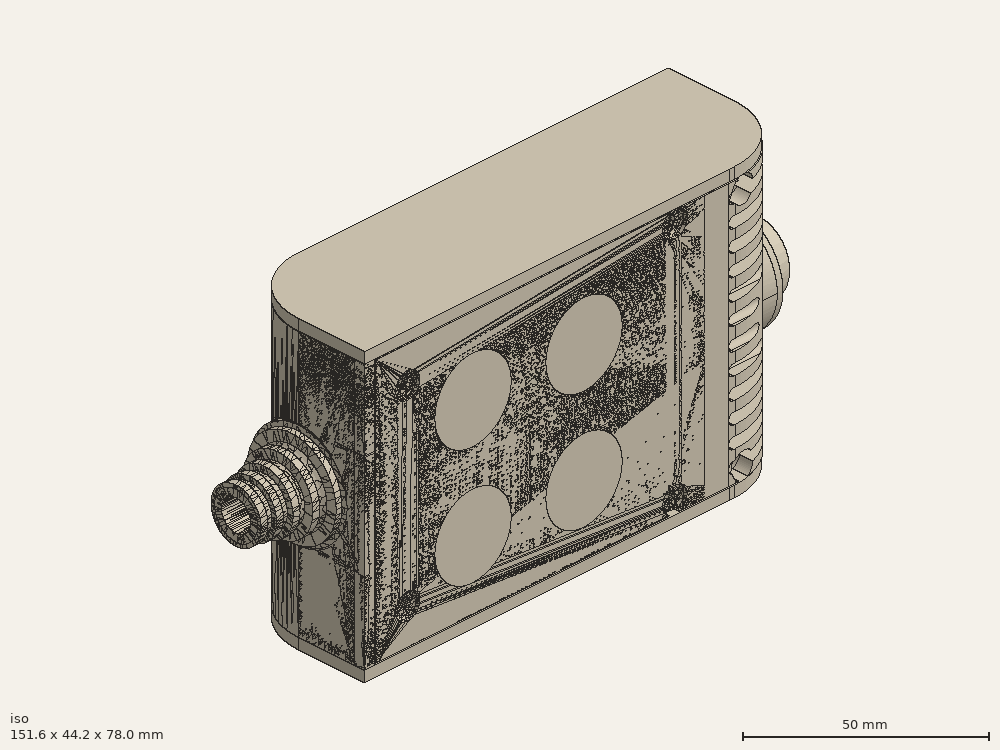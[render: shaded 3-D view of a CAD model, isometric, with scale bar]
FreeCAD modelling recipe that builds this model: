
FCSTD DOCUMENT  (FreeCAD 0.19R0.19.2)
Label: enclosure_177FCStd
License: All rights reserved
LicenseURL: http://en.wikipedia.org/wiki/All_rights_reserved
objects: Part::Revolution×152, Part::MultiFuse×146, Part::Feature×146, Sketcher::SketchObject×84, Part::Cut×70, Part::Cylinder×70, Part::Extrusion×67, Part::Fillet×58, Part::Box×36, App::MeasureDistance×4, PartDesign::Body×2, Image::ImagePlane×1
note: 831 computed .brp shape members not serialized (recipe doc carries the construction recipe); baked Part::Feature solids carry a one-line shape summary decoded from their .brp

FEATURE [Sketcher::SketchObject] Sketch  label="topSketch"
  FullyConstrained = true
  sketch-geometry (20):
    g0: LineSegment StartX=5.21097e-06 StartY=3 StartZ=0 EndX=5.21097e-06 EndY=19 EndZ=0
    g1: ArcOfCircle CenterX=19 CenterY=19 CenterZ=0 NormalX=0 NormalY=0 NormalZ=1 AngleXU=0 Radius=19 StartAngle=1.5708 EndAngle=3.14159
    g2: ArcOfCircle CenterX=19 CenterY=19 CenterZ=0 NormalX=0 NormalY=0 NormalZ=1 AngleXU=0 Radius=16 StartAngle=1.5708 EndAngle=3.14159
    g3: LineSegment StartX=114 StartY=35 StartZ=0 EndX=19 EndY=35 EndZ=0
    g4: LineSegment StartX=5.21097e-06 StartY=3 StartZ=0 EndX=5.21097e-06 EndY=0 EndZ=0
    g5: LineSegment StartX=3 StartY=0 StartZ=0 EndX=5.21097e-06 EndY=0 EndZ=0
    g6: LineSegment StartX=3 StartY=19 StartZ=0 EndX=3 EndY=0 EndZ=0
    g7: LineSegment StartX=19 StartY=38 StartZ=0 EndX=124 EndY=38 EndZ=0
    g8: Circle CenterX=119 CenterY=35 CenterZ=0 NormalX=0 NormalY=0 NormalZ=1 AngleXU=0 Radius=1
    g9: Circle CenterX=121 CenterY=35 CenterZ=0 NormalX=0 NormalY=0 NormalZ=1 AngleXU=0 Radius=1
    g10: Circle CenterX=121 CenterY=33 CenterZ=0 NormalX=0 NormalY=0 NormalZ=1 AngleXU=0 Radius=1
    g11: BSplineCurve PolesCount=3 KnotsCount=2 Degree=2 IsPeriodic=0
    g12: GeomPoint X=119 Y=35 Z=0
    g13: GeomPoint X=121 Y=33 Z=0
    g14: LineSegment StartX=119 StartY=35 StartZ=0 EndX=114 EndY=35 EndZ=0
    g15: ArcOfCircle CenterX=105 CenterY=19 CenterZ=0 NormalX=0 NormalY=0 NormalZ=1 AngleXU=0 Radius=19 StartAngle=5.7297 EndAngle=6.28319
    g16: ArcOfCircle CenterX=105 CenterY=19 CenterZ=0 NormalX=0 NormalY=0 NormalZ=1 AngleXU=0 Radius=16 StartAngle=5.60905 EndAngle=6.28319
    g17: LineSegment StartX=121 StartY=33 StartZ=0 EndX=121 EndY=19 EndZ=0
    g18: LineSegment StartX=124 StartY=38 StartZ=0 EndX=124 EndY=19 EndZ=0
    g19: LineSegment StartX=117.5 StartY=9.01251 StartZ=0 EndX=121.163 EndY=9.0125 EndZ=0
  constraints (46):
    c: Vertical(g0)
    c: Block(g0)
    c: Coincident(g1,g0)
    c: Block(g1)
    c: Coincident(g2,g1)
    c: Block(g2)
    c: Coincident(g3,g2)
    c: Horizontal(g3)
    c: Tangent(g3,g2)
    c: Coincident(g4,g0)
    c: Distance(g4) = 3
    c: Vertical(g4)
    c: Coincident(g5,g4)
    c: Horizontal(g5)
    c: Coincident(g6,g2)
    c: Coincident(g6,g5)
    c: Vertical(g6)
    c: Horizontal(g7)
    c: Distance(g7) = 105
    c: Coincident(g7,g1)
    c: Block(g3)
    c: Weight(g8) = 1
    c: Equal(g8,g9)
    c: Equal(g8,g10)
    c: InternalAlignment(g8,g11)
    c: InternalAlignment(g9,g11)
    c: InternalAlignment(g10,g11)
    c: InternalAlignment(g12,g11)
    c: InternalAlignment(g13,g11)
    c: Block(g11)
    c: Coincident(g14,g11)
    c: Coincident(g14,g3)
    c: Horizontal(g14)
    c: Block(g15)
    c: Coincident(g16,g15)
    c: Block(g16)
    c: Coincident(g17,g11)
    c: Coincident(g17,g16)
    c: Vertical(g17)
    c: Distance(g17) = 14
    c: Coincident(g18,g7)
    c: Coincident(g18,g15)
    c: Vertical(g18)
    c: Distance(g18) = 19
    c: Coincident(g19,g16)
    c: Coincident(g19,g15)
FEATURE [Sketcher::SketchObject] Sketch001  label="bottomSketch"
  FullyConstrained = true
  sketch-geometry (32):
    g0: LineSegment StartX=3.3 StartY=-6.03275e-07 StartZ=0 EndX=98 EndY=-6.03275e-07 EndZ=0
    g1: ArcOfCircle CenterX=98 CenterY=19 CenterZ=0 NormalX=0 NormalY=0 NormalZ=1 AngleXU=0 Radius=19 StartAngle=4.71239 EndAngle=5.71103
    g2: LineSegment StartX=6.3 StartY=8 StartZ=0 EndX=3.3 EndY=8 EndZ=0
    g3: LineSegment StartX=3.3 StartY=8 StartZ=0 EndX=3.3 EndY=-6.03275e-07 EndZ=0
    g4: ArcOfCircle CenterX=8.3 CenterY=5 CenterZ=0 NormalX=0 NormalY=0 NormalZ=1 AngleXU=0 Radius=2 StartAngle=3.14159 EndAngle=4.71239
    g5: LineSegment StartX=6.3 StartY=8 StartZ=0 EndX=6.3 EndY=5 EndZ=0
    g6: ArcOfCircle CenterX=98 CenterY=19 CenterZ=0 NormalX=0 NormalY=0 NormalZ=1 AngleXU=0 Radius=12.7 StartAngle=4.71239 EndAngle=6.28319
    g7: LineSegment StartX=94.7 StartY=3 StartZ=0 EndX=8.3 EndY=3 EndZ=0
    g8-g12: Circle x5 (B-spline internal-alignment scaffolding for g13; pole/knot coordinates omitted)
    g13: BSplineCurve PolesCount=5 KnotsCount=3 Degree=3 IsPeriodic=0
    g14: GeomPoint X=98 Y=6.3 Z=0
    g15: GeomPoint X=96.3938 Y=4.71946 Z=0
    g16: GeomPoint X=94.7 Y=3 Z=0
    g17-g23: Circle x7 (B-spline internal-alignment scaffolding for g24; pole/knot coordinates omitted)
    g24: BSplineCurve PolesCount=7 KnotsCount=5 Degree=3 IsPeriodic=0
    g25-g29: GeomPoint x5 (B-spline internal-alignment scaffolding for g24; pole/knot coordinates omitted)
    g30: ArcOfCircle CenterX=98 CenterY=19 CenterZ=0 NormalX=0 NormalY=0 NormalZ=1 AngleXU=0 Radius=15.7 StartAngle=5.81226 EndAngle=6.28319
    g31: LineSegment StartX=110.7 StartY=19 StartZ=0 EndX=113.7 EndY=19 EndZ=0
  constraints (41):
    c: Horizontal(g0)
    c: Coincident(g1,g0)
    c: Block(g1)
    c: Horizontal(g2)
    c: Distance(g2) = 3
    c: Coincident(g3,g2)
    c: Vertical(g3)
    c: Coincident(g3,g0)
    c: Block(g4)
    c: Block(g2)
    c: Coincident(g5,g2)
    c: Coincident(g5,g4)
    c: Vertical(g5)
    c: Coincident(g6,g1)
    c: Block(g6)
    c: Coincident(g7,g4)
    c: Horizontal(g7)
    c: Block(g0)
    c: Block(g7)
    c: Block(g3)
    c: Coincident(g13,g6)
    c: Weight(g8) = 1
    c: Equal(g8, g9-g12) x4
    c: Coincident(g13,g7)
    c: InternalAlignment(g8-g12 -> g13) x5
    c: InternalAlignment(g14,g13)
    c: InternalAlignment(g15,g13)
    c: InternalAlignment(g16,g13)
    c: Block(g13)
    c: Weight(g17) = 1
    c: Equal(g17, g18-g23) x6
    c: Coincident(g24,g1)
    c: InternalAlignment(g17-g23 -> g24) x7
    c: InternalAlignment(g25-g29 -> g24) x5
    c: Block(g24)
    c: Coincident(g30,g24)
    c: Coincident(g31,g6)
    c: Coincident(g31,g30)
    c: Horizontal(g31)
    c: Block(g31)
    c: Block(g30)
FEATURE [Part::Extrusion] Extrude  label="top"
  Base = -> Sketch
  Dir = (0,0,1)
  DirMode = 2
  FaceMakerClass = Part::FaceMakerBullseye
  LengthFwd = 72
  LengthRev = 0
  Solid = true
  Symmetric = false
FEATURE [Part::Extrusion] Extrude001  label="bottom"
  Base = -> Sketch001
  Dir = (0,0,1)
  DirMode = 2
  FaceMakerClass = Part::FaceMakerBullseye
  LengthFwd = 71.4
  LengthRev = 0
  Placement = pos=(0,0,0.3) rot=(0,0,1;0rad)
  Solid = true
  Symmetric = false
FEATURE [Sketcher::SketchObject] Sketch002  label="topSketch001"
  FullyConstrained = true
  sketch-geometry (8):
    g0: ArcOfCircle CenterX=19 CenterY=19.0975 CenterZ=0 NormalX=0 NormalY=0 NormalZ=1 AngleXU=0 Radius=18.9025 StartAngle=1.5708 EndAngle=3.14674
    g1: LineSegment StartX=0.0977805 StartY=19.0003 StartZ=0 EndX=0.0977805 EndY=0.000251602 EndZ=0
    g2: LineSegment StartX=19 StartY=38 StartZ=0 EndX=124 EndY=38 EndZ=0
    g3: LineSegment StartX=0.0977805 StartY=0.000251602 StartZ=0 EndX=105.098 EndY=0.000251602 EndZ=0
    g4: LineSegment StartX=124 StartY=38 StartZ=0 EndX=125.616 EndY=38 EndZ=0
    g5: LineSegment StartX=105.098 StartY=0.000251602 StartZ=0 EndX=106.713 EndY=0.000251602 EndZ=0
    g6: ArcOfCircle CenterX=106.616 CenterY=19 CenterZ=0 NormalX=0 NormalY=0 NormalZ=1 AngleXU=0 Radius=19 StartAngle=4.71754 EndAngle=6.28319
    g7: LineSegment StartX=125.616 StartY=38 StartZ=0 EndX=125.616 EndY=19 EndZ=0
  constraints (21):
    c: Block(g0)
    c: Coincident(g1,g0)
    c: Vertical(g1)
    c: Horizontal(g2)
    c: Distance(g2) = 105
    c: Coincident(g2,g0)
    c: Distance(g1) = 19
    c: Coincident(g3,g1)
    c: Horizontal(g3)
    c: Distance(g3) = 105
    c: Coincident(g4,g2)
    c: Horizontal(g4)
    c: Distance(g4) = 1.61553
    c: Horizontal(g5)
    c: Equal(g4,g5) = 1.61553
    c: Coincident(g5,g3)
    c: Block(g6)
    c: Coincident(g6,g5)
    c: Coincident(g7,g4)
    c: Coincident(g7,g6)
    c: Vertical(g7)
FEATURE [Part::Extrusion] Extrude002  label="sideA"
  Base = -> Sketch002
  Dir = (0,0,1)
  DirMode = 2
  FaceMakerClass = Part::FaceMakerBullseye
  LengthFwd = 3
  LengthRev = 0
  Placement = pos=(0,0,-3) rot=(0,0,1;0rad)
  Solid = true
  Symmetric = false
FEATURE [Sketcher::SketchObject] Sketch003  label="topSketch002"
  FullyConstrained = true
  sketch-geometry (6):
    g0: LineSegment StartX=19 StartY=38 StartZ=0 EndX=117 EndY=38 EndZ=0
    g1: ArcOfCircle CenterX=19 CenterY=19 CenterZ=0 NormalX=0 NormalY=0 NormalZ=1 AngleXU=0 Radius=19 StartAngle=1.5708 EndAngle=3.14159
    g2: LineSegment StartX=117 StartY=38 StartZ=0 EndX=117 EndY=19 EndZ=0
    g3: LineSegment StartX=98 StartY=1.0161e-12 StartZ=0 EndX=5.22862e-06 EndY=1.0161e-12 EndZ=0
    g4: LineSegment StartX=5.22862e-06 StartY=19 StartZ=0 EndX=5.22862e-06 EndY=1.0161e-12 EndZ=0
    g5: ArcOfCircle CenterX=98 CenterY=19 CenterZ=0 NormalX=0 NormalY=0 NormalZ=1 AngleXU=0 Radius=19 StartAngle=4.71239 EndAngle=6.28319
  constraints (16):
    c: Horizontal(g0)
    c: Distance(g0) = 98
    c: Coincident(g1,g0)
    c: Block(g1)
    c: Coincident(g2,g0)
    c: Vertical(g2)
    c: Distance(g2) = 19
    c: Horizontal(g3)
    c: Coincident(g4,g1)
    c: Vertical(g4)
    c: Coincident(g3,g4)
    c: Block(g3)
    c: Coincident(g5,g2)
    c: Coincident(g5,g3)
    c: Block(g0)
    c: Block(g5)
FEATURE [Sketcher::SketchObject] Sketch004
  FullyConstrained = true
  MapMode = 3
  Placement = pos=(0,0,0) rot=(1,0,0;1.5708rad)
  Support = -> [Extrude]
  sketch-geometry (8):
    g0: Circle CenterX=80.351 CenterY=-67.6202 CenterZ=0 NormalX=0 NormalY=0 NormalZ=1 AngleXU=0 Radius=2
    g1: Circle CenterX=80.351 CenterY=-67.6202 CenterZ=0 NormalX=0 NormalY=0 NormalZ=1 AngleXU=0 Radius=3
    g2: Circle CenterX=80.351 CenterY=-4.92017 CenterZ=0 NormalX=0 NormalY=0 NormalZ=1 AngleXU=0 Radius=2
    g3: Circle CenterX=80.351 CenterY=-4.92017 CenterZ=0 NormalX=0 NormalY=0 NormalZ=1 AngleXU=0 Radius=3
    g4: Circle CenterX=23.851 CenterY=-4.92017 CenterZ=0 NormalX=0 NormalY=0 NormalZ=1 AngleXU=0 Radius=2
    g5: Circle CenterX=23.851 CenterY=-4.92017 CenterZ=0 NormalX=0 NormalY=0 NormalZ=1 AngleXU=0 Radius=3
    g6: Circle CenterX=23.851 CenterY=-67.6202 CenterZ=0 NormalX=0 NormalY=0 NormalZ=1 AngleXU=0 Radius=2
    g7: Circle CenterX=23.851 CenterY=-67.6202 CenterZ=0 NormalX=0 NormalY=0 NormalZ=1 AngleXU=0 Radius=3
  constraints (8):
    c: Block(g3)
    c: Block(g2)
    c: Block(g1)
    c: Block(g0)
    c: Block(g6)
    c: Block(g7)
    c: Block(g4)
    c: Block(g5)
FEATURE [Part::Extrusion] Extrude004
  Base = -> Sketch004
  Dir = (0,-1,2e-16)
  DirMode = 2
  FaceMakerClass = Part::FaceMakerBullseye
  LengthFwd = 6
  LengthRev = 0
  Placement = pos=(0,9,0) rot=(0,0,1;0rad)
  Solid = true
  Symmetric = false
FEATURE [Sketcher::SketchObject] Sketch005
  FullyConstrained = true
  MapMode = 3
  Placement = pos=(0,0,0) rot=(1,0,0;1.5708rad)
  Support = -> [Extrude]
  sketch-geometry (8):
    g0: Circle CenterX=80.351 CenterY=-67.6202 CenterZ=0 NormalX=0 NormalY=0 NormalZ=1 AngleXU=0 Radius=3
    g1: Circle CenterX=80.351 CenterY=-4.92017 CenterZ=0 NormalX=0 NormalY=0 NormalZ=1 AngleXU=0 Radius=3
    g2: Circle CenterX=23.851 CenterY=-4.92017 CenterZ=0 NormalX=0 NormalY=0 NormalZ=1 AngleXU=0 Radius=3
    g3: Circle CenterX=23.851 CenterY=-67.6202 CenterZ=0 NormalX=0 NormalY=0 NormalZ=1 AngleXU=0 Radius=3
    g4: Circle CenterX=23.851 CenterY=-67.6202 CenterZ=0 NormalX=0 NormalY=0 NormalZ=1 AngleXU=0 Radius=5
    g5: Circle CenterX=80.351 CenterY=-67.6202 CenterZ=0 NormalX=0 NormalY=0 NormalZ=1 AngleXU=0 Radius=5
    g6: Circle CenterX=23.851 CenterY=-4.92017 CenterZ=0 NormalX=0 NormalY=0 NormalZ=1 AngleXU=0 Radius=5
    g7: Circle CenterX=80.351 CenterY=-4.92017 CenterZ=0 NormalX=0 NormalY=0 NormalZ=1 AngleXU=0 Radius=5
  constraints (8):
    c: Block(g1)
    c: Block(g0)
    c: Block(g3)
    c: Block(g2)
    c: Block(g5)
    c: Block(g4)
    c: Block(g6)
    c: Block(g7)
FEATURE [Part::Extrusion] Extrude005
  Base = -> Sketch005
  Dir = (0,-1,2e-16)
  DirMode = 2
  FaceMakerClass = Part::FaceMakerBullseye
  LengthFwd = 2
  LengthRev = 0
  Solid = true
  Symmetric = false
FEATURE [Sketcher::SketchObject] Sketch006
  FullyConstrained = true
  MapMode = 3
  Placement = pos=(0,0,0) rot=(1,0,0;1.5708rad)
  sketch-geometry (8):
    g0: Circle CenterX=80.351 CenterY=-67.6202 CenterZ=0 NormalX=0 NormalY=0 NormalZ=1 AngleXU=0 Radius=3
    g1: Circle CenterX=80.351 CenterY=-4.92017 CenterZ=0 NormalX=0 NormalY=0 NormalZ=1 AngleXU=0 Radius=3
    g2: Circle CenterX=23.851 CenterY=-4.92017 CenterZ=0 NormalX=0 NormalY=0 NormalZ=1 AngleXU=0 Radius=3
    g3: Circle CenterX=23.851 CenterY=-67.6202 CenterZ=0 NormalX=0 NormalY=0 NormalZ=1 AngleXU=0 Radius=3
    g4: Circle CenterX=23.851 CenterY=-67.6202 CenterZ=0 NormalX=0 NormalY=0 NormalZ=1 AngleXU=0 Radius=5
    g5: Circle CenterX=80.351 CenterY=-67.6202 CenterZ=0 NormalX=0 NormalY=0 NormalZ=1 AngleXU=0 Radius=5
    g6: Circle CenterX=23.851 CenterY=-4.92017 CenterZ=0 NormalX=0 NormalY=0 NormalZ=1 AngleXU=0 Radius=5
    g7: Circle CenterX=80.351 CenterY=-4.92017 CenterZ=0 NormalX=0 NormalY=0 NormalZ=1 AngleXU=0 Radius=5
  constraints (8):
    c: Block(g1)
    c: Block(g0)
    c: Block(g3)
    c: Block(g2)
    c: Block(g5)
    c: Block(g4)
    c: Block(g6)
    c: Block(g7)
FEATURE [Part::Extrusion] Extrude007
  Base = -> Sketch006
  Dir = (0,-1,2e-16)
  DirMode = 2
  FaceMakerClass = Part::FaceMakerBullseye
  LengthFwd = 2
  LengthRev = 0
  Solid = true
  Symmetric = false
FEATURE [Part::Fillet] Fillet
  Base = -> Extrude007
  Edges = 4 edges r=1.99: [Edge6,Edge12,Edge18,Edge24]
FEATURE [Part::Cut] Cut
  Base = -> Extrude005
  Placement = pos=(0,5,0) rot=(0,0,1;0rad)
  Tool = -> Fillet
FEATURE [Part::MultiFuse] Fusion  label="pCBScrews"
  Placement = pos=(-2.5,0,72.3) rot=(0,0,1;0rad)
  Shapes = -> [Extrude004,Cut]
FEATURE [App::MeasureDistance] Distance  label="Distance: 0.69 mm"
  Distance = 0.685967
  P1 = (24.0138,2.9647,0.3)
  P2 = (23.8901,3,-0.373787)
FEATURE [App::MeasureDistance] Distance001  label="Distance: 0.53 mm"
  Distance = 0.533607
  P1 = (80.2939,3,72.2334)
  P2 = (80.281,2.99661,71.7)
FEATURE [Part::Fillet] Fillet001
  Base = -> Extrude001
  Edges = 1 edges r=2.4: [Edge17]
FEATURE [Part::Fillet] Fillet002  label="bottom001"
  Base = -> Fillet001
  Edges = 1 edges r=2.4: [Edge36]
FEATURE [Part::Fillet] Fillet003  label="top001"
  Base = -> Extrude
  Edges = 1 edges r=2: [Edge1]
FEATURE [Sketcher::SketchObject] Sketch007
  FullyConstrained = true
  sketch-geometry (16):
    g0: LineSegment StartX=4 StartY=0 StartZ=0 EndX=4 EndY=2.4 EndZ=0
    g1: LineSegment StartX=4 StartY=2.4 StartZ=0 EndX=7 EndY=2.4 EndZ=0
    g2: LineSegment StartX=4 StartY=0 StartZ=0 EndX=5.7 EndY=0 EndZ=0
    g3: LineSegment StartX=5.7 StartY=0 StartZ=0 EndX=5.7 EndY=-5.6 EndZ=0
    g4-g8: Circle x5 (B-spline internal-alignment scaffolding for g9; pole/knot coordinates omitted)
    g9: BSplineCurve PolesCount=5 KnotsCount=3 Degree=3 IsPeriodic=0
    g10: GeomPoint X=7 Y=2.4 Z=0
    g11: GeomPoint X=10.4582 Y=-1.55472 Z=0
    g12: GeomPoint X=14 Y=-5.6 Z=0
    g13: LineSegment StartX=14 StartY=-5.6 StartZ=0 EndX=14 EndY=-14.1 EndZ=0
    g14: LineSegment StartX=14 StartY=-14.1 StartZ=0 EndX=6.5 EndY=-14.1 EndZ=0
    g15: LineSegment StartX=5.7 StartY=-5.6 StartZ=0 EndX=6.5 EndY=-14.1 EndZ=0
  constraints (28):
    c: Distance(g0) = 2.4
    c: Vertical(g0)
    c: Block(g0)
    c: Coincident(g1,g0)
    c: Horizontal(g1)
    c: Distance(g1) = 3
    c: Coincident(g2,g0)
    c: Horizontal(g2)
    c: Distance(g2) = 1.7
    c: Coincident(g3,g2)
    c: Vertical(g3)
    c: Distance(g3) = 5.6
    c: Coincident(g9,g1)
    c: Weight(g4) = 1
    c: Equal(g4, g5-g8) x4
    c: InternalAlignment(g4-g8 -> g9) x5
    c: InternalAlignment(g10,g9)
    c: InternalAlignment(g11,g9)
    c: InternalAlignment(g12,g9)
    c: Block(g9)
    c: Coincident(g13,g9)
    c: Vertical(g13)
    c: Distance(g13) = 8.5
    c: Coincident(g14,g13)
    c: Horizontal(g14)
    c: Distance(g14) = 7.5
    c: Coincident(g15,g3)
    c: Coincident(g15,g14)
FEATURE [Part::Feature] Face
  shape: bbox 10 x 16.5 x 2e-07 mm, 1 faces, 0 solids (baked)
FEATURE [Part::Revolution] Revolve  label="plugHousing"
  Angle = 360
  Axis = (0,1,0)
  Base = (0,0,0)
  FaceMakerClass = Part::FaceMakerBullseye
  Placement = pos=(0,0,36.15) rot=(0,0,1;0rad)
  Solid = false
  Source = -> Face
  Symmetric = false
FEATURE [Part::Feature] Face001
  shape: bbox 10 x 16.5 x 2e-07 mm, 1 faces, 0 solids (baked)
FEATURE [Part::Revolution] Revolve001  label="plugHousing001"
  Angle = 360
  Axis = (0,1,0)
  Base = (0,0,0)
  FaceMakerClass = Part::FaceMakerBullseye
  Placement = pos=(0,0,36.15) rot=(0,0,1;0rad)
  Solid = false
  Source = -> Face001
  Symmetric = false
FEATURE [Part::MultiFuse] Fusion001  label="plugHousing002"
  Placement = pos=(0,0,0) rot=(0,0,1;1.5708rad)
  Shapes = -> [Revolve001,Revolve]
FEATURE [Part::Feature] Face002
  shape: bbox 10 x 16.5 x 2e-07 mm, 1 faces, 0 solids (baked)
FEATURE [Part::Revolution] Revolve003  label="plugHousing005"
  Angle = 360
  Axis = (0,1,0)
  Base = (0,0,0)
  FaceMakerClass = Part::FaceMakerBullseye
  Placement = pos=(0,0,36.15) rot=(0,0,1;0rad)
  Solid = false
  Source = -> Face002
  Symmetric = false
FEATURE [Part::Feature] Face003
  shape: bbox 10 x 16.5 x 2e-07 mm, 1 faces, 0 solids (baked)
FEATURE [Part::Revolution] Revolve002  label="plugHousing003"
  Angle = 360
  Axis = (0,1,0)
  Base = (0,0,0)
  FaceMakerClass = Part::FaceMakerBullseye
  Placement = pos=(0,0,36.15) rot=(0,0,1;0rad)
  Solid = false
  Source = -> Face003
  Symmetric = false
FEATURE [Part::MultiFuse] Fusion002  label="plugHousing004"
  Placement = pos=(0,0,0) rot=(0,0,1;1.5708rad)
  Shapes = -> [Revolve002,Revolve003]
FEATURE [Part::MultiFuse] Fusion003  label="plugHousing006"
  Placement = pos=(0,19,0) rot=(0,0,1;3.14159rad)
  Shapes = -> [Fusion002,Fusion001]
FEATURE [Part::Feature] Face004
  shape: bbox 10 x 16.5 x 2e-07 mm, 1 faces, 0 solids (baked)
FEATURE [Part::Revolution] Revolve006  label="plugHousing010"
  Angle = 360
  Axis = (0,1,0)
  Base = (0,0,0)
  FaceMakerClass = Part::FaceMakerBullseye
  Placement = pos=(0,0,36.15) rot=(0,0,1;0rad)
  Solid = false
  Source = -> Face004
  Symmetric = false
FEATURE [Part::Feature] Face005
  shape: bbox 10 x 16.5 x 2e-07 mm, 1 faces, 0 solids (baked)
FEATURE [Part::Revolution] Revolve007  label="plugHousing011"
  Angle = 360
  Axis = (0,1,0)
  Base = (0,0,0)
  FaceMakerClass = Part::FaceMakerBullseye
  Placement = pos=(0,0,36.15) rot=(0,0,1;0rad)
  Solid = false
  Source = -> Face005
  Symmetric = false
FEATURE [Part::Feature] Face006
  shape: bbox 10 x 16.5 x 2e-07 mm, 1 faces, 0 solids (baked)
FEATURE [Part::Revolution] Revolve004  label="plugHousing007"
  Angle = 360
  Axis = (0,1,0)
  Base = (0,0,0)
  FaceMakerClass = Part::FaceMakerBullseye
  Placement = pos=(0,0,36.15) rot=(0,0,1;0rad)
  Solid = false
  Source = -> Face006
  Symmetric = false
FEATURE [Part::MultiFuse] Fusion004  label="plugHousing009"
  Placement = pos=(0,0,0) rot=(0,0,1;1.5708rad)
  Shapes = -> [Revolve004,Revolve007]
FEATURE [Part::Feature] Face007
  shape: bbox 10 x 16.5 x 2e-07 mm, 1 faces, 0 solids (baked)
FEATURE [Part::Revolution] Revolve005  label="plugHousing008"
  Angle = 360
  Axis = (0,1,0)
  Base = (0,0,0)
  FaceMakerClass = Part::FaceMakerBullseye
  Placement = pos=(0,0,36.15) rot=(0,0,1;0rad)
  Solid = false
  Source = -> Face007
  Symmetric = false
FEATURE [Part::MultiFuse] Fusion005  label="plugHousing012"
  Placement = pos=(0,0,0) rot=(0,0,1;1.5708rad)
  Shapes = -> [Revolve006,Revolve005]
FEATURE [Part::MultiFuse] Fusion006  label="plugHousing013"
  Placement = pos=(0,19,0) rot=(0,0,1;3.14159rad)
  Shapes = -> [Fusion005,Fusion004]
FEATURE [Part::MultiFuse] Fusion007  label="plugHousing014"
  Placement = pos=(122.621,0,-0.15) rot=(0,0,1;0rad)
  Shapes = -> [Fusion003,Fusion006]
FEATURE [Part::Cylinder] Cylinder002
  Angle = 360
  AttacherType = Attacher::AttachEngine3D
  Height = 20
  Placement = pos=(0,0,36.15) rot=(0,0,1;0rad)
  Radius = 4
FEATURE [Part::Cylinder] Cylinder003
  Angle = 360
  AttacherType = Attacher::AttachEngine3D
  Height = 10
  Placement = pos=(0,0,36.15) rot=(0,0,1;0rad)
  Radius = 4
FEATURE [Part::MultiFuse] Fusion009  label="removeToCreateHoleForPlugHousing"
  Placement = pos=(70,19,36.15) rot=(0,1,0;1.5708rad)
  Shapes = -> [Cylinder002,Cylinder003]
FEATURE [Part::Cylinder] Cylinder004
  Angle = 360
  AttacherType = Attacher::AttachEngine3D
  Height = 20
  Placement = pos=(0,0,36.15) rot=(0,0,1;0rad)
  Radius = 4
FEATURE [Part::Cylinder] Cylinder005
  Angle = 360
  AttacherType = Attacher::AttachEngine3D
  Height = 10
  Placement = pos=(0,0,36.15) rot=(0,0,1;0rad)
  Radius = 4
FEATURE [Part::MultiFuse] Fusion010  label="removeToCreateHoleForPlugHousing001"
  Placement = pos=(70,19,36.15) rot=(0,1,0;1.5708rad)
  Shapes = -> [Cylinder004,Cylinder005]
FEATURE [Part::Cut] Cut001
  Base = -> Fillet003
  Tool = -> Fusion010
FEATURE [Part::Cut] Cut002  label="Bottom"
  Base = -> Fillet002
  Tool = -> Fusion009
FEATURE [Part::Feature] Face008
  shape: bbox 10 x 16.5 x 2e-07 mm, 1 faces, 0 solids (baked)
FEATURE [Part::Revolution] Revolve011  label="plugHousing021"
  Angle = 360
  Axis = (0,1,0)
  Base = (0,0,0)
  FaceMakerClass = Part::FaceMakerBullseye
  Placement = pos=(0,0,36.15) rot=(0,0,1;0rad)
  Solid = false
  Source = -> Face008
  Symmetric = false
FEATURE [Part::Feature] Face009
  shape: bbox 10 x 16.5 x 2e-07 mm, 1 faces, 0 solids (baked)
FEATURE [Part::Revolution] Revolve012  label="plugHousing022"
  Angle = 360
  Axis = (0,1,0)
  Base = (0,0,0)
  FaceMakerClass = Part::FaceMakerBullseye
  Placement = pos=(0,0,36.15) rot=(0,0,1;0rad)
  Solid = false
  Source = -> Face009
  Symmetric = false
FEATURE [Part::Feature] Face010 .. Face013  x4 (patterned run collapsed; names and placements below)
  shape: bbox 10 x 16.5 x 2e-07 mm, 1 faces, 0 solids (baked)
FEATURE [Part::Revolution] Revolve015  label="plugHousing027"
  Angle = 360
  Axis = (0,1,0)
  Base = (0,0,0)
  FaceMakerClass = Part::FaceMakerBullseye
  Placement = pos=(0,0,36.15) rot=(0,0,1;0rad)
  Solid = false
  Source = -> Face013
  Symmetric = false
FEATURE [Part::Feature] Face014
  shape: bbox 10 x 16.5 x 2e-07 mm, 1 faces, 0 solids (baked)
FEATURE [Part::Feature] Face015
  shape: bbox 10 x 16.5 x 2e-07 mm, 1 faces, 0 solids (baked)
FEATURE [Part::Feature] Face016
  shape: bbox 10 x 16.5 x 2e-07 mm, 1 faces, 0 solids (baked)
FEATURE [Part::Revolution] Revolve019  label="plugHousing033"
  Angle = 360
  Axis = (0,1,0)
  Base = (0,0,0)
  FaceMakerClass = Part::FaceMakerBullseye
  Placement = pos=(0,0,36.15) rot=(0,0,1;0rad)
  Solid = false
  Source = -> Face016
  Symmetric = false
FEATURE [Part::Feature] Face017
  shape: bbox 10 x 16.5 x 2e-07 mm, 1 faces, 0 solids (baked)
FEATURE [Part::Revolution] Revolve020  label="plugHousing034"
  Angle = 360
  Axis = (0,1,0)
  Base = (0,0,0)
  FaceMakerClass = Part::FaceMakerBullseye
  Placement = pos=(0,0,36.15) rot=(0,0,1;0rad)
  Solid = false
  Source = -> Face017
  Symmetric = false
FEATURE [Part::Feature] Face018
  shape: bbox 10 x 16.5 x 2e-07 mm, 1 faces, 0 solids (baked)
FEATURE [Part::Revolution] Revolve016  label="plugHousing030"
  Angle = 360
  Axis = (0,1,0)
  Base = (0,0,0)
  FaceMakerClass = Part::FaceMakerBullseye
  Placement = pos=(0,0,36.15) rot=(0,0,1;0rad)
  Solid = false
  Source = -> Face018
  Symmetric = false
FEATURE [Part::MultiFuse] Fusion020  label="plugHousing038"
  Placement = pos=(0,0,0) rot=(0,0,1;1.5708rad)
  Shapes = -> [Revolve016,Revolve020]
FEATURE [Part::Feature] Face019
  shape: bbox 10 x 16.5 x 2e-07 mm, 1 faces, 0 solids (baked)
FEATURE [Part::Feature] Face020
  shape: bbox 10 x 16.5 x 2e-07 mm, 1 faces, 0 solids (baked)
FEATURE [Part::Revolution] Revolve017  label="plugHousing031"
  Angle = 360
  Axis = (0,1,0)
  Base = (0,0,0)
  FaceMakerClass = Part::FaceMakerBullseye
  Placement = pos=(0,0,36.15) rot=(0,0,1;0rad)
  Solid = false
  Source = -> Face020
  Symmetric = false
FEATURE [Part::MultiFuse] Fusion021  label="plugHousing039"
  Placement = pos=(0,0,0) rot=(0,0,1;1.5708rad)
  Shapes = -> [Revolve019,Revolve017]
FEATURE [Part::MultiFuse] Fusion023  label="plugHousing041"
  Placement = pos=(0,19,0) rot=(0,0,1;3.14159rad)
  Shapes = -> [Fusion021,Fusion020]
FEATURE [Part::Revolution] Revolve022  label="plugHousing043"
  Angle = 360
  Axis = (0,1,0)
  Base = (0,0,0)
  FaceMakerClass = Part::FaceMakerBullseye
  Placement = pos=(0,0,36.15) rot=(0,0,1;0rad)
  Solid = false
  Source = -> Face019
  Symmetric = false
FEATURE [Part::Feature] Face021
  shape: bbox 10 x 16.5 x 2e-07 mm, 1 faces, 0 solids (baked)
FEATURE [Part::Revolution] Revolve023  label="plugHousing044"
  Angle = 360
  Axis = (0,1,0)
  Base = (0,0,0)
  FaceMakerClass = Part::FaceMakerBullseye
  Placement = pos=(0,0,36.15) rot=(0,0,1;0rad)
  Solid = false
  Source = -> Face021
  Symmetric = false
FEATURE [Part::Feature] Face022
  shape: bbox 10 x 16.5 x 2e-07 mm, 1 faces, 0 solids (baked)
FEATURE [Part::Revolution] Revolve018  label="plugHousing032"
  Angle = 360
  Axis = (0,1,0)
  Base = (0,0,0)
  FaceMakerClass = Part::FaceMakerBullseye
  Placement = pos=(0,0,36.15) rot=(0,0,1;0rad)
  Solid = false
  Source = -> Face022
  Symmetric = false
FEATURE [Part::MultiFuse] Fusion022  label="plugHousing040"
  Placement = pos=(0,0,0) rot=(0,0,1;1.5708rad)
  Shapes = -> [Revolve018,Revolve023]
FEATURE [Part::Feature] Face023
  shape: bbox 10 x 16.5 x 2e-07 mm, 1 faces, 0 solids (baked)
FEATURE [Part::Revolution] Revolve021  label="plugHousing035"
  Angle = 360
  Axis = (0,1,0)
  Base = (0,0,0)
  FaceMakerClass = Part::FaceMakerBullseye
  Placement = pos=(0,0,36.15) rot=(0,0,1;0rad)
  Solid = false
  Source = -> Face023
  Symmetric = false
FEATURE [Part::MultiFuse] Fusion018  label="plugHousing036"
  Placement = pos=(0,0,0) rot=(0,0,1;1.5708rad)
  Shapes = -> [Revolve022,Revolve021]
FEATURE [Part::MultiFuse] Fusion019  label="plugHousing037"
  Placement = pos=(0,19,0) rot=(0,0,1;3.14159rad)
  Shapes = -> [Fusion018,Fusion022]
FEATURE [Part::MultiFuse] Fusion024  label="plugHousing042"
  Placement = pos=(122.621,0,-0.15) rot=(0,0,1;0rad)
  Shapes = -> [Fusion023,Fusion019]
FEATURE [Part::Cylinder] Cylinder006
  Angle = 360
  AttacherType = Attacher::AttachEngine3D
  Height = 20
  Placement = pos=(0,0,36.15) rot=(0,0,1;0rad)
  Radius = 14.3
FEATURE [Part::Cylinder] Cylinder007
  Angle = 360
  AttacherType = Attacher::AttachEngine3D
  Height = 10
  Placement = pos=(0,0,36.15) rot=(0,0,1;0rad)
  Radius = 4
FEATURE [Part::MultiFuse] Fusion026  label="removeToCreteHoleForPlugHousing"
  Placement = pos=(70,19,36) rot=(0,1,0;1.5708rad)
  Shapes = -> [Cylinder006,Cylinder007]
FEATURE [Part::Box] Box001  label="Cube001"
  AttacherType = Attacher::AttachEngine3D
  Height = 28
  Length = 3
  Placement = pos=(110.7,19,22) rot=(0,0,1;0rad)
  Width = 15.7
FEATURE [Part::Cut] Cut003  label="top002"
  Base = -> Cut001
  Tool = -> Fusion007
FEATURE [Part::Revolution] Revolve008  label="plugHousing015"
  Angle = 360
  Axis = (0,1,0)
  Base = (0,0,0)
  FaceMakerClass = Part::FaceMakerBullseye
  Placement = pos=(0,0,36.15) rot=(0,0,1;0rad)
  Solid = false
  Source = -> Face010
  Symmetric = false
FEATURE [Part::MultiFuse] Fusion013  label="plugHousing020"
  Placement = pos=(0,0,0) rot=(0,0,1;1.5708rad)
  Shapes = -> [Revolve008,Revolve012]
FEATURE [Part::Cut] Cut004  label="top003"
  Base = -> Cut003
  Placement = pos=(1,0,0) rot=(0,0,1;0rad)
  Tool = -> Fusion026
FEATURE [Part::Cylinder] Cylinder008
  Angle = 360
  AttacherType = Attacher::AttachEngine3D
  Height = 20
  Placement = pos=(0,0,36.15) rot=(0,0,1;0rad)
  Radius = 10.3
FEATURE [Part::Cylinder] Cylinder009
  Angle = 360
  AttacherType = Attacher::AttachEngine3D
  Height = 10
  Placement = pos=(0,0,36.15) rot=(0,0,1;0rad)
  Radius = 4
FEATURE [Part::MultiFuse] Fusion027  label="removeToCreteHoleForPlugHousing001"
  Placement = pos=(70,19,36) rot=(0,1,0;1.5708rad)
  Shapes = -> [Cylinder008,Cylinder009]
FEATURE [Part::Cut] Cut005  label="plugHousingTab"
  Base = -> Box001
  Tool = -> Fusion027
FEATURE [Part::MultiFuse] Fusion028  label="plugHousing045"
  Shapes = -> [Fusion024,Cut005]
FEATURE [Part::Box] Box002  label="Cube002"
  AttacherType = Attacher::AttachEngine3D
  Height = 28.8
  Length = 3
  Placement = pos=(107.3,28,21.6) rot=(0,0,1;0rad)
  Width = 7
FEATURE [Part::Box] Box003  label="Cube003"
  AttacherType = Attacher::AttachEngine3D
  Height = 3
  Length = 6.4
  Placement = pos=(107.3,28,18.6) rot=(0,0,1;0rad)
  Width = 7
FEATURE [Part::Box] Box004  label="Cube004"
  AttacherType = Attacher::AttachEngine3D
  Height = 3
  Length = 6.4
  Placement = pos=(107.3,28,50.4) rot=(0,0,1;0rad)
  Width = 7
FEATURE [Part::MultiFuse] Fusion029  label="plugHousingBracketHolder"
  Shapes = -> [Box004,Box002,Box003]
FEATURE [Part::Cylinder] Cylinder010
  Angle = 360
  AttacherType = Attacher::AttachEngine3D
  Height = 20
  Placement = pos=(0,0,36.15) rot=(0,0,1;0rad)
  Radius = 14.3
FEATURE [Part::Cylinder] Cylinder011
  Angle = 360
  AttacherType = Attacher::AttachEngine3D
  Height = 10
  Placement = pos=(0,0,36.15) rot=(0,0,1;0rad)
  Radius = 4
FEATURE [Part::MultiFuse] Fusion030  label="removeToCreteHoleForPlugHousing002"
  Placement = pos=(70,19,36) rot=(0,1,0;1.5708rad)
  Shapes = -> [Cylinder010,Cylinder011]
FEATURE [Part::Cut] Cut006  label="plugHousingBracketHolder001"
  Base = -> Fusion029
  Tool = -> Fusion030
FEATURE [Part::Cylinder] Cylinder012
  Angle = 360
  AttacherType = Attacher::AttachEngine3D
  Height = 20
  Placement = pos=(0,0,36.15) rot=(0,0,1;0rad)
  Radius = 7
FEATURE [Part::Cylinder] Cylinder013
  Angle = 360
  AttacherType = Attacher::AttachEngine3D
  Height = 10
  Placement = pos=(0,0,36.15) rot=(0,0,1;0rad)
  Radius = 4
FEATURE [Part::MultiFuse] Fusion032  label="removeToCreteHoleForPlugHousing003"
  Placement = pos=(70,19,36) rot=(0,1,0;1.5708rad)
  Shapes = -> [Cylinder012,Cylinder013]
FEATURE [Part::Cut] Cut007  label="bottom002"
  Base = -> Cut002
  Tool = -> Fusion032
FEATURE [Sketcher::SketchObject] Sketch008
  FullyConstrained = true
  sketch-geometry (54):
    g0: LineSegment StartX=-4.2 StartY=0 StartZ=0 EndX=-6.2 EndY=0 EndZ=0
    g1: LineSegment StartX=-14 StartY=-18 StartZ=0 EndX=-14 EndY=-26.5 EndZ=0
    g2: LineSegment StartX=-4.2 StartY=0 StartZ=0 EndX=-4.2 EndY=-13.4877 EndZ=0
    g3: Circle CenterX=-4.2 CenterY=-13.4877 CenterZ=0 NormalX=0 NormalY=0 NormalZ=1 AngleXU=0 Radius=1
    g4: Circle CenterX=-4.2 CenterY=-26.5 CenterZ=0 NormalX=0 NormalY=0 NormalZ=1 AngleXU=0 Radius=1
    g5: Circle CenterX=-8.2 CenterY=-26.5 CenterZ=0 NormalX=0 NormalY=0 NormalZ=1 AngleXU=0 Radius=1
    g6: BSplineCurve PolesCount=3 KnotsCount=2 Degree=2 IsPeriodic=0
    g7: GeomPoint X=-4.2 Y=-13.4877 Z=0
    g8: GeomPoint X=-8.2 Y=-26.5 Z=0
    g9: LineSegment StartX=-14 StartY=-26.5 StartZ=0 EndX=-8.2 EndY=-26.5 EndZ=0
    g10: LineSegment StartX=-10.15 StartY=-12 StartZ=0 EndX=-10.15 EndY=-14 EndZ=0
    g11: LineSegment StartX=-12.8401 StartY=-16 StartZ=0 EndX=-10.1571 EndY=-16 EndZ=0
    g12: LineSegment StartX=-10.15 StartY=-14 StartZ=0 EndX=-8.70761 EndY=-14 EndZ=0
    g13: LineSegment StartX=-12.8401 StartY=-16 StartZ=0 EndX=-12.8401 EndY=-17.6958 EndZ=0
    g14: LineSegment StartX=-10.15 StartY=-12 StartZ=0 EndX=-7.79258 EndY=-12 EndZ=0
    g15: Circle CenterX=-6.2215 CenterY=-2 CenterZ=0 NormalX=0 NormalY=0 NormalZ=1 AngleXU=0 Radius=1
    g16: Circle CenterX=-6.22762 CenterY=-2.58724 CenterZ=0 NormalX=0 NormalY=0 NormalZ=1 AngleXU=0 Radius=1
    g17: Circle CenterX=-6.32538 CenterY=-4 CenterZ=0 NormalX=0 NormalY=0 NormalZ=1 AngleXU=0 Radius=1
    g18: BSplineCurve PolesCount=3 KnotsCount=2 Degree=2 IsPeriodic=0
    g19: GeomPoint X=-6.2215 Y=-2 Z=0
    g20: GeomPoint X=-6.32538 Y=-4 Z=0
    g21: Circle CenterX=-6.48644 CenterY=-5.99526 CenterZ=0 NormalX=0 NormalY=0 NormalZ=1 AngleXU=0 Radius=1
    g22: Circle CenterX=-6.58486 CenterY=-6.99526 CenterZ=0 NormalX=0 NormalY=0 NormalZ=1 AngleXU=0 Radius=1
    g23: Circle CenterX=-6.77343 CenterY=-8 CenterZ=0 NormalX=0 NormalY=0 NormalZ=1 AngleXU=0 Radius=1
    g24: BSplineCurve PolesCount=3 KnotsCount=2 Degree=2 IsPeriodic=0
    g25: GeomPoint X=-6.48644 Y=-5.99526 Z=0
    g26: GeomPoint X=-6.77343 Y=-8 Z=0
    g27: Circle CenterX=-7.19003 CenterY=-10 CenterZ=0 NormalX=0 NormalY=0 NormalZ=1 AngleXU=0 Radius=1
    g28: Circle CenterX=-7.44407 CenterY=-11.0915 CenterZ=0 NormalX=0 NormalY=0 NormalZ=1 AngleXU=0 Radius=1
    g29: Circle CenterX=-7.79258 CenterY=-12 CenterZ=0 NormalX=0 NormalY=0 NormalZ=1 AngleXU=0 Radius=1
    g30: BSplineCurve PolesCount=3 KnotsCount=2 Degree=2 IsPeriodic=0
    g31: GeomPoint X=-7.19003 Y=-10 Z=0
    g32: GeomPoint X=-7.79258 Y=-12 Z=0
    g33: Circle CenterX=-8.70761 CenterY=-14 CenterZ=0 NormalX=0 NormalY=0 NormalZ=1 AngleXU=0 Radius=1
    g34: Circle CenterX=-9.33087 CenterY=-15.1837 CenterZ=0 NormalX=0 NormalY=0 NormalZ=1 AngleXU=0 Radius=1
    g35: Circle CenterX=-10.1571 CenterY=-16 CenterZ=0 NormalX=0 NormalY=0 NormalZ=1 AngleXU=0 Radius=1
    g36: BSplineCurve PolesCount=3 KnotsCount=2 Degree=2 IsPeriodic=0
    g37: GeomPoint X=-8.70761 Y=-14 Z=0
    g38: GeomPoint X=-10.1571 Y=-16 Z=0
    g39: Circle CenterX=-12.8401 CenterY=-17.6958 CenterZ=0 NormalX=0 NormalY=0 NormalZ=1 AngleXU=0 Radius=1
    g40: Circle CenterX=-13.3521 CenterY=-17.9027 CenterZ=0 NormalX=0 NormalY=0 NormalZ=1 AngleXU=0 Radius=1
    g41: Circle CenterX=-14 CenterY=-18 CenterZ=0 NormalX=0 NormalY=0 NormalZ=1 AngleXU=0 Radius=1
    g42: BSplineCurve PolesCount=3 KnotsCount=2 Degree=2 IsPeriodic=0
    g43: GeomPoint X=-12.8401 Y=-17.6958 Z=0
    g44: GeomPoint X=-14 Y=-18 Z=0
    g45: LineSegment StartX=-6.2 StartY=0 StartZ=0 EndX=-7.2 EndY=0 EndZ=0
    g46: LineSegment StartX=-7.2 StartY=0 StartZ=0 EndX=-7.2 EndY=-2 EndZ=0
    g47: LineSegment StartX=-7.2 StartY=-2 StartZ=0 EndX=-6.2215 EndY=-2 EndZ=0
    g48: LineSegment StartX=-6.32538 StartY=-4 StartZ=0 EndX=-7.65538 EndY=-4 EndZ=0
    g49: LineSegment StartX=-7.65538 StartY=-4 StartZ=0 EndX=-7.65538 EndY=-5.99526 EndZ=0
    g50: LineSegment StartX=-7.65538 StartY=-5.99526 StartZ=0 EndX=-6.48644 EndY=-5.99526 EndZ=0
    g51: LineSegment StartX=-6.77343 StartY=-8 StartZ=0 EndX=-8.43343 EndY=-8 EndZ=0
    g52: LineSegment StartX=-8.43343 StartY=-8 StartZ=0 EndX=-8.43343 EndY=-10 EndZ=0
    g53: LineSegment StartX=-8.43343 StartY=-10 StartZ=0 EndX=-7.19003 EndY=-10 EndZ=0
  constraints (112):
    c: Horizontal(g0)
    c: Distance(g0) = 2
    c: Block(g0)
    c: Vertical(g1)
    c: Coincident(g2,g0)
    c: Vertical(g2)
    c: Block(g2)
    c: Coincident(g6,g2)
    c: Weight(g3) = 1
    c: Equal(g3,g4)
    c: Equal(g3,g5)
    c: InternalAlignment(g3,g6)
    c: InternalAlignment(g4,g6)
    c: InternalAlignment(g5,g6)
    c: InternalAlignment(g7,g6)
    c: InternalAlignment(g8,g6)
    c: Block(g6)
    c: Coincident(g9,g1)
    c: Coincident(g9,g6)
    c: Horizontal(g9)
    c: Vertical(g10)
    c: Block(g10)
    c: Horizontal(g11)
    c: Block(g11)
    c: Coincident(g12,g10)
    c: Horizontal(g12)
    c: Block(g12)
    c: Coincident(g13,g11)
    c: Vertical(g13)
    c: Block(g13)
    c: Coincident(g14,g10)
    c: Horizontal(g14)
    c: Block(g14)
    c: Block(g9)
    c: Block(g1)
    c: Weight(g15) = 1
    c: Equal(g15,g16)
    c: Equal(g15,g17)
    c: InternalAlignment(g15,g18)
    c: InternalAlignment(g16,g18)
    c: InternalAlignment(g17,g18)
    c: InternalAlignment(g19,g18)
    c: InternalAlignment(g20,g18)
    c: Weight(g21) = 1
    c: Equal(g21,g22)
    c: Equal(g21,g23)
    c: InternalAlignment(g21,g24)
    c: InternalAlignment(g22,g24)
    c: InternalAlignment(g23,g24)
    c: InternalAlignment(g25,g24)
    c: InternalAlignment(g26,g24)
    c: Weight(g27) = 1
    c: Equal(g27,g28)
    c: Equal(g27,g29)
    c: Coincident(g30,g14)
    c: InternalAlignment(g27,g30)
    c: InternalAlignment(g28,g30)
    c: InternalAlignment(g29,g30)
    c: InternalAlignment(g31,g30)
    c: InternalAlignment(g32,g30)
    c: Coincident(g36,g12)
    c: Weight(g33) = 1
    c: Equal(g33,g34)
    c: Equal(g33,g35)
    c: Coincident(g36,g11)
    c: InternalAlignment(g33,g36)
    c: InternalAlignment(g34,g36)
    c: InternalAlignment(g35,g36)
    c: InternalAlignment(g37,g36)
    c: InternalAlignment(g38,g36)
    c: Coincident(g42,g13)
    c: Weight(g39) = 1
    c: Equal(g39,g40)
    c: Equal(g39,g41)
    c: Coincident(g42,g1)
    c: InternalAlignment(g39,g42)
    c: InternalAlignment(g40,g42)
    c: InternalAlignment(g41,g42)
    c: InternalAlignment(g43,g42)
    c: InternalAlignment(g44,g42)
    c: Block(g18)
    c: Block(g24)
    c: Block(g30)
    c: Block(g36)
    c: Block(g42)
    c: Horizontal(g45)
    c: Coincident(g45,g0)
    c: Vertical(g46)
    c: Coincident(g46,g45)
    c: Coincident(g47,g46)
    c: Coincident(g47,g18)
    c: Horizontal(g47)
    c: Block(g46)
    c: Coincident(g48,g18)
    c: Horizontal(g48)
    c: Distance(g48) = 1.33
    c: Vertical(g49)
    c: Coincident(g49,g48)
    c: Coincident(g50,g49)
    c: Coincident(g50,g24)
    c: Horizontal(g50)
    c: Tangent(g50,g22)
    c: Horizontal(g51)
    c: Coincident(g51,g24)
    c: Block(g51)
    c: Vertical(g52)
    c: Block(g52)
    c: Coincident(g52,g51)
    c: Coincident(g53,g52)
    c: Coincident(g53,g30)
    c: Horizontal(g53)
    c: Distance(g1) = 8.5
FEATURE [Part::Feature] Face024
  shape: bbox 9.8 x 26.5 x 2e-07 mm, 1 faces, 0 solids (baked)
FEATURE [Part::Revolution] Revolve024
  Angle = 360
  Axis = (0,1,0)
  Base = (0,0,0)
  FaceMakerClass = Part::FaceMakerBullseye
  Placement = pos=(0,0,0) rot=(0,0,1;1.5708rad)
  Solid = false
  Source = -> Face024
  Symmetric = false
FEATURE [Part::Feature] Face025
  shape: bbox 9.8 x 26.5 x 2e-07 mm, 1 faces, 0 solids (baked)
FEATURE [Part::Revolution] Revolve025
  Angle = 360
  Axis = (0,1,0)
  Base = (0,0,0)
  FaceMakerClass = Part::FaceMakerBullseye
  Placement = pos=(0,0,0) rot=(0,0,1;1.5708rad)
  Solid = false
  Source = -> Face025
  Symmetric = false
FEATURE [Part::MultiFuse] Fusion033
  Placement = pos=(-18,19,36) rot=(0,0,1;0rad)
  Shapes = -> [Revolve025,Revolve024]
FEATURE [Part::Cylinder] Cylinder014
  Angle = 360
  AttacherType = Attacher::AttachEngine3D
  Height = 20
  Placement = pos=(0,0,36.15) rot=(0,0,1;0rad)
  Radius = 14.3
FEATURE [Part::Cylinder] Cylinder015
  Angle = 360
  AttacherType = Attacher::AttachEngine3D
  Height = 10
  Placement = pos=(0,0,36.15) rot=(0,0,1;0rad)
  Radius = 4
FEATURE [Part::MultiFuse] Fusion034  label="removeToCreteHoleForPlugHousing004"
  Placement = pos=(-42,19,36) rot=(0,1,0;1.5708rad)
  Shapes = -> [Cylinder014,Cylinder015]
FEATURE [Part::Cut] Cut008  label="top004"
  Base = -> Cut004
  Placement = pos=(-1,0,0) rot=(0,0,1;0rad)
  Tool = -> Fusion034
FEATURE [Part::Box] Box005  label="Cube005"
  AttacherType = Attacher::AttachEngine3D
  Height = 28
  Length = 3
  Placement = pos=(110.7,19,22) rot=(0,0,1;0rad)
  Width = 15.7
FEATURE [Part::Cylinder] Cylinder016
  Angle = 360
  AttacherType = Attacher::AttachEngine3D
  Height = 10
  Placement = pos=(0,0,36.15) rot=(0,0,1;0rad)
  Radius = 4
FEATURE [Part::Cylinder] Cylinder017
  Angle = 360
  AttacherType = Attacher::AttachEngine3D
  Height = 20
  Placement = pos=(0,0,36.15) rot=(0,0,1;0rad)
  Radius = 10.3
FEATURE [Part::MultiFuse] Fusion035  label="removeToCreteHoleForPlugHousing005"
  Placement = pos=(70,19,36) rot=(0,1,0;1.5708rad)
  Shapes = -> [Cylinder017,Cylinder016]
FEATURE [Part::Cut] Cut009  label="plugHousingTab001"
  Base = -> Box005
  Placement = pos=(-107.4,-14,0) rot=(0,0,1;0rad)
  Tool = -> Fusion035
FEATURE [Part::Box] Box006  label="Cube006"
  AttacherType = Attacher::AttachEngine3D
  Height = 28
  Length = 3
  Placement = pos=(110.7,19,22) rot=(0,0,1;0rad)
  Width = 15.7
FEATURE [Part::Cylinder] Cylinder018
  Angle = 360
  AttacherType = Attacher::AttachEngine3D
  Height = 10
  Placement = pos=(0,0,36.15) rot=(0,0,1;0rad)
  Radius = 4
FEATURE [Part::Cylinder] Cylinder019
  Angle = 360
  AttacherType = Attacher::AttachEngine3D
  Height = 20
  Placement = pos=(0,0,36.15) rot=(0,0,1;0rad)
  Radius = 10.3
FEATURE [Part::MultiFuse] Fusion036  label="removeToCreteHoleForPlugHousing006"
  Placement = pos=(70,19,36) rot=(0,1,0;1.5708rad)
  Shapes = -> [Cylinder019,Cylinder018]
FEATURE [Part::Cut] Cut010  label="plugHousingTab002"
  Base = -> Box006
  Placement = pos=(-107.4,-14,0) rot=(0,0,1;0rad)
  Tool = -> Fusion036
FEATURE [Part::MultiFuse] Fusion037
  Placement = pos=(9.6,23,0) rot=(0,0,1;3.14159rad)
  Shapes = -> [Cut009,Cut010]
FEATURE [Part::Box] Box  label="Cube"
  AttacherType = Attacher::AttachEngine3D
  Height = 10
  Length = 3
  Placement = pos=(3.3,4,12) rot=(0,0,1;0rad)
  Width = 10
FEATURE [Part::Fillet] Fillet004
  Base = -> Fusion028
  Edges = 1 edges r=2: [Edge25]
FEATURE [Part::Fillet] Fillet005  label="plugHousing046"
  Base = -> Fillet004
  Edges = 1 edges r=2: [Edge8]
FEATURE [Part::Fillet] Fillet006
  Base = -> Box
  Edges = 1 edges r=2: [Edge11]
FEATURE [Part::Box] Box007  label="Cube007"
  AttacherType = Attacher::AttachEngine3D
  Height = 10
  Length = 3
  Placement = pos=(3.3,4,50) rot=(0,0,1;0rad)
  Width = 10
FEATURE [Part::Fillet] Fillet007
  Base = -> Box007
  Edges = 1 edges r=2: [Edge12]
FEATURE [Part::Box] Box008  label="Cube008"
  AttacherType = Attacher::AttachEngine3D
  Height = 28
  Length = 4
  Placement = pos=(5,0,22) rot=(0,0,1;0rad)
  Width = 10
FEATURE [Part::Fillet] Fillet008
  Base = -> Box008
  Edges = 1 edges r=1: [Edge7]
FEATURE [Part::Fillet] Fillet009
  Base = -> Fillet008
  Edges = 1 edges r=2: [Edge5]
FEATURE [Part::Fillet] Fillet010
  Base = -> Fillet009
  Edges = 1 edges r=2: [Edge2]
FEATURE [Sketcher::SketchObject] Sketch009  label="topSketch003"
  FullyConstrained = true
  sketch-geometry (4):
    g0: LineSegment StartX=16.8446 StartY=31.512 StartZ=0 EndX=16.3251 EndY=34.4666 EndZ=0
    g1: ArcOfCircle CenterX=19 CenterY=19.2524 CenterZ=0 NormalX=0 NormalY=0 NormalZ=1 AngleXU=0 Radius=15.4476 StartAngle=1.74483 EndAngle=2.72717
    g2: ArcOfCircle CenterX=19 CenterY=19.2524 CenterZ=0 NormalX=0 NormalY=0 NormalZ=1 AngleXU=0 Radius=12.4476 StartAngle=1.74483 EndAngle=2.73189
    g3: LineSegment StartX=4.86004 StartY=25.4725 StartZ=0 EndX=7.58253 EndY=24.2107 EndZ=0
  constraints (7):
    c: Block(g0)
    c: Coincident(g1,g0)
    c: Coincident(g2,g0)
    c: Coincident(g3,g1)
    c: Coincident(g3,g2)
    c: Block(g1)
    c: Block(g2)
FEATURE [Part::Extrusion] Extrude008
  Base = -> Sketch009
  Dir = (0,0,1)
  DirMode = 2
  FaceMakerClass = Part::FaceMakerBullseye
  LengthFwd = 10
  LengthRev = 0
  Placement = pos=(0,0,31) rot=(0,0,1;0rad)
  Solid = true
  Symmetric = false
FEATURE [Part::Cylinder] Cylinder020
  Angle = 360
  AttacherType = Attacher::AttachEngine3D
  Height = 20
  Placement = pos=(0,0,36.15) rot=(0,0,1;0rad)
  Radius = 8.2
FEATURE [Part::Cylinder] Cylinder021
  Angle = 360
  AttacherType = Attacher::AttachEngine3D
  Height = 10
  Placement = pos=(0,0,36.15) rot=(0,0,1;0rad)
  Radius = 4
FEATURE [Part::MultiFuse] Fusion038  label="removeToCreteHoleForPlugHousing007"
  Placement = pos=(-42,19,36) rot=(0,1,0;1.5708rad)
  Shapes = -> [Cylinder020,Cylinder021]
FEATURE [Part::Cut] Cut011
  Base = -> Extrude008
  Tool = -> Fusion038
FEATURE [Part::Fillet] Fillet011
  Base = -> Cut011
  Edges = 1 edges r=2: [Edge1]
FEATURE [Part::Fillet] Fillet012
  Base = -> Fillet011
  Edges = 1 edges r=2.5: [Edge1]
FEATURE [Part::Fillet] Fillet013
  Base = -> Fillet012
  Edges = 1 edges r=2.5: [Edge2]
FEATURE [Part::Box] Box010  label="Cube010"
  AttacherType = Attacher::AttachEngine3D
  Height = 16
  Length = 8
  Placement = pos=(12.7,31.52,28) rot=(0,0,1;0rad)
  Width = 4
FEATURE [Sketcher::SketchObject] Sketch010  label="topSketch004"
  FullyConstrained = true
  sketch-geometry (4):
    g0: LineSegment StartX=16.8446 StartY=31.512 StartZ=0 EndX=16.3251 EndY=34.4666 EndZ=0
    g1: ArcOfCircle CenterX=19 CenterY=19.2524 CenterZ=0 NormalX=0 NormalY=0 NormalZ=1 AngleXU=0 Radius=15.4476 StartAngle=1.74483 EndAngle=2.72717
    g2: ArcOfCircle CenterX=19 CenterY=19.2524 CenterZ=0 NormalX=0 NormalY=0 NormalZ=1 AngleXU=0 Radius=12.4476 StartAngle=1.74483 EndAngle=2.73189
    g3: LineSegment StartX=4.86004 StartY=25.4725 StartZ=0 EndX=7.58253 EndY=24.2107 EndZ=0
  constraints (7):
    c: Block(g0)
    c: Coincident(g1,g0)
    c: Coincident(g2,g0)
    c: Coincident(g3,g1)
    c: Coincident(g3,g2)
    c: Block(g1)
    c: Block(g2)
FEATURE [Part::Cylinder] Cylinder022
  Angle = 360
  AttacherType = Attacher::AttachEngine3D
  Height = 10
  Placement = pos=(0,0,36.15) rot=(0,0,1;0rad)
  Radius = 4
FEATURE [Sketcher::SketchObject] Sketch011  label="topSketch005"
  FullyConstrained = true
  sketch-geometry (4):
    g0: LineSegment StartX=16.8446 StartY=31.512 StartZ=0 EndX=16.3251 EndY=34.4666 EndZ=0
    g1: ArcOfCircle CenterX=19 CenterY=19.2524 CenterZ=0 NormalX=0 NormalY=0 NormalZ=1 AngleXU=0 Radius=15.4476 StartAngle=1.74483 EndAngle=2.72717
    g2: ArcOfCircle CenterX=19 CenterY=19.2524 CenterZ=0 NormalX=0 NormalY=0 NormalZ=1 AngleXU=0 Radius=12.4476 StartAngle=1.74483 EndAngle=2.73189
    g3: LineSegment StartX=4.86004 StartY=25.4725 StartZ=0 EndX=7.58253 EndY=24.2107 EndZ=0
  constraints (7):
    c: Block(g0)
    c: Coincident(g1,g0)
    c: Coincident(g2,g0)
    c: Coincident(g3,g1)
    c: Coincident(g3,g2)
    c: Block(g1)
    c: Block(g2)
FEATURE [Part::Extrusion] Extrude010
  Base = -> Sketch011
  Dir = (0,0,1)
  DirMode = 2
  FaceMakerClass = Part::FaceMakerBullseye
  LengthFwd = 10.6
  LengthRev = 0
  Placement = pos=(0,0,31) rot=(0,0,1;0rad)
  Solid = true
  Symmetric = false
FEATURE [Part::Cylinder] Cylinder023
  Angle = 360
  AttacherType = Attacher::AttachEngine3D
  Height = 20
  Placement = pos=(0,0,36.15) rot=(0,0,1;0rad)
  Radius = 8.2
FEATURE [Part::MultiFuse] Fusion039  label="removeToCreteHoleForPlugHousing008"
  Placement = pos=(-42,19,36) rot=(0,1,0;1.5708rad)
  Shapes = -> [Cylinder023,Cylinder022]
FEATURE [Part::Cut] Cut012
  Base = -> Extrude010
  Placement = pos=(0,0,-0.3) rot=(0,0,1;0rad)
  Tool = -> Fusion039
FEATURE [Part::Cut] Cut013
  Base = -> Box010
  Tool = -> Cut012
FEATURE [Part::Fillet] Fillet014
  Base = -> Cut013
  Edges = 1 edges r=0.7: [Edge13]
FEATURE [Part::Fillet] Fillet015
  Base = -> Fillet014
  Edges = 1 edges r=0.7: [Edge13]
FEATURE [Part::Fillet] Fillet016
  Base = -> Fillet015
  Edges = 1 edges r=0.7: [Edge16]
FEATURE [Part::Fillet] Fillet017
  Base = -> Fillet016
  Edges = 1 edges r=0.7: [Edge11]
FEATURE [Part::Fillet] Fillet018
  Base = -> Fillet017
  Edges = 1 edges r=0.7: [Edge10]
FEATURE [Part::Fillet] Fillet019
  Base = -> Fillet018
  Edges = 1 edges r=1.2: [Edge5]
FEATURE [Part::Fillet] Fillet020
  Base = -> Fillet019
  Edges = 1 edges r=1.2: [Edge12]
FEATURE [Part::Fillet] Fillet021
  Base = -> Fillet020
  Edges = 1 edges r=2: [Edge1]
  Placement = pos=(0.3,0,0) rot=(0,0,1;0rad)
FEATURE [Part::MultiFuse] Fusion040  label="top005"
  Shapes = -> [Cut008,Fillet021]
FEATURE [Part::MultiFuse] Fusion041  label="wireHolder"
  Shapes = -> [Fusion033,Fillet013]
FEATURE [Part::MultiFuse] Fusion042
  Shapes = -> [Fillet007,Fusion041]
FEATURE [Part::MultiFuse] Fusion043  label="wireHolder001"
  Shapes = -> [Fusion042,Fillet010]
FEATURE [Part::MultiFuse] Fusion044  label="wireHolder002"
  Shapes = -> [Fillet006,Fusion037,Fusion043]
FEATURE [Part::Feature] Face026
  shape: bbox 11 x 6 x 2e-07 mm, 1 faces, 0 solids (baked)
FEATURE [Part::Revolution] Revolve026
  Angle = 360
  Axis = (0,1,0)
  Base = (0,0,0)
  FaceMakerClass = Part::FaceMakerBullseye
  Placement = pos=(30.3,-1,19.7) rot=(0,0,1;0rad)
  Solid = false
  Source = -> Face026
  Symmetric = false
FEATURE [Sketcher::SketchObject] Sketch013  label="topSketch006"
  FullyConstrained = true
  sketch-geometry (13):
    g0: LineSegment StartX=117 StartY=19 StartZ=0 EndX=117 EndY=38 EndZ=0
    g1: ArcOfCircle CenterX=98 CenterY=19 CenterZ=0 NormalX=0 NormalY=0 NormalZ=1 AngleXU=0 Radius=19 StartAngle=5.7297 EndAngle=6.28319
    g2: LineSegment StartX=0 StartY=3 StartZ=0 EndX=0 EndY=19 EndZ=0
    g3: LineSegment StartX=19 StartY=38 StartZ=0 EndX=117 EndY=38 EndZ=0
    g4: ArcOfCircle CenterX=19 CenterY=19 CenterZ=0 NormalX=0 NormalY=0 NormalZ=1 AngleXU=0 Radius=19 StartAngle=1.5708 EndAngle=3.14159
    g5: ArcOfCircle CenterX=19 CenterY=19 CenterZ=0 NormalX=0 NormalY=0 NormalZ=1 AngleXU=0 Radius=16 StartAngle=1.5708 EndAngle=3.14159
    g6: ArcOfCircle CenterX=98 CenterY=19 CenterZ=0 NormalX=0 NormalY=0 NormalZ=1 AngleXU=0 Radius=16 StartAngle=5.60905 EndAngle=6.28319
    g7: LineSegment StartX=114 StartY=19 StartZ=0 EndX=114 EndY=35 EndZ=0
    g8: LineSegment StartX=110.5 StartY=9.01251 StartZ=0 EndX=114.163 EndY=9.01251 EndZ=0
    g9: LineSegment StartX=114 StartY=35 StartZ=0 EndX=19 EndY=35 EndZ=0
    g10: LineSegment StartX=0 StartY=3 StartZ=0 EndX=0 EndY=0 EndZ=0
    g11: LineSegment StartX=3 StartY=0 StartZ=0 EndX=0 EndY=0 EndZ=0
    g12: LineSegment StartX=3 StartY=19 StartZ=0 EndX=3 EndY=0 EndZ=0
  constraints (33):
    c: Vertical(g0)
    c: Distance(g0) = 19
    c: Block(g0)
    c: Coincident(g1,g0)
    c: Block(g1)
    c: Vertical(g2)
    c: Block(g2)
    c: Coincident(g3,g0)
    c: Horizontal(g3)
    c: Distance(g3) = 98
    c: Coincident(g4,g3)
    c: Coincident(g4,g2)
    c: Block(g4)
    c: Coincident(g5,g4)
    c: Coincident(g6,g1)
    c: Block(g6)
    c: Block(g5)
    c: Coincident(g7,g6)
    c: Vertical(g7)
    c: Coincident(g8,g6)
    c: Coincident(g8,g1)
    c: Coincident(g9,g7)
    c: Coincident(g9,g5)
    c: Horizontal(g9)
    c: Tangent(g9,g5)
    c: Coincident(g10,g2)
    c: Distance(g10) = 3
    c: Vertical(g10)
    c: Coincident(g11,g10)
    c: Horizontal(g11)
    c: Coincident(g12,g5)
    c: Coincident(g12,g11)
    c: Vertical(g12)
FEATURE [Part::Extrusion] Extrude011  label="top006"
  Base = -> Sketch013
  Dir = (0,0,1)
  DirMode = 2
  FaceMakerClass = Part::FaceMakerBullseye
  LengthFwd = 72
  LengthRev = 0
  Solid = true
  Symmetric = false
FEATURE [Sketcher::SketchObject] Sketch014
  FullyConstrained = true
  MapMode = 3
  Placement = pos=(0,0,0) rot=(1,0,0;1.5708rad)
  Support = -> [Extrude011]
  sketch-geometry (8):
    g0: Circle CenterX=80.351 CenterY=-67.6202 CenterZ=0 NormalX=0 NormalY=0 NormalZ=1 AngleXU=0 Radius=2
    g1: Circle CenterX=80.351 CenterY=-67.6202 CenterZ=0 NormalX=0 NormalY=0 NormalZ=1 AngleXU=0 Radius=3
    g2: Circle CenterX=80.351 CenterY=-4.92017 CenterZ=0 NormalX=0 NormalY=0 NormalZ=1 AngleXU=0 Radius=2
    g3: Circle CenterX=80.351 CenterY=-4.92017 CenterZ=0 NormalX=0 NormalY=0 NormalZ=1 AngleXU=0 Radius=3
    g4: Circle CenterX=23.851 CenterY=-4.92017 CenterZ=0 NormalX=0 NormalY=0 NormalZ=1 AngleXU=0 Radius=2
    g5: Circle CenterX=23.851 CenterY=-4.92017 CenterZ=0 NormalX=0 NormalY=0 NormalZ=1 AngleXU=0 Radius=3
    g6: Circle CenterX=23.851 CenterY=-67.6202 CenterZ=0 NormalX=0 NormalY=0 NormalZ=1 AngleXU=0 Radius=2
    g7: Circle CenterX=23.851 CenterY=-67.6202 CenterZ=0 NormalX=0 NormalY=0 NormalZ=1 AngleXU=0 Radius=3
  constraints (8):
    c: Block(g3)
    c: Block(g2)
    c: Block(g1)
    c: Block(g0)
    c: Block(g6)
    c: Block(g7)
    c: Block(g4)
    c: Block(g5)
FEATURE [Part::Feature] Face027
  shape: bbox 11 x 6 x 2e-07 mm, 1 faces, 0 solids (baked)
FEATURE [Part::Revolution] Revolve027
  Angle = 360
  Axis = (0,1,0)
  Base = (0,0,0)
  FaceMakerClass = Part::FaceMakerBullseye
  Placement = pos=(30.3,-1,51.7) rot=(0,0,1;0rad)
  Solid = false
  Source = -> Face027
  Symmetric = false
FEATURE [Part::Feature] Face028
  shape: bbox 11 x 6 x 2e-07 mm, 1 faces, 0 solids (baked)
FEATURE [Part::Revolution] Revolve028
  Angle = 360
  Axis = (0,1,0)
  Base = (0,0,0)
  FaceMakerClass = Part::FaceMakerBullseye
  Placement = pos=(62.3,-1,19.7) rot=(0,0,1;0rad)
  Solid = false
  Source = -> Face028
  Symmetric = false
FEATURE [Part::Feature] Face029
  shape: bbox 11 x 6 x 2e-07 mm, 1 faces, 0 solids (baked)
FEATURE [Part::Revolution] Revolve029
  Angle = 360
  Axis = (0,1,0)
  Base = (0,0,0)
  FaceMakerClass = Part::FaceMakerBullseye
  Placement = pos=(62.3,-1,51.7) rot=(0,0,1;0rad)
  Solid = false
  Source = -> Face029
  Symmetric = false
FEATURE [Part::Feature] Wire
  shape: bbox 11 x 5.2 x 2e-07 mm, 0 faces, 0 solids (baked)
FEATURE [Part::Revolution] Revolve030
  Angle = 360
  Axis = (0,1,0)
  Base = (0,0,0)
  FaceMakerClass = Part::FaceMakerBullseye
  Placement = pos=(30.3,38,19.7) rot=(0,0,1;0rad)
  Solid = true
  Source = -> Wire
  Symmetric = false
FEATURE [Part::Feature] Wire001
  shape: bbox 11 x 5.2 x 2e-07 mm, 0 faces, 0 solids (baked)
FEATURE [Part::Revolution] Revolve031
  Angle = 360
  Axis = (0,1,0)
  Base = (0,0,0)
  FaceMakerClass = Part::FaceMakerBullseye
  Placement = pos=(30.3,38,51.7) rot=(0,0,1;0rad)
  Solid = true
  Source = -> Wire001
  Symmetric = false
FEATURE [Part::Feature] Wire002
  shape: bbox 11 x 5.2 x 2e-07 mm, 0 faces, 0 solids (baked)
FEATURE [Part::Revolution] Revolve032
  Angle = 360
  Axis = (0,1,0)
  Base = (0,0,0)
  FaceMakerClass = Part::FaceMakerBullseye
  Placement = pos=(62.3,38,51.7) rot=(0,0,1;0rad)
  Solid = true
  Source = -> Wire002
  Symmetric = false
FEATURE [Part::Feature] Wire003
  shape: bbox 11 x 5.2 x 2e-07 mm, 0 faces, 0 solids (baked)
FEATURE [Part::Revolution] Revolve033
  Angle = 360
  Axis = (0,1,0)
  Base = (0,0,0)
  FaceMakerClass = Part::FaceMakerBullseye
  Placement = pos=(62.3,38,19.7) rot=(0,0,1;0rad)
  Solid = true
  Source = -> Wire003
  Symmetric = false
FEATURE [Part::MultiFuse] Fusion045  label="altRandScrewHousing"
  Shapes = -> [Revolve029,Revolve027,Revolve028,Revolve026]
FEATURE [Part::MultiFuse] Fusion046  label="fanScrewHousing"
  Shapes = -> [Revolve033,Revolve032,Revolve031,Revolve030]
FEATURE [Sketcher::SketchObject] Sketch015
  FullyConstrained = true
  sketch-geometry (17):
    g0: Circle CenterX=-3.5 CenterY=23.5 CenterZ=0 NormalX=0 NormalY=0 NormalZ=1 AngleXU=0 Radius=1
    g1: Circle CenterX=-1 CenterY=15.25 CenterZ=0 NormalX=0 NormalY=0 NormalZ=1 AngleXU=0 Radius=1
    g2: Circle CenterX=-3.5 CenterY=7 CenterZ=0 NormalX=0 NormalY=0 NormalZ=1 AngleXU=0 Radius=1
    g3: BSplineCurve PolesCount=3 KnotsCount=2 Degree=2 IsPeriodic=0
    g4: GeomPoint X=-3.5 Y=23.5 Z=0
    g5: GeomPoint X=-3.5 Y=7 Z=0
    g6: Circle CenterX=-4.8 CenterY=30.5 CenterZ=0 NormalX=0 NormalY=0 NormalZ=1 AngleXU=0 Radius=1
    g7: Circle CenterX=-3.5 CenterY=30.5 CenterZ=0 NormalX=0 NormalY=0 NormalZ=1 AngleXU=0 Radius=1
    g8: Circle CenterX=-3.5 CenterY=29.2 CenterZ=0 NormalX=0 NormalY=0 NormalZ=1 AngleXU=0 Radius=1
    g9: BSplineCurve PolesCount=3 KnotsCount=2 Degree=2 IsPeriodic=0
    g10: GeomPoint X=-4.8 Y=30.5 Z=0
    g11: GeomPoint X=-3.5 Y=29.2 Z=0
    g12: LineSegment StartX=-3.5 StartY=29.2 StartZ=0 EndX=-3.5 EndY=23.5 EndZ=0
    g13: LineSegment StartX=-4.8 StartY=30.5 StartZ=0 EndX=0 EndY=30.5 EndZ=0
    g14: LineSegment StartX=-3.5 StartY=0.3 StartZ=0 EndX=0 EndY=0.3 EndZ=0
    g15: LineSegment StartX=-3.5 StartY=0.3 StartZ=0 EndX=-3.5 EndY=7 EndZ=0
    g16: LineSegment StartX=0 StartY=0.3 StartZ=0 EndX=0 EndY=30.5 EndZ=0
  constraints (33):
    c: Weight(g0) = 1
    c: Equal(g0,g1)
    c: Equal(g0,g2)
    c: InternalAlignment(g0,g3)
    c: InternalAlignment(g1,g3)
    c: InternalAlignment(g2,g3)
    c: InternalAlignment(g4,g3)
    c: InternalAlignment(g5,g3)
    c: Block(g3)
    c: Weight(g6) = 1
    c: Equal(g6,g7)
    c: Equal(g6,g8)
    c: InternalAlignment(g6,g9)
    c: InternalAlignment(g7,g9)
    c: InternalAlignment(g8,g9)
    c: InternalAlignment(g10,g9)
    c: InternalAlignment(g11,g9)
    c: Block(g9)
    c: Coincident(g12,g9)
    c: Coincident(g12,g3)
    c: Vertical(g12)
    c: Coincident(g13,g9)
    c: Horizontal(g13)
    c: Distance(g13) = 4.8
    c: Horizontal(g14)
    c: Block(g14)
    c: Coincident(g15,g14)
    c: Coincident(g15,g3)
    c: Vertical(g15)
    c: Coincident(g16,g14)
    c: Coincident(g16,g13)
    c: Vertical(g16)
    c: Tangent(g16,g1)
FEATURE [Sketcher::SketchObject] Sketch016
  FullyConstrained = true
  sketch-geometry (16):
    g0: Circle CenterX=-3.5 CenterY=23.5 CenterZ=0 NormalX=0 NormalY=0 NormalZ=1 AngleXU=0 Radius=1
    g1: Circle CenterX=-1 CenterY=15.25 CenterZ=0 NormalX=0 NormalY=0 NormalZ=1 AngleXU=0 Radius=1
    g2: Circle CenterX=-3.5 CenterY=7 CenterZ=0 NormalX=0 NormalY=0 NormalZ=1 AngleXU=0 Radius=1
    g3: BSplineCurve PolesCount=3 KnotsCount=2 Degree=2 IsPeriodic=0
    g4: GeomPoint X=-3.5 Y=23.5 Z=0
    g5: GeomPoint X=-3.5 Y=7 Z=0
    g6: LineSegment StartX=-3.5 StartY=28.2 StartZ=0 EndX=-3.5 EndY=23.5 EndZ=0
    g7: LineSegment StartX=0 StartY=29.5 StartZ=0 EndX=0 EndY=30 EndZ=0
    g8: LineSegment StartX=-3.5 StartY=28.2 StartZ=0 EndX=-3.5 EndY=30 EndZ=0
    g9: LineSegment StartX=0 StartY=30 StartZ=0 EndX=0 EndY=30.5 EndZ=0
    g10: LineSegment StartX=0 StartY=30.5 StartZ=0 EndX=-3.5 EndY=30.5 EndZ=0
    g11: LineSegment StartX=-3.5 StartY=30.5 StartZ=0 EndX=-3.5 EndY=30 EndZ=0
    g12: LineSegment StartX=0 StartY=29.5 StartZ=0 EndX=0 EndY=5 EndZ=0
    g13: LineSegment StartX=-3.5 StartY=0.3 StartZ=0 EndX=-3.5 EndY=7 EndZ=0
    g14: LineSegment StartX=-3.5 StartY=0.3 StartZ=0 EndX=0 EndY=0.3 EndZ=0
    g15: LineSegment StartX=0 StartY=5 StartZ=0 EndX=0 EndY=0.3 EndZ=0
  constraints (39):
    c: Weight(g0) = 1
    c: Equal(g0,g1)
    c: Equal(g0,g2)
    c: InternalAlignment(g0,g3)
    c: InternalAlignment(g1,g3)
    c: InternalAlignment(g2,g3)
    c: InternalAlignment(g4,g3)
    c: InternalAlignment(g5,g3)
    c: Block(g3)
    c: Coincident(g6,g3)
    c: Vertical(g6)
    c: Vertical(g7)
    c: Distance(g7) = 0.5
    c: Coincident(g8,g6)
    c: Vertical(g8)
    c: Block(g6)
    c: Block(g7)
    c: Vertical(g9)
    c: Equal(g7,g9) = 0.5
    c: Block(g9)
    c: Coincident(g9,g7)
    c: Horizontal(g10)
    c: Coincident(g10,g9)
    c: Coincident(g11,g10)
    c: Coincident(g11,g8)
    c: Vertical(g11)
    c: Block(g11)
    c: Coincident(g12,g7)
    c: Vertical(g12)
    c: Coincident(g13,g3)
    c: Vertical(g13)
    c: Distance(g13) = 6.7
    c: Coincident(g14,g13)
    c: Horizontal(g14)
    c: Block(g14)
    c: Coincident(g15,g12)
    c: Coincident(g15,g14)
    c: Vertical(g15)
    c: Block(g15)
FEATURE [Sketcher::SketchObject] Sketch017
  FullyConstrained = true
  sketch-geometry (11):
    g0: LineSegment StartX=-3.5 StartY=1e-16 StartZ=0 EndX=-1.6 EndY=1e-16 EndZ=0
    g1: LineSegment StartX=-1.6 StartY=1e-16 StartZ=0 EndX=-1.6 EndY=1.5 EndZ=0
    g2: LineSegment StartX=-3.5 StartY=1.5 StartZ=0 EndX=-1.6 EndY=1.5 EndZ=0
    g3: LineSegment StartX=-3.5 StartY=1e-16 StartZ=0 EndX=-4.8 EndY=1e-16 EndZ=0
    g4: Circle CenterX=-3.5 CenterY=1.3 CenterZ=0 NormalX=0 NormalY=0 NormalZ=1 AngleXU=0 Radius=1
    g5: Circle CenterX=-3.5 CenterY=1e-16 CenterZ=0 NormalX=0 NormalY=0 NormalZ=1 AngleXU=0 Radius=1
    g6: Circle CenterX=-4.8 CenterY=1e-16 CenterZ=0 NormalX=0 NormalY=0 NormalZ=1 AngleXU=0 Radius=1
    g7: BSplineCurve PolesCount=3 KnotsCount=2 Degree=2 IsPeriodic=0
    g8: GeomPoint X=-3.5 Y=1.3 Z=0
    g9: GeomPoint X=-4.8 Y=1e-16 Z=0
    g10: LineSegment StartX=-3.5 StartY=1.3 StartZ=0 EndX=-3.5 EndY=1.5 EndZ=0
  constraints (24):
    c: Horizontal(g0)
    c: Distance(g0) = 1.9
    c: Block(g0)
    c: Coincident(g1,g0)
    c: Vertical(g1)
    c: Coincident(g2,g1)
    c: Horizontal(g2)
    c: Coincident(g3,g0)
    c: Horizontal(g3)
    c: Distance(g3) = 1.3
    c: Weight(g4) = 1
    c: Equal(g4,g5)
    c: Coincident(g5,g0)
    c: Equal(g4,g6)
    c: Coincident(g7,g3)
    c: InternalAlignment(g4,g7)
    c: InternalAlignment(g5,g7)
    c: InternalAlignment(g6,g7)
    c: InternalAlignment(g8,g7)
    c: InternalAlignment(g9,g7)
    c: Coincident(g10,g7)
    c: Coincident(g10,g2)
    c: Vertical(g10)
    c: Block(g10)
FEATURE [Part::Feature] Face035
  shape: bbox 3.2 x 1.5 x 2e-07 mm, 1 faces, 0 solids (baked)
FEATURE [Part::Revolution] Revolve039  label="backCaseScrewRetainer"
  Angle = 360
  Axis = (0,1,0)
  Base = (0,0,0)
  FaceMakerClass = Part::FaceMakerBullseye
  Placement = pos=(12.5,3,62) rot=(0,0,1;0rad)
  Solid = false
  Source = -> Face035
  Symmetric = false
FEATURE [Part::Feature] Face036
  shape: bbox 3.2 x 1.5 x 2e-07 mm, 1 faces, 0 solids (baked)
FEATURE [Part::Feature] Face039
  shape: bbox 4.8 x 30.2 x 2e-07 mm, 1 faces, 0 solids (baked)
FEATURE [Part::Revolution] Revolve043  label="frontCaseScrewPost002"
  Angle = 360
  Axis = (0,1,0)
  Base = (0,0,0)
  FaceMakerClass = Part::FaceMakerBullseye
  Placement = pos=(89.5,4.5,3.5) rot=(0,0,1;0rad)
  Solid = false
  Source = -> Face039
  Symmetric = false
FEATURE [Part::Feature] Face042
  shape: bbox 4.8 x 30.2 x 2e-07 mm, 1 faces, 0 solids (baked)
FEATURE [Part::Revolution] Revolve046  label="frontCaseScrewPost003"
  Angle = 360
  Axis = (0,1,0)
  Base = (0,0,0)
  FaceMakerClass = Part::FaceMakerBullseye
  Placement = pos=(89.5,4.5,68.5) rot=(0,0,1;0rad)
  Solid = false
  Source = -> Face042
  Symmetric = false
FEATURE [Part::Feature] Face043
  shape: bbox 3.2 x 1.5 x 2e-07 mm, 1 faces, 0 solids (baked)
FEATURE [Part::Revolution] Revolve047  label="frontCaseScrewRetainer002"
  Angle = 360
  Axis = (0,1,0)
  Base = (0,0,0)
  FaceMakerClass = Part::FaceMakerBullseye
  Placement = pos=(89.5,3,68.5) rot=(0,0,1;0rad)
  Solid = false
  Source = -> Face043
  Symmetric = false
FEATURE [Part::Feature] Face044
  shape: bbox 3.2 x 1.5 x 2e-07 mm, 1 faces, 0 solids (baked)
FEATURE [Part::Revolution] Revolve048  label="frontCaseScrewRetainer003"
  Angle = 360
  Axis = (0,1,0)
  Base = (0,0,0)
  FaceMakerClass = Part::FaceMakerBullseye
  Placement = pos=(89.5,3,3.5) rot=(0,0,1;0rad)
  Solid = false
  Source = -> Face044
  Symmetric = false
FEATURE [App::MeasureDistance] Distance002  label="Distance: 1.67 mm"
  Distance = 1.66921
  P1 = (99.2361,4.7524,71.7)
  P2 = (99.2347,6.42161,71.7)
FEATURE [Sketcher::SketchObject] Sketch018
  FullyConstrained = true
  sketch-geometry (7):
    g0: LineSegment StartX=0 StartY=0 StartZ=0 EndX=0 EndY=6 EndZ=0
    g1: Circle CenterX=0 CenterY=0 CenterZ=0 NormalX=0 NormalY=0 NormalZ=1 AngleXU=0 Radius=1
    g2: Circle CenterX=8 CenterY=6 CenterZ=0 NormalX=0 NormalY=0 NormalZ=1 AngleXU=0 Radius=1
    g3: BSplineCurve PolesCount=3 KnotsCount=2 Degree=2 IsPeriodic=0
    g4: GeomPoint X=0 Y=0 Z=0
    g5: GeomPoint X=8 Y=6 Z=0
    g6: LineSegment StartX=0 StartY=6 StartZ=0 EndX=8 EndY=6 EndZ=0
  constraints (14):
    c: Coincident(g0,g-1)
    c: Distance(g0) = 6
    c: Vertical(g0)
    c: Coincident(g3,g0)
    c: Weight(g1) = 1
    c: Equal(g1,g2)
    c: InternalAlignment(g1,g3)
    c: InternalAlignment(g2,g3)
    c: InternalAlignment(g4,g3)
    c: InternalAlignment(g5,g3)
    c: Block(g3)
    c: Coincident(g6,g0)
    c: Coincident(g6,g3)
    c: Horizontal(g6)
FEATURE [Part::Extrusion] Extrude012  label="caseScrewPillarBracket"
  Base = -> Sketch018
  Dir = (0,0,1)
  DirMode = 2
  FaceMakerClass = Part::FaceMakerBullseye
  LengthFwd = 2.4
  LengthRev = 0
  Placement = pos=(15.76,29,8.8) rot=(0,1,0;0rad)
  Solid = true
  Symmetric = false
FEATURE [Sketcher::SketchObject] Sketch019
  FullyConstrained = true
  sketch-geometry (7):
    g0: LineSegment StartX=0 StartY=0 StartZ=0 EndX=0 EndY=6 EndZ=0
    g1: Circle CenterX=0 CenterY=0 CenterZ=0 NormalX=0 NormalY=0 NormalZ=1 AngleXU=0 Radius=1
    g2: Circle CenterX=8 CenterY=6 CenterZ=0 NormalX=0 NormalY=0 NormalZ=1 AngleXU=0 Radius=1
    g3: BSplineCurve PolesCount=3 KnotsCount=2 Degree=2 IsPeriodic=0
    g4: GeomPoint X=0 Y=0 Z=0
    g5: GeomPoint X=8 Y=6 Z=0
    g6: LineSegment StartX=0 StartY=6 StartZ=0 EndX=8 EndY=6 EndZ=0
  constraints (14):
    c: Coincident(g0,g-1)
    c: Distance(g0) = 6
    c: Vertical(g0)
    c: Coincident(g3,g0)
    c: Weight(g1) = 1
    c: Equal(g1,g2)
    c: InternalAlignment(g1,g3)
    c: InternalAlignment(g2,g3)
    c: InternalAlignment(g4,g3)
    c: InternalAlignment(g5,g3)
    c: Block(g3)
    c: Coincident(g6,g0)
    c: Coincident(g6,g3)
    c: Horizontal(g6)
FEATURE [Part::Extrusion] Extrude013  label="caseScrewPillarBracket001"
  Base = -> Sketch019
  Dir = (0,0,1)
  DirMode = 2
  FaceMakerClass = Part::FaceMakerBullseye
  LengthFwd = 2.4
  LengthRev = 0
  Placement = pos=(15.76,29,60.8) rot=(0,0,1;0rad)
  Solid = true
  Symmetric = false
FEATURE [Sketcher::SketchObject] Sketch020
  FullyConstrained = true
  sketch-geometry (7):
    g0: LineSegment StartX=0 StartY=0 StartZ=0 EndX=0 EndY=6 EndZ=0
    g1: Circle CenterX=0 CenterY=0 CenterZ=0 NormalX=0 NormalY=0 NormalZ=1 AngleXU=0 Radius=1
    g2: Circle CenterX=8 CenterY=6 CenterZ=0 NormalX=0 NormalY=0 NormalZ=1 AngleXU=0 Radius=1
    g3: BSplineCurve PolesCount=3 KnotsCount=2 Degree=2 IsPeriodic=0
    g4: GeomPoint X=0 Y=0 Z=0
    g5: GeomPoint X=8 Y=6 Z=0
    g6: LineSegment StartX=0 StartY=6 StartZ=0 EndX=8 EndY=6 EndZ=0
  constraints (14):
    c: Coincident(g0,g-1)
    c: Distance(g0) = 6
    c: Vertical(g0)
    c: Coincident(g3,g0)
    c: Weight(g1) = 1
    c: Equal(g1,g2)
    c: InternalAlignment(g1,g3)
    c: InternalAlignment(g2,g3)
    c: InternalAlignment(g4,g3)
    c: InternalAlignment(g5,g3)
    c: Block(g3)
    c: Coincident(g6,g0)
    c: Coincident(g6,g3)
    c: Horizontal(g6)
FEATURE [Part::Extrusion] Extrude014  label="caseScrewPillarBracket002"
  Base = -> Sketch020
  Dir = (0,0,1)
  DirMode = 2
  FaceMakerClass = Part::FaceMakerBullseye
  LengthFwd = 2.4
  LengthRev = 0
  Placement = pos=(13.7,29,13.26) rot=(0,-1,0;1.5708rad)
  Solid = true
  Symmetric = false
FEATURE [Sketcher::SketchObject] Sketch021
  FullyConstrained = true
  sketch-geometry (7):
    g0: LineSegment StartX=0 StartY=0 StartZ=0 EndX=0 EndY=6 EndZ=0
    g1: Circle CenterX=0 CenterY=0 CenterZ=0 NormalX=0 NormalY=0 NormalZ=1 AngleXU=0 Radius=1
    g2: Circle CenterX=8 CenterY=6 CenterZ=0 NormalX=0 NormalY=0 NormalZ=1 AngleXU=0 Radius=1
    g3: BSplineCurve PolesCount=3 KnotsCount=2 Degree=2 IsPeriodic=0
    g4: GeomPoint X=0 Y=0 Z=0
    g5: GeomPoint X=8 Y=6 Z=0
    g6: LineSegment StartX=0 StartY=6 StartZ=0 EndX=8 EndY=6 EndZ=0
  constraints (14):
    c: Coincident(g0,g-1)
    c: Distance(g0) = 6
    c: Vertical(g0)
    c: Coincident(g3,g0)
    c: Weight(g1) = 1
    c: Equal(g1,g2)
    c: InternalAlignment(g1,g3)
    c: InternalAlignment(g2,g3)
    c: InternalAlignment(g4,g3)
    c: InternalAlignment(g5,g3)
    c: Block(g3)
    c: Coincident(g6,g0)
    c: Coincident(g6,g3)
    c: Horizontal(g6)
FEATURE [Part::Extrusion] Extrude015  label="caseScrewPillarBracket003"
  Base = -> Sketch021
  Dir = (0,0,1)
  DirMode = 2
  FaceMakerClass = Part::FaceMakerBullseye
  LengthFwd = 2.4
  LengthRev = 0
  Placement = pos=(11.3,29,58.74) rot=(0,1,0;1.5708rad)
  Solid = true
  Symmetric = false
FEATURE [Sketcher::SketchObject] Sketch022
  FullyConstrained = true
  sketch-geometry (7):
    g0: LineSegment StartX=0 StartY=0 StartZ=0 EndX=0 EndY=6 EndZ=0
    g1: Circle CenterX=0 CenterY=0 CenterZ=0 NormalX=0 NormalY=0 NormalZ=1 AngleXU=0 Radius=1
    g2: Circle CenterX=8 CenterY=6 CenterZ=0 NormalX=0 NormalY=0 NormalZ=1 AngleXU=0 Radius=1
    g3: BSplineCurve PolesCount=3 KnotsCount=2 Degree=2 IsPeriodic=0
    g4: GeomPoint X=0 Y=0 Z=0
    g5: GeomPoint X=8 Y=6 Z=0
    g6: LineSegment StartX=0 StartY=6 StartZ=0 EndX=8 EndY=6 EndZ=0
  constraints (14):
    c: Coincident(g0,g-1)
    c: Distance(g0) = 6
    c: Vertical(g0)
    c: Coincident(g3,g0)
    c: Weight(g1) = 1
    c: Equal(g1,g2)
    c: InternalAlignment(g1,g3)
    c: InternalAlignment(g2,g3)
    c: InternalAlignment(g4,g3)
    c: InternalAlignment(g5,g3)
    c: Block(g3)
    c: Coincident(g6,g0)
    c: Coincident(g6,g3)
    c: Horizontal(g6)
FEATURE [Part::Extrusion] Extrude016  label="caseScrewPillarBracket004"
  Base = -> Sketch022
  Dir = (0,0,1)
  DirMode = 2
  FaceMakerClass = Part::FaceMakerBullseye
  LengthFwd = 2.4
  LengthRev = 0
  Placement = pos=(88.3,29,65.23) rot=(0,1,0;1.5708rad)
  Solid = true
  Symmetric = false
FEATURE [Sketcher::SketchObject] Sketch023
  FullyConstrained = true
  sketch-geometry (7):
    g0: LineSegment StartX=0 StartY=0 StartZ=0 EndX=0 EndY=6 EndZ=0
    g1: Circle CenterX=0 CenterY=0 CenterZ=0 NormalX=0 NormalY=0 NormalZ=1 AngleXU=0 Radius=1
    g2: Circle CenterX=8 CenterY=6 CenterZ=0 NormalX=0 NormalY=0 NormalZ=1 AngleXU=0 Radius=1
    g3: BSplineCurve PolesCount=3 KnotsCount=2 Degree=2 IsPeriodic=0
    g4: GeomPoint X=0 Y=0 Z=0
    g5: GeomPoint X=8 Y=6 Z=0
    g6: LineSegment StartX=0 StartY=6 StartZ=0 EndX=8 EndY=6 EndZ=0
  constraints (14):
    c: Coincident(g0,g-1)
    c: Distance(g0) = 6
    c: Vertical(g0)
    c: Coincident(g3,g0)
    c: Weight(g1) = 1
    c: Equal(g1,g2)
    c: InternalAlignment(g1,g3)
    c: InternalAlignment(g2,g3)
    c: InternalAlignment(g4,g3)
    c: InternalAlignment(g5,g3)
    c: Block(g3)
    c: Coincident(g6,g0)
    c: Coincident(g6,g3)
    c: Horizontal(g6)
FEATURE [Part::Extrusion] Extrude017  label="caseScrewPillarBracket005"
  Base = -> Sketch023
  Dir = (0,0,1)
  DirMode = 2
  FaceMakerClass = Part::FaceMakerBullseye
  LengthFwd = 2.4
  LengthRev = 0
  Placement = pos=(90.7,29,6.77) rot=(0,-1,0;1.5708rad)
  Solid = true
  Symmetric = false
FEATURE [Sketcher::SketchObject] Sketch024
  FullyConstrained = true
  sketch-geometry (7):
    g0: LineSegment StartX=0 StartY=0 StartZ=0 EndX=0 EndY=6 EndZ=0
    g1: Circle CenterX=0 CenterY=0 CenterZ=0 NormalX=0 NormalY=0 NormalZ=1 AngleXU=0 Radius=1
    g2: Circle CenterX=8 CenterY=6 CenterZ=0 NormalX=0 NormalY=0 NormalZ=1 AngleXU=0 Radius=1
    g3: BSplineCurve PolesCount=3 KnotsCount=2 Degree=2 IsPeriodic=0
    g4: GeomPoint X=0 Y=0 Z=0
    g5: GeomPoint X=8 Y=6 Z=0
    g6: LineSegment StartX=0 StartY=6 StartZ=0 EndX=8 EndY=6 EndZ=0
  constraints (14):
    c: Coincident(g0,g-1)
    c: Distance(g0) = 6
    c: Vertical(g0)
    c: Coincident(g3,g0)
    c: Weight(g1) = 1
    c: Equal(g1,g2)
    c: InternalAlignment(g1,g3)
    c: InternalAlignment(g2,g3)
    c: InternalAlignment(g4,g3)
    c: InternalAlignment(g5,g3)
    c: Block(g3)
    c: Coincident(g6,g0)
    c: Coincident(g6,g3)
    c: Horizontal(g6)
FEATURE [Part::Extrusion] Extrude018  label="caseScrewPillarBracket006"
  Base = -> Sketch024
  Dir = (0,0,1)
  DirMode = 2
  FaceMakerClass = Part::FaceMakerBullseye
  LengthFwd = 2.4
  LengthRev = 0
  Placement = pos=(103.7,29,6.77) rot=(0,-1,0;1.5708rad)
  Solid = true
  Symmetric = false
FEATURE [Sketcher::SketchObject] Sketch025
  FullyConstrained = true
  sketch-geometry (7):
    g0: LineSegment StartX=0 StartY=0 StartZ=0 EndX=0 EndY=6 EndZ=0
    g1: Circle CenterX=0 CenterY=0 CenterZ=0 NormalX=0 NormalY=0 NormalZ=1 AngleXU=0 Radius=1
    g2: Circle CenterX=8 CenterY=6 CenterZ=0 NormalX=0 NormalY=0 NormalZ=1 AngleXU=0 Radius=1
    g3: BSplineCurve PolesCount=3 KnotsCount=2 Degree=2 IsPeriodic=0
    g4: GeomPoint X=0 Y=0 Z=0
    g5: GeomPoint X=8 Y=6 Z=0
    g6: LineSegment StartX=0 StartY=6 StartZ=0 EndX=8 EndY=6 EndZ=0
  constraints (14):
    c: Coincident(g0,g-1)
    c: Distance(g0) = 6
    c: Vertical(g0)
    c: Coincident(g3,g0)
    c: Weight(g1) = 1
    c: Equal(g1,g2)
    c: InternalAlignment(g1,g3)
    c: InternalAlignment(g2,g3)
    c: InternalAlignment(g4,g3)
    c: InternalAlignment(g5,g3)
    c: Block(g3)
    c: Coincident(g6,g0)
    c: Coincident(g6,g3)
    c: Horizontal(g6)
FEATURE [Part::Extrusion] Extrude019  label="caseScrewPillarBracket007"
  Base = -> Sketch025
  Dir = (0,0,1)
  DirMode = 2
  FaceMakerClass = Part::FaceMakerBullseye
  LengthFwd = 2.4
  LengthRev = 0
  Placement = pos=(101.3,29,65.23) rot=(0,1,0;1.5708rad)
  Solid = true
  Symmetric = false
FEATURE [Part::Box] Box011  label="frontCaseScrewPillarBracket"
  AttacherType = Attacher::AttachEngine3D
  Height = 2.4
  Length = 16
  Placement = pos=(87,28,2.3) rot=(0,0,1;0rad)
  Width = 7
FEATURE [Part::Box] Box012  label="frontCaseScrewPillarBracket001"
  AttacherType = Attacher::AttachEngine3D
  Height = 2.4
  Length = 16
  Placement = pos=(87,28,67.3) rot=(0,0,1;0rad)
  Width = 7
FEATURE [Sketcher::SketchObject] Sketch026
  FullyConstrained = true
  sketch-geometry (17):
    g0: Circle CenterX=-3.5 CenterY=23.5 CenterZ=0 NormalX=0 NormalY=0 NormalZ=1 AngleXU=0 Radius=1
    g1: Circle CenterX=-1 CenterY=15.25 CenterZ=0 NormalX=0 NormalY=0 NormalZ=1 AngleXU=0 Radius=1
    g2: Circle CenterX=-3.5 CenterY=7 CenterZ=0 NormalX=0 NormalY=0 NormalZ=1 AngleXU=0 Radius=1
    g3: BSplineCurve PolesCount=3 KnotsCount=2 Degree=2 IsPeriodic=0
    g4: GeomPoint X=-3.5 Y=23.5 Z=0
    g5: GeomPoint X=-3.5 Y=7 Z=0
    g6: Circle CenterX=-4.8 CenterY=30.5 CenterZ=0 NormalX=0 NormalY=0 NormalZ=1 AngleXU=0 Radius=1
    g7: Circle CenterX=-3.5 CenterY=30.5 CenterZ=0 NormalX=0 NormalY=0 NormalZ=1 AngleXU=0 Radius=1
    g8: Circle CenterX=-3.5 CenterY=29.2 CenterZ=0 NormalX=0 NormalY=0 NormalZ=1 AngleXU=0 Radius=1
    g9: BSplineCurve PolesCount=3 KnotsCount=2 Degree=2 IsPeriodic=0
    g10: GeomPoint X=-4.8 Y=30.5 Z=0
    g11: GeomPoint X=-3.5 Y=29.2 Z=0
    g12: LineSegment StartX=-3.5 StartY=29.2 StartZ=0 EndX=-3.5 EndY=23.5 EndZ=0
    g13: LineSegment StartX=-4.8 StartY=30.5 StartZ=0 EndX=0 EndY=30.5 EndZ=0
    g14: LineSegment StartX=-3.5 StartY=5 StartZ=0 EndX=-3.5 EndY=7 EndZ=0
    g15: LineSegment StartX=0 StartY=5 StartZ=0 EndX=0 EndY=30.5 EndZ=0
    g16: LineSegment StartX=-3.5 StartY=5 StartZ=0 EndX=0 EndY=5 EndZ=0
  constraints (33):
    c: Weight(g0) = 1
    c: Equal(g0,g1)
    c: Equal(g0,g2)
    c: InternalAlignment(g0,g3)
    c: InternalAlignment(g1,g3)
    c: InternalAlignment(g2,g3)
    c: InternalAlignment(g4,g3)
    c: InternalAlignment(g5,g3)
    c: Block(g3)
    c: Weight(g6) = 1
    c: Equal(g6,g7)
    c: Equal(g6,g8)
    c: InternalAlignment(g6,g9)
    c: InternalAlignment(g7,g9)
    c: InternalAlignment(g8,g9)
    c: InternalAlignment(g10,g9)
    c: InternalAlignment(g11,g9)
    c: Block(g9)
    c: Coincident(g12,g9)
    c: Coincident(g12,g3)
    c: Vertical(g12)
    c: Coincident(g13,g9)
    c: Horizontal(g13)
    c: Distance(g13) = 4.8
    c: Coincident(g14,g3)
    c: Vertical(g14)
    c: Coincident(g15,g13)
    c: Vertical(g15)
    c: Tangent(g15,g1)
    c: Distance(g14) = 2
    c: Coincident(g16,g14)
    c: Horizontal(g16)
    c: Coincident(g15,g16)
FEATURE [Part::Feature] Face050
  shape: bbox 4.8 x 25.5 x 2e-07 mm, 1 faces, 0 solids (baked)
FEATURE [Part::Revolution] Revolve054  label="moreFrontCaseScrewPost001"
  Angle = 360
  Axis = (0,1,0)
  Base = (0,0,0)
  FaceMakerClass = Part::FaceMakerBullseye
  Placement = pos=(102.5,4.5,3.5) rot=(0,0,1;0rad)
  Solid = false
  Source = -> Face050
  Symmetric = false
FEATURE [Part::Feature] Face051
  shape: bbox 4.8 x 25.5 x 2e-07 mm, 1 faces, 0 solids (baked)
FEATURE [Part::Revolution] Revolve055  label="moreFrontCaseScrewPost002"
  Angle = 360
  Axis = (0,1,0)
  Base = (0,0,0)
  FaceMakerClass = Part::FaceMakerBullseye
  Placement = pos=(102.5,4.5,68.5) rot=(0,0,1;0rad)
  Solid = false
  Source = -> Face051
  Symmetric = false
FEATURE [Sketcher::SketchObject] Sketch027
  FullyConstrained = true
  sketch-geometry (10):
    g0: LineSegment StartX=-1.6 StartY=4.7 StartZ=0 EndX=-1.6 EndY=1.7 EndZ=0
    g1: LineSegment StartX=-3.5 StartY=4.7 StartZ=0 EndX=-1.6 EndY=4.7 EndZ=0
    g2: LineSegment StartX=-1.6 StartY=1.7 StartZ=0 EndX=-1.6 EndY=1.5 EndZ=0
    g3: LineSegment StartX=-1.6 StartY=1.5 StartZ=0 EndX=-5.2 EndY=1.5 EndZ=0
    g4: Circle CenterX=-3.5 CenterY=4.7 CenterZ=0 NormalX=0 NormalY=0 NormalZ=1 AngleXU=0 Radius=1
    g5: Circle CenterX=-3.59627 CenterY=2.99743 CenterZ=0 NormalX=0 NormalY=0 NormalZ=1 AngleXU=0 Radius=1
    g6: Circle CenterX=-5.2 CenterY=1.5 CenterZ=0 NormalX=0 NormalY=0 NormalZ=1 AngleXU=0 Radius=1
    g7: BSplineCurve PolesCount=3 KnotsCount=2 Degree=2 IsPeriodic=0
    g8: GeomPoint X=-3.5 Y=4.7 Z=0
    g9: GeomPoint X=-5.2 Y=1.5 Z=0
  constraints (23):
    c: Vertical(g0)
    c: Distance(g0) = 3
    c: Coincident(g1,g0)
    c: Horizontal(g1)
    c: Block(g0)
    c: Block(g1)
    c: Coincident(g2,g0)
    c: Vertical(g2)
    c: Distance(g2) = 0.2
    c: Coincident(g3,g2)
    c: Horizontal(g3)
    c: Block(g3)
    c: Coincident(g7,g1)
    c: Weight(g4) = 1
    c: Equal(g4,g5)
    c: Equal(g4,g6)
    c: Coincident(g7,g3)
    c: InternalAlignment(g4,g7)
    c: InternalAlignment(g5,g7)
    c: InternalAlignment(g6,g7)
    c: InternalAlignment(g8,g7)
    c: InternalAlignment(g9,g7)
    c: Block(g7)
FEATURE [Sketcher::SketchObject] Sketch028
  FullyConstrained = true
  sketch-geometry (18):
    g0: LineSegment StartX=0 StartY=3e-16 StartZ=0 EndX=0 EndY=1.7 EndZ=0
    g1: LineSegment StartX=-3.5 StartY=0 StartZ=0 EndX=-3.5 EndY=0.9 EndZ=0
    g2: Circle CenterX=-2.7 CenterY=1.7 CenterZ=0 NormalX=0 NormalY=0 NormalZ=1 AngleXU=0 Radius=1
    g3: Circle CenterX=-3.5 CenterY=1.7 CenterZ=0 NormalX=0 NormalY=0 NormalZ=1 AngleXU=0 Radius=1
    g4: Circle CenterX=-3.5 CenterY=0.9 CenterZ=0 NormalX=0 NormalY=0 NormalZ=1 AngleXU=0 Radius=1
    g5: BSplineCurve PolesCount=3 KnotsCount=2 Degree=2 IsPeriodic=0
    g6: GeomPoint X=-2.7 Y=1.7 Z=0
    g7: GeomPoint X=-3.5 Y=0.9 Z=0
    g8: LineSegment StartX=-3.5 StartY=0 StartZ=0 EndX=-3.5 EndY=-7 EndZ=0
    g9: LineSegment StartX=0 StartY=3e-16 StartZ=0 EndX=0 EndY=-7 EndZ=0
    g10: LineSegment StartX=-3.5 StartY=-7 StartZ=0 EndX=0 EndY=-7 EndZ=0
    g11: LineSegment StartX=-2.7 StartY=1.7 StartZ=0 EndX=-1.6 EndY=1.7 EndZ=0
    g12: LineSegment StartX=0 StartY=1.7 StartZ=0 EndX=0 EndY=4.5 EndZ=0
    g13: LineSegment StartX=0 StartY=4.5 StartZ=0 EndX=0 EndY=10.8 EndZ=0
    g14: LineSegment StartX=0 StartY=10.8 StartZ=0 EndX=-2 EndY=10.8 EndZ=0
    g15: LineSegment StartX=-1.6 StartY=4.7 StartZ=0 EndX=-1.6 EndY=1.7 EndZ=0
    g16: LineSegment StartX=-1.6 StartY=4.7 StartZ=0 EndX=-2 EndY=4.7 EndZ=0
    g17: LineSegment StartX=-2 StartY=4.7 StartZ=0 EndX=-2 EndY=10.8 EndZ=0
  constraints (44):
    c: Vertical(g0)
    c: Vertical(g1)
    c: Distance(g1) = 0.9
    c: Block(g0)
    c: Distance(g0) = 1.7
    c: Weight(g2) = 1
    c: Equal(g2,g3)
    c: Equal(g2,g4)
    c: Coincident(g5,g1)
    c: InternalAlignment(g2,g5)
    c: InternalAlignment(g3,g5)
    c: InternalAlignment(g4,g5)
    c: InternalAlignment(g6,g5)
    c: InternalAlignment(g7,g5)
    c: Block(g5)
    c: Coincident(g8,g1)
    c: Vertical(g8)
    c: Distance(g8) = 7
    c: Vertical(g9)
    c: Equal(g8,g9) = 7
    c: Coincident(g9,g0)
    c: Coincident(g10,g8)
    c: Coincident(g10,g9)
    c: Horizontal(g10)
    c: Coincident(g11,g5)
    c: Horizontal(g11)
    c: Coincident(g12,g0)
    c: Vertical(g12)
    c: Distance(g12) = 2.8
    c: Coincident(g13,g12)
    c: Vertical(g13)
    c: Distance(g13) = 6.3
    c: Coincident(g14,g13)
    c: Horizontal(g14)
    c: Distance(g14) = 2
    c: Vertical(g15)
    c: Distance(g15) = 3
    c: Block(g11)
    c: Coincident(g15,g11)
    c: Coincident(g16,g15)
    c: Horizontal(g16)
    c: Coincident(g17,g16)
    c: Coincident(g17,g14)
    c: Vertical(g17)
FEATURE [Part::Revolution] Revolve040  label="backCaseScrewRetainer001"
  Angle = 360
  Axis = (0,1,0)
  Base = (0,0,0)
  FaceMakerClass = Part::FaceMakerBullseye
  Placement = pos=(12.5,3,10) rot=(0,0,1;0rad)
  Solid = false
  Source = -> Face036
  Symmetric = false
FEATURE [Part::Feature] Face055
  shape: bbox 3.5 x 30.2 x 2e-07 mm, 1 faces, 0 solids (baked)
FEATURE [Part::Revolution] Revolve059  label="backCaseScrewPost"
  Angle = 360
  Axis = (0,1,0)
  Base = (0,0,0)
  FaceMakerClass = Part::FaceMakerBullseye
  Placement = pos=(12.5,4.5,10) rot=(0,0,1;0rad)
  Solid = false
  Source = -> Face055
  Symmetric = false
FEATURE [Part::Feature] Face056
  shape: bbox 3.5 x 30.2 x 2e-07 mm, 1 faces, 0 solids (baked)
FEATURE [Part::Revolution] Revolve060  label="backCaseScrewPost001"
  Angle = 360
  Axis = (0,1,0)
  Base = (0,0,0)
  FaceMakerClass = Part::FaceMakerBullseye
  Placement = pos=(12.5,4.5,62) rot=(0,0,1;0rad)
  Solid = false
  Source = -> Face056
  Symmetric = false
FEATURE [Part::Feature] Face057
  shape: bbox 3.5 x 17.8 x 2e-07 mm, 1 faces, 0 solids (baked)
FEATURE [Part::Revolution] Revolve061  label="removeToCreateScrewAndThreadedInsertHole"
  Angle = 360
  Axis = (0,1,0)
  Base = (0,0,0)
  FaceMakerClass = Part::FaceMakerBullseye
  Placement = pos=(12.5,0,10) rot=(0,0,1;0rad)
  Solid = false
  Source = -> Face057
  Symmetric = false
FEATURE [Part::Feature] Face058
  shape: bbox 3.5 x 17.8 x 2e-07 mm, 1 faces, 0 solids (baked)
FEATURE [Part::Revolution] Revolve062  label="removeToCreateScrewAndThreadedInsertHole001"
  Angle = 360
  Axis = (0,1,0)
  Base = (0,0,0)
  FaceMakerClass = Part::FaceMakerBullseye
  Placement = pos=(12.5,0,62) rot=(0,0,1;0rad)
  Solid = false
  Source = -> Face058
  Symmetric = false
FEATURE [Part::Feature] Face059
  shape: bbox 3.5 x 17.8 x 2e-07 mm, 1 faces, 0 solids (baked)
FEATURE [Part::Revolution] Revolve063  label="removeToCreateScrewAndThreadedInsertHole002"
  Angle = 360
  Axis = (0,1,0)
  Base = (0,0,0)
  FaceMakerClass = Part::FaceMakerBullseye
  Placement = pos=(89.5,0,68.5) rot=(0,0,1;0rad)
  Solid = false
  Source = -> Face059
  Symmetric = false
FEATURE [Part::Feature] Face060
  shape: bbox 3.5 x 17.8 x 2e-07 mm, 1 faces, 0 solids (baked)
FEATURE [Part::Revolution] Revolve064  label="removeToCreateScrewAndThreadedInsertHole003"
  Angle = 360
  Axis = (0,1,0)
  Base = (0,0,0)
  FaceMakerClass = Part::FaceMakerBullseye
  Placement = pos=(89.5,0,3.5) rot=(0,0,1;0rad)
  Solid = false
  Source = -> Face060
  Symmetric = false
FEATURE [Part::Feature] Face061
  shape: bbox 3.5 x 17.8 x 2e-07 mm, 1 faces, 0 solids (baked)
FEATURE [Part::Revolution] Revolve065  label="removeToCreateScrewAndThreadedInsertHole004"
  Angle = 360
  Axis = (0,1,0)
  Base = (0,0,0)
  FaceMakerClass = Part::FaceMakerBullseye
  Placement = pos=(102.5,4.7,3.5) rot=(0,0,1;0rad)
  Solid = false
  Source = -> Face061
  Symmetric = false
FEATURE [Part::Feature] Face062
  shape: bbox 3.5 x 17.8 x 2e-07 mm, 1 faces, 0 solids (baked)
FEATURE [Part::Revolution] Revolve066  label="removeToCreateScrewAndThreadedInsertHole005"
  Angle = 360
  Axis = (0,1,0)
  Base = (0,0,0)
  FaceMakerClass = Part::FaceMakerBullseye
  Placement = pos=(102.5,4.7,68.5) rot=(0,0,1;0rad)
  Solid = false
  Source = -> Face062
  Symmetric = false
FEATURE [Part::MultiFuse] Fusion047  label="makeHoles"
  Shapes = -> [Revolve066,Revolve065,Revolve064,Revolve063,Revolve062,Revolve061]
FEATURE [Part::Feature] Face063
  shape: bbox 3.6 x 3.2 x 2e-07 mm, 1 faces, 0 solids (baked)
FEATURE [Part::Revolution] Revolve067  label="moreFrontCaseScrewRetainer002"
  Angle = 360
  Axis = (0,1,0)
  Base = (0,0,0)
  FaceMakerClass = Part::FaceMakerBullseye
  Placement = pos=(102.5,4.5,68.5) rot=(0,0,1;0rad)
  Solid = false
  Source = -> Face063
  Symmetric = false
FEATURE [Part::Feature] Face064
  shape: bbox 3.6 x 3.2 x 2e-07 mm, 1 faces, 0 solids (baked)
FEATURE [Part::Revolution] Revolve068  label="moreFrontCaseScrewRetainer003"
  Angle = 360
  Axis = (0,1,0)
  Base = (0,0,0)
  FaceMakerClass = Part::FaceMakerBullseye
  Placement = pos=(102.5,4.5,3.5) rot=(0,0,1;0rad)
  Solid = false
  Source = -> Face064
  Symmetric = false
FEATURE [Part::Feature] Face065
  shape: bbox 3.5 x 17.8 x 2e-07 mm, 1 faces, 0 solids (baked)
FEATURE [Part::Revolution] Revolve069  label="removeToCreateScrewAndThreadedInsertHole006"
  Angle = 360
  Axis = (0,1,0)
  Base = (0,0,0)
  FaceMakerClass = Part::FaceMakerBullseye
  Placement = pos=(12.5,0,10) rot=(0,0,1;0rad)
  Solid = false
  Source = -> Face065
  Symmetric = false
FEATURE [Part::Feature] Face066
  shape: bbox 3.5 x 17.8 x 2e-07 mm, 1 faces, 0 solids (baked)
FEATURE [Part::Revolution] Revolve070  label="removeToCreateScrewAndThreadedInsertHole007"
  Angle = 360
  Axis = (0,1,0)
  Base = (0,0,0)
  FaceMakerClass = Part::FaceMakerBullseye
  Placement = pos=(12.5,0,62) rot=(0,0,1;0rad)
  Solid = false
  Source = -> Face066
  Symmetric = false
FEATURE [Part::Feature] Face067
  shape: bbox 3.5 x 17.8 x 2e-07 mm, 1 faces, 0 solids (baked)
FEATURE [Part::Revolution] Revolve071  label="removeToCreateScrewAndThreadedInsertHole008"
  Angle = 360
  Axis = (0,1,0)
  Base = (0,0,0)
  FaceMakerClass = Part::FaceMakerBullseye
  Placement = pos=(89.5,0,68.5) rot=(0,0,1;0rad)
  Solid = false
  Source = -> Face067
  Symmetric = false
FEATURE [Part::Feature] Face068
  shape: bbox 3.5 x 17.8 x 2e-07 mm, 1 faces, 0 solids (baked)
FEATURE [Part::Revolution] Revolve072  label="removeToCreateScrewAndThreadedInsertHole009"
  Angle = 360
  Axis = (0,1,0)
  Base = (0,0,0)
  FaceMakerClass = Part::FaceMakerBullseye
  Placement = pos=(89.5,0,3.5) rot=(0,0,1;0rad)
  Solid = false
  Source = -> Face068
  Symmetric = false
FEATURE [Part::Feature] Face069
  shape: bbox 3.5 x 17.8 x 2e-07 mm, 1 faces, 0 solids (baked)
FEATURE [Part::Feature] Face070
  shape: bbox 3.5 x 17.8 x 2e-07 mm, 1 faces, 0 solids (baked)
FEATURE [Part::Revolution] Revolve073  label="removeToCreateScrewAndThreadedInsertHole010"
  Angle = 360
  Axis = (0,1,0)
  Base = (0,0,0)
  FaceMakerClass = Part::FaceMakerBullseye
  Placement = pos=(102.5,4.7,3.5) rot=(0,0,1;0rad)
  Solid = false
  Source = -> Face069
  Symmetric = false
FEATURE [Part::Revolution] Revolve074  label="removeToCreateScrewAndThreadedInsertHole011"
  Angle = 360
  Axis = (0,1,0)
  Base = (0,0,0)
  FaceMakerClass = Part::FaceMakerBullseye
  Placement = pos=(102.5,4.7,68.5) rot=(0,0,1;0rad)
  Solid = false
  Source = -> Face070
  Symmetric = false
FEATURE [Part::MultiFuse] Fusion048  label="makeHoles001"
  Shapes = -> [Revolve074,Revolve073,Revolve072,Revolve071,Revolve070,Revolve069]
FEATURE [Part::MultiFuse] Fusion049  label="caseScrewRetainers"
  Shapes = -> [Revolve067,Revolve068,Revolve048,Revolve047,Revolve039,Revolve040]
FEATURE [Part::Cut] Cut015  label="caseScrewRetainers001"
  Base = -> Fusion049
  Tool = -> Fusion048
FEATURE [Part::MultiFuse] Fusion050  label="casePillars"
  Shapes = -> [Revolve055,Revolve054,Revolve043,Revolve046,Revolve059,Revolve060]
FEATURE [Part::Feature] Face071 .. Face076  x6 (patterned run collapsed; names and placements below)
  shape: bbox 3.5 x 17.8 x 2e-07 mm, 1 faces, 0 solids (baked)
FEATURE [Part::Revolution] Revolve075  label="removeToCreateScrewAndThreadedInsertHole012"
  Angle = 360
  Axis = (0,1,0)
  Base = (0,0,0)
  FaceMakerClass = Part::FaceMakerBullseye
  Placement = pos=(12.5,0,10) rot=(0,0,1;0rad)
  Solid = false
  Source = -> Face071
  Symmetric = false
FEATURE [Part::Revolution] Revolve076  label="removeToCreateScrewAndThreadedInsertHole013"
  Angle = 360
  Axis = (0,1,0)
  Base = (0,0,0)
  FaceMakerClass = Part::FaceMakerBullseye
  Placement = pos=(12.5,0,62) rot=(0,0,1;0rad)
  Solid = false
  Source = -> Face072
  Symmetric = false
FEATURE [Part::Revolution] Revolve077  label="removeToCreateScrewAndThreadedInsertHole014"
  Angle = 360
  Axis = (0,1,0)
  Base = (0,0,0)
  FaceMakerClass = Part::FaceMakerBullseye
  Placement = pos=(89.5,0,68.5) rot=(0,0,1;0rad)
  Solid = false
  Source = -> Face073
  Symmetric = false
FEATURE [Part::Revolution] Revolve078  label="removeToCreateScrewAndThreadedInsertHole015"
  Angle = 360
  Axis = (0,1,0)
  Base = (0,0,0)
  FaceMakerClass = Part::FaceMakerBullseye
  Placement = pos=(89.5,0,3.5) rot=(0,0,1;0rad)
  Solid = false
  Source = -> Face074
  Symmetric = false
FEATURE [Part::Revolution] Revolve079  label="removeToCreateScrewAndThreadedInsertHole016"
  Angle = 360
  Axis = (0,1,0)
  Base = (0,0,0)
  FaceMakerClass = Part::FaceMakerBullseye
  Placement = pos=(102.5,4.7,3.5) rot=(0,0,1;0rad)
  Solid = false
  Source = -> Face075
  Symmetric = false
FEATURE [Part::Revolution] Revolve080  label="removeToCreateScrewAndThreadedInsertHole017"
  Angle = 360
  Axis = (0,1,0)
  Base = (0,0,0)
  FaceMakerClass = Part::FaceMakerBullseye
  Placement = pos=(102.5,4.7,68.5) rot=(0,0,1;0rad)
  Solid = false
  Source = -> Face076
  Symmetric = false
FEATURE [Part::MultiFuse] Fusion051  label="makeHoles002"
  Shapes = -> [Revolve080,Revolve079,Revolve078,Revolve077,Revolve076,Revolve075]
FEATURE [Part::Cut] Cut016  label="caesPillars"
  Base = -> Fusion050
  Tool = -> Fusion051
FEATURE [Part::Revolution] Revolve009  label="plugHousing016"
  Angle = 360
  Axis = (0,1,0)
  Base = (0,0,0)
  FaceMakerClass = Part::FaceMakerBullseye
  Placement = pos=(0,0,36.15) rot=(0,0,1;0rad)
  Solid = false
  Source = -> Face012
  Symmetric = false
FEATURE [Part::MultiFuse] Fusion014  label="plugHousing023"
  Placement = pos=(0,0,0) rot=(0,0,1;1.5708rad)
  Shapes = -> [Revolve011,Revolve009]
FEATURE [Part::Revolution] Revolve010  label="plugHousing017"
  Angle = 360
  Axis = (0,1,0)
  Base = (0,0,0)
  FaceMakerClass = Part::FaceMakerBullseye
  Placement = pos=(0,0,36.15) rot=(0,0,1;0rad)
  Solid = false
  Source = -> Face014
  Symmetric = false
FEATURE [Part::MultiFuse] Fusion015  label="plugHousing024"
  Placement = pos=(0,0,0) rot=(0,0,1;1.5708rad)
  Shapes = -> [Revolve010,Revolve015]
FEATURE [Part::Revolution] Revolve014  label="plugHousing026"
  Angle = 360
  Axis = (0,1,0)
  Base = (0,0,0)
  FaceMakerClass = Part::FaceMakerBullseye
  Placement = pos=(0,0,36.15) rot=(0,0,1;0rad)
  Solid = false
  Source = -> Face011
  Symmetric = false
FEATURE [Part::Revolution] Revolve013  label="plugHousing025"
  Angle = 360
  Axis = (0,1,0)
  Base = (0,0,0)
  FaceMakerClass = Part::FaceMakerBullseye
  Placement = pos=(0,0,36.15) rot=(0,0,1;0rad)
  Solid = false
  Source = -> Face015
  Symmetric = false
FEATURE [Part::MultiFuse] Fusion016  label="plugHousing028"
  Placement = pos=(0,19,0) rot=(0,0,1;3.14159rad)
  Shapes = -> [Fusion014,Fusion013]
FEATURE [Part::MultiFuse] Fusion011  label="plugHousing018"
  Placement = pos=(0,0,0) rot=(0,0,1;1.5708rad)
  Shapes = -> [Revolve014,Revolve013]
FEATURE [Part::MultiFuse] Fusion012  label="plugHousing019"
  Placement = pos=(0,19,0) rot=(0,0,1;3.14159rad)
  Shapes = -> [Fusion011,Fusion015]
FEATURE [Part::MultiFuse] Fusion017  label="plugHousing029"
  Placement = pos=(122.621,0,-0.15) rot=(0,0,1;0rad)
  Shapes = -> [Fusion016,Fusion012]
FEATURE [Part::MultiFuse] Fusion052  label="casePillarRetainers"
  Shapes = -> [Extrude012,Extrude013,Extrude014,Extrude015,Extrude016,Extrude017,Extrude018,Extrude019,Box011,Box012]
FEATURE [Part::Feature] Face077
  shape: bbox 3.5 x 17.8 x 2e-07 mm, 1 faces, 0 solids (baked)
FEATURE [Part::Revolution] Revolve081  label="removeToCreateScrewAndThreadedInsertHole018"
  Angle = 360
  Axis = (0,1,0)
  Base = (0,0,0)
  FaceMakerClass = Part::FaceMakerBullseye
  Placement = pos=(62.3,30.3,19.7) rot=(0,0,1;0rad)
  Solid = false
  Source = -> Face077
  Symmetric = false
FEATURE [Part::Feature] Face078
  shape: bbox 3.5 x 17.8 x 2e-07 mm, 1 faces, 0 solids (baked)
FEATURE [Part::Revolution] Revolve082  label="removeToCreateScrewAndThreadedInsertHole019"
  Angle = 360
  Axis = (0,1,0)
  Base = (0,0,0)
  FaceMakerClass = Part::FaceMakerBullseye
  Placement = pos=(62.3,30.3,51.7) rot=(0,0,1;0rad)
  Solid = false
  Source = -> Face078
  Symmetric = false
FEATURE [Part::Feature] Face079
  shape: bbox 3.5 x 17.8 x 2e-07 mm, 1 faces, 0 solids (baked)
FEATURE [Part::Revolution] Revolve083  label="removeToCreateScrewAndThreadedInsertHole020"
  Angle = 360
  Axis = (0,1,0)
  Base = (0,0,0)
  FaceMakerClass = Part::FaceMakerBullseye
  Placement = pos=(30.3,30.3,19.7) rot=(0,0,1;0rad)
  Solid = false
  Source = -> Face079
  Symmetric = false
FEATURE [Part::Feature] Face080
  shape: bbox 3.5 x 17.8 x 2e-07 mm, 1 faces, 0 solids (baked)
FEATURE [Part::Revolution] Revolve084  label="removeToCreateScrewAndThreadedInsertHole021"
  Angle = 360
  Axis = (0,1,0)
  Base = (0,0,0)
  FaceMakerClass = Part::FaceMakerBullseye
  Placement = pos=(30.3,30.3,51.7) rot=(0,0,1;0rad)
  Solid = false
  Source = -> Face080
  Symmetric = false
FEATURE [Part::MultiFuse] Fusion053  label="createThreadedInsertHolesForFan"
  Shapes = -> [Revolve081,Revolve082,Revolve083,Revolve084]
FEATURE [Part::Cut] Cut017  label="fanScrewHousing001"
  Base = -> Fusion046
  Tool = -> Fusion053
FEATURE [Part::Feature] Face081
  shape: bbox 3.5 x 17.8 x 2e-07 mm, 1 faces, 0 solids (baked)
FEATURE [Part::Revolution] Revolve085  label="removeToCreateScrewAndThreadedInsertHole022"
  Angle = 360
  Axis = (0,1,0)
  Base = (0,0,0)
  FaceMakerClass = Part::FaceMakerBullseye
  Placement = pos=(62.3,30.3,19.7) rot=(0,0,1;0rad)
  Solid = false
  Source = -> Face081
  Symmetric = false
FEATURE [Part::Feature] Face082
  shape: bbox 3.5 x 17.8 x 2e-07 mm, 1 faces, 0 solids (baked)
FEATURE [Part::Revolution] Revolve086  label="removeToCreateScrewAndThreadedInsertHole023"
  Angle = 360
  Axis = (0,1,0)
  Base = (0,0,0)
  FaceMakerClass = Part::FaceMakerBullseye
  Placement = pos=(62.3,30.3,51.7) rot=(0,0,1;0rad)
  Solid = false
  Source = -> Face082
  Symmetric = false
FEATURE [Part::Feature] Face083
  shape: bbox 3.5 x 17.8 x 2e-07 mm, 1 faces, 0 solids (baked)
FEATURE [Part::Revolution] Revolve087  label="removeToCreateScrewAndThreadedInsertHole024"
  Angle = 360
  Axis = (0,1,0)
  Base = (0,0,0)
  FaceMakerClass = Part::FaceMakerBullseye
  Placement = pos=(30.3,30.3,19.7) rot=(0,0,1;0rad)
  Solid = false
  Source = -> Face083
  Symmetric = false
FEATURE [Part::Feature] Face084
  shape: bbox 3.5 x 17.8 x 2e-07 mm, 1 faces, 0 solids (baked)
FEATURE [Part::Revolution] Revolve088  label="removeToCreateScrewAndThreadedInsertHole025"
  Angle = 360
  Axis = (0,1,0)
  Base = (0,0,0)
  FaceMakerClass = Part::FaceMakerBullseye
  Placement = pos=(30.3,30.3,51.7) rot=(0,0,1;0rad)
  Solid = false
  Source = -> Face084
  Symmetric = false
FEATURE [Part::MultiFuse] Fusion054  label="createThreadedInsertHolesForFan001"
  Shapes = -> [Revolve085,Revolve086,Revolve087,Revolve088]
FEATURE [Part::Cut] Cut018  label="top007"
  Base = -> Fusion040
  Tool = -> Fusion054
FEATURE [Sketcher::SketchObject] Sketch029
  FullyConstrained = false
  Placement = pos=(0,0,0) rot=(1,0,0;1.5708rad)
  sketch-geometry (24):
    g0: ArcOfCircle CenterX=-4 CenterY=-10.5 CenterZ=0 NormalX=0 NormalY=0 NormalZ=1 AngleXU=0 Radius=1.5 StartAngle=6e-16 EndAngle=3.14159
    g1: ArcOfCircle CenterX=-34.2 CenterY=-10.5 CenterZ=0 NormalX=0 NormalY=0 NormalZ=1 AngleXU=0 Radius=1.5 StartAngle=0 EndAngle=3.14159
    g2: ArcOfCircle CenterX=-34.2 CenterY=-27.7 CenterZ=0 NormalX=0 NormalY=0 NormalZ=1 AngleXU=0 Radius=1.5 StartAngle=3.14159 EndAngle=6.28319
    g3: ArcOfCircle CenterX=-4 CenterY=-27.7 CenterZ=0 NormalX=0 NormalY=0 NormalZ=1 AngleXU=0 Radius=1.5 StartAngle=3.1416 EndAngle=6.28319
    g4: ArcOfCircle CenterX=-10 CenterY=-4.3 CenterZ=0 NormalX=0 NormalY=0 NormalZ=1 AngleXU=0 Radius=1.5 StartAngle=2e-16 EndAngle=3.14159
    g5: ArcOfCircle CenterX=-16.1 CenterY=-1.8 CenterZ=0 NormalX=0 NormalY=0 NormalZ=1 AngleXU=0 Radius=1.5 StartAngle=5e-16 EndAngle=3.14159
    g6: ArcOfCircle CenterX=-22.1 CenterY=-1.8 CenterZ=0 NormalX=0 NormalY=0 NormalZ=1 AngleXU=0 Radius=1.5 StartAngle=5e-16 EndAngle=3.14159
    g7: ArcOfCircle CenterX=-28.2 CenterY=-4.3 CenterZ=0 NormalX=0 NormalY=0 NormalZ=1 AngleXU=0 Radius=1.5 StartAngle=2e-16 EndAngle=3.14159
    g8: ArcOfCircle CenterX=-10 CenterY=-33.9 CenterZ=0 NormalX=0 NormalY=0 NormalZ=1 AngleXU=0 Radius=1.5 StartAngle=3.14159 EndAngle=6.28319
    g9: ArcOfCircle CenterX=-16.1 CenterY=-36.4 CenterZ=0 NormalX=0 NormalY=0 NormalZ=1 AngleXU=0 Radius=1.5 StartAngle=3.14159 EndAngle=6.28319
    g10: ArcOfCircle CenterX=-22.1 CenterY=-36.4 CenterZ=0 NormalX=0 NormalY=0 NormalZ=1 AngleXU=0 Radius=1.5 StartAngle=3.14159 EndAngle=6.28319
    g11: ArcOfCircle CenterX=-28.2 CenterY=-33.9 CenterZ=0 NormalX=0 NormalY=0 NormalZ=1 AngleXU=0 Radius=1.5 StartAngle=3.14159 EndAngle=6.28319
    g12: LineSegment StartX=-35.7 StartY=-10.5 StartZ=0 EndX=-35.7 EndY=-27.7 EndZ=0
    g13: LineSegment StartX=-32.7 StartY=-10.5 StartZ=0 EndX=-32.7 EndY=-27.7 EndZ=0
    g14: LineSegment StartX=-29.7 StartY=-33.9 StartZ=0 EndX=-29.7 EndY=-4.3 EndZ=0
    g15: LineSegment StartX=-26.7 StartY=-33.9 StartZ=0 EndX=-26.7 EndY=-4.3 EndZ=0
    g16: LineSegment StartX=-2.5 StartY=-10.5 StartZ=0 EndX=-2.5 EndY=-27.7 EndZ=0
    g17: LineSegment StartX=-8.5 StartY=-4.3 StartZ=0 EndX=-8.5 EndY=-33.9 EndZ=0
    g18: LineSegment StartX=-5.5 StartY=-10.5 StartZ=0 EndX=-5.5 EndY=-27.7 EndZ=0
    g19: LineSegment StartX=-11.5 StartY=-4.3 StartZ=0 EndX=-11.5 EndY=-33.9 EndZ=0
    g20: LineSegment StartX=-14.6 StartY=-1.8 StartZ=0 EndX=-14.6 EndY=-36.4 EndZ=0
    g21: LineSegment StartX=-17.6 StartY=-1.8 StartZ=0 EndX=-17.6 EndY=-36.4 EndZ=0
    g22: LineSegment StartX=-20.6 StartY=-36.4 StartZ=0 EndX=-20.6 EndY=-1.8 EndZ=0
    g23: LineSegment StartX=-23.6 StartY=-1.8 StartZ=0 EndX=-23.6 EndY=-36.4 EndZ=0
  constraints (48):
    c: Block(g0)
    c: Block(g1)
    c: Block(g2)
    c: Block(g3)
    c: Block(g4)
    c: Block(g5)
    c: Block(g6)
    c: Block(g7)
    c: Block(g8)
    c: Block(g9)
    c: Block(g10)
    c: Block(g11)
    c: Coincident(g12,g1)
    c: Coincident(g12,g2)
    c: Vertical(g12)
    c: Coincident(g13,g1)
    c: Coincident(g13,g2)
    c: Vertical(g13)
    c: Coincident(g14,g11)
    c: Coincident(g14,g7)
    c: Vertical(g14)
    c: Coincident(g15,g11)
    c: Coincident(g15,g7)
    c: Vertical(g15)
    c: Coincident(g16,g0)
    c: Coincident(g16,g3)
    c: Vertical(g16)
    c: Coincident(g17,g4)
    c: Coincident(g17,g8)
    c: Vertical(g17)
    c: Coincident(g18,g0)
    c: Coincident(g18,g3)
    c: Vertical(g18)
    c: Coincident(g19,g4)
    c: Coincident(g19,g8)
    c: Vertical(g19)
    c: Coincident(g20,g5)
    c: Coincident(g20,g9)
    c: Vertical(g20)
    c: Coincident(g21,g5)
    c: Coincident(g21,g9)
    c: Vertical(g21)
    c: Coincident(g22,g10)
    c: Coincident(g22,g6)
    c: Vertical(g22)
    c: Coincident(g23,g6)
    c: Coincident(g23,g10)
    c: Vertical(g23)
FEATURE [Part::Extrusion] Extrude020  label="removeToCreateFanGrillHoles"
  Base = -> Sketch029
  Dir = (0,-1,6e-16)
  DirMode = 2
  FaceMakerClass = Part::FaceMakerBullseye
  LengthFwd = 10
  LengthRev = 0
  Placement = pos=(65.4,44,54.82) rot=(0,0,1;0rad)
  Solid = true
  Symmetric = false
FEATURE [Part::MultiFuse] Fusion055  label="top008"
  Shapes = -> [Cut017,Cut018]
FEATURE [Part::Cut] Cut019  label="top009"
  Base = -> Fusion055
  Tool = -> Extrude020
FEATURE [App::MeasureDistance] Distance003  label="Distance: 71.95 mm"
  Distance = 71.9513
  P1 = (117,38,72)
  P2 = (117,38,0.0487319)
FEATURE [Sketcher::SketchObject] Sketch030
  FullyConstrained = true
  Placement = pos=(117,19,0) rot=(0.57735,0.57735,0.57735;2.0944rad)
  sketch-geometry (48):
    g0: LineSegment StartX=-49.19 StartY=69.25 StartZ=0 EndX=-49.19 EndY=66.25 EndZ=0
    g1: LineSegment StartX=-49.19 StartY=63.5 StartZ=0 EndX=-49.19 EndY=60.5 EndZ=0
    g2: LineSegment StartX=-49.19 StartY=57.75 StartZ=0 EndX=-49.19 EndY=54.75 EndZ=0
    g3: LineSegment StartX=-49.19 StartY=52 StartZ=0 EndX=-49.19 EndY=49 EndZ=0
    g4: LineSegment StartX=-49.19 StartY=46.25 StartZ=0 EndX=-49.19 EndY=43.25 EndZ=0
    g5: LineSegment StartX=-49.19 StartY=40.5 StartZ=0 EndX=-49.19 EndY=37.5 EndZ=0
    g6: LineSegment StartX=-49.19 StartY=34.5 StartZ=0 EndX=-49.19 EndY=31.5 EndZ=0
    g7: LineSegment StartX=-49.19 StartY=28.75 StartZ=0 EndX=-49.19 EndY=25.75 EndZ=0
    g8: LineSegment StartX=-49.19 StartY=23 StartZ=0 EndX=-49.19 EndY=20 EndZ=0
    g9: LineSegment StartX=-49.19 StartY=17.25 StartZ=0 EndX=-49.19 EndY=14.25 EndZ=0
    g10: LineSegment StartX=-49.19 StartY=11.5 StartZ=0 EndX=-49.19 EndY=8.5 EndZ=0
    g11: LineSegment StartX=-49.19 StartY=5.75 StartZ=0 EndX=-49.19 EndY=2.75 EndZ=0
    g12: ArcOfCircle CenterX=-1.5 CenterY=67.75 CenterZ=0 NormalX=0 NormalY=0 NormalZ=1 AngleXU=0 Radius=1.5 StartAngle=4.71239 EndAngle=7.85398
    g13: ArcOfCircle CenterX=-1.5 CenterY=62 CenterZ=0 NormalX=0 NormalY=0 NormalZ=1 AngleXU=0 Radius=1.5 StartAngle=4.71239 EndAngle=7.85398
    g14: ArcOfCircle CenterX=-1.5 CenterY=56.25 CenterZ=0 NormalX=0 NormalY=0 NormalZ=1 AngleXU=0 Radius=1.5 StartAngle=4.71239 EndAngle=7.85398
    g15: ArcOfCircle CenterX=-11.49 CenterY=50.5 CenterZ=0 NormalX=0 NormalY=0 NormalZ=1 AngleXU=0 Radius=1.5 StartAngle=4.71239 EndAngle=7.85398
    g16: ArcOfCircle CenterX=-16.28 CenterY=44.75 CenterZ=0 NormalX=0 NormalY=0 NormalZ=1 AngleXU=0 Radius=1.5 StartAngle=4.71239 EndAngle=7.85398
    g17: ArcOfCircle CenterX=-18.2337 CenterY=39 CenterZ=0 NormalX=0 NormalY=0 NormalZ=1 AngleXU=0 Radius=1.5 StartAngle=4.71485 EndAngle=7.85398
    g18: ArcOfCircle CenterX=-16.2837 CenterY=27.25 CenterZ=0 NormalX=0 NormalY=0 NormalZ=1 AngleXU=0 Radius=1.5 StartAngle=4.71485 EndAngle=7.85398
    g19: ArcOfCircle CenterX=-18.2337 CenterY=33 CenterZ=0 NormalX=0 NormalY=0 NormalZ=1 AngleXU=0 Radius=1.5 StartAngle=4.71485 EndAngle=7.85398
    g20: ArcOfCircle CenterX=-11.49 CenterY=21.5 CenterZ=0 NormalX=0 NormalY=0 NormalZ=1 AngleXU=0 Radius=1.5 StartAngle=4.71239 EndAngle=7.85398
    g21: ArcOfCircle CenterX=-1.5 CenterY=4.25 CenterZ=0 NormalX=0 NormalY=0 NormalZ=1 AngleXU=0 Radius=1.5 StartAngle=4.71239 EndAngle=7.85398
    g22: ArcOfCircle CenterX=-1.5 CenterY=10 CenterZ=0 NormalX=0 NormalY=0 NormalZ=1 AngleXU=0 Radius=1.5 StartAngle=4.71239 EndAngle=7.85398
    g23: ArcOfCircle CenterX=-1.5 CenterY=15.75 CenterZ=0 NormalX=0 NormalY=0 NormalZ=1 AngleXU=0 Radius=1.5 StartAngle=4.71239 EndAngle=7.85398
    g24: LineSegment StartX=-49.19 StartY=69.25 StartZ=0 EndX=-1.5 EndY=69.25 EndZ=0
    g25: LineSegment StartX=-49.19 StartY=66.25 StartZ=0 EndX=-1.5 EndY=66.25 EndZ=0
    g26: LineSegment StartX=-49.19 StartY=63.5 StartZ=0 EndX=-1.5 EndY=63.5 EndZ=0
    g27: LineSegment StartX=-49.19 StartY=60.5 StartZ=0 EndX=-1.5 EndY=60.5 EndZ=0
    g28: LineSegment StartX=-49.19 StartY=57.75 StartZ=0 EndX=-1.5 EndY=57.75 EndZ=0
    g29: LineSegment StartX=-49.19 StartY=54.75 StartZ=0 EndX=-1.5 EndY=54.75 EndZ=0
    g30: LineSegment StartX=-49.19 StartY=52 StartZ=0 EndX=-11.49 EndY=52 EndZ=0
    g31: LineSegment StartX=-49.19 StartY=49 StartZ=0 EndX=-11.49 EndY=49 EndZ=0
    g32: LineSegment StartX=-49.19 StartY=46.25 StartZ=0 EndX=-16.28 EndY=46.25 EndZ=0
    g33: LineSegment StartX=-49.19 StartY=43.25 StartZ=0 EndX=-16.28 EndY=43.25 EndZ=0
    g34: LineSegment StartX=-49.19 StartY=40.5 StartZ=0 EndX=-18.2337 EndY=40.5 EndZ=0
    g35: LineSegment StartX=-49.19 StartY=37.5 StartZ=0 EndX=-18.23 EndY=37.5 EndZ=0
    g36: LineSegment StartX=-49.19 StartY=34.5 StartZ=0 EndX=-18.2337 EndY=34.5 EndZ=0
    g37: LineSegment StartX=-49.19 StartY=31.5 StartZ=0 EndX=-18.23 EndY=31.5 EndZ=0
    g38: LineSegment StartX=-49.19 StartY=28.75 StartZ=0 EndX=-16.2837 EndY=28.75 EndZ=0
    g39: LineSegment StartX=-49.19 StartY=25.75 StartZ=0 EndX=-16.28 EndY=25.75 EndZ=0
    g40: LineSegment StartX=-49.19 StartY=23 StartZ=0 EndX=-11.49 EndY=23 EndZ=0
    g41: LineSegment StartX=-49.19 StartY=20 StartZ=0 EndX=-11.49 EndY=20 EndZ=0
    g42: LineSegment StartX=-49.19 StartY=17.25 StartZ=0 EndX=-1.5 EndY=17.25 EndZ=0
    g43: LineSegment StartX=-49.19 StartY=14.25 StartZ=0 EndX=-1.5 EndY=14.25 EndZ=0
    g44: LineSegment StartX=-49.19 StartY=11.5 StartZ=0 EndX=-1.5 EndY=11.5 EndZ=0
    g45: LineSegment StartX=-49.19 StartY=8.5 StartZ=0 EndX=-1.5 EndY=8.5 EndZ=0
    g46: LineSegment StartX=-49.19 StartY=5.75 StartZ=0 EndX=-1.5 EndY=5.75 EndZ=0
    g47: LineSegment StartX=-49.19 StartY=2.75 StartZ=0 EndX=-1.5 EndY=2.75 EndZ=0
  constraints (120):
    c: Vertical(g0)
    c: Distance(g0) = 3
    c: Block(g0)
    c: Vertical(g1)
    c: Distance(g1) = 3
    c: Vertical(g2)
    c: Equal(g0,g2) = 3
    c: Block(g2)
    c: Vertical(g3)
    c: Equal(g1,g3) = 3
    c: Vertical(g4)
    c: Equal(g0,g4) = 3
    c: Block(g4)
    c: Vertical(g5)
    c: Equal(g1,g5) = 3
    c: Vertical(g6)
    c: Equal(g0,g6) = 3
    c: Block(g6)
    c: Vertical(g7)
    c: Equal(g1,g7) = 3
    c: Vertical(g8)
    c: Equal(g0,g8) = 3
    c: Block(g8)
    c: Vertical(g9)
    c: Equal(g1,g9) = 3
    c: Vertical(g10)
    c: Equal(g0,g10) = 3
    c: Block(g10)
    c: Vertical(g11)
    c: Equal(g1,g11) = 3
    c: Block(g12)
    c: Block(g13)
    c: Block(g14)
    c: Block(g15)
    c: Block(g16)
    c: Block(g17)
    c: Block(g18)
    c: Block(g19)
    c: Block(g20)
    c: Block(g21)
    c: Block(g22)
    c: Block(g23)
    c: Block(g11)
    c: Block(g9)
    c: Block(g7)
    c: Block(g5)
    c: Block(g3)
    c: Block(g1)
    c: Coincident(g24,g0)
    c: Coincident(g24,g12)
    c: Horizontal(g24)
    c: Coincident(g25,g0)
    c: Coincident(g25,g12)
    c: Horizontal(g25)
    c: Coincident(g26,g1)
    c: Coincident(g26,g13)
    c: Horizontal(g26)
    c: Coincident(g27,g1)
    c: Coincident(g27,g13)
    c: Horizontal(g27)
    c: Coincident(g28,g2)
    c: Coincident(g28,g14)
    c: Horizontal(g28)
    c: Coincident(g29,g2)
    c: Coincident(g29,g14)
    c: Horizontal(g29)
    c: Coincident(g30,g3)
    c: Coincident(g30,g15)
    c: Horizontal(g30)
    c: Coincident(g31,g3)
    c: Coincident(g31,g15)
    c: Horizontal(g31)
    c: Coincident(g32,g4)
    c: Coincident(g32,g16)
    c: Horizontal(g32)
    c: Coincident(g33,g4)
    c: Coincident(g33,g16)
    c: Horizontal(g33)
    c: Coincident(g34,g5)
    c: Coincident(g34,g17)
    c: Horizontal(g34)
    c: Coincident(g35,g5)
    c: Coincident(g35,g17)
    c: Horizontal(g35)
    c: Coincident(g36,g6)
    c: Coincident(g36,g19)
    c: Horizontal(g36)
    c: Coincident(g37,g6)
    c: Coincident(g37,g19)
    c: Horizontal(g37)
    c: Coincident(g38,g7)
    c: Coincident(g38,g18)
    c: Horizontal(g38)
    c: Coincident(g39,g7)
    c: Coincident(g39,g18)
    c: Horizontal(g39)
    c: Coincident(g40,g8)
    c: Coincident(g40,g20)
    c: Horizontal(g40)
    c: Coincident(g41,g8)
    c: Coincident(g41,g20)
    c: Horizontal(g41)
    c: Coincident(g42,g9)
    c: Coincident(g42,g23)
    c: Horizontal(g42)
    c: Coincident(g43,g9)
    c: Coincident(g43,g23)
    c: Horizontal(g43)
    c: Coincident(g44,g10)
    c: Coincident(g44,g22)
    c: Horizontal(g44)
    c: Coincident(g45,g10)
    c: Coincident(g45,g22)
    c: Horizontal(g45)
    c: Coincident(g46,g11)
    c: Coincident(g46,g21)
    c: Horizontal(g46)
    c: Coincident(g47,g11)
    c: Coincident(g47,g21)
    c: Horizontal(g47)
FEATURE [Sketcher::SketchObject] Sketch031
  FullyConstrained = true
  Placement = pos=(117,19,0) rot=(0.57735,0.57735,0.57735;2.0944rad)
  sketch-geometry (24):
    g0: ArcOfCircle CenterX=-49.19 CenterY=67.75 CenterZ=0 NormalX=0 NormalY=0 NormalZ=1 AngleXU=0 Radius=1.5 StartAngle=1.5708 EndAngle=4.71239
    g1: ArcOfCircle CenterX=-49.19 CenterY=62 CenterZ=0 NormalX=0 NormalY=0 NormalZ=1 AngleXU=0 Radius=1.5 StartAngle=1.5708 EndAngle=4.71239
    g2: ArcOfCircle CenterX=-49.19 CenterY=56.25 CenterZ=0 NormalX=0 NormalY=0 NormalZ=1 AngleXU=0 Radius=1.5 StartAngle=1.5708 EndAngle=4.71239
    g3: ArcOfCircle CenterX=-49.19 CenterY=50.5 CenterZ=0 NormalX=0 NormalY=0 NormalZ=1 AngleXU=0 Radius=1.5 StartAngle=1.5708 EndAngle=4.71239
    g4: ArcOfCircle CenterX=-49.19 CenterY=44.75 CenterZ=0 NormalX=0 NormalY=0 NormalZ=1 AngleXU=0 Radius=1.5 StartAngle=1.5708 EndAngle=4.71239
    g5: ArcOfCircle CenterX=-49.19 CenterY=39 CenterZ=0 NormalX=0 NormalY=0 NormalZ=1 AngleXU=0 Radius=1.5 StartAngle=1.5708 EndAngle=4.71239
    g6: ArcOfCircle CenterX=-49.19 CenterY=33 CenterZ=0 NormalX=0 NormalY=0 NormalZ=1 AngleXU=0 Radius=1.5 StartAngle=1.5708 EndAngle=4.71239
    g7: ArcOfCircle CenterX=-49.19 CenterY=27.25 CenterZ=0 NormalX=0 NormalY=0 NormalZ=1 AngleXU=0 Radius=1.5 StartAngle=1.5708 EndAngle=4.71239
    g8: ArcOfCircle CenterX=-49.19 CenterY=21.5 CenterZ=0 NormalX=0 NormalY=0 NormalZ=1 AngleXU=0 Radius=1.5 StartAngle=1.5708 EndAngle=4.71239
    g9: ArcOfCircle CenterX=-49.19 CenterY=15.75 CenterZ=0 NormalX=0 NormalY=0 NormalZ=1 AngleXU=0 Radius=1.5 StartAngle=1.5708 EndAngle=4.71239
    g10: ArcOfCircle CenterX=-49.19 CenterY=10 CenterZ=0 NormalX=0 NormalY=0 NormalZ=1 AngleXU=0 Radius=1.5 StartAngle=1.5708 EndAngle=4.71239
    g11: ArcOfCircle CenterX=-49.19 CenterY=4.25 CenterZ=0 NormalX=0 NormalY=0 NormalZ=1 AngleXU=0 Radius=1.5 StartAngle=1.5708 EndAngle=4.71239
    g12: LineSegment StartX=-49.19 StartY=69.25 StartZ=0 EndX=-49.19 EndY=66.25 EndZ=0
    g13: LineSegment StartX=-49.19 StartY=63.5 StartZ=0 EndX=-49.19 EndY=60.5 EndZ=0
    g14: LineSegment StartX=-49.19 StartY=57.75 StartZ=0 EndX=-49.19 EndY=54.75 EndZ=0
    g15: LineSegment StartX=-49.19 StartY=52 StartZ=0 EndX=-49.19 EndY=49 EndZ=0
    g16: LineSegment StartX=-49.19 StartY=46.25 StartZ=0 EndX=-49.19 EndY=43.25 EndZ=0
    g17: LineSegment StartX=-49.19 StartY=40.5 StartZ=0 EndX=-49.19 EndY=37.5 EndZ=0
    g18: LineSegment StartX=-49.19 StartY=34.5 StartZ=0 EndX=-49.19 EndY=31.5 EndZ=0
    g19: LineSegment StartX=-49.19 StartY=28.75 StartZ=0 EndX=-49.19 EndY=25.75 EndZ=0
    g20: LineSegment StartX=-49.19 StartY=23 StartZ=0 EndX=-49.19 EndY=20 EndZ=0
    g21: LineSegment StartX=-49.19 StartY=17.25 StartZ=0 EndX=-49.19 EndY=14.25 EndZ=0
    g22: LineSegment StartX=-49.19 StartY=11.5 StartZ=0 EndX=-49.19 EndY=8.5 EndZ=0
    g23: LineSegment StartX=-49.19 StartY=5.75 StartZ=0 EndX=-49.19 EndY=2.75 EndZ=0
  constraints (48):
    c: Block(g0)
    c: Block(g1)
    c: Block(g2)
    c: Block(g3)
    c: Block(g4)
    c: Block(g5)
    c: Block(g6)
    c: Block(g7)
    c: Block(g8)
    c: Block(g9)
    c: Block(g10)
    c: Block(g11)
    c: Coincident(g12,g0)
    c: Coincident(g12,g0)
    c: Vertical(g12)
    c: Vertical(g13)
    c: Coincident(g13,g1)
    c: Vertical(g14)
    c: Coincident(g14,g2)
    c: Vertical(g15)
    c: Coincident(g15,g3)
    c: Vertical(g16)
    c: Coincident(g16,g4)
    c: Vertical(g17)
    c: Coincident(g17,g5)
    c: Vertical(g18)
    c: Coincident(g18,g6)
    c: Vertical(g19)
    c: Coincident(g19,g7)
    c: Vertical(g20)
    c: Coincident(g20,g8)
    c: Vertical(g21)
    c: Coincident(g21,g9)
    c: Vertical(g22)
    c: Coincident(g22,g10)
    c: Vertical(g23)
    c: Coincident(g23,g11)
    c: Block(g23)
    c: Block(g22)
    c: Block(g21)
    c: Block(g20)
    c: Block(g13)
    c: Block(g14)
    c: Block(g15)
    c: Block(g16)
    c: Block(g17)
    c: Block(g18)
    c: Block(g19)
FEATURE [Part::Extrusion] Extrude022
  Base = -> Sketch030
  Dir = (1,-2e-16,2e-16)
  DirMode = 2
  FaceMakerClass = Part::FaceMakerBullseye
  LengthFwd = 19
  LengthRev = 0
  Placement = pos=(-19,0,0) rot=(0,0,1;0rad)
  Solid = true
  Symmetric = false
FEATURE [Part::Fillet] Fillet022
  Base = -> Extrude022
  Edges = 24 edges r=1.49: [Edge6,Edge11,Edge18,Edge23,Edge30,Edge35,Edge42,Edge47,Edge54,Edge59,Edge66,Edge71,Edge78,Edge83,Edge90,Edge95,Edge102,Edge107,Edge114,Edge119,Edge126,Edge131,Edge138,Edge143]
FEATURE [Part::Cut] Cut020  label="top010"
  Base = -> Cut019
  Tool = -> Fillet022
FEATURE [Sketcher::SketchObject] Sketch032
  FullyConstrained = true
  Placement = pos=(117,19,0) rot=(0.57735,0.57735,0.57735;2.0944rad)
  sketch-geometry (48):
    g0: LineSegment StartX=-49.19 StartY=69.25 StartZ=0 EndX=-49.19 EndY=66.25 EndZ=0
    g1: LineSegment StartX=-49.19 StartY=63.5 StartZ=0 EndX=-49.19 EndY=60.5 EndZ=0
    g2: LineSegment StartX=-49.19 StartY=57.75 StartZ=0 EndX=-49.19 EndY=54.75 EndZ=0
    g3: LineSegment StartX=-49.19 StartY=52 StartZ=0 EndX=-49.19 EndY=49 EndZ=0
    g4: LineSegment StartX=-49.19 StartY=46.25 StartZ=0 EndX=-49.19 EndY=43.25 EndZ=0
    g5: LineSegment StartX=-49.19 StartY=40.5 StartZ=0 EndX=-49.19 EndY=37.5 EndZ=0
    g6: LineSegment StartX=-49.19 StartY=34.5 StartZ=0 EndX=-49.19 EndY=31.5 EndZ=0
    g7: LineSegment StartX=-49.19 StartY=28.75 StartZ=0 EndX=-49.19 EndY=25.75 EndZ=0
    g8: LineSegment StartX=-49.19 StartY=23 StartZ=0 EndX=-49.19 EndY=20 EndZ=0
    g9: LineSegment StartX=-49.19 StartY=17.25 StartZ=0 EndX=-49.19 EndY=14.25 EndZ=0
    g10: LineSegment StartX=-49.19 StartY=11.5 StartZ=0 EndX=-49.19 EndY=8.5 EndZ=0
    g11: LineSegment StartX=-49.19 StartY=5.75 StartZ=0 EndX=-49.19 EndY=2.75 EndZ=0
    g12: ArcOfCircle CenterX=-1.5 CenterY=67.75 CenterZ=0 NormalX=0 NormalY=0 NormalZ=1 AngleXU=0 Radius=1.5 StartAngle=4.71239 EndAngle=7.85398
    g13: ArcOfCircle CenterX=-1.5 CenterY=62 CenterZ=0 NormalX=0 NormalY=0 NormalZ=1 AngleXU=0 Radius=1.5 StartAngle=4.71239 EndAngle=7.85398
    g14: ArcOfCircle CenterX=-1.5 CenterY=56.25 CenterZ=0 NormalX=0 NormalY=0 NormalZ=1 AngleXU=0 Radius=1.5 StartAngle=4.71239 EndAngle=7.85398
    g15: ArcOfCircle CenterX=-11.49 CenterY=50.5 CenterZ=0 NormalX=0 NormalY=0 NormalZ=1 AngleXU=0 Radius=1.5 StartAngle=4.71239 EndAngle=7.85398
    g16: ArcOfCircle CenterX=-16.28 CenterY=44.75 CenterZ=0 NormalX=0 NormalY=0 NormalZ=1 AngleXU=0 Radius=1.5 StartAngle=4.71239 EndAngle=7.85398
    g17: ArcOfCircle CenterX=-18.2337 CenterY=39 CenterZ=0 NormalX=0 NormalY=0 NormalZ=1 AngleXU=0 Radius=1.5 StartAngle=4.71485 EndAngle=7.85398
    g18: ArcOfCircle CenterX=-16.2837 CenterY=27.25 CenterZ=0 NormalX=0 NormalY=0 NormalZ=1 AngleXU=0 Radius=1.5 StartAngle=4.71485 EndAngle=7.85398
    g19: ArcOfCircle CenterX=-18.2337 CenterY=33 CenterZ=0 NormalX=0 NormalY=0 NormalZ=1 AngleXU=0 Radius=1.5 StartAngle=4.71485 EndAngle=7.85398
    g20: ArcOfCircle CenterX=-11.49 CenterY=21.5 CenterZ=0 NormalX=0 NormalY=0 NormalZ=1 AngleXU=0 Radius=1.5 StartAngle=4.71239 EndAngle=7.85398
    g21: ArcOfCircle CenterX=-1.5 CenterY=4.25 CenterZ=0 NormalX=0 NormalY=0 NormalZ=1 AngleXU=0 Radius=1.5 StartAngle=4.71239 EndAngle=7.85398
    g22: ArcOfCircle CenterX=-1.5 CenterY=10 CenterZ=0 NormalX=0 NormalY=0 NormalZ=1 AngleXU=0 Radius=1.5 StartAngle=4.71239 EndAngle=7.85398
    g23: ArcOfCircle CenterX=-1.5 CenterY=15.75 CenterZ=0 NormalX=0 NormalY=0 NormalZ=1 AngleXU=0 Radius=1.5 StartAngle=4.71239 EndAngle=7.85398
    g24: LineSegment StartX=-49.19 StartY=69.25 StartZ=0 EndX=-1.5 EndY=69.25 EndZ=0
    g25: LineSegment StartX=-49.19 StartY=66.25 StartZ=0 EndX=-1.5 EndY=66.25 EndZ=0
    g26: LineSegment StartX=-49.19 StartY=63.5 StartZ=0 EndX=-1.5 EndY=63.5 EndZ=0
    g27: LineSegment StartX=-49.19 StartY=60.5 StartZ=0 EndX=-1.5 EndY=60.5 EndZ=0
    g28: LineSegment StartX=-49.19 StartY=57.75 StartZ=0 EndX=-1.5 EndY=57.75 EndZ=0
    g29: LineSegment StartX=-49.19 StartY=54.75 StartZ=0 EndX=-1.5 EndY=54.75 EndZ=0
    g30: LineSegment StartX=-49.19 StartY=52 StartZ=0 EndX=-11.49 EndY=52 EndZ=0
    g31: LineSegment StartX=-49.19 StartY=49 StartZ=0 EndX=-11.49 EndY=49 EndZ=0
    g32: LineSegment StartX=-49.19 StartY=46.25 StartZ=0 EndX=-16.28 EndY=46.25 EndZ=0
    g33: LineSegment StartX=-49.19 StartY=43.25 StartZ=0 EndX=-16.28 EndY=43.25 EndZ=0
    g34: LineSegment StartX=-49.19 StartY=40.5 StartZ=0 EndX=-18.2337 EndY=40.5 EndZ=0
    g35: LineSegment StartX=-49.19 StartY=37.5 StartZ=0 EndX=-18.23 EndY=37.5 EndZ=0
    g36: LineSegment StartX=-49.19 StartY=34.5 StartZ=0 EndX=-18.2337 EndY=34.5 EndZ=0
    g37: LineSegment StartX=-49.19 StartY=31.5 StartZ=0 EndX=-18.23 EndY=31.5 EndZ=0
    g38: LineSegment StartX=-49.19 StartY=28.75 StartZ=0 EndX=-16.2837 EndY=28.75 EndZ=0
    g39: LineSegment StartX=-49.19 StartY=25.75 StartZ=0 EndX=-16.28 EndY=25.75 EndZ=0
    g40: LineSegment StartX=-49.19 StartY=23 StartZ=0 EndX=-11.49 EndY=23 EndZ=0
    g41: LineSegment StartX=-49.19 StartY=20 StartZ=0 EndX=-11.49 EndY=20 EndZ=0
    g42: LineSegment StartX=-49.19 StartY=17.25 StartZ=0 EndX=-1.5 EndY=17.25 EndZ=0
    g43: LineSegment StartX=-49.19 StartY=14.25 StartZ=0 EndX=-1.5 EndY=14.25 EndZ=0
    g44: LineSegment StartX=-49.19 StartY=11.5 StartZ=0 EndX=-1.5 EndY=11.5 EndZ=0
    g45: LineSegment StartX=-49.19 StartY=8.5 StartZ=0 EndX=-1.5 EndY=8.5 EndZ=0
    g46: LineSegment StartX=-49.19 StartY=5.75 StartZ=0 EndX=-1.5 EndY=5.75 EndZ=0
    g47: LineSegment StartX=-49.19 StartY=2.75 StartZ=0 EndX=-1.5 EndY=2.75 EndZ=0
  constraints (120):
    c: Vertical(g0)
    c: Distance(g0) = 3
    c: Block(g0)
    c: Vertical(g1)
    c: Distance(g1) = 3
    c: Vertical(g2)
    c: Equal(g0,g2) = 3
    c: Block(g2)
    c: Vertical(g3)
    c: Equal(g1,g3) = 3
    c: Vertical(g4)
    c: Equal(g0,g4) = 3
    c: Block(g4)
    c: Vertical(g5)
    c: Equal(g1,g5) = 3
    c: Vertical(g6)
    c: Equal(g0,g6) = 3
    c: Block(g6)
    c: Vertical(g7)
    c: Equal(g1,g7) = 3
    c: Vertical(g8)
    c: Equal(g0,g8) = 3
    c: Block(g8)
    c: Vertical(g9)
    c: Equal(g1,g9) = 3
    c: Vertical(g10)
    c: Equal(g0,g10) = 3
    c: Block(g10)
    c: Vertical(g11)
    c: Equal(g1,g11) = 3
    c: Block(g12)
    c: Block(g13)
    c: Block(g14)
    c: Block(g15)
    c: Block(g16)
    c: Block(g17)
    c: Block(g18)
    c: Block(g19)
    c: Block(g20)
    c: Block(g21)
    c: Block(g22)
    c: Block(g23)
    c: Block(g11)
    c: Block(g9)
    c: Block(g7)
    c: Block(g5)
    c: Block(g3)
    c: Block(g1)
    c: Coincident(g24,g0)
    c: Coincident(g24,g12)
    c: Horizontal(g24)
    c: Coincident(g25,g0)
    c: Coincident(g25,g12)
    c: Horizontal(g25)
    c: Coincident(g26,g1)
    c: Coincident(g26,g13)
    c: Horizontal(g26)
    c: Coincident(g27,g1)
    c: Coincident(g27,g13)
    c: Horizontal(g27)
    c: Coincident(g28,g2)
    c: Coincident(g28,g14)
    c: Horizontal(g28)
    c: Coincident(g29,g2)
    c: Coincident(g29,g14)
    c: Horizontal(g29)
    c: Coincident(g30,g3)
    c: Coincident(g30,g15)
    c: Horizontal(g30)
    c: Coincident(g31,g3)
    c: Coincident(g31,g15)
    c: Horizontal(g31)
    c: Coincident(g32,g4)
    c: Coincident(g32,g16)
    c: Horizontal(g32)
    c: Coincident(g33,g4)
    c: Coincident(g33,g16)
    c: Horizontal(g33)
    c: Coincident(g34,g5)
    c: Coincident(g34,g17)
    c: Horizontal(g34)
    c: Coincident(g35,g5)
    c: Coincident(g35,g17)
    c: Horizontal(g35)
    c: Coincident(g36,g6)
    c: Coincident(g36,g19)
    c: Horizontal(g36)
    c: Coincident(g37,g6)
    c: Coincident(g37,g19)
    c: Horizontal(g37)
    c: Coincident(g38,g7)
    c: Coincident(g38,g18)
    c: Horizontal(g38)
    c: Coincident(g39,g7)
    c: Coincident(g39,g18)
    c: Horizontal(g39)
    c: Coincident(g40,g8)
    c: Coincident(g40,g20)
    c: Horizontal(g40)
    c: Coincident(g41,g8)
    c: Coincident(g41,g20)
    c: Horizontal(g41)
    c: Coincident(g42,g9)
    c: Coincident(g42,g23)
    c: Horizontal(g42)
    c: Coincident(g43,g9)
    c: Coincident(g43,g23)
    c: Horizontal(g43)
    c: Coincident(g44,g10)
    c: Coincident(g44,g22)
    c: Horizontal(g44)
    c: Coincident(g45,g10)
    c: Coincident(g45,g22)
    c: Horizontal(g45)
    c: Coincident(g46,g11)
    c: Coincident(g46,g21)
    c: Horizontal(g46)
    c: Coincident(g47,g11)
    c: Coincident(g47,g21)
    c: Horizontal(g47)
FEATURE [Part::Extrusion] Extrude023
  Base = -> Sketch032
  Dir = (1,-2e-16,2e-16)
  DirMode = 2
  FaceMakerClass = Part::FaceMakerBullseye
  LengthFwd = 19
  LengthRev = 0
  Placement = pos=(-19,0,0) rot=(0,0,1;0rad)
  Solid = true
  Symmetric = false
FEATURE [Part::Fillet] Fillet023
  Base = -> Extrude023
  Edges = <same value as first occurrence — deduplicated (x6 in doc)>
  Placement = pos=(0,0.05,0) rot=(0,0,1;0rad)
FEATURE [Part::Cut] Cut014  label="bottom003"
  Base = -> Cut007
  Tool = -> Fusion047
FEATURE [Part::Cut] Cut021  label="bottom004"
  Base = -> Cut014
  Tool = -> Fillet023
FEATURE [Sketcher::SketchObject] Sketch033
  FullyConstrained = true
  Placement = pos=(117,19,0) rot=(0.57735,0.57735,0.57735;2.0944rad)
  sketch-geometry (8):
    g0: LineSegment StartX=-49.19 StartY=69.25 StartZ=0 EndX=-49.19 EndY=66.25 EndZ=0
    g1: LineSegment StartX=-49.19 StartY=5.75 StartZ=0 EndX=-49.19 EndY=2.75 EndZ=0
    g2: ArcOfCircle CenterX=-1.5 CenterY=67.75 CenterZ=0 NormalX=0 NormalY=0 NormalZ=1 AngleXU=0 Radius=1.5 StartAngle=4.71239 EndAngle=7.85398
    g3: ArcOfCircle CenterX=-1.5 CenterY=4.25 CenterZ=0 NormalX=0 NormalY=0 NormalZ=1 AngleXU=0 Radius=1.5 StartAngle=4.71239 EndAngle=7.85398
    g4: LineSegment StartX=-49.19 StartY=69.25 StartZ=0 EndX=-1.5 EndY=69.25 EndZ=0
    g5: LineSegment StartX=-49.19 StartY=66.25 StartZ=0 EndX=-1.5 EndY=66.25 EndZ=0
    g6: LineSegment StartX=-49.19 StartY=5.75 StartZ=0 EndX=-1.5 EndY=5.75 EndZ=0
    g7: LineSegment StartX=-49.19 StartY=2.75 StartZ=0 EndX=-1.5 EndY=2.75 EndZ=0
  constraints (19):
    c: Vertical(g0)
    c: Distance(g0) = 3
    c: Block(g0)
    c: Vertical(g1)
    c: Block(g2)
    c: Block(g3)
    c: Block(g1)
    c: Coincident(g4,g0)
    c: Coincident(g4,g2)
    c: Horizontal(g4)
    c: Coincident(g5,g0)
    c: Coincident(g5,g2)
    c: Horizontal(g5)
    c: Coincident(g6,g1)
    c: Coincident(g6,g3)
    c: Horizontal(g6)
    c: Coincident(g7,g1)
    c: Coincident(g7,g3)
    c: Horizontal(g7)
FEATURE [Sketcher::SketchObject] Sketch034
  FullyConstrained = true
  Placement = pos=(117,19,0) rot=(0.57735,0.57735,0.57735;2.0944rad)
  sketch-geometry (8):
    g0: LineSegment StartX=-49.19 StartY=63.5 StartZ=0 EndX=-49.19 EndY=60.5 EndZ=0
    g1: LineSegment StartX=-49.19 StartY=11.5 StartZ=0 EndX=-49.19 EndY=8.5 EndZ=0
    g2: ArcOfCircle CenterX=-1.5 CenterY=62 CenterZ=0 NormalX=0 NormalY=0 NormalZ=1 AngleXU=0 Radius=1.5 StartAngle=4.71239 EndAngle=7.85398
    g3: ArcOfCircle CenterX=-1.5 CenterY=10 CenterZ=0 NormalX=0 NormalY=0 NormalZ=1 AngleXU=0 Radius=1.5 StartAngle=4.71239 EndAngle=7.85398
    g4: LineSegment StartX=-49.19 StartY=63.5 StartZ=0 EndX=-1.5 EndY=63.5 EndZ=0
    g5: LineSegment StartX=-49.19 StartY=60.5 StartZ=0 EndX=-1.5 EndY=60.5 EndZ=0
    g6: LineSegment StartX=-49.19 StartY=11.5 StartZ=0 EndX=-1.5 EndY=11.5 EndZ=0
    g7: LineSegment StartX=-49.19 StartY=8.5 StartZ=0 EndX=-1.5 EndY=8.5 EndZ=0
  constraints (19):
    c: Vertical(g0)
    c: Distance(g0) = 3
    c: Vertical(g1)
    c: Block(g1)
    c: Block(g2)
    c: Block(g3)
    c: Block(g0)
    c: Coincident(g4,g0)
    c: Coincident(g4,g2)
    c: Horizontal(g4)
    c: Coincident(g5,g0)
    c: Coincident(g5,g2)
    c: Horizontal(g5)
    c: Coincident(g6,g1)
    c: Coincident(g6,g3)
    c: Horizontal(g6)
    c: Coincident(g7,g1)
    c: Coincident(g7,g3)
    c: Horizontal(g7)
FEATURE [Part::Extrusion] Extrude024
  Base = -> Sketch033
  Dir = (1,0,0)
  DirMode = 2
  FaceMakerClass = Part::FaceMakerBullseye
  LengthFwd = 10
  LengthRev = 0
  Solid = true
  Symmetric = false
FEATURE [Part::Extrusion] Extrude025
  Base = -> Sketch034
  Dir = (1,0,0)
  DirMode = 2
  FaceMakerClass = Part::FaceMakerBullseye
  LengthFwd = 10
  LengthRev = 0
  Solid = true
  Symmetric = false
FEATURE [Part::Fillet] Fillet024  label="removeFromtMoreFrontCaseScrewRetainers"
  Base = -> Extrude024
  Edges = 4 edges r=1.49: [Edge6,Edge11,Edge18,Edge23]
  Placement = pos=(-11,0,0) rot=(0,0,1;0rad)
FEATURE [Part::Fillet] Fillet025  label="removeFromtMoreFrontCaseScrewRetainers001"
  Base = -> Extrude025
  Edges = 4 edges r=1.49: [Edge6,Edge11,Edge18,Edge23]
  Placement = pos=(-19,0,0) rot=(0,0,1;0rad)
FEATURE [Part::Cut] Cut022
  Base = -> Cut015
  Tool = -> Fillet025
FEATURE [Part::Cut] Cut023  label="screwRetainers"
  Base = -> Cut022
  Tool = -> Fillet024
FEATURE [Part::MultiFuse] Fusion056  label="bottom005"
  Shapes = -> [Fusion044,Cut021]
FEATURE [Part::MultiFuse] Fusion057  label="casePillars001"
  Shapes = -> [Cut016,Fusion052]
FEATURE [Part::MultiFuse] Fusion058  label="bottom006"
  Shapes = -> [Fusion056,Cut023]
FEATURE [Part::MultiFuse] Fusion059  label="bottom007"
  Shapes = -> [Fusion058,Fillet005]
FEATURE [Part::MultiFuse] Fusion060  label="bottom008"
  Shapes = -> [Fusion059,Fusion]
FEATURE [Part::MultiFuse] Fusion061  label="top011"
  Shapes = -> [Cut006,Cut020]
FEATURE [Part::MultiFuse] Fusion062  label="top012"
  Shapes = -> [Fusion057,Fusion061]
FEATURE [Sketcher::SketchObject] Sketch035  label="topSketch007"
  FullyConstrained = true
  sketch-geometry (6):
    g0: LineSegment StartX=19 StartY=38 StartZ=0 EndX=117 EndY=38 EndZ=0
    g1: ArcOfCircle CenterX=19 CenterY=19 CenterZ=0 NormalX=0 NormalY=0 NormalZ=1 AngleXU=0 Radius=19 StartAngle=1.5708 EndAngle=3.14159
    g2: LineSegment StartX=117 StartY=38 StartZ=0 EndX=117 EndY=19 EndZ=0
    g3: LineSegment StartX=98 StartY=1.0161e-12 StartZ=0 EndX=5.22862e-06 EndY=1.0161e-12 EndZ=0
    g4: LineSegment StartX=5.22862e-06 StartY=19 StartZ=0 EndX=5.22862e-06 EndY=1.0161e-12 EndZ=0
    g5: ArcOfCircle CenterX=98 CenterY=19 CenterZ=0 NormalX=0 NormalY=0 NormalZ=1 AngleXU=0 Radius=19 StartAngle=4.71239 EndAngle=6.28319
  constraints (16):
    c: Horizontal(g0)
    c: Distance(g0) = 98
    c: Coincident(g1,g0)
    c: Block(g1)
    c: Coincident(g2,g0)
    c: Vertical(g2)
    c: Distance(g2) = 19
    c: Horizontal(g3)
    c: Coincident(g4,g1)
    c: Vertical(g4)
    c: Coincident(g3,g4)
    c: Block(g3)
    c: Coincident(g5,g2)
    c: Coincident(g5,g3)
    c: Block(g0)
    c: Block(g5)
FEATURE [Part::Extrusion] Extrude026  label="sideA001"
  Base = -> Sketch035
  Dir = (0,0,1)
  DirMode = 2
  FaceMakerClass = Part::FaceMakerBullseye
  LengthFwd = 3
  LengthRev = 0
  Placement = pos=(0,0,-2.7) rot=(0,0,1;0rad)
  Solid = true
  Symmetric = false
FEATURE [Sketcher::SketchObject] Sketch036  label="topSketch008"
  FullyConstrained = true
  sketch-geometry (6):
    g0: LineSegment StartX=19 StartY=38 StartZ=0 EndX=117 EndY=38 EndZ=0
    g1: ArcOfCircle CenterX=19 CenterY=19 CenterZ=0 NormalX=0 NormalY=0 NormalZ=1 AngleXU=0 Radius=19 StartAngle=1.5708 EndAngle=3.14159
    g2: LineSegment StartX=117 StartY=38 StartZ=0 EndX=117 EndY=19 EndZ=0
    g3: LineSegment StartX=98 StartY=1.0161e-12 StartZ=0 EndX=5.22862e-06 EndY=1.0161e-12 EndZ=0
    g4: LineSegment StartX=5.22862e-06 StartY=19 StartZ=0 EndX=5.22862e-06 EndY=1.0161e-12 EndZ=0
    g5: ArcOfCircle CenterX=98 CenterY=19 CenterZ=0 NormalX=0 NormalY=0 NormalZ=1 AngleXU=0 Radius=19 StartAngle=4.71239 EndAngle=6.28319
  constraints (16):
    c: Horizontal(g0)
    c: Distance(g0) = 98
    c: Coincident(g1,g0)
    c: Block(g1)
    c: Coincident(g2,g0)
    c: Vertical(g2)
    c: Distance(g2) = 19
    c: Horizontal(g3)
    c: Coincident(g4,g1)
    c: Vertical(g4)
    c: Coincident(g3,g4)
    c: Block(g3)
    c: Coincident(g5,g2)
    c: Coincident(g5,g3)
    c: Block(g0)
    c: Block(g5)
FEATURE [Part::Extrusion] Extrude027  label="sideB001"
  Base = -> Sketch036
  Dir = (0,0,1)
  DirMode = 2
  FaceMakerClass = Part::FaceMakerBullseye
  LengthFwd = 3
  LengthRev = 0
  Placement = pos=(0,0,71.7) rot=(0,0,1;0rad)
  Solid = true
  Symmetric = false
FEATURE [Part::MultiFuse] Fusion064  label="removeFromBottom"
  Shapes = -> [Extrude026,Extrude027]
FEATURE [Part::Cut] Cut024  label="bottom009"
  Base = -> Fusion060
  Tool = -> Fusion064
FEATURE [Sketcher::SketchObject] Sketch037  label="topSketch009"
  FullyConstrained = true
  sketch-geometry (8):
    g0: ArcOfCircle CenterX=19 CenterY=19.1201 CenterZ=0 NormalX=0 NormalY=0 NormalZ=1 AngleXU=0 Radius=18.8799 StartAngle=1.5708 EndAngle=3.14793
    g1: LineSegment StartX=0.120501 StartY=19.0004 StartZ=0 EndX=0.120501 EndY=0.000382114 EndZ=0
    g2: LineSegment StartX=19 StartY=38 StartZ=0 EndX=124 EndY=38 EndZ=0
    g3: LineSegment StartX=0.120501 StartY=0.000382114 StartZ=0 EndX=105.121 EndY=0.000382114 EndZ=0
    g4: LineSegment StartX=124 StartY=38 StartZ=0 EndX=125.616 EndY=38 EndZ=0
    g5: LineSegment StartX=105.121 StartY=0.000382114 StartZ=0 EndX=106.736 EndY=0.000382114 EndZ=0
    g6: ArcOfCircle CenterX=106.616 CenterY=19 CenterZ=0 NormalX=0 NormalY=0 NormalZ=1 AngleXU=0 Radius=19 StartAngle=4.71873 EndAngle=6.28319
    g7: LineSegment StartX=125.616 StartY=38 StartZ=0 EndX=125.616 EndY=19 EndZ=0
  constraints (21):
    c: Block(g0)
    c: Coincident(g1,g0)
    c: Vertical(g1)
    c: Horizontal(g2)
    c: Distance(g2) = 105
    c: Coincident(g2,g0)
    c: Distance(g1) = 19
    c: Coincident(g3,g1)
    c: Horizontal(g3)
    c: Distance(g3) = 105
    c: Coincident(g4,g2)
    c: Horizontal(g4)
    c: Distance(g4) = 1.61553
    c: Horizontal(g5)
    c: Equal(g4,g5) = 1.61553
    c: Coincident(g5,g3)
    c: Block(g6)
    c: Coincident(g6,g5)
    c: Coincident(g7,g4)
    c: Coincident(g7,g6)
    c: Vertical(g7)
FEATURE [Part::Extrusion] Extrude028  label="sideB"
  Base = -> Sketch037
  Dir = (0,0,1)
  DirMode = 2
  FaceMakerClass = Part::FaceMakerBullseye
  LengthFwd = 3
  LengthRev = 0
  Placement = pos=(0,0,72) rot=(0,0,1;0rad)
  Solid = true
  Symmetric = false
FEATURE [Sketcher::SketchObject] Sketch038  label="topSketch010"
  FullyConstrained = true
  sketch-geometry (22):
    g0: LineSegment StartX=5.21097e-06 StartY=3 StartZ=0 EndX=5.21097e-06 EndY=19 EndZ=0
    g1: ArcOfCircle CenterX=19 CenterY=19 CenterZ=0 NormalX=0 NormalY=0 NormalZ=1 AngleXU=0 Radius=19 StartAngle=1.5708 EndAngle=3.14159
    g2: ArcOfCircle CenterX=19 CenterY=19 CenterZ=0 NormalX=0 NormalY=0 NormalZ=1 AngleXU=0 Radius=16 StartAngle=1.5708 EndAngle=3.14159
    g3: LineSegment StartX=114 StartY=35 StartZ=0 EndX=19 EndY=35 EndZ=0
    g4: LineSegment StartX=5.21097e-06 StartY=3 StartZ=0 EndX=5.21097e-06 EndY=0 EndZ=0
    g5: LineSegment StartX=3 StartY=0 StartZ=0 EndX=5.21097e-06 EndY=0 EndZ=0
    g6: LineSegment StartX=3 StartY=19 StartZ=0 EndX=3 EndY=0 EndZ=0
    g7: LineSegment StartX=19 StartY=38 StartZ=0 EndX=124 EndY=38 EndZ=0
    g8: Circle CenterX=119 CenterY=35 CenterZ=0 NormalX=0 NormalY=0 NormalZ=1 AngleXU=0 Radius=1
    g9: Circle CenterX=121 CenterY=35 CenterZ=0 NormalX=0 NormalY=0 NormalZ=1 AngleXU=0 Radius=1
    g10: Circle CenterX=121 CenterY=33 CenterZ=0 NormalX=0 NormalY=0 NormalZ=1 AngleXU=0 Radius=1
    g11: BSplineCurve PolesCount=3 KnotsCount=2 Degree=2 IsPeriodic=0
    g12: GeomPoint X=119 Y=35 Z=0
    g13: GeomPoint X=121 Y=33 Z=0
    g14: LineSegment StartX=119 StartY=35 StartZ=0 EndX=114 EndY=35 EndZ=0
    g15: ArcOfCircle CenterX=105 CenterY=19 CenterZ=0 NormalX=0 NormalY=0 NormalZ=1 AngleXU=0 Radius=16 StartAngle=5.60905 EndAngle=6.28319
    g16: LineSegment StartX=121 StartY=33 StartZ=0 EndX=121 EndY=19 EndZ=0
    g17: LineSegment StartX=117.5 StartY=9.01251 StartZ=0 EndX=121.163 EndY=9.0125 EndZ=0
    g18: ArcOfCircle CenterX=105 CenterY=19 CenterZ=0 NormalX=0 NormalY=0 NormalZ=1 AngleXU=0 Radius=20.6155 StartAngle=5.7297 EndAngle=6.28319
    g19: LineSegment StartX=121.163 StartY=9.0125 StartZ=0 EndX=122.538 EndY=8.16329 EndZ=0
    g20: LineSegment StartX=124 StartY=38 StartZ=0 EndX=125.616 EndY=38 EndZ=0
    g21: LineSegment StartX=125.616 StartY=19 StartZ=0 EndX=125.616 EndY=38 EndZ=0
  constraints (49):
    c: Vertical(g0)
    c: Block(g0)
    c: Coincident(g1,g0)
    c: Block(g1)
    c: Coincident(g2,g1)
    c: Block(g2)
    c: Coincident(g3,g2)
    c: Horizontal(g3)
    c: Tangent(g3,g2)
    c: Coincident(g4,g0)
    c: Distance(g4) = 3
    c: Vertical(g4)
    c: Coincident(g5,g4)
    c: Horizontal(g5)
    c: Coincident(g6,g2)
    c: Coincident(g6,g5)
    c: Vertical(g6)
    c: Horizontal(g7)
    c: Distance(g7) = 105
    c: Coincident(g7,g1)
    c: Block(g3)
    c: Weight(g8) = 1
    c: Equal(g8,g9)
    c: Equal(g8,g10)
    c: InternalAlignment(g8,g11)
    c: InternalAlignment(g9,g11)
    c: InternalAlignment(g10,g11)
    c: InternalAlignment(g12,g11)
    c: InternalAlignment(g13,g11)
    c: Block(g11)
    c: Coincident(g14,g11)
    c: Coincident(g14,g3)
    c: Horizontal(g14)
    c: Block(g15)
    c: Coincident(g16,g11)
    c: Coincident(g16,g15)
    c: Vertical(g16)
    c: Distance(g16) = 14
    c: Coincident(g17,g15)
    c: Block(g18)
    c: Coincident(g19,g18)
    c: Coincident(g20,g7)
    c: Horizontal(g20)
    c: Vertical(g21)
    c: Coincident(g20,g21)
    c: Block(g20)
    c: Block(g21)
    c: Block(g19)
    c: Block(g17)
FEATURE [Part::Extrusion] Extrude029
  Base = -> Sketch038
  Dir = (0,0,1)
  DirMode = 2
  FaceMakerClass = Part::FaceMakerBullseye
  LengthFwd = 72
  LengthRev = 0
  Solid = true
  Symmetric = false
FEATURE [Part::Feature] Face085
  shape: bbox 4.8 x 25.5 x 2e-07 mm, 1 faces, 0 solids (baked)
FEATURE [Part::Revolution] Revolve089  label="moreFrontCaseScrewPost003"
  Angle = 360
  Axis = (0,1,0)
  Base = (0,0,0)
  FaceMakerClass = Part::FaceMakerBullseye
  Placement = pos=(109.5,4.5,3.5) rot=(0,0,1;0rad)
  Solid = false
  Source = -> Face085
  Symmetric = false
FEATURE [Part::Feature] Face086
  shape: bbox 4.8 x 25.5 x 2e-07 mm, 1 faces, 0 solids (baked)
FEATURE [Part::Revolution] Revolve090  label="moreFrontCaseScrewPost004"
  Angle = 360
  Axis = (0,1,0)
  Base = (0,0,0)
  FaceMakerClass = Part::FaceMakerBullseye
  Placement = pos=(109.5,4.5,68.5) rot=(0,0,1;0rad)
  Solid = false
  Source = -> Face086
  Symmetric = false
FEATURE [Part::Fillet] Fillet026  label="top013"
  Base = -> Extrude029
  Edges = 1 edges r=2: [Edge35]
FEATURE [Sketcher::SketchObject] Sketch039
  FullyConstrained = true
  sketch-geometry (7):
    g0: LineSegment StartX=0 StartY=0 StartZ=0 EndX=0 EndY=6 EndZ=0
    g1: Circle CenterX=0 CenterY=0 CenterZ=0 NormalX=0 NormalY=0 NormalZ=1 AngleXU=0 Radius=1
    g2: Circle CenterX=8 CenterY=6 CenterZ=0 NormalX=0 NormalY=0 NormalZ=1 AngleXU=0 Radius=1
    g3: BSplineCurve PolesCount=3 KnotsCount=2 Degree=2 IsPeriodic=0
    g4: GeomPoint X=0 Y=0 Z=0
    g5: GeomPoint X=8 Y=6 Z=0
    g6: LineSegment StartX=0 StartY=6 StartZ=0 EndX=8 EndY=6 EndZ=0
  constraints (14):
    c: Coincident(g0,g-1)
    c: Distance(g0) = 6
    c: Vertical(g0)
    c: Coincident(g3,g0)
    c: Weight(g1) = 1
    c: Equal(g1,g2)
    c: InternalAlignment(g1,g3)
    c: InternalAlignment(g2,g3)
    c: InternalAlignment(g4,g3)
    c: InternalAlignment(g5,g3)
    c: Block(g3)
    c: Coincident(g6,g0)
    c: Coincident(g6,g3)
    c: Horizontal(g6)
FEATURE [Sketcher::SketchObject] Sketch040
  FullyConstrained = true
  sketch-geometry (7):
    g0: LineSegment StartX=0 StartY=0 StartZ=0 EndX=0 EndY=6 EndZ=0
    g1: Circle CenterX=0 CenterY=0 CenterZ=0 NormalX=0 NormalY=0 NormalZ=1 AngleXU=0 Radius=1
    g2: Circle CenterX=8 CenterY=6 CenterZ=0 NormalX=0 NormalY=0 NormalZ=1 AngleXU=0 Radius=1
    g3: BSplineCurve PolesCount=3 KnotsCount=2 Degree=2 IsPeriodic=0
    g4: GeomPoint X=0 Y=0 Z=0
    g5: GeomPoint X=8 Y=6 Z=0
    g6: LineSegment StartX=0 StartY=6 StartZ=0 EndX=8 EndY=6 EndZ=0
  constraints (14):
    c: Coincident(g0,g-1)
    c: Distance(g0) = 6
    c: Vertical(g0)
    c: Coincident(g3,g0)
    c: Weight(g1) = 1
    c: Equal(g1,g2)
    c: InternalAlignment(g1,g3)
    c: InternalAlignment(g2,g3)
    c: InternalAlignment(g4,g3)
    c: InternalAlignment(g5,g3)
    c: Block(g3)
    c: Coincident(g6,g0)
    c: Coincident(g6,g3)
    c: Horizontal(g6)
FEATURE [Sketcher::SketchObject] Sketch041
  FullyConstrained = true
  sketch-geometry (7):
    g0: LineSegment StartX=0 StartY=0 StartZ=0 EndX=0 EndY=6 EndZ=0
    g1: Circle CenterX=0 CenterY=0 CenterZ=0 NormalX=0 NormalY=0 NormalZ=1 AngleXU=0 Radius=1
    g2: Circle CenterX=8 CenterY=6 CenterZ=0 NormalX=0 NormalY=0 NormalZ=1 AngleXU=0 Radius=1
    g3: BSplineCurve PolesCount=3 KnotsCount=2 Degree=2 IsPeriodic=0
    g4: GeomPoint X=0 Y=0 Z=0
    g5: GeomPoint X=8 Y=6 Z=0
    g6: LineSegment StartX=0 StartY=6 StartZ=0 EndX=8 EndY=6 EndZ=0
  constraints (14):
    c: Coincident(g0,g-1)
    c: Distance(g0) = 6
    c: Vertical(g0)
    c: Coincident(g3,g0)
    c: Weight(g1) = 1
    c: Equal(g1,g2)
    c: InternalAlignment(g1,g3)
    c: InternalAlignment(g2,g3)
    c: InternalAlignment(g4,g3)
    c: InternalAlignment(g5,g3)
    c: Block(g3)
    c: Coincident(g6,g0)
    c: Coincident(g6,g3)
    c: Horizontal(g6)
FEATURE [Sketcher::SketchObject] Sketch042
  FullyConstrained = true
  sketch-geometry (7):
    g0: LineSegment StartX=0 StartY=0 StartZ=0 EndX=0 EndY=6 EndZ=0
    g1: Circle CenterX=0 CenterY=0 CenterZ=0 NormalX=0 NormalY=0 NormalZ=1 AngleXU=0 Radius=1
    g2: Circle CenterX=8 CenterY=6 CenterZ=0 NormalX=0 NormalY=0 NormalZ=1 AngleXU=0 Radius=1
    g3: BSplineCurve PolesCount=3 KnotsCount=2 Degree=2 IsPeriodic=0
    g4: GeomPoint X=0 Y=0 Z=0
    g5: GeomPoint X=8 Y=6 Z=0
    g6: LineSegment StartX=0 StartY=6 StartZ=0 EndX=8 EndY=6 EndZ=0
  constraints (14):
    c: Coincident(g0,g-1)
    c: Distance(g0) = 6
    c: Vertical(g0)
    c: Coincident(g3,g0)
    c: Weight(g1) = 1
    c: Equal(g1,g2)
    c: InternalAlignment(g1,g3)
    c: InternalAlignment(g2,g3)
    c: InternalAlignment(g4,g3)
    c: InternalAlignment(g5,g3)
    c: Block(g3)
    c: Coincident(g6,g0)
    c: Coincident(g6,g3)
    c: Horizontal(g6)
FEATURE [Part::Extrusion] Extrude030  label="caseScrewPillarBracket008"
  Base = -> Sketch039
  Dir = (0,0,1)
  DirMode = 2
  FaceMakerClass = Part::FaceMakerBullseye
  LengthFwd = 2.4
  LengthRev = 0
  Placement = pos=(15.76,29,8.8) rot=(0,1,0;0rad)
  Solid = true
  Symmetric = false
FEATURE [Part::Extrusion] Extrude031  label="caseScrewPillarBracket009"
  Base = -> Sketch040
  Dir = (0,0,1)
  DirMode = 2
  FaceMakerClass = Part::FaceMakerBullseye
  LengthFwd = 2.4
  LengthRev = 0
  Placement = pos=(15.76,29,60.8) rot=(0,0,1;0rad)
  Solid = true
  Symmetric = false
FEATURE [Part::Extrusion] Extrude032  label="caseScrewPillarBracket010"
  Base = -> Sketch041
  Dir = (0,0,1)
  DirMode = 2
  FaceMakerClass = Part::FaceMakerBullseye
  LengthFwd = 2.4
  LengthRev = 0
  Placement = pos=(13.7,29,13.26) rot=(0,-1,0;1.5708rad)
  Solid = true
  Symmetric = false
FEATURE [Part::Extrusion] Extrude033  label="caseScrewPillarBracket011"
  Base = -> Sketch042
  Dir = (0,0,1)
  DirMode = 2
  FaceMakerClass = Part::FaceMakerBullseye
  LengthFwd = 2.4
  LengthRev = 0
  Placement = pos=(11.3,29,58.74) rot=(0,1,0;1.5708rad)
  Solid = true
  Symmetric = false
FEATURE [Sketcher::SketchObject] Sketch043
  FullyConstrained = true
  sketch-geometry (7):
    g0: LineSegment StartX=0 StartY=0 StartZ=0 EndX=0 EndY=6 EndZ=0
    g1: Circle CenterX=0 CenterY=0 CenterZ=0 NormalX=0 NormalY=0 NormalZ=1 AngleXU=0 Radius=1
    g2: Circle CenterX=8 CenterY=6 CenterZ=0 NormalX=0 NormalY=0 NormalZ=1 AngleXU=0 Radius=1
    g3: BSplineCurve PolesCount=3 KnotsCount=2 Degree=2 IsPeriodic=0
    g4: GeomPoint X=0 Y=0 Z=0
    g5: GeomPoint X=8 Y=6 Z=0
    g6: LineSegment StartX=0 StartY=6 StartZ=0 EndX=8 EndY=6 EndZ=0
  constraints (14):
    c: Coincident(g0,g-1)
    c: Distance(g0) = 6
    c: Vertical(g0)
    c: Coincident(g3,g0)
    c: Weight(g1) = 1
    c: Equal(g1,g2)
    c: InternalAlignment(g1,g3)
    c: InternalAlignment(g2,g3)
    c: InternalAlignment(g4,g3)
    c: InternalAlignment(g5,g3)
    c: Block(g3)
    c: Coincident(g6,g0)
    c: Coincident(g6,g3)
    c: Horizontal(g6)
FEATURE [Part::Extrusion] Extrude034  label="caseScrewPillarBracket012"
  Base = -> Sketch043
  Dir = (0,0,1)
  DirMode = 2
  FaceMakerClass = Part::FaceMakerBullseye
  LengthFwd = 2.4
  LengthRev = 0
  Placement = pos=(88.3,29,65.23) rot=(0,1,0;1.5708rad)
  Solid = true
  Symmetric = false
FEATURE [Sketcher::SketchObject] Sketch044
  FullyConstrained = true
  sketch-geometry (7):
    g0: LineSegment StartX=0 StartY=0 StartZ=0 EndX=0 EndY=6 EndZ=0
    g1: Circle CenterX=0 CenterY=0 CenterZ=0 NormalX=0 NormalY=0 NormalZ=1 AngleXU=0 Radius=1
    g2: Circle CenterX=8 CenterY=6 CenterZ=0 NormalX=0 NormalY=0 NormalZ=1 AngleXU=0 Radius=1
    g3: BSplineCurve PolesCount=3 KnotsCount=2 Degree=2 IsPeriodic=0
    g4: GeomPoint X=0 Y=0 Z=0
    g5: GeomPoint X=8 Y=6 Z=0
    g6: LineSegment StartX=0 StartY=6 StartZ=0 EndX=8 EndY=6 EndZ=0
  constraints (14):
    c: Coincident(g0,g-1)
    c: Distance(g0) = 6
    c: Vertical(g0)
    c: Coincident(g3,g0)
    c: Weight(g1) = 1
    c: Equal(g1,g2)
    c: InternalAlignment(g1,g3)
    c: InternalAlignment(g2,g3)
    c: InternalAlignment(g4,g3)
    c: InternalAlignment(g5,g3)
    c: Block(g3)
    c: Coincident(g6,g0)
    c: Coincident(g6,g3)
    c: Horizontal(g6)
FEATURE [Part::Extrusion] Extrude035  label="caseScrewPillarBracket013"
  Base = -> Sketch044
  Dir = (0,0,1)
  DirMode = 2
  FaceMakerClass = Part::FaceMakerBullseye
  LengthFwd = 2.4
  LengthRev = 0
  Placement = pos=(90.7,29,6.77) rot=(0,-1,0;1.5708rad)
  Solid = true
  Symmetric = false
FEATURE [Sketcher::SketchObject] Sketch045
  FullyConstrained = true
  sketch-geometry (7):
    g0: LineSegment StartX=0 StartY=0 StartZ=0 EndX=0 EndY=6 EndZ=0
    g1: Circle CenterX=0 CenterY=0 CenterZ=0 NormalX=0 NormalY=0 NormalZ=1 AngleXU=0 Radius=1
    g2: Circle CenterX=8 CenterY=6 CenterZ=0 NormalX=0 NormalY=0 NormalZ=1 AngleXU=0 Radius=1
    g3: BSplineCurve PolesCount=3 KnotsCount=2 Degree=2 IsPeriodic=0
    g4: GeomPoint X=0 Y=0 Z=0
    g5: GeomPoint X=8 Y=6 Z=0
    g6: LineSegment StartX=0 StartY=6 StartZ=0 EndX=8 EndY=6 EndZ=0
  constraints (14):
    c: Coincident(g0,g-1)
    c: Distance(g0) = 6
    c: Vertical(g0)
    c: Coincident(g3,g0)
    c: Weight(g1) = 1
    c: Equal(g1,g2)
    c: InternalAlignment(g1,g3)
    c: InternalAlignment(g2,g3)
    c: InternalAlignment(g4,g3)
    c: InternalAlignment(g5,g3)
    c: Block(g3)
    c: Coincident(g6,g0)
    c: Coincident(g6,g3)
    c: Horizontal(g6)
FEATURE [Sketcher::SketchObject] Sketch046
  FullyConstrained = true
  sketch-geometry (7):
    g0: LineSegment StartX=0 StartY=0 StartZ=0 EndX=0 EndY=6 EndZ=0
    g1: Circle CenterX=0 CenterY=0 CenterZ=0 NormalX=0 NormalY=0 NormalZ=1 AngleXU=0 Radius=1
    g2: Circle CenterX=8 CenterY=6 CenterZ=0 NormalX=0 NormalY=0 NormalZ=1 AngleXU=0 Radius=1
    g3: BSplineCurve PolesCount=3 KnotsCount=2 Degree=2 IsPeriodic=0
    g4: GeomPoint X=0 Y=0 Z=0
    g5: GeomPoint X=8 Y=6 Z=0
    g6: LineSegment StartX=0 StartY=6 StartZ=0 EndX=8 EndY=6 EndZ=0
  constraints (14):
    c: Coincident(g0,g-1)
    c: Distance(g0) = 6
    c: Vertical(g0)
    c: Coincident(g3,g0)
    c: Weight(g1) = 1
    c: Equal(g1,g2)
    c: InternalAlignment(g1,g3)
    c: InternalAlignment(g2,g3)
    c: InternalAlignment(g4,g3)
    c: InternalAlignment(g5,g3)
    c: Block(g3)
    c: Coincident(g6,g0)
    c: Coincident(g6,g3)
    c: Horizontal(g6)
FEATURE [Part::Extrusion] Extrude036  label="caseScrewPillarBracket014"
  Base = -> Sketch045
  Dir = (0,0,1)
  DirMode = 2
  FaceMakerClass = Part::FaceMakerBullseye
  LengthFwd = 2.4
  LengthRev = 0
  Placement = pos=(110.7,29,6.77) rot=(0,-1,0;1.5708rad)
  Solid = true
  Symmetric = false
FEATURE [Part::Extrusion] Extrude037  label="caseScrewPillarBracket015"
  Base = -> Sketch046
  Dir = (0,0,1)
  DirMode = 2
  FaceMakerClass = Part::FaceMakerBullseye
  LengthFwd = 2.4
  LengthRev = 0
  Placement = pos=(108.3,29,65.23) rot=(0,1,0;1.5708rad)
  Solid = true
  Symmetric = false
FEATURE [Part::Box] Box013  label="frontCaseScrewPillarBracket002"
  AttacherType = Attacher::AttachEngine3D
  Height = 2.4
  Length = 22
  Placement = pos=(87,28,2.3) rot=(0,0,1;0rad)
  Width = 7
FEATURE [Part::Box] Box014  label="frontCaseScrewPillarBracket003"
  AttacherType = Attacher::AttachEngine3D
  Height = 2.4
  Length = 22
  Placement = pos=(87,28,67.3) rot=(0,0,1;0rad)
  Width = 7
FEATURE [Part::Feature] Face087
  shape: bbox 4.8 x 30.2 x 2e-07 mm, 1 faces, 0 solids (baked)
FEATURE [Part::Revolution] Revolve091  label="frontCaseScrewPost004"
  Angle = 360
  Axis = (0,1,0)
  Base = (0,0,0)
  FaceMakerClass = Part::FaceMakerBullseye
  Placement = pos=(89.5,4.5,3.5) rot=(0,0,1;0rad)
  Solid = false
  Source = -> Face087
  Symmetric = false
FEATURE [Part::Feature] Face088
  shape: bbox 4.8 x 30.2 x 2e-07 mm, 1 faces, 0 solids (baked)
FEATURE [Part::Revolution] Revolve092  label="frontCaseScrewPost005"
  Angle = 360
  Axis = (0,1,0)
  Base = (0,0,0)
  FaceMakerClass = Part::FaceMakerBullseye
  Placement = pos=(89.5,4.5,68.5) rot=(0,0,1;0rad)
  Solid = false
  Source = -> Face088
  Symmetric = false
FEATURE [Part::Feature] Face089
  shape: bbox 3.5 x 30.2 x 2e-07 mm, 1 faces, 0 solids (baked)
FEATURE [Part::Revolution] Revolve093  label="backCaseScrewPost002"
  Angle = 360
  Axis = (0,1,0)
  Base = (0,0,0)
  FaceMakerClass = Part::FaceMakerBullseye
  Placement = pos=(12.5,4.5,10) rot=(0,0,1;0rad)
  Solid = false
  Source = -> Face089
  Symmetric = false
FEATURE [Part::Feature] Face090
  shape: bbox 3.5 x 30.2 x 2e-07 mm, 1 faces, 0 solids (baked)
FEATURE [Part::Revolution] Revolve094  label="backCaseScrewPost003"
  Angle = 360
  Axis = (0,1,0)
  Base = (0,0,0)
  FaceMakerClass = Part::FaceMakerBullseye
  Placement = pos=(12.5,4.5,62) rot=(0,0,1;0rad)
  Solid = false
  Source = -> Face090
  Symmetric = false
FEATURE [Part::Box] Box015  label="Cube011"
  AttacherType = Attacher::AttachEngine3D
  Height = 28.8
  Length = 3
  Placement = pos=(107.3,28,21.6) rot=(0,0,1;0rad)
  Width = 7
FEATURE [Part::Box] Box016  label="Cube012"
  AttacherType = Attacher::AttachEngine3D
  Height = 3
  Length = 7.4
  Placement = pos=(107.3,28,18.6) rot=(0,0,1;0rad)
  Width = 7
FEATURE [Part::Box] Box017  label="Cube013"
  AttacherType = Attacher::AttachEngine3D
  Height = 3
  Length = 7.4
  Placement = pos=(107.3,28,50.4) rot=(0,0,1;0rad)
  Width = 7
FEATURE [Part::Cylinder] Cylinder024
  Angle = 360
  AttacherType = Attacher::AttachEngine3D
  Height = 20
  Placement = pos=(0,0,36.15) rot=(0,0,1;0rad)
  Radius = 14.3
FEATURE [Part::Cylinder] Cylinder025
  Angle = 360
  AttacherType = Attacher::AttachEngine3D
  Height = 10
  Placement = pos=(0,0,36.15) rot=(0,0,1;0rad)
  Radius = 4
FEATURE [Part::MultiFuse] Fusion066  label="removeToCreteHoleForPlugHousing009"
  Placement = pos=(70,19,36) rot=(0,1,0;1.5708rad)
  Shapes = -> [Cylinder024,Cylinder025]
FEATURE [Part::MultiFuse] Fusion065  label="plugHousingBracketHolder002"
  Shapes = -> [Box017,Box015,Box016]
FEATURE [Part::Cut] Cut025  label="plugHousingBracketHolder003"
  Base = -> Fusion065
  Placement = pos=(7,0,0) rot=(0,0,1;0rad)
  Tool = -> Fusion066
FEATURE [Sketcher::SketchObject] Sketch047
  FullyConstrained = false
  Placement = pos=(0,0,0) rot=(1,0,0;1.5708rad)
  sketch-geometry (24):
    g0: ArcOfCircle CenterX=-4 CenterY=-10.5 CenterZ=0 NormalX=0 NormalY=0 NormalZ=1 AngleXU=0 Radius=1.5 StartAngle=6e-16 EndAngle=3.14159
    g1: ArcOfCircle CenterX=-34.2 CenterY=-10.5 CenterZ=0 NormalX=0 NormalY=0 NormalZ=1 AngleXU=0 Radius=1.5 StartAngle=0 EndAngle=3.14159
    g2: ArcOfCircle CenterX=-34.2 CenterY=-27.7 CenterZ=0 NormalX=0 NormalY=0 NormalZ=1 AngleXU=0 Radius=1.5 StartAngle=3.14159 EndAngle=6.28319
    g3: ArcOfCircle CenterX=-4 CenterY=-27.7 CenterZ=0 NormalX=0 NormalY=0 NormalZ=1 AngleXU=0 Radius=1.5 StartAngle=3.1416 EndAngle=6.28319
    g4: ArcOfCircle CenterX=-10 CenterY=-4.3 CenterZ=0 NormalX=0 NormalY=0 NormalZ=1 AngleXU=0 Radius=1.5 StartAngle=2e-16 EndAngle=3.14159
    g5: ArcOfCircle CenterX=-16.1 CenterY=-1.8 CenterZ=0 NormalX=0 NormalY=0 NormalZ=1 AngleXU=0 Radius=1.5 StartAngle=5e-16 EndAngle=3.14159
    g6: ArcOfCircle CenterX=-22.1 CenterY=-1.8 CenterZ=0 NormalX=0 NormalY=0 NormalZ=1 AngleXU=0 Radius=1.5 StartAngle=5e-16 EndAngle=3.14159
    g7: ArcOfCircle CenterX=-28.2 CenterY=-4.3 CenterZ=0 NormalX=0 NormalY=0 NormalZ=1 AngleXU=0 Radius=1.5 StartAngle=2e-16 EndAngle=3.14159
    g8: ArcOfCircle CenterX=-10 CenterY=-33.9 CenterZ=0 NormalX=0 NormalY=0 NormalZ=1 AngleXU=0 Radius=1.5 StartAngle=3.14159 EndAngle=6.28319
    g9: ArcOfCircle CenterX=-16.1 CenterY=-36.4 CenterZ=0 NormalX=0 NormalY=0 NormalZ=1 AngleXU=0 Radius=1.5 StartAngle=3.14159 EndAngle=6.28319
    g10: ArcOfCircle CenterX=-22.1 CenterY=-36.4 CenterZ=0 NormalX=0 NormalY=0 NormalZ=1 AngleXU=0 Radius=1.5 StartAngle=3.14159 EndAngle=6.28319
    g11: ArcOfCircle CenterX=-28.2 CenterY=-33.9 CenterZ=0 NormalX=0 NormalY=0 NormalZ=1 AngleXU=0 Radius=1.5 StartAngle=3.14159 EndAngle=6.28319
    g12: LineSegment StartX=-35.7 StartY=-10.5 StartZ=0 EndX=-35.7 EndY=-27.7 EndZ=0
    g13: LineSegment StartX=-32.7 StartY=-10.5 StartZ=0 EndX=-32.7 EndY=-27.7 EndZ=0
    g14: LineSegment StartX=-29.7 StartY=-33.9 StartZ=0 EndX=-29.7 EndY=-4.3 EndZ=0
    g15: LineSegment StartX=-26.7 StartY=-33.9 StartZ=0 EndX=-26.7 EndY=-4.3 EndZ=0
    g16: LineSegment StartX=-2.5 StartY=-10.5 StartZ=0 EndX=-2.5 EndY=-27.7 EndZ=0
    g17: LineSegment StartX=-8.5 StartY=-4.3 StartZ=0 EndX=-8.5 EndY=-33.9 EndZ=0
    g18: LineSegment StartX=-5.5 StartY=-10.5 StartZ=0 EndX=-5.5 EndY=-27.7 EndZ=0
    g19: LineSegment StartX=-11.5 StartY=-4.3 StartZ=0 EndX=-11.5 EndY=-33.9 EndZ=0
    g20: LineSegment StartX=-14.6 StartY=-1.8 StartZ=0 EndX=-14.6 EndY=-36.4 EndZ=0
    g21: LineSegment StartX=-17.6 StartY=-1.8 StartZ=0 EndX=-17.6 EndY=-36.4 EndZ=0
    g22: LineSegment StartX=-20.6 StartY=-36.4 StartZ=0 EndX=-20.6 EndY=-1.8 EndZ=0
    g23: LineSegment StartX=-23.6 StartY=-1.8 StartZ=0 EndX=-23.6 EndY=-36.4 EndZ=0
  constraints (48):
    c: Block(g0)
    c: Block(g1)
    c: Block(g2)
    c: Block(g3)
    c: Block(g4)
    c: Block(g5)
    c: Block(g6)
    c: Block(g7)
    c: Block(g8)
    c: Block(g9)
    c: Block(g10)
    c: Block(g11)
    c: Coincident(g12,g1)
    c: Coincident(g12,g2)
    c: Vertical(g12)
    c: Coincident(g13,g1)
    c: Coincident(g13,g2)
    c: Vertical(g13)
    c: Coincident(g14,g11)
    c: Coincident(g14,g7)
    c: Vertical(g14)
    c: Coincident(g15,g11)
    c: Coincident(g15,g7)
    c: Vertical(g15)
    c: Coincident(g16,g0)
    c: Coincident(g16,g3)
    c: Vertical(g16)
    c: Coincident(g17,g4)
    c: Coincident(g17,g8)
    c: Vertical(g17)
    c: Coincident(g18,g0)
    c: Coincident(g18,g3)
    c: Vertical(g18)
    c: Coincident(g19,g4)
    c: Coincident(g19,g8)
    c: Vertical(g19)
    c: Coincident(g20,g5)
    c: Coincident(g20,g9)
    c: Vertical(g20)
    c: Coincident(g21,g5)
    c: Coincident(g21,g9)
    c: Vertical(g21)
    c: Coincident(g22,g10)
    c: Coincident(g22,g6)
    c: Vertical(g22)
    c: Coincident(g23,g6)
    c: Coincident(g23,g10)
    c: Vertical(g23)
FEATURE [Part::Extrusion] Extrude038  label="removeToCreateFanGrillHoles001"
  Base = -> Sketch047
  Dir = (0,-1,6e-16)
  DirMode = 2
  FaceMakerClass = Part::FaceMakerBullseye
  LengthFwd = 10
  LengthRev = 0
  Placement = pos=(65.4,44,54.82) rot=(0,0,1;0rad)
  Solid = true
  Symmetric = false
FEATURE [Part::Feature] Wire004
  shape: bbox 11 x 5.2 x 2e-07 mm, 0 faces, 0 solids (baked)
FEATURE [Part::Revolution] Revolve095
  Angle = 360
  Axis = (0,1,0)
  Base = (0,0,0)
  FaceMakerClass = Part::FaceMakerBullseye
  Placement = pos=(30.3,38,19.7) rot=(0,0,1;0rad)
  Solid = true
  Source = -> Wire004
  Symmetric = false
FEATURE [Part::Feature] Wire005
  shape: bbox 11 x 5.2 x 2e-07 mm, 0 faces, 0 solids (baked)
FEATURE [Part::Revolution] Revolve096
  Angle = 360
  Axis = (0,1,0)
  Base = (0,0,0)
  FaceMakerClass = Part::FaceMakerBullseye
  Placement = pos=(30.3,38,51.7) rot=(0,0,1;0rad)
  Solid = true
  Source = -> Wire005
  Symmetric = false
FEATURE [Part::Feature] Wire006
  shape: bbox 11 x 5.2 x 2e-07 mm, 0 faces, 0 solids (baked)
FEATURE [Part::Revolution] Revolve097
  Angle = 360
  Axis = (0,1,0)
  Base = (0,0,0)
  FaceMakerClass = Part::FaceMakerBullseye
  Placement = pos=(62.3,38,51.7) rot=(0,0,1;0rad)
  Solid = true
  Source = -> Wire006
  Symmetric = false
FEATURE [Part::Feature] Wire007
  shape: bbox 11 x 5.2 x 2e-07 mm, 0 faces, 0 solids (baked)
FEATURE [Part::Revolution] Revolve098
  Angle = 360
  Axis = (0,1,0)
  Base = (0,0,0)
  FaceMakerClass = Part::FaceMakerBullseye
  Placement = pos=(62.3,38,19.7) rot=(0,0,1;0rad)
  Solid = true
  Source = -> Wire007
  Symmetric = false
FEATURE [Part::MultiFuse] Fusion067  label="fanScrewHousing002"
  Shapes = -> [Revolve098,Revolve097,Revolve096,Revolve095]
FEATURE [Part::Feature] Face091 .. Face094  x4 (patterned run collapsed; names and placements below)
  shape: bbox 3.5 x 17.8 x 2e-07 mm, 1 faces, 0 solids (baked)
FEATURE [Part::Revolution] Revolve099  label="removeToCreateScrewAndThreadedInsertHole026"
  Angle = 360
  Axis = (0,1,0)
  Base = (0,0,0)
  FaceMakerClass = Part::FaceMakerBullseye
  Placement = pos=(62.3,30.3,19.7) rot=(0,0,1;0rad)
  Solid = false
  Source = -> Face091
  Symmetric = false
FEATURE [Part::Revolution] Revolve100  label="removeToCreateScrewAndThreadedInsertHole027"
  Angle = 360
  Axis = (0,1,0)
  Base = (0,0,0)
  FaceMakerClass = Part::FaceMakerBullseye
  Placement = pos=(62.3,30.3,51.7) rot=(0,0,1;0rad)
  Solid = false
  Source = -> Face092
  Symmetric = false
FEATURE [Part::Revolution] Revolve101  label="removeToCreateScrewAndThreadedInsertHole028"
  Angle = 360
  Axis = (0,1,0)
  Base = (0,0,0)
  FaceMakerClass = Part::FaceMakerBullseye
  Placement = pos=(30.3,30.3,19.7) rot=(0,0,1;0rad)
  Solid = false
  Source = -> Face093
  Symmetric = false
FEATURE [Part::Revolution] Revolve102  label="removeToCreateScrewAndThreadedInsertHole029"
  Angle = 360
  Axis = (0,1,0)
  Base = (0,0,0)
  FaceMakerClass = Part::FaceMakerBullseye
  Placement = pos=(30.3,30.3,51.7) rot=(0,0,1;0rad)
  Solid = false
  Source = -> Face094
  Symmetric = false
FEATURE [Part::MultiFuse] Fusion068  label="createThreadedInsertHolesForFan002"
  Shapes = -> [Revolve099,Revolve100,Revolve101,Revolve102]
FEATURE [Part::Cut] Cut026  label="fanScrewHousing003"
  Base = -> Fusion067
  Tool = -> Fusion068
FEATURE [Sketcher::SketchObject] Sketch048
  FullyConstrained = false
  Placement = pos=(0,0,0) rot=(1,0,0;1.5708rad)
  sketch-geometry (24):
    g0: ArcOfCircle CenterX=-4 CenterY=-10.5 CenterZ=0 NormalX=0 NormalY=0 NormalZ=1 AngleXU=0 Radius=1.5 StartAngle=6e-16 EndAngle=3.14159
    g1: ArcOfCircle CenterX=-34.2 CenterY=-10.5 CenterZ=0 NormalX=0 NormalY=0 NormalZ=1 AngleXU=0 Radius=1.5 StartAngle=0 EndAngle=3.14159
    g2: ArcOfCircle CenterX=-34.2 CenterY=-27.7 CenterZ=0 NormalX=0 NormalY=0 NormalZ=1 AngleXU=0 Radius=1.5 StartAngle=3.14159 EndAngle=6.28319
    g3: ArcOfCircle CenterX=-4 CenterY=-27.7 CenterZ=0 NormalX=0 NormalY=0 NormalZ=1 AngleXU=0 Radius=1.5 StartAngle=3.1416 EndAngle=6.28319
    g4: ArcOfCircle CenterX=-10 CenterY=-4.3 CenterZ=0 NormalX=0 NormalY=0 NormalZ=1 AngleXU=0 Radius=1.5 StartAngle=2e-16 EndAngle=3.14159
    g5: ArcOfCircle CenterX=-16.1 CenterY=-1.8 CenterZ=0 NormalX=0 NormalY=0 NormalZ=1 AngleXU=0 Radius=1.5 StartAngle=5e-16 EndAngle=3.14159
    g6: ArcOfCircle CenterX=-22.1 CenterY=-1.8 CenterZ=0 NormalX=0 NormalY=0 NormalZ=1 AngleXU=0 Radius=1.5 StartAngle=5e-16 EndAngle=3.14159
    g7: ArcOfCircle CenterX=-28.2 CenterY=-4.3 CenterZ=0 NormalX=0 NormalY=0 NormalZ=1 AngleXU=0 Radius=1.5 StartAngle=2e-16 EndAngle=3.14159
    g8: ArcOfCircle CenterX=-10 CenterY=-33.9 CenterZ=0 NormalX=0 NormalY=0 NormalZ=1 AngleXU=0 Radius=1.5 StartAngle=3.14159 EndAngle=6.28319
    g9: ArcOfCircle CenterX=-16.1 CenterY=-36.4 CenterZ=0 NormalX=0 NormalY=0 NormalZ=1 AngleXU=0 Radius=1.5 StartAngle=3.14159 EndAngle=6.28319
    g10: ArcOfCircle CenterX=-22.1 CenterY=-36.4 CenterZ=0 NormalX=0 NormalY=0 NormalZ=1 AngleXU=0 Radius=1.5 StartAngle=3.14159 EndAngle=6.28319
    g11: ArcOfCircle CenterX=-28.2 CenterY=-33.9 CenterZ=0 NormalX=0 NormalY=0 NormalZ=1 AngleXU=0 Radius=1.5 StartAngle=3.14159 EndAngle=6.28319
    g12: LineSegment StartX=-35.7 StartY=-10.5 StartZ=0 EndX=-35.7 EndY=-27.7 EndZ=0
    g13: LineSegment StartX=-32.7 StartY=-10.5 StartZ=0 EndX=-32.7 EndY=-27.7 EndZ=0
    g14: LineSegment StartX=-29.7 StartY=-33.9 StartZ=0 EndX=-29.7 EndY=-4.3 EndZ=0
    g15: LineSegment StartX=-26.7 StartY=-33.9 StartZ=0 EndX=-26.7 EndY=-4.3 EndZ=0
    g16: LineSegment StartX=-2.5 StartY=-10.5 StartZ=0 EndX=-2.5 EndY=-27.7 EndZ=0
    g17: LineSegment StartX=-8.5 StartY=-4.3 StartZ=0 EndX=-8.5 EndY=-33.9 EndZ=0
    g18: LineSegment StartX=-5.5 StartY=-10.5 StartZ=0 EndX=-5.5 EndY=-27.7 EndZ=0
    g19: LineSegment StartX=-11.5 StartY=-4.3 StartZ=0 EndX=-11.5 EndY=-33.9 EndZ=0
    g20: LineSegment StartX=-14.6 StartY=-1.8 StartZ=0 EndX=-14.6 EndY=-36.4 EndZ=0
    g21: LineSegment StartX=-17.6 StartY=-1.8 StartZ=0 EndX=-17.6 EndY=-36.4 EndZ=0
    g22: LineSegment StartX=-20.6 StartY=-36.4 StartZ=0 EndX=-20.6 EndY=-1.8 EndZ=0
    g23: LineSegment StartX=-23.6 StartY=-1.8 StartZ=0 EndX=-23.6 EndY=-36.4 EndZ=0
  constraints (48):
    c: Block(g0)
    c: Block(g1)
    c: Block(g2)
    c: Block(g3)
    c: Block(g4)
    c: Block(g5)
    c: Block(g6)
    c: Block(g7)
    c: Block(g8)
    c: Block(g9)
    c: Block(g10)
    c: Block(g11)
    c: Coincident(g12,g1)
    c: Coincident(g12,g2)
    c: Vertical(g12)
    c: Coincident(g13,g1)
    c: Coincident(g13,g2)
    c: Vertical(g13)
    c: Coincident(g14,g11)
    c: Coincident(g14,g7)
    c: Vertical(g14)
    c: Coincident(g15,g11)
    c: Coincident(g15,g7)
    c: Vertical(g15)
    c: Coincident(g16,g0)
    c: Coincident(g16,g3)
    c: Vertical(g16)
    c: Coincident(g17,g4)
    c: Coincident(g17,g8)
    c: Vertical(g17)
    c: Coincident(g18,g0)
    c: Coincident(g18,g3)
    c: Vertical(g18)
    c: Coincident(g19,g4)
    c: Coincident(g19,g8)
    c: Vertical(g19)
    c: Coincident(g20,g5)
    c: Coincident(g20,g9)
    c: Vertical(g20)
    c: Coincident(g21,g5)
    c: Coincident(g21,g9)
    c: Vertical(g21)
    c: Coincident(g22,g10)
    c: Coincident(g22,g6)
    c: Vertical(g22)
    c: Coincident(g23,g6)
    c: Coincident(g23,g10)
    c: Vertical(g23)
FEATURE [Part::Extrusion] Extrude039  label="removeToCreateFanGrillHoles002"
  Base = -> Sketch048
  Dir = (0,-1,6e-16)
  DirMode = 2
  FaceMakerClass = Part::FaceMakerBullseye
  LengthFwd = 10
  LengthRev = 0
  Placement = pos=(65.4,44,54.82) rot=(0,0,1;0rad)
  Solid = true
  Symmetric = false
FEATURE [Part::Cut] Cut027  label="fanScrewHousing004"
  Base = -> Cut026
  Tool = -> Extrude038
FEATURE [Part::Cut] Cut028  label="top014"
  Base = -> Fillet026
  Tool = -> Extrude039
FEATURE [Part::Feature] Face095 .. Face098  x4 (patterned run collapsed; names and placements below)
  shape: bbox 3.5 x 17.8 x 2e-07 mm, 1 faces, 0 solids (baked)
FEATURE [Part::Revolution] Revolve103  label="removeToCreateScrewAndThreadedInsertHole030"
  Angle = 360
  Axis = (0,1,0)
  Base = (0,0,0)
  FaceMakerClass = Part::FaceMakerBullseye
  Placement = pos=(62.3,30.3,19.7) rot=(0,0,1;0rad)
  Solid = false
  Source = -> Face095
  Symmetric = false
FEATURE [Part::Revolution] Revolve104  label="removeToCreateScrewAndThreadedInsertHole031"
  Angle = 360
  Axis = (0,1,0)
  Base = (0,0,0)
  FaceMakerClass = Part::FaceMakerBullseye
  Placement = pos=(62.3,30.3,51.7) rot=(0,0,1;0rad)
  Solid = false
  Source = -> Face096
  Symmetric = false
FEATURE [Part::Revolution] Revolve105  label="removeToCreateScrewAndThreadedInsertHole032"
  Angle = 360
  Axis = (0,1,0)
  Base = (0,0,0)
  FaceMakerClass = Part::FaceMakerBullseye
  Placement = pos=(30.3,30.3,19.7) rot=(0,0,1;0rad)
  Solid = false
  Source = -> Face097
  Symmetric = false
FEATURE [Part::Revolution] Revolve106  label="removeToCreateScrewAndThreadedInsertHole033"
  Angle = 360
  Axis = (0,1,0)
  Base = (0,0,0)
  FaceMakerClass = Part::FaceMakerBullseye
  Placement = pos=(30.3,30.3,51.7) rot=(0,0,1;0rad)
  Solid = false
  Source = -> Face098
  Symmetric = false
FEATURE [Part::MultiFuse] Fusion069  label="createThreadedInsertHolesForFan003"
  Shapes = -> [Revolve103,Revolve104,Revolve105,Revolve106]
FEATURE [Part::Cut] Cut029  label="top015"
  Base = -> Cut028
  Tool = -> Fusion054
FEATURE [Part::Cut] Cut030  label="fanScrewHousing005"
  Base = -> Cut027
  Tool = -> Fusion069
FEATURE [Part::Cylinder] Cylinder026  label="removeToCreteHoleForPlugHousing010"
  Angle = 360
  AttacherType = Attacher::AttachEngine3D
  Height = 20
  Placement = pos=(-2,19,36) rot=(0,1,0;1.5708rad)
  Radius = 14.3
FEATURE [Part::Box] Box018  label="removeToCreteHoleForPlugHousing011"
  AttacherType = Attacher::AttachEngine3D
  Height = 28.6
  Length = 10
  Placement = pos=(-2,0,21.7) rot=(0,0,1;0rad)
  Width = 19
FEATURE [Part::Box] Box019  label="wireHolderBottomCaseBit"
  AttacherType = Attacher::AttachEngine3D
  Height = 28
  Length = 3
  Placement = pos=(0,0,22) rot=(0,0,1;0rad)
  Width = 21
FEATURE [Part::Cylinder] Cylinder027  label="removeToCreteHoleForPlugHousing012"
  Angle = 360
  AttacherType = Attacher::AttachEngine3D
  Height = 20
  Placement = pos=(-2,19,36) rot=(0,1,0;1.5708rad)
  Radius = 14.3
FEATURE [Part::Cut] Cut031  label="wireHolderBottomCaseBit001"
  Base = -> Box019
  Tool = -> Cylinder027
FEATURE [Part::MultiFuse] Fusion070  label="removeToCreteHoleForPlugHousing013"
  Shapes = -> [Box018,Cylinder026]
FEATURE [Part::Cut] Cut032  label="top016"
  Base = -> Cut029
  Tool = -> Fusion070
FEATURE [Part::Cylinder] Cylinder028
  Angle = 360
  AttacherType = Attacher::AttachEngine3D
  Height = 20
  Placement = pos=(0,0,36.15) rot=(0,0,1;0rad)
  Radius = 14.3
FEATURE [Part::Cylinder] Cylinder029
  Angle = 360
  AttacherType = Attacher::AttachEngine3D
  Height = 10
  Placement = pos=(0,0,36.15) rot=(0,0,1;0rad)
  Radius = 4
FEATURE [Part::MultiFuse] Fusion071  label="removeToCreteHoleForPlugHousing014"
  Placement = pos=(70,19,36) rot=(0,1,0;1.5708rad)
  Shapes = -> [Cylinder028,Cylinder029]
FEATURE [Sketcher::SketchObject] Sketch049  label="topSketch011"
  FullyConstrained = true
  sketch-geometry (4):
    g0: ArcOfCircle CenterX=105 CenterY=19 CenterZ=0 NormalX=0 NormalY=0 NormalZ=1 AngleXU=0 Radius=20.6155 StartAngle=5.54125 EndAngle=6.28319
    g1: ArcOfCircle CenterX=105 CenterY=19 CenterZ=0 NormalX=0 NormalY=0 NormalZ=1 AngleXU=0 Radius=13 StartAngle=5.54125 EndAngle=6.28319
    g2: LineSegment StartX=118 StartY=19 StartZ=0 EndX=125.616 EndY=19 EndZ=0
    g3: LineSegment StartX=114.583 StartY=10.2157 StartZ=0 EndX=120.197 EndY=5.06982 EndZ=0
  constraints (7):
    c: Block(g0)
    c: Block(g1)
    c: Coincident(g2,g1)
    c: Coincident(g2,g0)
    c: Horizontal(g2)
    c: Coincident(g3,g1)
    c: Coincident(g3,g0)
FEATURE [Part::Box] Box020  label="removeToCreteHoleForPlugHousing015"
  AttacherType = Attacher::AttachEngine3D
  Height = 28.6
  Length = 20
  Placement = pos=(106.15,0,21.7) rot=(0,0,1;0rad)
  Width = 19
FEATURE [Part::MultiFuse] Fusion072  label="removeToCreteHoleForPlugHousing016"
  Shapes = -> [Box020,Fusion071]
FEATURE [Part::Cut] Cut033  label="removeToCreteHoleForPlugHousing017"
  Base = -> Cut032
  Tool = -> Fusion072
FEATURE [Part::Cylinder] Cylinder030
  Angle = 360
  AttacherType = Attacher::AttachEngine3D
  Height = 20
  Placement = pos=(0,0,36.15) rot=(0,0,1;0rad)
  Radius = 14.3
FEATURE [Part::Cylinder] Cylinder031
  Angle = 360
  AttacherType = Attacher::AttachEngine3D
  Height = 10
  Placement = pos=(0,0,36.15) rot=(0,0,1;0rad)
  Radius = 4
FEATURE [Part::Box] Box021  label="removeToCreteHoleForPlugHousing019"
  AttacherType = Attacher::AttachEngine3D
  Height = 28.6
  Length = 20
  Placement = pos=(106.15,0,21.7) rot=(0,0,1;0rad)
  Width = 19
FEATURE [Part::MultiFuse] Fusion074  label="removeToCreteHoleForPlugHousing020"
  Placement = pos=(70,19,36) rot=(0,1,0;1.5708rad)
  Shapes = -> [Cylinder030,Cylinder031]
FEATURE [Part::MultiFuse] Fusion073  label="removeToCreteHoleForPlugHousing018"
  Placement = pos=(0,0,28.3) rot=(0,0,1;0rad)
  Shapes = -> [Box021,Fusion074]
FEATURE [Part::Cylinder] Cylinder032
  Angle = 360
  AttacherType = Attacher::AttachEngine3D
  Height = 20
  Placement = pos=(0,0,36.15) rot=(0,0,1;0rad)
  Radius = 14.3
FEATURE [Part::Cylinder] Cylinder033
  Angle = 360
  AttacherType = Attacher::AttachEngine3D
  Height = 10
  Placement = pos=(0,0,36.15) rot=(0,0,1;0rad)
  Radius = 4
FEATURE [Part::Box] Box022  label="removeToCreteHoleForPlugHousing021"
  AttacherType = Attacher::AttachEngine3D
  Height = 28.6
  Length = 20
  Placement = pos=(106.15,0,21.7) rot=(0,0,1;0rad)
  Width = 19
FEATURE [Part::MultiFuse] Fusion076  label="removeToCreteHoleForPlugHousing023"
  Placement = pos=(70,19,36) rot=(0,1,0;1.5708rad)
  Shapes = -> [Cylinder032,Cylinder033]
FEATURE [Part::MultiFuse] Fusion075  label="removeToCreteHoleForPlugHousing022"
  Placement = pos=(0,0,-28.3) rot=(0,0,1;0rad)
  Shapes = -> [Box022,Fusion076]
FEATURE [Part::MultiFuse] Fusion077  label="removeToCreatePlugHousingBottomBit"
  Shapes = -> [Fusion075,Fusion073]
FEATURE [Part::Cylinder] Cylinder034
  Angle = 360
  AttacherType = Attacher::AttachEngine3D
  Height = 20
  Placement = pos=(0,0,36.15) rot=(0,0,1;0rad)
  Radius = 14
FEATURE [Part::Cylinder] Cylinder035
  Angle = 360
  AttacherType = Attacher::AttachEngine3D
  Height = 10
  Placement = pos=(0,0,36.15) rot=(0,0,1;0rad)
  Radius = 4
FEATURE [Part::MultiFuse] Fusion078  label="removeToCreteHoleForPlugHousing024"
  Placement = pos=(70,19,36) rot=(0,1,0;1.5708rad)
  Shapes = -> [Cylinder034,Cylinder035]
FEATURE [Part::MultiFuse] Fusion079  label="removeToCreatePlugHousingBottomBit001"
  Shapes = -> [Fusion078,Fusion077]
FEATURE [Part::Extrusion] Extrude040  label="bottomPlugHousingBit"
  Base = -> Sketch049
  Dir = (0,0,1)
  DirMode = 2
  FaceMakerClass = Part::FaceMakerBullseye
  LengthFwd = 72
  LengthRev = 0
  Solid = true
  Symmetric = false
FEATURE [Part::Cut] Cut034  label="bottomPlugHousingBit001"
  Base = -> Extrude040
  Placement = pos=(-0.09,0,0) rot=(0,0,1;0rad)
  Tool = -> Fusion079
FEATURE [Part::Box] Box023  label="Cube014"
  AttacherType = Attacher::AttachEngine3D
  Height = 16
  Length = 8
  Placement = pos=(12.7,31.52,28) rot=(0,0,1;0rad)
  Width = 4
FEATURE [Part::Cylinder] Cylinder036
  Angle = 360
  AttacherType = Attacher::AttachEngine3D
  Height = 10
  Placement = pos=(0,0,36.15) rot=(0,0,1;0rad)
  Radius = 4
FEATURE [Part::Cylinder] Cylinder037
  Angle = 360
  AttacherType = Attacher::AttachEngine3D
  Height = 20
  Placement = pos=(0,0,36.15) rot=(0,0,1;0rad)
  Radius = 8.2
FEATURE [Part::MultiFuse] Fusion080  label="removeToCreteHoleForPlugHousing025"
  Placement = pos=(-42,19,36) rot=(0,1,0;1.5708rad)
  Shapes = -> [Cylinder037,Cylinder036]
FEATURE [Sketcher::SketchObject] Sketch050  label="topSketch012"
  FullyConstrained = true
  sketch-geometry (4):
    g0: LineSegment StartX=16.8446 StartY=31.512 StartZ=0 EndX=16.3251 EndY=34.4666 EndZ=0
    g1: ArcOfCircle CenterX=19 CenterY=19.2524 CenterZ=0 NormalX=0 NormalY=0 NormalZ=1 AngleXU=0 Radius=15.4476 StartAngle=1.74483 EndAngle=2.72717
    g2: ArcOfCircle CenterX=19 CenterY=19.2524 CenterZ=0 NormalX=0 NormalY=0 NormalZ=1 AngleXU=0 Radius=12.4476 StartAngle=1.74483 EndAngle=2.73189
    g3: LineSegment StartX=4.86004 StartY=25.4725 StartZ=0 EndX=7.58253 EndY=24.2107 EndZ=0
  constraints (7):
    c: Block(g0)
    c: Coincident(g1,g0)
    c: Coincident(g2,g0)
    c: Coincident(g3,g1)
    c: Coincident(g3,g2)
    c: Block(g1)
    c: Block(g2)
FEATURE [Part::Extrusion] Extrude041
  Base = -> Sketch050
  Dir = (0,0,1)
  DirMode = 2
  FaceMakerClass = Part::FaceMakerBullseye
  LengthFwd = 10.6
  LengthRev = 0
  Placement = pos=(0,0,31) rot=(0,0,1;0rad)
  Solid = true
  Symmetric = false
FEATURE [Part::Cut] Cut035
  Base = -> Extrude041
  Placement = pos=(0,0,-0.3) rot=(0,0,1;0rad)
  Tool = -> Fusion080
FEATURE [Part::Cut] Cut036
  Base = -> Box023
  Tool = -> Cut035
FEATURE [Part::Fillet] Fillet027
  Base = -> Cut036
  Edges = 1 edges r=0.7: [Edge13]
FEATURE [Part::Fillet] Fillet028
  Base = -> Fillet027
  Edges = 1 edges r=0.7: [Edge13]
FEATURE [Part::Fillet] Fillet029
  Base = -> Fillet028
  Edges = 1 edges r=0.7: [Edge16]
FEATURE [Part::Fillet] Fillet030
  Base = -> Fillet029
  Edges = 1 edges r=0.7: [Edge11]
FEATURE [Part::Fillet] Fillet031
  Base = -> Fillet030
  Edges = 1 edges r=0.7: [Edge10]
FEATURE [Part::Fillet] Fillet032
  Base = -> Fillet031
  Edges = 1 edges r=1.2: [Edge5]
FEATURE [Part::Fillet] Fillet033
  Base = -> Fillet032
  Edges = 1 edges r=1.2: [Edge12]
FEATURE [Part::Fillet] Fillet034  label="wireHousingRetainer"
  Base = -> Fillet033
  Edges = 1 edges r=2: [Edge1]
  Placement = pos=(0.3,0,0) rot=(0,0,1;0rad)
FEATURE [Part::Feature] Face099
  shape: bbox 3.5 x 17.8 x 2e-07 mm, 1 faces, 0 solids (baked)
FEATURE [Part::Revolution] Revolve107  label="removeToCreateScrewAndThreadedInsertHole034"
  Angle = 360
  Axis = (0,1,0)
  Base = (0,0,0)
  FaceMakerClass = Part::FaceMakerBullseye
  Placement = pos=(12.5,0,10) rot=(0,0,1;0rad)
  Solid = false
  Source = -> Face099
  Symmetric = false
FEATURE [Part::Feature] Face100
  shape: bbox 3.5 x 17.8 x 2e-07 mm, 1 faces, 0 solids (baked)
FEATURE [Part::Revolution] Revolve108  label="removeToCreateScrewAndThreadedInsertHole035"
  Angle = 360
  Axis = (0,1,0)
  Base = (0,0,0)
  FaceMakerClass = Part::FaceMakerBullseye
  Placement = pos=(12.5,0,62) rot=(0,0,1;0rad)
  Solid = false
  Source = -> Face100
  Symmetric = false
FEATURE [Part::Feature] Face101
  shape: bbox 3.5 x 17.8 x 2e-07 mm, 1 faces, 0 solids (baked)
FEATURE [Part::Revolution] Revolve109  label="removeToCreateScrewAndThreadedInsertHole036"
  Angle = 360
  Axis = (0,1,0)
  Base = (0,0,0)
  FaceMakerClass = Part::FaceMakerBullseye
  Placement = pos=(89.5,0,68.5) rot=(0,0,1;0rad)
  Solid = false
  Source = -> Face101
  Symmetric = false
FEATURE [Part::Feature] Face102
  shape: bbox 3.5 x 17.8 x 2e-07 mm, 1 faces, 0 solids (baked)
FEATURE [Part::Revolution] Revolve110  label="removeToCreateScrewAndThreadedInsertHole037"
  Angle = 360
  Axis = (0,1,0)
  Base = (0,0,0)
  FaceMakerClass = Part::FaceMakerBullseye
  Placement = pos=(89.5,0,3.5) rot=(0,0,1;0rad)
  Solid = false
  Source = -> Face102
  Symmetric = false
FEATURE [Part::Feature] Face103
  shape: bbox 3.5 x 17.8 x 2e-07 mm, 1 faces, 0 solids (baked)
FEATURE [Part::Revolution] Revolve111  label="removeToCreateScrewAndThreadedInsertHole038"
  Angle = 360
  Axis = (0,1,0)
  Base = (0,0,0)
  FaceMakerClass = Part::FaceMakerBullseye
  Placement = pos=(109.5,4.7,3.5) rot=(0,0,1;0rad)
  Solid = false
  Source = -> Face103
  Symmetric = false
FEATURE [Part::Feature] Face104
  shape: bbox 3.5 x 17.8 x 2e-07 mm, 1 faces, 0 solids (baked)
FEATURE [Part::Revolution] Revolve112  label="removeToCreateScrewAndThreadedInsertHole039"
  Angle = 360
  Axis = (0,1,0)
  Base = (0,0,0)
  FaceMakerClass = Part::FaceMakerBullseye
  Placement = pos=(109.5,4.7,68.5) rot=(0,0,1;0rad)
  Solid = false
  Source = -> Face104
  Symmetric = false
FEATURE [Part::MultiFuse] Fusion081  label="removeToCreateScrewAndThreadedInsertHole040"
  Shapes = -> [Revolve107,Revolve108,Revolve109,Revolve110,Revolve111,Revolve112]
FEATURE [Part::MultiFuse] Fusion082  label="casePillars002"
  Shapes = -> [Revolve094,Revolve092,Revolve090,Revolve089,Revolve091,Revolve093]
FEATURE [Part::Cut] Cut037  label="casePillars003"
  Base = -> Fusion082
  Tool = -> Fusion081
FEATURE [Sketcher::SketchObject] Sketch051
  FullyConstrained = true
  Placement = pos=(117,19,0) rot=(0.57735,0.57735,0.57735;2.0944rad)
  sketch-geometry (48):
    g0: LineSegment StartX=-49.19 StartY=69.25 StartZ=0 EndX=-49.19 EndY=66.25 EndZ=0
    g1: LineSegment StartX=-49.19 StartY=63.5 StartZ=0 EndX=-49.19 EndY=60.5 EndZ=0
    g2: LineSegment StartX=-49.19 StartY=57.75 StartZ=0 EndX=-49.19 EndY=54.75 EndZ=0
    g3: LineSegment StartX=-49.19 StartY=52 StartZ=0 EndX=-49.19 EndY=49 EndZ=0
    g4: LineSegment StartX=-49.19 StartY=46.25 StartZ=0 EndX=-49.19 EndY=43.25 EndZ=0
    g5: LineSegment StartX=-49.19 StartY=40.5 StartZ=0 EndX=-49.19 EndY=37.5 EndZ=0
    g6: LineSegment StartX=-49.19 StartY=34.5 StartZ=0 EndX=-49.19 EndY=31.5 EndZ=0
    g7: LineSegment StartX=-49.19 StartY=28.75 StartZ=0 EndX=-49.19 EndY=25.75 EndZ=0
    g8: LineSegment StartX=-49.19 StartY=23 StartZ=0 EndX=-49.19 EndY=20 EndZ=0
    g9: LineSegment StartX=-49.19 StartY=17.25 StartZ=0 EndX=-49.19 EndY=14.25 EndZ=0
    g10: LineSegment StartX=-49.19 StartY=11.5 StartZ=0 EndX=-49.19 EndY=8.5 EndZ=0
    g11: LineSegment StartX=-49.19 StartY=5.75 StartZ=0 EndX=-49.19 EndY=2.75 EndZ=0
    g12: ArcOfCircle CenterX=-1.5 CenterY=67.75 CenterZ=0 NormalX=0 NormalY=0 NormalZ=1 AngleXU=0 Radius=1.5 StartAngle=4.71239 EndAngle=7.85398
    g13: ArcOfCircle CenterX=-1.5 CenterY=62 CenterZ=0 NormalX=0 NormalY=0 NormalZ=1 AngleXU=0 Radius=1.5 StartAngle=4.71239 EndAngle=7.85398
    g14: ArcOfCircle CenterX=-1.5 CenterY=56.25 CenterZ=0 NormalX=0 NormalY=0 NormalZ=1 AngleXU=0 Radius=1.5 StartAngle=4.71239 EndAngle=7.85398
    g15: ArcOfCircle CenterX=-11.49 CenterY=50.5 CenterZ=0 NormalX=0 NormalY=0 NormalZ=1 AngleXU=0 Radius=1.5 StartAngle=4.71239 EndAngle=7.85398
    g16: ArcOfCircle CenterX=-16.28 CenterY=44.75 CenterZ=0 NormalX=0 NormalY=0 NormalZ=1 AngleXU=0 Radius=1.5 StartAngle=4.71239 EndAngle=7.85398
    g17: ArcOfCircle CenterX=-18.2337 CenterY=39 CenterZ=0 NormalX=0 NormalY=0 NormalZ=1 AngleXU=0 Radius=1.5 StartAngle=4.71485 EndAngle=7.85398
    g18: ArcOfCircle CenterX=-16.2837 CenterY=27.25 CenterZ=0 NormalX=0 NormalY=0 NormalZ=1 AngleXU=0 Radius=1.5 StartAngle=4.71485 EndAngle=7.85398
    g19: ArcOfCircle CenterX=-18.2337 CenterY=33 CenterZ=0 NormalX=0 NormalY=0 NormalZ=1 AngleXU=0 Radius=1.5 StartAngle=4.71485 EndAngle=7.85398
    g20: ArcOfCircle CenterX=-11.49 CenterY=21.5 CenterZ=0 NormalX=0 NormalY=0 NormalZ=1 AngleXU=0 Radius=1.5 StartAngle=4.71239 EndAngle=7.85398
    g21: ArcOfCircle CenterX=-1.5 CenterY=4.25 CenterZ=0 NormalX=0 NormalY=0 NormalZ=1 AngleXU=0 Radius=1.5 StartAngle=4.71239 EndAngle=7.85398
    g22: ArcOfCircle CenterX=-1.5 CenterY=10 CenterZ=0 NormalX=0 NormalY=0 NormalZ=1 AngleXU=0 Radius=1.5 StartAngle=4.71239 EndAngle=7.85398
    g23: ArcOfCircle CenterX=-1.5 CenterY=15.75 CenterZ=0 NormalX=0 NormalY=0 NormalZ=1 AngleXU=0 Radius=1.5 StartAngle=4.71239 EndAngle=7.85398
    g24: LineSegment StartX=-49.19 StartY=69.25 StartZ=0 EndX=-1.5 EndY=69.25 EndZ=0
    g25: LineSegment StartX=-49.19 StartY=66.25 StartZ=0 EndX=-1.5 EndY=66.25 EndZ=0
    g26: LineSegment StartX=-49.19 StartY=63.5 StartZ=0 EndX=-1.5 EndY=63.5 EndZ=0
    g27: LineSegment StartX=-49.19 StartY=60.5 StartZ=0 EndX=-1.5 EndY=60.5 EndZ=0
    g28: LineSegment StartX=-49.19 StartY=57.75 StartZ=0 EndX=-1.5 EndY=57.75 EndZ=0
    g29: LineSegment StartX=-49.19 StartY=54.75 StartZ=0 EndX=-1.5 EndY=54.75 EndZ=0
    g30: LineSegment StartX=-49.19 StartY=52 StartZ=0 EndX=-11.49 EndY=52 EndZ=0
    g31: LineSegment StartX=-49.19 StartY=49 StartZ=0 EndX=-11.49 EndY=49 EndZ=0
    g32: LineSegment StartX=-49.19 StartY=46.25 StartZ=0 EndX=-16.28 EndY=46.25 EndZ=0
    g33: LineSegment StartX=-49.19 StartY=43.25 StartZ=0 EndX=-16.28 EndY=43.25 EndZ=0
    g34: LineSegment StartX=-49.19 StartY=40.5 StartZ=0 EndX=-18.2337 EndY=40.5 EndZ=0
    g35: LineSegment StartX=-49.19 StartY=37.5 StartZ=0 EndX=-18.23 EndY=37.5 EndZ=0
    g36: LineSegment StartX=-49.19 StartY=34.5 StartZ=0 EndX=-18.2337 EndY=34.5 EndZ=0
    g37: LineSegment StartX=-49.19 StartY=31.5 StartZ=0 EndX=-18.23 EndY=31.5 EndZ=0
    g38: LineSegment StartX=-49.19 StartY=28.75 StartZ=0 EndX=-16.2837 EndY=28.75 EndZ=0
    g39: LineSegment StartX=-49.19 StartY=25.75 StartZ=0 EndX=-16.28 EndY=25.75 EndZ=0
    g40: LineSegment StartX=-49.19 StartY=23 StartZ=0 EndX=-11.49 EndY=23 EndZ=0
    g41: LineSegment StartX=-49.19 StartY=20 StartZ=0 EndX=-11.49 EndY=20 EndZ=0
    g42: LineSegment StartX=-49.19 StartY=17.25 StartZ=0 EndX=-1.5 EndY=17.25 EndZ=0
    g43: LineSegment StartX=-49.19 StartY=14.25 StartZ=0 EndX=-1.5 EndY=14.25 EndZ=0
    g44: LineSegment StartX=-49.19 StartY=11.5 StartZ=0 EndX=-1.5 EndY=11.5 EndZ=0
    g45: LineSegment StartX=-49.19 StartY=8.5 StartZ=0 EndX=-1.5 EndY=8.5 EndZ=0
    g46: LineSegment StartX=-49.19 StartY=5.75 StartZ=0 EndX=-1.5 EndY=5.75 EndZ=0
    g47: LineSegment StartX=-49.19 StartY=2.75 StartZ=0 EndX=-1.5 EndY=2.75 EndZ=0
  constraints (120):
    c: Vertical(g0)
    c: Distance(g0) = 3
    c: Block(g0)
    c: Vertical(g1)
    c: Distance(g1) = 3
    c: Vertical(g2)
    c: Equal(g0,g2) = 3
    c: Block(g2)
    c: Vertical(g3)
    c: Equal(g1,g3) = 3
    c: Vertical(g4)
    c: Equal(g0,g4) = 3
    c: Block(g4)
    c: Vertical(g5)
    c: Equal(g1,g5) = 3
    c: Vertical(g6)
    c: Equal(g0,g6) = 3
    c: Block(g6)
    c: Vertical(g7)
    c: Equal(g1,g7) = 3
    c: Vertical(g8)
    c: Equal(g0,g8) = 3
    c: Block(g8)
    c: Vertical(g9)
    c: Equal(g1,g9) = 3
    c: Vertical(g10)
    c: Equal(g0,g10) = 3
    c: Block(g10)
    c: Vertical(g11)
    c: Equal(g1,g11) = 3
    c: Block(g12)
    c: Block(g13)
    c: Block(g14)
    c: Block(g15)
    c: Block(g16)
    c: Block(g17)
    c: Block(g18)
    c: Block(g19)
    c: Block(g20)
    c: Block(g21)
    c: Block(g22)
    c: Block(g23)
    c: Block(g11)
    c: Block(g9)
    c: Block(g7)
    c: Block(g5)
    c: Block(g3)
    c: Block(g1)
    c: Coincident(g24,g0)
    c: Coincident(g24,g12)
    c: Horizontal(g24)
    c: Coincident(g25,g0)
    c: Coincident(g25,g12)
    c: Horizontal(g25)
    c: Coincident(g26,g1)
    c: Coincident(g26,g13)
    c: Horizontal(g26)
    c: Coincident(g27,g1)
    c: Coincident(g27,g13)
    c: Horizontal(g27)
    c: Coincident(g28,g2)
    c: Coincident(g28,g14)
    c: Horizontal(g28)
    c: Coincident(g29,g2)
    c: Coincident(g29,g14)
    c: Horizontal(g29)
    c: Coincident(g30,g3)
    c: Coincident(g30,g15)
    c: Horizontal(g30)
    c: Coincident(g31,g3)
    c: Coincident(g31,g15)
    c: Horizontal(g31)
    c: Coincident(g32,g4)
    c: Coincident(g32,g16)
    c: Horizontal(g32)
    c: Coincident(g33,g4)
    c: Coincident(g33,g16)
    c: Horizontal(g33)
    c: Coincident(g34,g5)
    c: Coincident(g34,g17)
    c: Horizontal(g34)
    c: Coincident(g35,g5)
    c: Coincident(g35,g17)
    c: Horizontal(g35)
    c: Coincident(g36,g6)
    c: Coincident(g36,g19)
    c: Horizontal(g36)
    c: Coincident(g37,g6)
    c: Coincident(g37,g19)
    c: Horizontal(g37)
    c: Coincident(g38,g7)
    c: Coincident(g38,g18)
    c: Horizontal(g38)
    c: Coincident(g39,g7)
    c: Coincident(g39,g18)
    c: Horizontal(g39)
    c: Coincident(g40,g8)
    c: Coincident(g40,g20)
    c: Horizontal(g40)
    c: Coincident(g41,g8)
    c: Coincident(g41,g20)
    c: Horizontal(g41)
    c: Coincident(g42,g9)
    c: Coincident(g42,g23)
    c: Horizontal(g42)
    c: Coincident(g43,g9)
    c: Coincident(g43,g23)
    c: Horizontal(g43)
    c: Coincident(g44,g10)
    c: Coincident(g44,g22)
    c: Horizontal(g44)
    c: Coincident(g45,g10)
    c: Coincident(g45,g22)
    c: Horizontal(g45)
    c: Coincident(g46,g11)
    c: Coincident(g46,g21)
    c: Horizontal(g46)
    c: Coincident(g47,g11)
    c: Coincident(g47,g21)
    c: Horizontal(g47)
FEATURE [Part::Extrusion] Extrude042
  Base = -> Sketch051
  Dir = (1,-2e-16,2e-16)
  DirMode = 2
  FaceMakerClass = Part::FaceMakerBullseye
  LengthFwd = 19
  LengthRev = 0
  Placement = pos=(-19,0,0) rot=(0,0,1;0rad)
  Solid = true
  Symmetric = false
FEATURE [Part::Fillet] Fillet035  label="removeToCreateVentalationHoles"
  Base = -> Extrude042
  Edges = <same value as first occurrence — deduplicated (x6 in doc)>
  Placement = pos=(7,0,0) rot=(0,0,1;0rad)
FEATURE [Part::Cut] Cut038  label="top017"
  Base = -> Cut033
  Tool = -> Fillet035
FEATURE [Sketcher::SketchObject] Sketch052  label="bottomSketch001"
  FullyConstrained = true
  sketch-geometry (45):
    g0: LineSegment StartX=6.29999 StartY=8 StartZ=0 EndX=3.29999 EndY=8 EndZ=0
    g1: LineSegment StartX=3.29999 StartY=8 StartZ=0 EndX=3.29999 EndY=-6.03275e-07 EndZ=0
    g2: ArcOfCircle CenterX=8.29999 CenterY=5 CenterZ=0 NormalX=0 NormalY=0 NormalZ=1 AngleXU=0 Radius=2 StartAngle=3.14159 EndAngle=4.71239
    g3: LineSegment StartX=6.29999 StartY=8 StartZ=0 EndX=6.29999 EndY=5 EndZ=0
    g4: ArcOfCircle CenterX=105 CenterY=19 CenterZ=0 NormalX=0 NormalY=0 NormalZ=1 AngleXU=0 Radius=12.7 StartAngle=4.71239 EndAngle=5.94289
    g5-g11: Circle x7 (B-spline internal-alignment scaffolding for g12; pole/knot coordinates omitted)
    g12: BSplineCurve PolesCount=7 KnotsCount=5 Degree=3 IsPeriodic=0
    g13-g17: GeomPoint x5 (B-spline internal-alignment scaffolding for g12; pole/knot coordinates omitted)
    g18: ArcOfCircle CenterX=105 CenterY=19 CenterZ=0 NormalX=0 NormalY=0 NormalZ=1 AngleXU=0 Radius=15.7 StartAngle=5.81226 EndAngle=6.28319
    g19: BSplineCurve PolesCount=5 KnotsCount=3 Degree=3 IsPeriodic=0
    g20: LineSegment StartX=8.29999 StartY=3 StartZ=0 EndX=101.7 EndY=3 EndZ=0
    g21: LineSegment StartX=3.29999 StartY=-6.03275e-07 StartZ=0 EndX=105 EndY=-6.03275e-07 EndZ=0
    g22: LineSegment StartX=120.974 StartY=8.71251 StartZ=0 EndX=122.332 EndY=7.83778 EndZ=0
    g23: LineSegment StartX=105 StartY=-6.03274e-07 StartZ=0 EndX=113 EndY=-6.03274e-07 EndZ=0
    g24: ArcOfCircle CenterX=105 CenterY=19 CenterZ=0 NormalX=0 NormalY=0 NormalZ=1 AngleXU=0 Radius=20.6155 StartAngle=5.11091 EndAngle=5.71103
    g25: ArcOfCircle CenterX=117.7 CenterY=19 CenterZ=0 NormalX=0 NormalY=0 NormalZ=1 AngleXU=0 Radius=3 StartAngle=1.2e-15 EndAngle=2.10468
    g26: Circle CenterX=116.345 CenterY=16.3232 CenterZ=0 NormalX=0 NormalY=0 NormalZ=1 AngleXU=0 Radius=1
    g27: Circle CenterX=117.24 CenterY=15.7584 CenterZ=0 NormalX=0 NormalY=0 NormalZ=1 AngleXU=0 Radius=1
    g28: Circle CenterX=116.972 CenterY=14.7612 CenterZ=0 NormalX=0 NormalY=0 NormalZ=1 AngleXU=0 Radius=1
    g29: BSplineCurve PolesCount=3 KnotsCount=2 Degree=2 IsPeriodic=0
    g30: GeomPoint X=116.345 Y=16.3232 Z=0
    g31: GeomPoint X=116.972 Y=14.7612 Z=0
    g32: Circle CenterX=115.828 CenterY=17.157 CenterZ=0 NormalX=0 NormalY=0 NormalZ=1 AngleXU=0 Radius=1
    g33: Circle CenterX=115.841 CenterY=16.639 CenterZ=0 NormalX=0 NormalY=0 NormalZ=1 AngleXU=0 Radius=1
    g34: Circle CenterX=116.345 CenterY=16.3232 CenterZ=0 NormalX=0 NormalY=0 NormalZ=1 AngleXU=0 Radius=1
    g35: BSplineCurve PolesCount=3 KnotsCount=2 Degree=2 IsPeriodic=0
    g36: GeomPoint X=115.828 Y=17.157 Z=0
    g37: GeomPoint X=116.345 Y=16.3232 Z=0
    g38: LineSegment StartX=115.828 StartY=17.157 StartZ=0 EndX=115.828 EndY=20.8307 EndZ=0
    g39: Circle CenterX=115.828 CenterY=20.8307 CenterZ=0 NormalX=0 NormalY=0 NormalZ=1 AngleXU=0 Radius=1
    g40: Circle CenterX=115.831 CenterY=21.3396 CenterZ=0 NormalX=0 NormalY=0 NormalZ=1 AngleXU=0 Radius=1
    g41: Circle CenterX=116.173 CenterY=21.5825 CenterZ=0 NormalX=0 NormalY=0 NormalZ=1 AngleXU=0 Radius=1
    g42: BSplineCurve PolesCount=3 KnotsCount=2 Degree=2 IsPeriodic=0
    g43: GeomPoint X=115.828 Y=20.8307 Z=0
    g44: GeomPoint X=116.173 Y=21.5825 Z=0
  constraints (70):
    c: Horizontal(g0)
    c: Distance(g0) = 3
    c: Coincident(g1,g0)
    c: Vertical(g1)
    c: Block(g2)
    c: Block(g0)
    c: Coincident(g3,g0)
    c: Coincident(g3,g2)
    c: Vertical(g3)
    c: Block(g1)
    c: Block(g4)
    c: Coincident(g19,g4)
    c: Block(g19)
    c: Equal(g5, g6-g11) x6
    c: InternalAlignment(g5-g11 -> g12) x7
    c: InternalAlignment(g13-g17 -> g12) x5
    c: Block(g12)
    c: Coincident(g18,g12)
    c: Block(g18)
    c: Coincident(g20,g2)
    c: Coincident(g20,g19)
    c: Horizontal(g20)
    c: Distance(g20) = 93.4
    c: Coincident(g21,g1)
    c: Horizontal(g21)
    c: Distance(g21) = 101.7
    c: Horizontal(g23)
    c: Distance(g23) = 8
    c: Coincident(g24,g23)
    c: Block(g23)
    c: Coincident(g22,g24)
    c: Block(g24)
    c: Block(g22)
    c: Distance(g22) = 1.61553
    c: Coincident(g25,g18)
    c: Block(g25)
    c: Weight(g26) = 1
    c: Equal(g26,g27)
    c: Equal(g26,g28)
    c: Coincident(g29,g4)
    c: InternalAlignment(g26,g29)
    c: InternalAlignment(g27,g29)
    c: InternalAlignment(g28,g29)
    c: InternalAlignment(g30,g29)
    c: InternalAlignment(g31,g29)
    c: Block(g29)
    c: Weight(g32) = 1
    c: Equal(g32,g33)
    c: Equal(g32,g34)
    c: Coincident(g35,g29)
    c: InternalAlignment(g32,g35)
    c: InternalAlignment(g33,g35)
    c: InternalAlignment(g34,g35)
    c: InternalAlignment(g36,g35)
    c: InternalAlignment(g37,g35)
    c: Block(g35)
    c: Coincident(g38,g35)
    c: Vertical(g38)
    c: Block(g38)
    c: Coincident(g42,g38)
    c: Weight(g39) = 1
    c: Equal(g39,g40)
    c: Equal(g39,g41)
    c: Coincident(g42,g25)
    c: InternalAlignment(g39,g42)
    c: InternalAlignment(g40,g42)
    c: InternalAlignment(g41,g42)
    c: InternalAlignment(g43,g42)
    c: InternalAlignment(g44,g42)
    c: Block(g42)
FEATURE [Part::Extrusion] Extrude043  label="bottom010"
  Base = -> Sketch052
  Dir = (0,0,1)
  DirMode = 2
  FaceMakerClass = Part::FaceMakerBullseye
  LengthFwd = 71.4
  LengthRev = 0
  Placement = pos=(0,0,0.3) rot=(0,0,1;0rad)
  Solid = true
  Symmetric = false
FEATURE [Sketcher::SketchObject] Sketch053  label="topSketch013"
  FullyConstrained = true
  sketch-geometry (22):
    g0: LineSegment StartX=5.21097e-06 StartY=3 StartZ=0 EndX=5.21097e-06 EndY=19 EndZ=0
    g1: ArcOfCircle CenterX=19 CenterY=19 CenterZ=0 NormalX=0 NormalY=0 NormalZ=1 AngleXU=0 Radius=19 StartAngle=1.5708 EndAngle=3.14159
    g2: ArcOfCircle CenterX=19 CenterY=19 CenterZ=0 NormalX=0 NormalY=0 NormalZ=1 AngleXU=0 Radius=16 StartAngle=1.5708 EndAngle=3.14159
    g3: LineSegment StartX=114 StartY=35 StartZ=0 EndX=19 EndY=35 EndZ=0
    g4: LineSegment StartX=5.21097e-06 StartY=3 StartZ=0 EndX=5.21097e-06 EndY=0 EndZ=0
    g5: LineSegment StartX=3 StartY=0 StartZ=0 EndX=5.21097e-06 EndY=0 EndZ=0
    g6: LineSegment StartX=3 StartY=19 StartZ=0 EndX=3 EndY=0 EndZ=0
    g7: LineSegment StartX=19 StartY=38 StartZ=0 EndX=124 EndY=38 EndZ=0
    g8: Circle CenterX=119 CenterY=35 CenterZ=0 NormalX=0 NormalY=0 NormalZ=1 AngleXU=0 Radius=1
    g9: Circle CenterX=121 CenterY=35 CenterZ=0 NormalX=0 NormalY=0 NormalZ=1 AngleXU=0 Radius=1
    g10: Circle CenterX=121 CenterY=33 CenterZ=0 NormalX=0 NormalY=0 NormalZ=1 AngleXU=0 Radius=1
    g11: BSplineCurve PolesCount=3 KnotsCount=2 Degree=2 IsPeriodic=0
    g12: GeomPoint X=119 Y=35 Z=0
    g13: GeomPoint X=121 Y=33 Z=0
    g14: LineSegment StartX=119 StartY=35 StartZ=0 EndX=114 EndY=35 EndZ=0
    g15: ArcOfCircle CenterX=105 CenterY=19 CenterZ=0 NormalX=0 NormalY=0 NormalZ=1 AngleXU=0 Radius=16 StartAngle=5.60905 EndAngle=6.28319
    g16: LineSegment StartX=121 StartY=33 StartZ=0 EndX=121 EndY=19 EndZ=0
    g17: LineSegment StartX=117.5 StartY=9.01251 StartZ=0 EndX=121.163 EndY=9.0125 EndZ=0
    g18: ArcOfCircle CenterX=105 CenterY=19 CenterZ=0 NormalX=0 NormalY=0 NormalZ=1 AngleXU=0 Radius=20.6155 StartAngle=5.7297 EndAngle=6.28319
    g19: LineSegment StartX=121.163 StartY=9.0125 StartZ=0 EndX=122.538 EndY=8.16329 EndZ=0
    g20: LineSegment StartX=124 StartY=38 StartZ=0 EndX=125.616 EndY=38 EndZ=0
    g21: LineSegment StartX=125.616 StartY=19 StartZ=0 EndX=125.616 EndY=38 EndZ=0
  constraints (50):
    c: Vertical(g0)
    c: Block(g0)
    c: Coincident(g1,g0)
    c: Block(g1)
    c: Coincident(g2,g1)
    c: Block(g2)
    c: Coincident(g3,g2)
    c: Horizontal(g3)
    c: Tangent(g3,g2)
    c: Coincident(g4,g0)
    c: Distance(g4) = 3
    c: Vertical(g4)
    c: Coincident(g5,g4)
    c: Horizontal(g5)
    c: Coincident(g6,g2)
    c: Coincident(g6,g5)
    c: Vertical(g6)
    c: Horizontal(g7)
    c: Distance(g7) = 105
    c: Coincident(g7,g1)
    c: Block(g3)
    c: Weight(g8) = 1
    c: Equal(g8,g9)
    c: Equal(g8,g10)
    c: InternalAlignment(g8,g11)
    c: InternalAlignment(g9,g11)
    c: InternalAlignment(g10,g11)
    c: InternalAlignment(g12,g11)
    c: InternalAlignment(g13,g11)
    c: Block(g11)
    c: Coincident(g14,g11)
    c: Coincident(g14,g3)
    c: Horizontal(g14)
    c: Block(g15)
    c: Coincident(g16,g11)
    c: Coincident(g16,g15)
    c: Vertical(g16)
    c: Distance(g16) = 14
    c: Coincident(g17,g15)
    c: Block(g18)
    c: Coincident(g19,g18)
    c: Coincident(g20,g7)
    c: Horizontal(g20)
    c: Vertical(g21)
    c: Coincident(g20,g21)
    c: Block(g20)
    c: Block(g21)
    c: Block(g19)
    c: Block(g17)
    c: Distance(g20) = 1.61553
FEATURE [Part::Extrusion] Extrude044
  Base = -> Sketch053
  Dir = (0,0,1)
  DirMode = 2
  FaceMakerClass = Part::FaceMakerBullseye
  LengthFwd = 72
  LengthRev = 0
  Solid = true
  Symmetric = false
FEATURE [Part::Fillet] Fillet036  label="top018"
  Base = -> Extrude044
  Edges = 1 edges r=2: [Edge41]
FEATURE [Sketcher::SketchObject] Sketch054
  FullyConstrained = false
  Placement = pos=(0,0,0) rot=(1,0,0;1.5708rad)
  sketch-geometry (24):
    g0: ArcOfCircle CenterX=-4 CenterY=-10.5 CenterZ=0 NormalX=0 NormalY=0 NormalZ=1 AngleXU=0 Radius=1.5 StartAngle=6e-16 EndAngle=3.14159
    g1: ArcOfCircle CenterX=-34.2 CenterY=-10.5 CenterZ=0 NormalX=0 NormalY=0 NormalZ=1 AngleXU=0 Radius=1.5 StartAngle=0 EndAngle=3.14159
    g2: ArcOfCircle CenterX=-34.2 CenterY=-27.7 CenterZ=0 NormalX=0 NormalY=0 NormalZ=1 AngleXU=0 Radius=1.5 StartAngle=3.14159 EndAngle=6.28319
    g3: ArcOfCircle CenterX=-4 CenterY=-27.7 CenterZ=0 NormalX=0 NormalY=0 NormalZ=1 AngleXU=0 Radius=1.5 StartAngle=3.1416 EndAngle=6.28319
    g4: ArcOfCircle CenterX=-10 CenterY=-4.3 CenterZ=0 NormalX=0 NormalY=0 NormalZ=1 AngleXU=0 Radius=1.5 StartAngle=2e-16 EndAngle=3.14159
    g5: ArcOfCircle CenterX=-16.1 CenterY=-1.8 CenterZ=0 NormalX=0 NormalY=0 NormalZ=1 AngleXU=0 Radius=1.5 StartAngle=5e-16 EndAngle=3.14159
    g6: ArcOfCircle CenterX=-22.1 CenterY=-1.8 CenterZ=0 NormalX=0 NormalY=0 NormalZ=1 AngleXU=0 Radius=1.5 StartAngle=5e-16 EndAngle=3.14159
    g7: ArcOfCircle CenterX=-28.2 CenterY=-4.3 CenterZ=0 NormalX=0 NormalY=0 NormalZ=1 AngleXU=0 Radius=1.5 StartAngle=2e-16 EndAngle=3.14159
    g8: ArcOfCircle CenterX=-10 CenterY=-33.9 CenterZ=0 NormalX=0 NormalY=0 NormalZ=1 AngleXU=0 Radius=1.5 StartAngle=3.14159 EndAngle=6.28319
    g9: ArcOfCircle CenterX=-16.1 CenterY=-36.4 CenterZ=0 NormalX=0 NormalY=0 NormalZ=1 AngleXU=0 Radius=1.5 StartAngle=3.14159 EndAngle=6.28319
    g10: ArcOfCircle CenterX=-22.1 CenterY=-36.4 CenterZ=0 NormalX=0 NormalY=0 NormalZ=1 AngleXU=0 Radius=1.5 StartAngle=3.14159 EndAngle=6.28319
    g11: ArcOfCircle CenterX=-28.2 CenterY=-33.9 CenterZ=0 NormalX=0 NormalY=0 NormalZ=1 AngleXU=0 Radius=1.5 StartAngle=3.14159 EndAngle=6.28319
    g12: LineSegment StartX=-35.7 StartY=-10.5 StartZ=0 EndX=-35.7 EndY=-27.7 EndZ=0
    g13: LineSegment StartX=-32.7 StartY=-10.5 StartZ=0 EndX=-32.7 EndY=-27.7 EndZ=0
    g14: LineSegment StartX=-29.7 StartY=-33.9 StartZ=0 EndX=-29.7 EndY=-4.3 EndZ=0
    g15: LineSegment StartX=-26.7 StartY=-33.9 StartZ=0 EndX=-26.7 EndY=-4.3 EndZ=0
    g16: LineSegment StartX=-2.5 StartY=-10.5 StartZ=0 EndX=-2.5 EndY=-27.7 EndZ=0
    g17: LineSegment StartX=-8.5 StartY=-4.3 StartZ=0 EndX=-8.5 EndY=-33.9 EndZ=0
    g18: LineSegment StartX=-5.5 StartY=-10.5 StartZ=0 EndX=-5.5 EndY=-27.7 EndZ=0
    g19: LineSegment StartX=-11.5 StartY=-4.3 StartZ=0 EndX=-11.5 EndY=-33.9 EndZ=0
    g20: LineSegment StartX=-14.6 StartY=-1.8 StartZ=0 EndX=-14.6 EndY=-36.4 EndZ=0
    g21: LineSegment StartX=-17.6 StartY=-1.8 StartZ=0 EndX=-17.6 EndY=-36.4 EndZ=0
    g22: LineSegment StartX=-20.6 StartY=-36.4 StartZ=0 EndX=-20.6 EndY=-1.8 EndZ=0
    g23: LineSegment StartX=-23.6 StartY=-1.8 StartZ=0 EndX=-23.6 EndY=-36.4 EndZ=0
  constraints (48):
    c: Block(g0)
    c: Block(g1)
    c: Block(g2)
    c: Block(g3)
    c: Block(g4)
    c: Block(g5)
    c: Block(g6)
    c: Block(g7)
    c: Block(g8)
    c: Block(g9)
    c: Block(g10)
    c: Block(g11)
    c: Coincident(g12,g1)
    c: Coincident(g12,g2)
    c: Vertical(g12)
    c: Coincident(g13,g1)
    c: Coincident(g13,g2)
    c: Vertical(g13)
    c: Coincident(g14,g11)
    c: Coincident(g14,g7)
    c: Vertical(g14)
    c: Coincident(g15,g11)
    c: Coincident(g15,g7)
    c: Vertical(g15)
    c: Coincident(g16,g0)
    c: Coincident(g16,g3)
    c: Vertical(g16)
    c: Coincident(g17,g4)
    c: Coincident(g17,g8)
    c: Vertical(g17)
    c: Coincident(g18,g0)
    c: Coincident(g18,g3)
    c: Vertical(g18)
    c: Coincident(g19,g4)
    c: Coincident(g19,g8)
    c: Vertical(g19)
    c: Coincident(g20,g5)
    c: Coincident(g20,g9)
    c: Vertical(g20)
    c: Coincident(g21,g5)
    c: Coincident(g21,g9)
    c: Vertical(g21)
    c: Coincident(g22,g10)
    c: Coincident(g22,g6)
    c: Vertical(g22)
    c: Coincident(g23,g6)
    c: Coincident(g23,g10)
    c: Vertical(g23)
FEATURE [Part::Extrusion] Extrude045  label="removeToCreateFanGrillHoles003"
  Base = -> Sketch054
  Dir = (0,-1,6e-16)
  DirMode = 2
  FaceMakerClass = Part::FaceMakerBullseye
  LengthFwd = 10
  LengthRev = 0
  Placement = pos=(65.4,44,54.82) rot=(0,0,1;0rad)
  Solid = true
  Symmetric = false
FEATURE [Part::Feature] Face105 .. Face108  x4 (patterned run collapsed; names and placements below)
  shape: bbox 3.5 x 17.8 x 2e-07 mm, 1 faces, 0 solids (baked)
FEATURE [Part::Revolution] Revolve113  label="removeToCreateScrewAndThreadedInsertHole041"
  Angle = 360
  Axis = (0,1,0)
  Base = (0,0,0)
  FaceMakerClass = Part::FaceMakerBullseye
  Placement = pos=(62.3,30.3,19.7) rot=(0,0,1;0rad)
  Solid = false
  Source = -> Face105
  Symmetric = false
FEATURE [Part::Revolution] Revolve114  label="removeToCreateScrewAndThreadedInsertHole042"
  Angle = 360
  Axis = (0,1,0)
  Base = (0,0,0)
  FaceMakerClass = Part::FaceMakerBullseye
  Placement = pos=(62.3,30.3,51.7) rot=(0,0,1;0rad)
  Solid = false
  Source = -> Face106
  Symmetric = false
FEATURE [Part::Revolution] Revolve115  label="removeToCreateScrewAndThreadedInsertHole043"
  Angle = 360
  Axis = (0,1,0)
  Base = (0,0,0)
  FaceMakerClass = Part::FaceMakerBullseye
  Placement = pos=(30.3,30.3,19.7) rot=(0,0,1;0rad)
  Solid = false
  Source = -> Face107
  Symmetric = false
FEATURE [Part::Revolution] Revolve116  label="removeToCreateScrewAndThreadedInsertHole044"
  Angle = 360
  Axis = (0,1,0)
  Base = (0,0,0)
  FaceMakerClass = Part::FaceMakerBullseye
  Placement = pos=(30.3,30.3,51.7) rot=(0,0,1;0rad)
  Solid = false
  Source = -> Face108
  Symmetric = false
FEATURE [Part::MultiFuse] Fusion083  label="createThreadedInsertHolesForFan004"
  Shapes = -> [Revolve113,Revolve114,Revolve115,Revolve116]
FEATURE [Part::Box] Box024  label="removeToCreteHoleForPlugHousing026"
  AttacherType = Attacher::AttachEngine3D
  Height = 28.6
  Length = 10
  Placement = pos=(-2,0,21.7) rot=(0,0,1;0rad)
  Width = 19
FEATURE [Part::Cylinder] Cylinder038  label="removeToCreteHoleForPlugHousing027"
  Angle = 360
  AttacherType = Attacher::AttachEngine3D
  Height = 20
  Placement = pos=(-2,19,36) rot=(0,1,0;1.5708rad)
  Radius = 14.3
FEATURE [Part::MultiFuse] Fusion084  label="removeToCreteHoleForPlugHousing028"
  Shapes = -> [Box024,Cylinder038]
FEATURE [Part::Cylinder] Cylinder039
  Angle = 360
  AttacherType = Attacher::AttachEngine3D
  Height = 20
  Placement = pos=(0,0,36.15) rot=(0,0,1;0rad)
  Radius = 14.3
FEATURE [Part::Cylinder] Cylinder040
  Angle = 360
  AttacherType = Attacher::AttachEngine3D
  Height = 10
  Placement = pos=(0,0,36.15) rot=(0,0,1;0rad)
  Radius = 4
FEATURE [Part::Box] Box025  label="removeToCreteHoleForPlugHousing030"
  AttacherType = Attacher::AttachEngine3D
  Height = 28.6
  Length = 20
  Placement = pos=(106.15,0,21.7) rot=(0,0,1;0rad)
  Width = 19
FEATURE [Part::MultiFuse] Fusion086  label="removeToCreteHoleForPlugHousing031"
  Placement = pos=(70,19,36) rot=(0,1,0;1.5708rad)
  Shapes = -> [Cylinder039,Cylinder040]
FEATURE [Part::MultiFuse] Fusion085  label="removeToCreteHoleForPlugHousing029"
  Shapes = -> [Box025,Fusion086]
FEATURE [Sketcher::SketchObject] Sketch055
  FullyConstrained = true
  Placement = pos=(117,19,0) rot=(0.57735,0.57735,0.57735;2.0944rad)
  sketch-geometry (48):
    g0: LineSegment StartX=-49.19 StartY=69.25 StartZ=0 EndX=-49.19 EndY=66.25 EndZ=0
    g1: LineSegment StartX=-49.19 StartY=63.5 StartZ=0 EndX=-49.19 EndY=60.5 EndZ=0
    g2: LineSegment StartX=-49.19 StartY=57.75 StartZ=0 EndX=-49.19 EndY=54.75 EndZ=0
    g3: LineSegment StartX=-49.19 StartY=52 StartZ=0 EndX=-49.19 EndY=49 EndZ=0
    g4: LineSegment StartX=-49.19 StartY=46.25 StartZ=0 EndX=-49.19 EndY=43.25 EndZ=0
    g5: LineSegment StartX=-49.19 StartY=40.5 StartZ=0 EndX=-49.19 EndY=37.5 EndZ=0
    g6: LineSegment StartX=-49.19 StartY=34.5 StartZ=0 EndX=-49.19 EndY=31.5 EndZ=0
    g7: LineSegment StartX=-49.19 StartY=28.75 StartZ=0 EndX=-49.19 EndY=25.75 EndZ=0
    g8: LineSegment StartX=-49.19 StartY=23 StartZ=0 EndX=-49.19 EndY=20 EndZ=0
    g9: LineSegment StartX=-49.19 StartY=17.25 StartZ=0 EndX=-49.19 EndY=14.25 EndZ=0
    g10: LineSegment StartX=-49.19 StartY=11.5 StartZ=0 EndX=-49.19 EndY=8.5 EndZ=0
    g11: LineSegment StartX=-49.19 StartY=5.75 StartZ=0 EndX=-49.19 EndY=2.75 EndZ=0
    g12: ArcOfCircle CenterX=-1.5 CenterY=67.75 CenterZ=0 NormalX=0 NormalY=0 NormalZ=1 AngleXU=0 Radius=1.5 StartAngle=4.71239 EndAngle=7.85398
    g13: ArcOfCircle CenterX=-1.5 CenterY=62 CenterZ=0 NormalX=0 NormalY=0 NormalZ=1 AngleXU=0 Radius=1.5 StartAngle=4.71239 EndAngle=7.85398
    g14: ArcOfCircle CenterX=-1.5 CenterY=56.25 CenterZ=0 NormalX=0 NormalY=0 NormalZ=1 AngleXU=0 Radius=1.5 StartAngle=4.71239 EndAngle=7.85398
    g15: ArcOfCircle CenterX=-11.49 CenterY=50.5 CenterZ=0 NormalX=0 NormalY=0 NormalZ=1 AngleXU=0 Radius=1.5 StartAngle=4.71239 EndAngle=7.85398
    g16: ArcOfCircle CenterX=-16.28 CenterY=44.75 CenterZ=0 NormalX=0 NormalY=0 NormalZ=1 AngleXU=0 Radius=1.5 StartAngle=4.71239 EndAngle=7.85398
    g17: ArcOfCircle CenterX=-18.2337 CenterY=39 CenterZ=0 NormalX=0 NormalY=0 NormalZ=1 AngleXU=0 Radius=1.5 StartAngle=4.71485 EndAngle=7.85398
    g18: ArcOfCircle CenterX=-16.2837 CenterY=27.25 CenterZ=0 NormalX=0 NormalY=0 NormalZ=1 AngleXU=0 Radius=1.5 StartAngle=4.71485 EndAngle=7.85398
    g19: ArcOfCircle CenterX=-18.2337 CenterY=33 CenterZ=0 NormalX=0 NormalY=0 NormalZ=1 AngleXU=0 Radius=1.5 StartAngle=4.71485 EndAngle=7.85398
    g20: ArcOfCircle CenterX=-11.49 CenterY=21.5 CenterZ=0 NormalX=0 NormalY=0 NormalZ=1 AngleXU=0 Radius=1.5 StartAngle=4.71239 EndAngle=7.85398
    g21: ArcOfCircle CenterX=-1.5 CenterY=4.25 CenterZ=0 NormalX=0 NormalY=0 NormalZ=1 AngleXU=0 Radius=1.5 StartAngle=4.71239 EndAngle=7.85398
    g22: ArcOfCircle CenterX=-1.5 CenterY=10 CenterZ=0 NormalX=0 NormalY=0 NormalZ=1 AngleXU=0 Radius=1.5 StartAngle=4.71239 EndAngle=7.85398
    g23: ArcOfCircle CenterX=-1.5 CenterY=15.75 CenterZ=0 NormalX=0 NormalY=0 NormalZ=1 AngleXU=0 Radius=1.5 StartAngle=4.71239 EndAngle=7.85398
    g24: LineSegment StartX=-49.19 StartY=69.25 StartZ=0 EndX=-1.5 EndY=69.25 EndZ=0
    g25: LineSegment StartX=-49.19 StartY=66.25 StartZ=0 EndX=-1.5 EndY=66.25 EndZ=0
    g26: LineSegment StartX=-49.19 StartY=63.5 StartZ=0 EndX=-1.5 EndY=63.5 EndZ=0
    g27: LineSegment StartX=-49.19 StartY=60.5 StartZ=0 EndX=-1.5 EndY=60.5 EndZ=0
    g28: LineSegment StartX=-49.19 StartY=57.75 StartZ=0 EndX=-1.5 EndY=57.75 EndZ=0
    g29: LineSegment StartX=-49.19 StartY=54.75 StartZ=0 EndX=-1.5 EndY=54.75 EndZ=0
    g30: LineSegment StartX=-49.19 StartY=52 StartZ=0 EndX=-11.49 EndY=52 EndZ=0
    g31: LineSegment StartX=-49.19 StartY=49 StartZ=0 EndX=-11.49 EndY=49 EndZ=0
    g32: LineSegment StartX=-49.19 StartY=46.25 StartZ=0 EndX=-16.28 EndY=46.25 EndZ=0
    g33: LineSegment StartX=-49.19 StartY=43.25 StartZ=0 EndX=-16.28 EndY=43.25 EndZ=0
    g34: LineSegment StartX=-49.19 StartY=40.5 StartZ=0 EndX=-18.2337 EndY=40.5 EndZ=0
    g35: LineSegment StartX=-49.19 StartY=37.5 StartZ=0 EndX=-18.23 EndY=37.5 EndZ=0
    g36: LineSegment StartX=-49.19 StartY=34.5 StartZ=0 EndX=-18.2337 EndY=34.5 EndZ=0
    g37: LineSegment StartX=-49.19 StartY=31.5 StartZ=0 EndX=-18.23 EndY=31.5 EndZ=0
    g38: LineSegment StartX=-49.19 StartY=28.75 StartZ=0 EndX=-16.2837 EndY=28.75 EndZ=0
    g39: LineSegment StartX=-49.19 StartY=25.75 StartZ=0 EndX=-16.28 EndY=25.75 EndZ=0
    g40: LineSegment StartX=-49.19 StartY=23 StartZ=0 EndX=-11.49 EndY=23 EndZ=0
    g41: LineSegment StartX=-49.19 StartY=20 StartZ=0 EndX=-11.49 EndY=20 EndZ=0
    g42: LineSegment StartX=-49.19 StartY=17.25 StartZ=0 EndX=-1.5 EndY=17.25 EndZ=0
    g43: LineSegment StartX=-49.19 StartY=14.25 StartZ=0 EndX=-1.5 EndY=14.25 EndZ=0
    g44: LineSegment StartX=-49.19 StartY=11.5 StartZ=0 EndX=-1.5 EndY=11.5 EndZ=0
    g45: LineSegment StartX=-49.19 StartY=8.5 StartZ=0 EndX=-1.5 EndY=8.5 EndZ=0
    g46: LineSegment StartX=-49.19 StartY=5.75 StartZ=0 EndX=-1.5 EndY=5.75 EndZ=0
    g47: LineSegment StartX=-49.19 StartY=2.75 StartZ=0 EndX=-1.5 EndY=2.75 EndZ=0
  constraints (120):
    c: Vertical(g0)
    c: Distance(g0) = 3
    c: Block(g0)
    c: Vertical(g1)
    c: Distance(g1) = 3
    c: Vertical(g2)
    c: Equal(g0,g2) = 3
    c: Block(g2)
    c: Vertical(g3)
    c: Equal(g1,g3) = 3
    c: Vertical(g4)
    c: Equal(g0,g4) = 3
    c: Block(g4)
    c: Vertical(g5)
    c: Equal(g1,g5) = 3
    c: Vertical(g6)
    c: Equal(g0,g6) = 3
    c: Block(g6)
    c: Vertical(g7)
    c: Equal(g1,g7) = 3
    c: Vertical(g8)
    c: Equal(g0,g8) = 3
    c: Block(g8)
    c: Vertical(g9)
    c: Equal(g1,g9) = 3
    c: Vertical(g10)
    c: Equal(g0,g10) = 3
    c: Block(g10)
    c: Vertical(g11)
    c: Equal(g1,g11) = 3
    c: Block(g12)
    c: Block(g13)
    c: Block(g14)
    c: Block(g15)
    c: Block(g16)
    c: Block(g17)
    c: Block(g18)
    c: Block(g19)
    c: Block(g20)
    c: Block(g21)
    c: Block(g22)
    c: Block(g23)
    c: Block(g11)
    c: Block(g9)
    c: Block(g7)
    c: Block(g5)
    c: Block(g3)
    c: Block(g1)
    c: Coincident(g24,g0)
    c: Coincident(g24,g12)
    c: Horizontal(g24)
    c: Coincident(g25,g0)
    c: Coincident(g25,g12)
    c: Horizontal(g25)
    c: Coincident(g26,g1)
    c: Coincident(g26,g13)
    c: Horizontal(g26)
    c: Coincident(g27,g1)
    c: Coincident(g27,g13)
    c: Horizontal(g27)
    c: Coincident(g28,g2)
    c: Coincident(g28,g14)
    c: Horizontal(g28)
    c: Coincident(g29,g2)
    c: Coincident(g29,g14)
    c: Horizontal(g29)
    c: Coincident(g30,g3)
    c: Coincident(g30,g15)
    c: Horizontal(g30)
    c: Coincident(g31,g3)
    c: Coincident(g31,g15)
    c: Horizontal(g31)
    c: Coincident(g32,g4)
    c: Coincident(g32,g16)
    c: Horizontal(g32)
    c: Coincident(g33,g4)
    c: Coincident(g33,g16)
    c: Horizontal(g33)
    c: Coincident(g34,g5)
    c: Coincident(g34,g17)
    c: Horizontal(g34)
    c: Coincident(g35,g5)
    c: Coincident(g35,g17)
    c: Horizontal(g35)
    c: Coincident(g36,g6)
    c: Coincident(g36,g19)
    c: Horizontal(g36)
    c: Coincident(g37,g6)
    c: Coincident(g37,g19)
    c: Horizontal(g37)
    c: Coincident(g38,g7)
    c: Coincident(g38,g18)
    c: Horizontal(g38)
    c: Coincident(g39,g7)
    c: Coincident(g39,g18)
    c: Horizontal(g39)
    c: Coincident(g40,g8)
    c: Coincident(g40,g20)
    c: Horizontal(g40)
    c: Coincident(g41,g8)
    c: Coincident(g41,g20)
    c: Horizontal(g41)
    c: Coincident(g42,g9)
    c: Coincident(g42,g23)
    c: Horizontal(g42)
    c: Coincident(g43,g9)
    c: Coincident(g43,g23)
    c: Horizontal(g43)
    c: Coincident(g44,g10)
    c: Coincident(g44,g22)
    c: Horizontal(g44)
    c: Coincident(g45,g10)
    c: Coincident(g45,g22)
    c: Horizontal(g45)
    c: Coincident(g46,g11)
    c: Coincident(g46,g21)
    c: Horizontal(g46)
    c: Coincident(g47,g11)
    c: Coincident(g47,g21)
    c: Horizontal(g47)
FEATURE [Part::Extrusion] Extrude046
  Base = -> Sketch055
  Dir = (1,0,0)
  DirMode = 2
  FaceMakerClass = Part::FaceMakerBullseye
  LengthFwd = 23
  LengthRev = 0
  Placement = pos=(-19,0,0) rot=(0,0,1;0rad)
  Solid = true
  Symmetric = false
FEATURE [Part::Fillet] Fillet038  label="removeToCreateVentalationHoles001"
  Base = -> Extrude046
  Edges = <same value as first occurrence — deduplicated (x6 in doc)>
  Placement = pos=(7,0,0) rot=(0,0,1;0rad)
FEATURE [Sketcher::SketchObject] Sketch056  label="topSketch014"
  FullyConstrained = true
  sketch-geometry (22):
    g0: LineSegment StartX=5.21097e-06 StartY=3 StartZ=0 EndX=5.21097e-06 EndY=19 EndZ=0
    g1: ArcOfCircle CenterX=19 CenterY=19 CenterZ=0 NormalX=0 NormalY=0 NormalZ=1 AngleXU=0 Radius=19 StartAngle=1.5708 EndAngle=3.14159
    g2: ArcOfCircle CenterX=19 CenterY=19 CenterZ=0 NormalX=0 NormalY=0 NormalZ=1 AngleXU=0 Radius=16 StartAngle=1.5708 EndAngle=3.14159
    g3: LineSegment StartX=114 StartY=35 StartZ=0 EndX=19 EndY=35 EndZ=0
    g4: LineSegment StartX=5.21097e-06 StartY=3 StartZ=0 EndX=5.21097e-06 EndY=0 EndZ=0
    g5: LineSegment StartX=3 StartY=0 StartZ=0 EndX=5.21097e-06 EndY=0 EndZ=0
    g6: LineSegment StartX=3 StartY=19 StartZ=0 EndX=3 EndY=0 EndZ=0
    g7: LineSegment StartX=19 StartY=38 StartZ=0 EndX=124 EndY=38 EndZ=0
    g8: Circle CenterX=119 CenterY=35 CenterZ=0 NormalX=0 NormalY=0 NormalZ=1 AngleXU=0 Radius=1
    g9: Circle CenterX=121 CenterY=35 CenterZ=0 NormalX=0 NormalY=0 NormalZ=1 AngleXU=0 Radius=1
    g10: Circle CenterX=121 CenterY=33 CenterZ=0 NormalX=0 NormalY=0 NormalZ=1 AngleXU=0 Radius=1
    g11: BSplineCurve PolesCount=3 KnotsCount=2 Degree=2 IsPeriodic=0
    g12: GeomPoint X=119 Y=35 Z=0
    g13: GeomPoint X=121 Y=33 Z=0
    g14: LineSegment StartX=119 StartY=35 StartZ=0 EndX=114 EndY=35 EndZ=0
    g15: ArcOfCircle CenterX=105 CenterY=19 CenterZ=0 NormalX=0 NormalY=0 NormalZ=1 AngleXU=0 Radius=16 StartAngle=5.60905 EndAngle=6.28319
    g16: LineSegment StartX=121 StartY=33 StartZ=0 EndX=121 EndY=19 EndZ=0
    g17: LineSegment StartX=117.5 StartY=9.01251 StartZ=0 EndX=121.163 EndY=9.0125 EndZ=0
    g18: ArcOfCircle CenterX=105 CenterY=19 CenterZ=0 NormalX=0 NormalY=0 NormalZ=1 AngleXU=0 Radius=20.6155 StartAngle=5.7297 EndAngle=6.28319
    g19: LineSegment StartX=121.163 StartY=9.0125 StartZ=0 EndX=122.538 EndY=8.16329 EndZ=0
    g20: LineSegment StartX=124 StartY=38 StartZ=0 EndX=125.616 EndY=38 EndZ=0
    g21: LineSegment StartX=125.616 StartY=19 StartZ=0 EndX=125.616 EndY=38 EndZ=0
  constraints (49):
    c: Vertical(g0)
    c: Block(g0)
    c: Coincident(g1,g0)
    c: Block(g1)
    c: Coincident(g2,g1)
    c: Block(g2)
    c: Coincident(g3,g2)
    c: Horizontal(g3)
    c: Tangent(g3,g2)
    c: Coincident(g4,g0)
    c: Distance(g4) = 3
    c: Vertical(g4)
    c: Coincident(g5,g4)
    c: Horizontal(g5)
    c: Coincident(g6,g2)
    c: Coincident(g6,g5)
    c: Vertical(g6)
    c: Horizontal(g7)
    c: Distance(g7) = 105
    c: Coincident(g7,g1)
    c: Block(g3)
    c: Weight(g8) = 1
    c: Equal(g8,g9)
    c: Equal(g8,g10)
    c: InternalAlignment(g8,g11)
    c: InternalAlignment(g9,g11)
    c: InternalAlignment(g10,g11)
    c: InternalAlignment(g12,g11)
    c: InternalAlignment(g13,g11)
    c: Block(g11)
    c: Coincident(g14,g11)
    c: Coincident(g14,g3)
    c: Horizontal(g14)
    c: Block(g15)
    c: Coincident(g16,g11)
    c: Coincident(g16,g15)
    c: Vertical(g16)
    c: Distance(g16) = 14
    c: Coincident(g17,g15)
    c: Block(g18)
    c: Coincident(g19,g18)
    c: Coincident(g20,g7)
    c: Horizontal(g20)
    c: Vertical(g21)
    c: Coincident(g20,g21)
    c: Block(g20)
    c: Block(g21)
    c: Block(g19)
    c: Block(g17)
FEATURE [Part::Box] Box026  label="removeToCreteHoleForPlugHousing032"
  AttacherType = Attacher::AttachEngine3D
  Height = 28.6
  Length = 10
  Placement = pos=(-2,0,21.7) rot=(0,0,1;0rad)
  Width = 19
FEATURE [Part::Feature] Face109 .. Face112  x4 (patterned run collapsed; names and placements below)
  shape: bbox 3.5 x 17.8 x 2e-07 mm, 1 faces, 0 solids (baked)
FEATURE [Part::Revolution] Revolve117  label="removeToCreateScrewAndThreadedInsertHole045"
  Angle = 360
  Axis = (0,1,0)
  Base = (0,0,0)
  FaceMakerClass = Part::FaceMakerBullseye
  Placement = pos=(62.3,30.3,19.7) rot=(0,0,1;0rad)
  Solid = false
  Source = -> Face109
  Symmetric = false
FEATURE [Part::Revolution] Revolve118  label="removeToCreateScrewAndThreadedInsertHole046"
  Angle = 360
  Axis = (0,1,0)
  Base = (0,0,0)
  FaceMakerClass = Part::FaceMakerBullseye
  Placement = pos=(62.3,30.3,51.7) rot=(0,0,1;0rad)
  Solid = false
  Source = -> Face110
  Symmetric = false
FEATURE [Part::Revolution] Revolve119  label="removeToCreateScrewAndThreadedInsertHole047"
  Angle = 360
  Axis = (0,1,0)
  Base = (0,0,0)
  FaceMakerClass = Part::FaceMakerBullseye
  Placement = pos=(30.3,30.3,19.7) rot=(0,0,1;0rad)
  Solid = false
  Source = -> Face111
  Symmetric = false
FEATURE [Part::Revolution] Revolve120  label="removeToCreateScrewAndThreadedInsertHole048"
  Angle = 360
  Axis = (0,1,0)
  Base = (0,0,0)
  FaceMakerClass = Part::FaceMakerBullseye
  Placement = pos=(30.3,30.3,51.7) rot=(0,0,1;0rad)
  Solid = false
  Source = -> Face112
  Symmetric = false
FEATURE [Part::MultiFuse] Fusion087  label="createThreadedInsertHolesForFan005"
  Shapes = -> [Revolve117,Revolve118,Revolve119,Revolve120]
FEATURE [Part::Extrusion] Extrude047
  Base = -> Sketch056
  Dir = (0,0,1)
  DirMode = 2
  FaceMakerClass = Part::FaceMakerBullseye
  LengthFwd = 72
  LengthRev = 0
  Solid = true
  Symmetric = false
FEATURE [Part::Fillet] Fillet039  label="top019"
  Base = -> Extrude047
  Edges = 1 edges r=2: [Edge35]
FEATURE [Sketcher::SketchObject] Sketch057
  FullyConstrained = false
  Placement = pos=(0,0,0) rot=(1,0,0;1.5708rad)
  sketch-geometry (24):
    g0: ArcOfCircle CenterX=-4 CenterY=-10.5 CenterZ=0 NormalX=0 NormalY=0 NormalZ=1 AngleXU=0 Radius=1.5 StartAngle=6e-16 EndAngle=3.14159
    g1: ArcOfCircle CenterX=-34.2 CenterY=-10.5 CenterZ=0 NormalX=0 NormalY=0 NormalZ=1 AngleXU=0 Radius=1.5 StartAngle=0 EndAngle=3.14159
    g2: ArcOfCircle CenterX=-34.2 CenterY=-27.7 CenterZ=0 NormalX=0 NormalY=0 NormalZ=1 AngleXU=0 Radius=1.5 StartAngle=3.14159 EndAngle=6.28319
    g3: ArcOfCircle CenterX=-4 CenterY=-27.7 CenterZ=0 NormalX=0 NormalY=0 NormalZ=1 AngleXU=0 Radius=1.5 StartAngle=3.1416 EndAngle=6.28319
    g4: ArcOfCircle CenterX=-10 CenterY=-4.3 CenterZ=0 NormalX=0 NormalY=0 NormalZ=1 AngleXU=0 Radius=1.5 StartAngle=2e-16 EndAngle=3.14159
    g5: ArcOfCircle CenterX=-16.1 CenterY=-1.8 CenterZ=0 NormalX=0 NormalY=0 NormalZ=1 AngleXU=0 Radius=1.5 StartAngle=5e-16 EndAngle=3.14159
    g6: ArcOfCircle CenterX=-22.1 CenterY=-1.8 CenterZ=0 NormalX=0 NormalY=0 NormalZ=1 AngleXU=0 Radius=1.5 StartAngle=5e-16 EndAngle=3.14159
    g7: ArcOfCircle CenterX=-28.2 CenterY=-4.3 CenterZ=0 NormalX=0 NormalY=0 NormalZ=1 AngleXU=0 Radius=1.5 StartAngle=2e-16 EndAngle=3.14159
    g8: ArcOfCircle CenterX=-10 CenterY=-33.9 CenterZ=0 NormalX=0 NormalY=0 NormalZ=1 AngleXU=0 Radius=1.5 StartAngle=3.14159 EndAngle=6.28319
    g9: ArcOfCircle CenterX=-16.1 CenterY=-36.4 CenterZ=0 NormalX=0 NormalY=0 NormalZ=1 AngleXU=0 Radius=1.5 StartAngle=3.14159 EndAngle=6.28319
    g10: ArcOfCircle CenterX=-22.1 CenterY=-36.4 CenterZ=0 NormalX=0 NormalY=0 NormalZ=1 AngleXU=0 Radius=1.5 StartAngle=3.14159 EndAngle=6.28319
    g11: ArcOfCircle CenterX=-28.2 CenterY=-33.9 CenterZ=0 NormalX=0 NormalY=0 NormalZ=1 AngleXU=0 Radius=1.5 StartAngle=3.14159 EndAngle=6.28319
    g12: LineSegment StartX=-35.7 StartY=-10.5 StartZ=0 EndX=-35.7 EndY=-27.7 EndZ=0
    g13: LineSegment StartX=-32.7 StartY=-10.5 StartZ=0 EndX=-32.7 EndY=-27.7 EndZ=0
    g14: LineSegment StartX=-29.7 StartY=-33.9 StartZ=0 EndX=-29.7 EndY=-4.3 EndZ=0
    g15: LineSegment StartX=-26.7 StartY=-33.9 StartZ=0 EndX=-26.7 EndY=-4.3 EndZ=0
    g16: LineSegment StartX=-2.5 StartY=-10.5 StartZ=0 EndX=-2.5 EndY=-27.7 EndZ=0
    g17: LineSegment StartX=-8.5 StartY=-4.3 StartZ=0 EndX=-8.5 EndY=-33.9 EndZ=0
    g18: LineSegment StartX=-5.5 StartY=-10.5 StartZ=0 EndX=-5.5 EndY=-27.7 EndZ=0
    g19: LineSegment StartX=-11.5 StartY=-4.3 StartZ=0 EndX=-11.5 EndY=-33.9 EndZ=0
    g20: LineSegment StartX=-14.6 StartY=-1.8 StartZ=0 EndX=-14.6 EndY=-36.4 EndZ=0
    g21: LineSegment StartX=-17.6 StartY=-1.8 StartZ=0 EndX=-17.6 EndY=-36.4 EndZ=0
    g22: LineSegment StartX=-20.6 StartY=-36.4 StartZ=0 EndX=-20.6 EndY=-1.8 EndZ=0
    g23: LineSegment StartX=-23.6 StartY=-1.8 StartZ=0 EndX=-23.6 EndY=-36.4 EndZ=0
  constraints (48):
    c: Block(g0)
    c: Block(g1)
    c: Block(g2)
    c: Block(g3)
    c: Block(g4)
    c: Block(g5)
    c: Block(g6)
    c: Block(g7)
    c: Block(g8)
    c: Block(g9)
    c: Block(g10)
    c: Block(g11)
    c: Coincident(g12,g1)
    c: Coincident(g12,g2)
    c: Vertical(g12)
    c: Coincident(g13,g1)
    c: Coincident(g13,g2)
    c: Vertical(g13)
    c: Coincident(g14,g11)
    c: Coincident(g14,g7)
    c: Vertical(g14)
    c: Coincident(g15,g11)
    c: Coincident(g15,g7)
    c: Vertical(g15)
    c: Coincident(g16,g0)
    c: Coincident(g16,g3)
    c: Vertical(g16)
    c: Coincident(g17,g4)
    c: Coincident(g17,g8)
    c: Vertical(g17)
    c: Coincident(g18,g0)
    c: Coincident(g18,g3)
    c: Vertical(g18)
    c: Coincident(g19,g4)
    c: Coincident(g19,g8)
    c: Vertical(g19)
    c: Coincident(g20,g5)
    c: Coincident(g20,g9)
    c: Vertical(g20)
    c: Coincident(g21,g5)
    c: Coincident(g21,g9)
    c: Vertical(g21)
    c: Coincident(g22,g10)
    c: Coincident(g22,g6)
    c: Vertical(g22)
    c: Coincident(g23,g6)
    c: Coincident(g23,g10)
    c: Vertical(g23)
FEATURE [Part::Extrusion] Extrude048  label="removeToCreateFanGrillHoles004"
  Base = -> Sketch057
  Dir = (0,-1,6e-16)
  DirMode = 2
  FaceMakerClass = Part::FaceMakerBullseye
  LengthFwd = 10
  LengthRev = 0
  Placement = pos=(65.4,44,54.82) rot=(0,0,1;0rad)
  Solid = true
  Symmetric = false
FEATURE [Part::Cut] Cut040  label="top021"
  Base = -> Fillet039
  Tool = -> Extrude048
FEATURE [Part::Cylinder] Cylinder041  label="removeToCreteHoleForPlugHousing034"
  Angle = 360
  AttacherType = Attacher::AttachEngine3D
  Height = 20
  Placement = pos=(-2,19,36) rot=(0,1,0;1.5708rad)
  Radius = 14.3
FEATURE [Part::MultiFuse] Fusion089  label="removeToCreteHoleForPlugHousing035"
  Shapes = -> [Box026,Cylinder041]
FEATURE [Part::Cylinder] Cylinder042
  Angle = 360
  AttacherType = Attacher::AttachEngine3D
  Height = 20
  Placement = pos=(0,0,36.15) rot=(0,0,1;0rad)
  Radius = 14.3
FEATURE [Part::Cylinder] Cylinder043
  Angle = 360
  AttacherType = Attacher::AttachEngine3D
  Height = 10
  Placement = pos=(0,0,36.15) rot=(0,0,1;0rad)
  Radius = 4
FEATURE [Part::Box] Box027  label="removeToCreteHoleForPlugHousing036"
  AttacherType = Attacher::AttachEngine3D
  Height = 28.6
  Length = 20
  Placement = pos=(106.15,0,21.7) rot=(0,0,1;0rad)
  Width = 19
FEATURE [Part::Cut] Cut041  label="top022"
  Base = -> Cut040
  Tool = -> Fusion087
FEATURE [Part::Cut] Cut039  label="top020"
  Base = -> Cut041
  Tool = -> Fusion089
FEATURE [Part::MultiFuse] Fusion090  label="removeToCreteHoleForPlugHousing037"
  Placement = pos=(70,19,36) rot=(0,1,0;1.5708rad)
  Shapes = -> [Cylinder042,Cylinder043]
FEATURE [Part::MultiFuse] Fusion088  label="removeToCreteHoleForPlugHousing033"
  Shapes = -> [Box027,Fusion090]
FEATURE [Part::Cut] Cut042  label="removeToCreteHoleForPlugHousing038"
  Base = -> Cut039
  Tool = -> Fusion088
FEATURE [Part::MultiFuse] Fusion091  label="removeFromTop"
  Shapes = -> [Fillet038,Fusion085,Fusion084,Fusion083,Extrude045]
FEATURE [Part::Cut] Cut043  label="REAL TOP ====="
  Base = -> Fillet036
  Tool = -> Fusion091
FEATURE [Part::MultiFuse] Fusion092  label="caseScrewPillarBracket016"
  Shapes = -> [Extrude030,Extrude031,Extrude032,Extrude033,Extrude034,Extrude035,Extrude036,Extrude037,Box013,Box014]
FEATURE [Sketcher::SketchObject] Sketch058  label="topSketch015"
  FullyConstrained = true
  sketch-geometry (20):
    g0: LineSegment StartX=5.21097e-06 StartY=3 StartZ=0 EndX=5.21097e-06 EndY=19 EndZ=0
    g1: ArcOfCircle CenterX=19 CenterY=19 CenterZ=0 NormalX=0 NormalY=0 NormalZ=1 AngleXU=0 Radius=19 StartAngle=1.5708 EndAngle=3.14159
    g2: ArcOfCircle CenterX=19 CenterY=19 CenterZ=0 NormalX=0 NormalY=0 NormalZ=1 AngleXU=0 Radius=16 StartAngle=1.5708 EndAngle=3.14159
    g3: LineSegment StartX=114 StartY=35 StartZ=0 EndX=19 EndY=35 EndZ=0
    g4: LineSegment StartX=5.21097e-06 StartY=3 StartZ=0 EndX=5.21097e-06 EndY=0 EndZ=0
    g5: LineSegment StartX=3 StartY=0 StartZ=0 EndX=5.21097e-06 EndY=0 EndZ=0
    g6: LineSegment StartX=3 StartY=19 StartZ=0 EndX=3 EndY=0 EndZ=0
    g7: LineSegment StartX=19 StartY=38 StartZ=0 EndX=124 EndY=38 EndZ=0
    g8: Circle CenterX=119 CenterY=35 CenterZ=0 NormalX=0 NormalY=0 NormalZ=1 AngleXU=0 Radius=1
    g9: Circle CenterX=121 CenterY=35 CenterZ=0 NormalX=0 NormalY=0 NormalZ=1 AngleXU=0 Radius=1
    g10: Circle CenterX=121 CenterY=33 CenterZ=0 NormalX=0 NormalY=0 NormalZ=1 AngleXU=0 Radius=1
    g11: BSplineCurve PolesCount=3 KnotsCount=2 Degree=2 IsPeriodic=0
    g12: GeomPoint X=119 Y=35 Z=0
    g13: GeomPoint X=121 Y=33 Z=0
    g14: LineSegment StartX=119 StartY=35 StartZ=0 EndX=114 EndY=35 EndZ=0
    g15: ArcOfCircle CenterX=105 CenterY=19 CenterZ=0 NormalX=0 NormalY=0 NormalZ=1 AngleXU=0 Radius=19 StartAngle=5.7297 EndAngle=6.28319
    g16: ArcOfCircle CenterX=105 CenterY=19 CenterZ=0 NormalX=0 NormalY=0 NormalZ=1 AngleXU=0 Radius=16 StartAngle=5.60905 EndAngle=6.28319
    g17: LineSegment StartX=121 StartY=33 StartZ=0 EndX=121 EndY=19 EndZ=0
    g18: LineSegment StartX=124 StartY=38 StartZ=0 EndX=124 EndY=19 EndZ=0
    g19: LineSegment StartX=117.5 StartY=9.01251 StartZ=0 EndX=121.163 EndY=9.0125 EndZ=0
  constraints (46):
    c: Vertical(g0)
    c: Block(g0)
    c: Coincident(g1,g0)
    c: Block(g1)
    c: Coincident(g2,g1)
    c: Block(g2)
    c: Coincident(g3,g2)
    c: Horizontal(g3)
    c: Tangent(g3,g2)
    c: Coincident(g4,g0)
    c: Distance(g4) = 3
    c: Vertical(g4)
    c: Coincident(g5,g4)
    c: Horizontal(g5)
    c: Coincident(g6,g2)
    c: Coincident(g6,g5)
    c: Vertical(g6)
    c: Horizontal(g7)
    c: Distance(g7) = 105
    c: Coincident(g7,g1)
    c: Block(g3)
    c: Weight(g8) = 1
    c: Equal(g8,g9)
    c: Equal(g8,g10)
    c: InternalAlignment(g8,g11)
    c: InternalAlignment(g9,g11)
    c: InternalAlignment(g10,g11)
    c: InternalAlignment(g12,g11)
    c: InternalAlignment(g13,g11)
    c: Block(g11)
    c: Coincident(g14,g11)
    c: Coincident(g14,g3)
    c: Horizontal(g14)
    c: Block(g15)
    c: Coincident(g16,g15)
    c: Block(g16)
    c: Coincident(g17,g11)
    c: Coincident(g17,g16)
    c: Vertical(g17)
    c: Distance(g17) = 14
    c: Coincident(g18,g7)
    c: Coincident(g18,g15)
    c: Vertical(g18)
    c: Distance(g18) = 19
    c: Coincident(g19,g16)
    c: Coincident(g19,g15)
FEATURE [Part::Extrusion] Extrude049  label="top023"
  Base = -> Sketch058
  Dir = (0,0,1)
  DirMode = 2
  FaceMakerClass = Part::FaceMakerBullseye
  LengthFwd = 72
  LengthRev = 0
  Solid = true
  Symmetric = false
FEATURE [Sketcher::SketchObject] Sketch059
  FullyConstrained = true
  MapMode = 3
  Placement = pos=(0,0,0) rot=(1,0,0;1.5708rad)
  Support = -> [Extrude049]
  sketch-geometry (8):
    g0: Circle CenterX=80.351 CenterY=-67.6202 CenterZ=0 NormalX=0 NormalY=0 NormalZ=1 AngleXU=0 Radius=2
    g1: Circle CenterX=80.351 CenterY=-67.6202 CenterZ=0 NormalX=0 NormalY=0 NormalZ=1 AngleXU=0 Radius=3
    g2: Circle CenterX=80.351 CenterY=-4.92017 CenterZ=0 NormalX=0 NormalY=0 NormalZ=1 AngleXU=0 Radius=2
    g3: Circle CenterX=80.351 CenterY=-4.92017 CenterZ=0 NormalX=0 NormalY=0 NormalZ=1 AngleXU=0 Radius=3
    g4: Circle CenterX=23.851 CenterY=-4.92017 CenterZ=0 NormalX=0 NormalY=0 NormalZ=1 AngleXU=0 Radius=2
    g5: Circle CenterX=23.851 CenterY=-4.92017 CenterZ=0 NormalX=0 NormalY=0 NormalZ=1 AngleXU=0 Radius=3
    g6: Circle CenterX=23.851 CenterY=-67.6202 CenterZ=0 NormalX=0 NormalY=0 NormalZ=1 AngleXU=0 Radius=2
    g7: Circle CenterX=23.851 CenterY=-67.6202 CenterZ=0 NormalX=0 NormalY=0 NormalZ=1 AngleXU=0 Radius=3
  constraints (8):
    c: Block(g3)
    c: Block(g2)
    c: Block(g1)
    c: Block(g0)
    c: Block(g6)
    c: Block(g7)
    c: Block(g4)
    c: Block(g5)
FEATURE [Sketcher::SketchObject] Sketch060
  FullyConstrained = true
  MapMode = 3
  Placement = pos=(0,0,0) rot=(1,0,0;1.5708rad)
  Support = -> [Extrude049]
  sketch-geometry (8):
    g0: Circle CenterX=80.351 CenterY=-67.6202 CenterZ=0 NormalX=0 NormalY=0 NormalZ=1 AngleXU=0 Radius=3
    g1: Circle CenterX=80.351 CenterY=-4.92017 CenterZ=0 NormalX=0 NormalY=0 NormalZ=1 AngleXU=0 Radius=3
    g2: Circle CenterX=23.851 CenterY=-4.92017 CenterZ=0 NormalX=0 NormalY=0 NormalZ=1 AngleXU=0 Radius=3
    g3: Circle CenterX=23.851 CenterY=-67.6202 CenterZ=0 NormalX=0 NormalY=0 NormalZ=1 AngleXU=0 Radius=3
    g4: Circle CenterX=23.851 CenterY=-67.6202 CenterZ=0 NormalX=0 NormalY=0 NormalZ=1 AngleXU=0 Radius=5
    g5: Circle CenterX=80.351 CenterY=-67.6202 CenterZ=0 NormalX=0 NormalY=0 NormalZ=1 AngleXU=0 Radius=5
    g6: Circle CenterX=23.851 CenterY=-4.92017 CenterZ=0 NormalX=0 NormalY=0 NormalZ=1 AngleXU=0 Radius=5
    g7: Circle CenterX=80.351 CenterY=-4.92017 CenterZ=0 NormalX=0 NormalY=0 NormalZ=1 AngleXU=0 Radius=5
  constraints (8):
    c: Block(g1)
    c: Block(g0)
    c: Block(g3)
    c: Block(g2)
    c: Block(g5)
    c: Block(g4)
    c: Block(g6)
    c: Block(g7)
FEATURE [Sketcher::SketchObject] Sketch061
  FullyConstrained = true
  MapMode = 3
  Placement = pos=(0,0,0) rot=(1,0,0;1.5708rad)
  sketch-geometry (8):
    g0: Circle CenterX=80.351 CenterY=-67.6202 CenterZ=0 NormalX=0 NormalY=0 NormalZ=1 AngleXU=0 Radius=3
    g1: Circle CenterX=80.351 CenterY=-4.92017 CenterZ=0 NormalX=0 NormalY=0 NormalZ=1 AngleXU=0 Radius=3
    g2: Circle CenterX=23.851 CenterY=-4.92017 CenterZ=0 NormalX=0 NormalY=0 NormalZ=1 AngleXU=0 Radius=3
    g3: Circle CenterX=23.851 CenterY=-67.6202 CenterZ=0 NormalX=0 NormalY=0 NormalZ=1 AngleXU=0 Radius=3
    g4: Circle CenterX=23.851 CenterY=-67.6202 CenterZ=0 NormalX=0 NormalY=0 NormalZ=1 AngleXU=0 Radius=5
    g5: Circle CenterX=80.351 CenterY=-67.6202 CenterZ=0 NormalX=0 NormalY=0 NormalZ=1 AngleXU=0 Radius=5
    g6: Circle CenterX=23.851 CenterY=-4.92017 CenterZ=0 NormalX=0 NormalY=0 NormalZ=1 AngleXU=0 Radius=5
    g7: Circle CenterX=80.351 CenterY=-4.92017 CenterZ=0 NormalX=0 NormalY=0 NormalZ=1 AngleXU=0 Radius=5
  constraints (8):
    c: Block(g1)
    c: Block(g0)
    c: Block(g3)
    c: Block(g2)
    c: Block(g5)
    c: Block(g4)
    c: Block(g6)
    c: Block(g7)
FEATURE [Sketcher::SketchObject] Sketch062  label="topSketch016"
  FullyConstrained = true
  sketch-geometry (20):
    g0: LineSegment StartX=5.21097e-06 StartY=3 StartZ=0 EndX=5.21097e-06 EndY=19 EndZ=0
    g1: ArcOfCircle CenterX=19 CenterY=19 CenterZ=0 NormalX=0 NormalY=0 NormalZ=1 AngleXU=0 Radius=19 StartAngle=1.5708 EndAngle=3.14159
    g2: ArcOfCircle CenterX=19 CenterY=19 CenterZ=0 NormalX=0 NormalY=0 NormalZ=1 AngleXU=0 Radius=16 StartAngle=1.5708 EndAngle=3.14159
    g3: LineSegment StartX=114 StartY=35 StartZ=0 EndX=19 EndY=35 EndZ=0
    g4: LineSegment StartX=5.21097e-06 StartY=3 StartZ=0 EndX=5.21097e-06 EndY=0 EndZ=0
    g5: LineSegment StartX=3 StartY=0 StartZ=0 EndX=5.21097e-06 EndY=0 EndZ=0
    g6: LineSegment StartX=3 StartY=19 StartZ=0 EndX=3 EndY=0 EndZ=0
    g7: LineSegment StartX=19 StartY=38 StartZ=0 EndX=124 EndY=38 EndZ=0
    g8: Circle CenterX=119 CenterY=35 CenterZ=0 NormalX=0 NormalY=0 NormalZ=1 AngleXU=0 Radius=1
    g9: Circle CenterX=121 CenterY=35 CenterZ=0 NormalX=0 NormalY=0 NormalZ=1 AngleXU=0 Radius=1
    g10: Circle CenterX=121 CenterY=33 CenterZ=0 NormalX=0 NormalY=0 NormalZ=1 AngleXU=0 Radius=1
    g11: BSplineCurve PolesCount=3 KnotsCount=2 Degree=2 IsPeriodic=0
    g12: GeomPoint X=119 Y=35 Z=0
    g13: GeomPoint X=121 Y=33 Z=0
    g14: LineSegment StartX=119 StartY=35 StartZ=0 EndX=114 EndY=35 EndZ=0
    g15: ArcOfCircle CenterX=105 CenterY=19 CenterZ=0 NormalX=0 NormalY=0 NormalZ=1 AngleXU=0 Radius=19 StartAngle=5.7297 EndAngle=6.28319
    g16: ArcOfCircle CenterX=105 CenterY=19 CenterZ=0 NormalX=0 NormalY=0 NormalZ=1 AngleXU=0 Radius=16 StartAngle=5.60905 EndAngle=6.28319
    g17: LineSegment StartX=121 StartY=33 StartZ=0 EndX=121 EndY=19 EndZ=0
    g18: LineSegment StartX=124 StartY=38 StartZ=0 EndX=124 EndY=19 EndZ=0
    g19: LineSegment StartX=117.5 StartY=9.01251 StartZ=0 EndX=121.163 EndY=9.0125 EndZ=0
  constraints (46):
    c: Vertical(g0)
    c: Block(g0)
    c: Coincident(g1,g0)
    c: Block(g1)
    c: Coincident(g2,g1)
    c: Block(g2)
    c: Coincident(g3,g2)
    c: Horizontal(g3)
    c: Tangent(g3,g2)
    c: Coincident(g4,g0)
    c: Distance(g4) = 3
    c: Vertical(g4)
    c: Coincident(g5,g4)
    c: Horizontal(g5)
    c: Coincident(g6,g2)
    c: Coincident(g6,g5)
    c: Vertical(g6)
    c: Horizontal(g7)
    c: Distance(g7) = 105
    c: Coincident(g7,g1)
    c: Block(g3)
    c: Weight(g8) = 1
    c: Equal(g8,g9)
    c: Equal(g8,g10)
    c: InternalAlignment(g8,g11)
    c: InternalAlignment(g9,g11)
    c: InternalAlignment(g10,g11)
    c: InternalAlignment(g12,g11)
    c: InternalAlignment(g13,g11)
    c: Block(g11)
    c: Coincident(g14,g11)
    c: Coincident(g14,g3)
    c: Horizontal(g14)
    c: Block(g15)
    c: Coincident(g16,g15)
    c: Block(g16)
    c: Coincident(g17,g11)
    c: Coincident(g17,g16)
    c: Vertical(g17)
    c: Distance(g17) = 14
    c: Coincident(g18,g7)
    c: Coincident(g18,g15)
    c: Vertical(g18)
    c: Distance(g18) = 19
    c: Coincident(g19,g16)
    c: Coincident(g19,g15)
FEATURE [Part::Extrusion] Extrude053  label="top024"
  Base = -> Sketch062
  Dir = (0,0,1)
  DirMode = 2
  FaceMakerClass = Part::FaceMakerBullseye
  LengthFwd = 72
  LengthRev = 0
  Solid = true
  Symmetric = false
FEATURE [Sketcher::SketchObject] Sketch063
  FullyConstrained = true
  MapMode = 3
  Placement = pos=(0,0,0) rot=(1,0,0;1.5708rad)
  Support = -> [Extrude053]
  sketch-geometry (8):
    g0: Circle CenterX=80.351 CenterY=-67.6202 CenterZ=0 NormalX=0 NormalY=0 NormalZ=1 AngleXU=0 Radius=2
    g1: Circle CenterX=80.351 CenterY=-67.6202 CenterZ=0 NormalX=0 NormalY=0 NormalZ=1 AngleXU=0 Radius=3
    g2: Circle CenterX=80.351 CenterY=-4.92017 CenterZ=0 NormalX=0 NormalY=0 NormalZ=1 AngleXU=0 Radius=2
    g3: Circle CenterX=80.351 CenterY=-4.92017 CenterZ=0 NormalX=0 NormalY=0 NormalZ=1 AngleXU=0 Radius=3
    g4: Circle CenterX=23.851 CenterY=-4.92017 CenterZ=0 NormalX=0 NormalY=0 NormalZ=1 AngleXU=0 Radius=2
    g5: Circle CenterX=23.851 CenterY=-4.92017 CenterZ=0 NormalX=0 NormalY=0 NormalZ=1 AngleXU=0 Radius=3
    g6: Circle CenterX=23.851 CenterY=-67.6202 CenterZ=0 NormalX=0 NormalY=0 NormalZ=1 AngleXU=0 Radius=2
    g7: Circle CenterX=23.851 CenterY=-67.6202 CenterZ=0 NormalX=0 NormalY=0 NormalZ=1 AngleXU=0 Radius=3
  constraints (8):
    c: Block(g3)
    c: Block(g2)
    c: Block(g1)
    c: Block(g0)
    c: Block(g6)
    c: Block(g7)
    c: Block(g4)
    c: Block(g5)
FEATURE [Part::Extrusion] Extrude054
  Base = -> Sketch063
  Dir = (0,-1,2e-16)
  DirMode = 2
  FaceMakerClass = Part::FaceMakerBullseye
  LengthFwd = 6
  LengthRev = 0
  Placement = pos=(0,9,0) rot=(0,0,1;0rad)
  Solid = true
  Symmetric = false
FEATURE [Sketcher::SketchObject] Sketch064  label="topSketch017"
  FullyConstrained = true
  sketch-geometry (20):
    g0: LineSegment StartX=5.21097e-06 StartY=3 StartZ=0 EndX=5.21097e-06 EndY=19 EndZ=0
    g1: ArcOfCircle CenterX=19 CenterY=19 CenterZ=0 NormalX=0 NormalY=0 NormalZ=1 AngleXU=0 Radius=19 StartAngle=1.5708 EndAngle=3.14159
    g2: ArcOfCircle CenterX=19 CenterY=19 CenterZ=0 NormalX=0 NormalY=0 NormalZ=1 AngleXU=0 Radius=16 StartAngle=1.5708 EndAngle=3.14159
    g3: LineSegment StartX=114 StartY=35 StartZ=0 EndX=19 EndY=35 EndZ=0
    g4: LineSegment StartX=5.21097e-06 StartY=3 StartZ=0 EndX=5.21097e-06 EndY=0 EndZ=0
    g5: LineSegment StartX=3 StartY=0 StartZ=0 EndX=5.21097e-06 EndY=0 EndZ=0
    g6: LineSegment StartX=3 StartY=19 StartZ=0 EndX=3 EndY=0 EndZ=0
    g7: LineSegment StartX=19 StartY=38 StartZ=0 EndX=124 EndY=38 EndZ=0
    g8: Circle CenterX=119 CenterY=35 CenterZ=0 NormalX=0 NormalY=0 NormalZ=1 AngleXU=0 Radius=1
    g9: Circle CenterX=121 CenterY=35 CenterZ=0 NormalX=0 NormalY=0 NormalZ=1 AngleXU=0 Radius=1
    g10: Circle CenterX=121 CenterY=33 CenterZ=0 NormalX=0 NormalY=0 NormalZ=1 AngleXU=0 Radius=1
    g11: BSplineCurve PolesCount=3 KnotsCount=2 Degree=2 IsPeriodic=0
    g12: GeomPoint X=119 Y=35 Z=0
    g13: GeomPoint X=121 Y=33 Z=0
    g14: LineSegment StartX=119 StartY=35 StartZ=0 EndX=114 EndY=35 EndZ=0
    g15: ArcOfCircle CenterX=105 CenterY=19 CenterZ=0 NormalX=0 NormalY=0 NormalZ=1 AngleXU=0 Radius=19 StartAngle=5.7297 EndAngle=6.28319
    g16: ArcOfCircle CenterX=105 CenterY=19 CenterZ=0 NormalX=0 NormalY=0 NormalZ=1 AngleXU=0 Radius=16 StartAngle=5.60905 EndAngle=6.28319
    g17: LineSegment StartX=121 StartY=33 StartZ=0 EndX=121 EndY=19 EndZ=0
    g18: LineSegment StartX=124 StartY=38 StartZ=0 EndX=124 EndY=19 EndZ=0
    g19: LineSegment StartX=117.5 StartY=9.01251 StartZ=0 EndX=121.163 EndY=9.0125 EndZ=0
  constraints (46):
    c: Vertical(g0)
    c: Block(g0)
    c: Coincident(g1,g0)
    c: Block(g1)
    c: Coincident(g2,g1)
    c: Block(g2)
    c: Coincident(g3,g2)
    c: Horizontal(g3)
    c: Tangent(g3,g2)
    c: Coincident(g4,g0)
    c: Distance(g4) = 3
    c: Vertical(g4)
    c: Coincident(g5,g4)
    c: Horizontal(g5)
    c: Coincident(g6,g2)
    c: Coincident(g6,g5)
    c: Vertical(g6)
    c: Horizontal(g7)
    c: Distance(g7) = 105
    c: Coincident(g7,g1)
    c: Block(g3)
    c: Weight(g8) = 1
    c: Equal(g8,g9)
    c: Equal(g8,g10)
    c: InternalAlignment(g8,g11)
    c: InternalAlignment(g9,g11)
    c: InternalAlignment(g10,g11)
    c: InternalAlignment(g12,g11)
    c: InternalAlignment(g13,g11)
    c: Block(g11)
    c: Coincident(g14,g11)
    c: Coincident(g14,g3)
    c: Horizontal(g14)
    c: Block(g15)
    c: Coincident(g16,g15)
    c: Block(g16)
    c: Coincident(g17,g11)
    c: Coincident(g17,g16)
    c: Vertical(g17)
    c: Distance(g17) = 14
    c: Coincident(g18,g7)
    c: Coincident(g18,g15)
    c: Vertical(g18)
    c: Distance(g18) = 19
    c: Coincident(g19,g16)
    c: Coincident(g19,g15)
FEATURE [Sketcher::SketchObject] Sketch065
  FullyConstrained = true
  MapMode = 3
  Placement = pos=(0,0,0) rot=(1,0,0;1.5708rad)
  sketch-geometry (8):
    g0: Circle CenterX=80.351 CenterY=-67.6202 CenterZ=0 NormalX=0 NormalY=0 NormalZ=1 AngleXU=0 Radius=3
    g1: Circle CenterX=80.351 CenterY=-4.92017 CenterZ=0 NormalX=0 NormalY=0 NormalZ=1 AngleXU=0 Radius=3
    g2: Circle CenterX=23.851 CenterY=-4.92017 CenterZ=0 NormalX=0 NormalY=0 NormalZ=1 AngleXU=0 Radius=3
    g3: Circle CenterX=23.851 CenterY=-67.6202 CenterZ=0 NormalX=0 NormalY=0 NormalZ=1 AngleXU=0 Radius=3
    g4: Circle CenterX=23.851 CenterY=-67.6202 CenterZ=0 NormalX=0 NormalY=0 NormalZ=1 AngleXU=0 Radius=5
    g5: Circle CenterX=80.351 CenterY=-67.6202 CenterZ=0 NormalX=0 NormalY=0 NormalZ=1 AngleXU=0 Radius=5
    g6: Circle CenterX=23.851 CenterY=-4.92017 CenterZ=0 NormalX=0 NormalY=0 NormalZ=1 AngleXU=0 Radius=5
    g7: Circle CenterX=80.351 CenterY=-4.92017 CenterZ=0 NormalX=0 NormalY=0 NormalZ=1 AngleXU=0 Radius=5
  constraints (8):
    c: Block(g1)
    c: Block(g0)
    c: Block(g3)
    c: Block(g2)
    c: Block(g5)
    c: Block(g4)
    c: Block(g6)
    c: Block(g7)
FEATURE [Part::Extrusion] Extrude056
  Base = -> Sketch065
  Dir = (0,-1,2e-16)
  DirMode = 2
  FaceMakerClass = Part::FaceMakerBullseye
  LengthFwd = 2
  LengthRev = 0
  Solid = true
  Symmetric = false
FEATURE [Part::Extrusion] Extrude057  label="top025"
  Base = -> Sketch064
  Dir = (0,0,1)
  DirMode = 2
  FaceMakerClass = Part::FaceMakerBullseye
  LengthFwd = 72
  LengthRev = 0
  Solid = true
  Symmetric = false
FEATURE [Sketcher::SketchObject] Sketch066
  FullyConstrained = true
  MapMode = 3
  Placement = pos=(0,0,0) rot=(1,0,0;1.5708rad)
  Support = -> [Extrude057]
  sketch-geometry (8):
    g0: Circle CenterX=80.351 CenterY=-67.6202 CenterZ=0 NormalX=0 NormalY=0 NormalZ=1 AngleXU=0 Radius=3
    g1: Circle CenterX=80.351 CenterY=-4.92017 CenterZ=0 NormalX=0 NormalY=0 NormalZ=1 AngleXU=0 Radius=3
    g2: Circle CenterX=23.851 CenterY=-4.92017 CenterZ=0 NormalX=0 NormalY=0 NormalZ=1 AngleXU=0 Radius=3
    g3: Circle CenterX=23.851 CenterY=-67.6202 CenterZ=0 NormalX=0 NormalY=0 NormalZ=1 AngleXU=0 Radius=3
    g4: Circle CenterX=23.851 CenterY=-67.6202 CenterZ=0 NormalX=0 NormalY=0 NormalZ=1 AngleXU=0 Radius=5
    g5: Circle CenterX=80.351 CenterY=-67.6202 CenterZ=0 NormalX=0 NormalY=0 NormalZ=1 AngleXU=0 Radius=5
    g6: Circle CenterX=23.851 CenterY=-4.92017 CenterZ=0 NormalX=0 NormalY=0 NormalZ=1 AngleXU=0 Radius=5
    g7: Circle CenterX=80.351 CenterY=-4.92017 CenterZ=0 NormalX=0 NormalY=0 NormalZ=1 AngleXU=0 Radius=5
  constraints (8):
    c: Block(g1)
    c: Block(g0)
    c: Block(g3)
    c: Block(g2)
    c: Block(g5)
    c: Block(g4)
    c: Block(g6)
    c: Block(g7)
FEATURE [Part::Extrusion] Extrude055
  Base = -> Sketch066
  Dir = (0,-1,2e-16)
  DirMode = 2
  FaceMakerClass = Part::FaceMakerBullseye
  LengthFwd = 2
  LengthRev = 0
  Solid = true
  Symmetric = false
FEATURE [Part::Fillet] Fillet041
  Base = -> Extrude056
  Edges = 4 edges r=1.99: [Edge6,Edge12,Edge18,Edge24]
FEATURE [Part::Cut] Cut045
  Base = -> Extrude055
  Placement = pos=(0,6,0) rot=(0,0,1;0rad)
  Tool = -> Fillet041
FEATURE [Part::MultiFuse] Fusion095  label="pcbScrewPillars"
  Placement = pos=(-3.2,-1,72.3) rot=(0,0,1;0rad)
  Shapes = -> [Cut045,Extrude054]
FEATURE [Part::Feature] Face113
  shape: bbox 3.2 x 1.5 x 2e-07 mm, 1 faces, 0 solids (baked)
FEATURE [Part::Revolution] Revolve121  label="backCaseScrewRetainer002"
  Angle = 360
  Axis = (0,1,0)
  Base = (0,0,0)
  FaceMakerClass = Part::FaceMakerBullseye
  Placement = pos=(12.5,3,62) rot=(0,0,1;0rad)
  Solid = false
  Source = -> Face113
  Symmetric = false
FEATURE [Part::Feature] Face114
  shape: bbox 3.2 x 1.5 x 2e-07 mm, 1 faces, 0 solids (baked)
FEATURE [Part::Feature] Face115
  shape: bbox 3.2 x 1.5 x 2e-07 mm, 1 faces, 0 solids (baked)
FEATURE [Part::Feature] Face116
  shape: bbox 3.2 x 1.5 x 2e-07 mm, 1 faces, 0 solids (baked)
FEATURE [Part::Revolution] Revolve122  label="frontCaseScrewRetainer004"
  Angle = 360
  Axis = (0,1,0)
  Base = (0,0,0)
  FaceMakerClass = Part::FaceMakerBullseye
  Placement = pos=(89.5,3,68.5) rot=(0,0,1;0rad)
  Solid = false
  Source = -> Face115
  Symmetric = false
FEATURE [Part::Revolution] Revolve123  label="frontCaseScrewRetainer005"
  Angle = 360
  Axis = (0,1,0)
  Base = (0,0,0)
  FaceMakerClass = Part::FaceMakerBullseye
  Placement = pos=(89.5,3,3.5) rot=(0,0,1;0rad)
  Solid = false
  Source = -> Face116
  Symmetric = false
FEATURE [Part::Revolution] Revolve124  label="backCaseScrewRetainer003"
  Angle = 360
  Axis = (0,1,0)
  Base = (0,0,0)
  FaceMakerClass = Part::FaceMakerBullseye
  Placement = pos=(12.5,3,10) rot=(0,0,1;0rad)
  Solid = false
  Source = -> Face114
  Symmetric = false
FEATURE [Part::Feature] Face117
  shape: bbox 3.6 x 3.2 x 2e-07 mm, 1 faces, 0 solids (baked)
FEATURE [Part::Revolution] Revolve125  label="moreFrontCaseScrewRetainer004"
  Angle = 360
  Axis = (0,1,0)
  Base = (0,0,0)
  FaceMakerClass = Part::FaceMakerBullseye
  Placement = pos=(109.5,4.5,68.5) rot=(0,0,1;0rad)
  Solid = false
  Source = -> Face117
  Symmetric = false
FEATURE [Part::Feature] Face118
  shape: bbox 3.6 x 3.2 x 2e-07 mm, 1 faces, 0 solids (baked)
FEATURE [Part::Revolution] Revolve126  label="moreFrontCaseScrewRetainer005"
  Angle = 360
  Axis = (0,1,0)
  Base = (0,0,0)
  FaceMakerClass = Part::FaceMakerBullseye
  Placement = pos=(109.5,4.5,3.5) rot=(0,0,1;0rad)
  Solid = false
  Source = -> Face118
  Symmetric = false
FEATURE [Part::MultiFuse] Fusion096  label="screwRetainers001"
  Shapes = -> [Revolve126,Revolve125,Revolve124,Revolve123,Revolve122,Revolve121]
FEATURE [Part::Feature] Face119
  shape: bbox 10 x 16.5 x 2e-07 mm, 1 faces, 0 solids (baked)
FEATURE [Part::Revolution] Revolve130  label="plugHousing050"
  Angle = 360
  Axis = (0,1,0)
  Base = (0,0,0)
  FaceMakerClass = Part::FaceMakerBullseye
  Placement = pos=(0,0,36.15) rot=(0,0,1;0rad)
  Solid = false
  Source = -> Face119
  Symmetric = false
FEATURE [Part::Feature] Face120
  shape: bbox 10 x 16.5 x 2e-07 mm, 1 faces, 0 solids (baked)
FEATURE [Part::Feature] Face121
  shape: bbox 10 x 16.5 x 2e-07 mm, 1 faces, 0 solids (baked)
FEATURE [Part::Revolution] Revolve127  label="plugHousing047"
  Angle = 360
  Axis = (0,1,0)
  Base = (0,0,0)
  FaceMakerClass = Part::FaceMakerBullseye
  Placement = pos=(0,0,36.15) rot=(0,0,1;0rad)
  Solid = false
  Source = -> Face121
  Symmetric = false
FEATURE [Part::Feature] Face122
  shape: bbox 10 x 16.5 x 2e-07 mm, 1 faces, 0 solids (baked)
FEATURE [Part::Feature] Face123
  shape: bbox 10 x 16.5 x 2e-07 mm, 1 faces, 0 solids (baked)
FEATURE [Part::Revolution] Revolve128  label="plugHousing048"
  Angle = 360
  Axis = (0,1,0)
  Base = (0,0,0)
  FaceMakerClass = Part::FaceMakerBullseye
  Placement = pos=(0,0,36.15) rot=(0,0,1;0rad)
  Solid = false
  Source = -> Face123
  Symmetric = false
FEATURE [Part::MultiFuse] Fusion100  label="plugHousing054"
  Placement = pos=(0,0,0) rot=(0,0,1;1.5708rad)
  Shapes = -> [Revolve130,Revolve128]
FEATURE [Part::Feature] Face124
  shape: bbox 10 x 16.5 x 2e-07 mm, 1 faces, 0 solids (baked)
FEATURE [Part::Feature] Face125
  shape: bbox 10 x 16.5 x 2e-07 mm, 1 faces, 0 solids (baked)
FEATURE [Part::Revolution] Revolve129  label="plugHousing049"
  Angle = 360
  Axis = (0,1,0)
  Base = (0,0,0)
  FaceMakerClass = Part::FaceMakerBullseye
  Placement = pos=(0,0,36.15) rot=(0,0,1;0rad)
  Solid = false
  Source = -> Face125
  Symmetric = false
FEATURE [Part::Feature] Face126
  shape: bbox 10 x 16.5 x 2e-07 mm, 1 faces, 0 solids (baked)
FEATURE [Part::Revolution] Revolve131  label="plugHousing058"
  Angle = 360
  Axis = (0,1,0)
  Base = (0,0,0)
  FaceMakerClass = Part::FaceMakerBullseye
  Placement = pos=(0,0,36.15) rot=(0,0,1;0rad)
  Solid = false
  Source = -> Face120
  Symmetric = false
FEATURE [Part::MultiFuse] Fusion099  label="plugHousing053"
  Placement = pos=(0,0,0) rot=(0,0,1;1.5708rad)
  Shapes = -> [Revolve127,Revolve131]
FEATURE [Part::MultiFuse] Fusion102  label="plugHousing056"
  Placement = pos=(0,19,0) rot=(0,0,1;3.14159rad)
  Shapes = -> [Fusion100,Fusion099]
FEATURE [Part::Revolution] Revolve132  label="plugHousing059"
  Angle = 360
  Axis = (0,1,0)
  Base = (0,0,0)
  FaceMakerClass = Part::FaceMakerBullseye
  Placement = pos=(0,0,36.15) rot=(0,0,1;0rad)
  Solid = false
  Source = -> Face126
  Symmetric = false
FEATURE [Part::Revolution] Revolve133  label="plugHousing060"
  Angle = 360
  Axis = (0,1,0)
  Base = (0,0,0)
  FaceMakerClass = Part::FaceMakerBullseye
  Placement = pos=(0,0,36.15) rot=(0,0,1;0rad)
  Solid = false
  Source = -> Face122
  Symmetric = false
FEATURE [Part::MultiFuse] Fusion097  label="plugHousing051"
  Placement = pos=(0,0,0) rot=(0,0,1;1.5708rad)
  Shapes = -> [Revolve133,Revolve132]
FEATURE [Part::Revolution] Revolve134  label="plugHousing061"
  Angle = 360
  Axis = (0,1,0)
  Base = (0,0,0)
  FaceMakerClass = Part::FaceMakerBullseye
  Placement = pos=(0,0,36.15) rot=(0,0,1;0rad)
  Solid = false
  Source = -> Face124
  Symmetric = false
FEATURE [Part::MultiFuse] Fusion101  label="plugHousing055"
  Placement = pos=(0,0,0) rot=(0,0,1;1.5708rad)
  Shapes = -> [Revolve129,Revolve134]
FEATURE [Part::MultiFuse] Fusion098  label="plugHousing052"
  Placement = pos=(0,19,0) rot=(0,0,1;3.14159rad)
  Shapes = -> [Fusion097,Fusion101]
FEATURE [Part::MultiFuse] Fusion103  label="plugHousing057"
  Placement = pos=(122.621,0,-0.15) rot=(0,0,1;0rad)
  Shapes = -> [Fusion102,Fusion098]
FEATURE [Part::Box] Box028  label="Cube015"
  AttacherType = Attacher::AttachEngine3D
  Height = 28
  Length = 3
  Placement = pos=(110.7,19,22) rot=(0,0,1;0rad)
  Width = 15.7
FEATURE [Part::Cylinder] Cylinder044
  Angle = 360
  AttacherType = Attacher::AttachEngine3D
  Height = 20
  Placement = pos=(0,0,36.15) rot=(0,0,1;0rad)
  Radius = 10.3
FEATURE [Part::Cylinder] Cylinder045
  Angle = 360
  AttacherType = Attacher::AttachEngine3D
  Height = 10
  Placement = pos=(0,0,36.15) rot=(0,0,1;0rad)
  Radius = 4
FEATURE [Part::MultiFuse] Fusion104  label="removeToCreteHoleForPlugHousing040"
  Placement = pos=(70,19,36) rot=(0,1,0;1.5708rad)
  Shapes = -> [Cylinder044,Cylinder045]
FEATURE [Part::Cut] Cut046  label="plugHousingTab003"
  Base = -> Box028
  Tool = -> Fusion104
FEATURE [Part::MultiFuse] Fusion105  label="plugHousing062"
  Shapes = -> [Fusion103,Cut046]
FEATURE [Part::Fillet] Fillet042
  Base = -> Fusion105
  Edges = 1 edges r=2: [Edge25]
FEATURE [Part::Fillet] Fillet043  label="plugHousing063"
  Base = -> Fillet042
  Edges = 1 edges r=2: [Edge8]
  Placement = pos=(7,0,0) rot=(0,0,1;0rad)
FEATURE [Part::Feature] Face127
  shape: bbox 10 x 16.5 x 2e-07 mm, 1 faces, 0 solids (baked)
FEATURE [Part::Feature] Face128
  shape: bbox 10 x 16.5 x 2e-07 mm, 1 faces, 0 solids (baked)
FEATURE [Part::Revolution] Revolve137  label="plugHousing070"
  Angle = 360
  Axis = (0,1,0)
  Base = (0,0,0)
  FaceMakerClass = Part::FaceMakerBullseye
  Placement = pos=(0,0,36.15) rot=(0,0,1;0rad)
  Solid = false
  Source = -> Face127
  Symmetric = false
FEATURE [Part::Revolution] Revolve140  label="plugHousing073"
  Angle = 360
  Axis = (0,1,0)
  Base = (0,0,0)
  FaceMakerClass = Part::FaceMakerBullseye
  Placement = pos=(0,0,36.15) rot=(0,0,1;0rad)
  Solid = false
  Source = -> Face128
  Symmetric = false
FEATURE [Part::Feature] Face129
  shape: bbox 10 x 16.5 x 2e-07 mm, 1 faces, 0 solids (baked)
FEATURE [Part::Revolution] Revolve138  label="plugHousing071"
  Angle = 360
  Axis = (0,1,0)
  Base = (0,0,0)
  FaceMakerClass = Part::FaceMakerBullseye
  Placement = pos=(0,0,36.15) rot=(0,0,1;0rad)
  Solid = false
  Source = -> Face129
  Symmetric = false
FEATURE [Part::Feature] Face130
  shape: bbox 10 x 16.5 x 2e-07 mm, 1 faces, 0 solids (baked)
FEATURE [Part::Revolution] Revolve139  label="plugHousing072"
  Angle = 360
  Axis = (0,1,0)
  Base = (0,0,0)
  FaceMakerClass = Part::FaceMakerBullseye
  Placement = pos=(0,0,36.15) rot=(0,0,1;0rad)
  Solid = false
  Source = -> Face130
  Symmetric = false
FEATURE [Part::Feature] Face131
  shape: bbox 10 x 16.5 x 2e-07 mm, 1 faces, 0 solids (baked)
FEATURE [Part::Revolution] Revolve135  label="plugHousing068"
  Angle = 360
  Axis = (0,1,0)
  Base = (0,0,0)
  FaceMakerClass = Part::FaceMakerBullseye
  Placement = pos=(0,0,36.15) rot=(0,0,1;0rad)
  Solid = false
  Source = -> Face131
  Symmetric = false
FEATURE [Part::MultiFuse] Fusion112  label="plugHousing078"
  Placement = pos=(0,0,0) rot=(0,0,1;1.5708rad)
  Shapes = -> [Revolve135,Revolve139]
FEATURE [Part::Feature] Face132
  shape: bbox 10 x 16.5 x 2e-07 mm, 1 faces, 0 solids (baked)
FEATURE [Part::Revolution] Revolve141  label="plugHousing074"
  Angle = 360
  Axis = (0,1,0)
  Base = (0,0,0)
  FaceMakerClass = Part::FaceMakerBullseye
  Placement = pos=(0,0,36.15) rot=(0,0,1;0rad)
  Solid = false
  Source = -> Face132
  Symmetric = false
FEATURE [Part::MultiFuse] Fusion110  label="plugHousing076"
  Placement = pos=(0,0,0) rot=(0,0,1;1.5708rad)
  Shapes = -> [Revolve141,Revolve140]
FEATURE [Part::Feature] Face133
  shape: bbox 10 x 16.5 x 2e-07 mm, 1 faces, 0 solids (baked)
FEATURE [Part::Revolution] Revolve136  label="plugHousing069"
  Angle = 360
  Axis = (0,1,0)
  Base = (0,0,0)
  FaceMakerClass = Part::FaceMakerBullseye
  Placement = pos=(0,0,36.15) rot=(0,0,1;0rad)
  Solid = false
  Source = -> Face133
  Symmetric = false
FEATURE [Part::MultiFuse] Fusion106  label="plugHousing064"
  Placement = pos=(0,0,0) rot=(0,0,1;1.5708rad)
  Shapes = -> [Revolve138,Revolve136]
FEATURE [Part::MultiFuse] Fusion108  label="plugHousing066"
  Placement = pos=(0,19,0) rot=(0,0,1;3.14159rad)
  Shapes = -> [Fusion106,Fusion112]
FEATURE [Part::Feature] Face134
  shape: bbox 10 x 16.5 x 2e-07 mm, 1 faces, 0 solids (baked)
FEATURE [Part::Revolution] Revolve142  label="plugHousing075"
  Angle = 360
  Axis = (0,1,0)
  Base = (0,0,0)
  FaceMakerClass = Part::FaceMakerBullseye
  Placement = pos=(0,0,36.15) rot=(0,0,1;0rad)
  Solid = false
  Source = -> Face134
  Symmetric = false
FEATURE [Part::MultiFuse] Fusion107  label="plugHousing065"
  Placement = pos=(0,0,0) rot=(0,0,1;1.5708rad)
  Shapes = -> [Revolve137,Revolve142]
FEATURE [Part::MultiFuse] Fusion111  label="plugHousing077"
  Placement = pos=(0,19,0) rot=(0,0,1;3.14159rad)
  Shapes = -> [Fusion110,Fusion107]
FEATURE [Part::MultiFuse] Fusion109  label="plugHousing067"
  Placement = pos=(131.236,0,-0.15) rot=(0,0,1;0rad)
  Shapes = -> [Fusion108,Fusion111]
FEATURE [Part::MultiFuse] Fusion113  label="plugHousing079"
  Shapes = -> [Fillet043,Fusion109]
FEATURE [Part::Feature] Face135
  shape: bbox 3.5 x 17.8 x 2e-07 mm, 1 faces, 0 solids (baked)
FEATURE [Part::Revolution] Revolve143  label="removeToCreateScrewAndThreadedInsertHole049"
  Angle = 360
  Axis = (0,1,0)
  Base = (0,0,0)
  FaceMakerClass = Part::FaceMakerBullseye
  Placement = pos=(12.5,0,10) rot=(0,0,1;0rad)
  Solid = false
  Source = -> Face135
  Symmetric = false
FEATURE [Part::Feature] Face136
  shape: bbox 3.5 x 17.8 x 2e-07 mm, 1 faces, 0 solids (baked)
FEATURE [Part::Revolution] Revolve144  label="removeToCreateScrewAndThreadedInsertHole050"
  Angle = 360
  Axis = (0,1,0)
  Base = (0,0,0)
  FaceMakerClass = Part::FaceMakerBullseye
  Placement = pos=(12.5,0,62) rot=(0,0,1;0rad)
  Solid = false
  Source = -> Face136
  Symmetric = false
FEATURE [Part::Feature] Face137
  shape: bbox 3.5 x 17.8 x 2e-07 mm, 1 faces, 0 solids (baked)
FEATURE [Part::Revolution] Revolve145  label="removeToCreateScrewAndThreadedInsertHole051"
  Angle = 360
  Axis = (0,1,0)
  Base = (0,0,0)
  FaceMakerClass = Part::FaceMakerBullseye
  Placement = pos=(89.5,0,68.5) rot=(0,0,1;0rad)
  Solid = false
  Source = -> Face137
  Symmetric = false
FEATURE [Part::Feature] Face138
  shape: bbox 3.5 x 17.8 x 2e-07 mm, 1 faces, 0 solids (baked)
FEATURE [Part::Revolution] Revolve146  label="removeToCreateScrewAndThreadedInsertHole052"
  Angle = 360
  Axis = (0,1,0)
  Base = (0,0,0)
  FaceMakerClass = Part::FaceMakerBullseye
  Placement = pos=(89.5,0,3.5) rot=(0,0,1;0rad)
  Solid = false
  Source = -> Face138
  Symmetric = false
FEATURE [Part::Feature] Face139
  shape: bbox 3.5 x 17.8 x 2e-07 mm, 1 faces, 0 solids (baked)
FEATURE [Part::Revolution] Revolve147  label="removeToCreateScrewAndThreadedInsertHole053"
  Angle = 360
  Axis = (0,1,0)
  Base = (0,0,0)
  FaceMakerClass = Part::FaceMakerBullseye
  Placement = pos=(109.5,4.7,3.5) rot=(0,0,1;0rad)
  Solid = false
  Source = -> Face139
  Symmetric = false
FEATURE [Part::Feature] Face140
  shape: bbox 3.5 x 17.8 x 2e-07 mm, 1 faces, 0 solids (baked)
FEATURE [Part::Revolution] Revolve148  label="removeToCreateScrewAndThreadedInsertHole054"
  Angle = 360
  Axis = (0,1,0)
  Base = (0,0,0)
  FaceMakerClass = Part::FaceMakerBullseye
  Placement = pos=(109.5,4.7,68.5) rot=(0,0,1;0rad)
  Solid = false
  Source = -> Face140
  Symmetric = false
FEATURE [Part::MultiFuse] Fusion114  label="removeToCreateScrewAndThreadedInsertHole055"
  Shapes = -> [Revolve148,Revolve147,Revolve146,Revolve145,Revolve144,Revolve143]
FEATURE [Part::Cut] Cut047  label="casePillars004"
  Base = -> Cut037
  Tool = -> Fusion114
FEATURE [Part::Feature] Face141
  shape: bbox 3.5 x 17.8 x 2e-07 mm, 1 faces, 0 solids (baked)
FEATURE [Part::Feature] Face142
  shape: bbox 3.5 x 17.8 x 2e-07 mm, 1 faces, 0 solids (baked)
FEATURE [Part::Feature] Face143
  shape: bbox 3.5 x 17.8 x 2e-07 mm, 1 faces, 0 solids (baked)
FEATURE [Part::Revolution] Revolve149  label="removeToCreateScrewAndThreadedInsertHole057"
  Angle = 360
  Axis = (0,1,0)
  Base = (0,0,0)
  FaceMakerClass = Part::FaceMakerBullseye
  Placement = pos=(12.5,0,10) rot=(0,0,1;0rad)
  Solid = false
  Source = -> Face141
  Symmetric = false
FEATURE [Part::Feature] Face144
  shape: bbox 3.5 x 17.8 x 2e-07 mm, 1 faces, 0 solids (baked)
FEATURE [Part::Feature] Face145
  shape: bbox 3.5 x 17.8 x 2e-07 mm, 1 faces, 0 solids (baked)
FEATURE [Part::Feature] Face146
  shape: bbox 3.5 x 17.8 x 2e-07 mm, 1 faces, 0 solids (baked)
FEATURE [Part::Revolution] Revolve150  label="removeToCreateScrewAndThreadedInsertHole058"
  Angle = 360
  Axis = (0,1,0)
  Base = (0,0,0)
  FaceMakerClass = Part::FaceMakerBullseye
  Placement = pos=(12.5,0,62) rot=(0,0,1;0rad)
  Solid = false
  Source = -> Face146
  Symmetric = false
FEATURE [Part::Revolution] Revolve151  label="removeToCreateScrewAndThreadedInsertHole059"
  Angle = 360
  Axis = (0,1,0)
  Base = (0,0,0)
  FaceMakerClass = Part::FaceMakerBullseye
  Placement = pos=(89.5,0,68.5) rot=(0,0,1;0rad)
  Solid = false
  Source = -> Face143
  Symmetric = false
FEATURE [Part::Revolution] Revolve152  label="removeToCreateScrewAndThreadedInsertHole060"
  Angle = 360
  Axis = (0,1,0)
  Base = (0,0,0)
  FaceMakerClass = Part::FaceMakerBullseye
  Placement = pos=(89.5,0,3.5) rot=(0,0,1;0rad)
  Solid = false
  Source = -> Face142
  Symmetric = false
FEATURE [Part::Revolution] Revolve153  label="removeToCreateScrewAndThreadedInsertHole061"
  Angle = 360
  Axis = (0,1,0)
  Base = (0,0,0)
  FaceMakerClass = Part::FaceMakerBullseye
  Placement = pos=(109.5,4.7,3.5) rot=(0,0,1;0rad)
  Solid = false
  Source = -> Face145
  Symmetric = false
FEATURE [Part::Revolution] Revolve154  label="removeToCreateScrewAndThreadedInsertHole062"
  Angle = 360
  Axis = (0,1,0)
  Base = (0,0,0)
  FaceMakerClass = Part::FaceMakerBullseye
  Placement = pos=(109.5,4.7,68.5) rot=(0,0,1;0rad)
  Solid = false
  Source = -> Face144
  Symmetric = false
FEATURE [Part::MultiFuse] Fusion115  label="removeToCreateScrewAndThreadedInsertHole056"
  Shapes = -> [Revolve154,Revolve153,Revolve152,Revolve151,Revolve150,Revolve149]
FEATURE [Part::Feature] Face147
  shape: bbox 9.8 x 26.5 x 2e-07 mm, 1 faces, 0 solids (baked)
FEATURE [Part::Revolution] Revolve155
  Angle = 360
  Axis = (0,1,0)
  Base = (0,0,0)
  FaceMakerClass = Part::FaceMakerBullseye
  Placement = pos=(0,0,0) rot=(0,0,1;1.5708rad)
  Solid = false
  Source = -> Face147
  Symmetric = false
FEATURE [Part::Feature] Face148
  shape: bbox 9.8 x 26.5 x 2e-07 mm, 1 faces, 0 solids (baked)
FEATURE [Part::Revolution] Revolve156
  Angle = 360
  Axis = (0,1,0)
  Base = (0,0,0)
  FaceMakerClass = Part::FaceMakerBullseye
  Placement = pos=(0,0,0) rot=(0,0,1;1.5708rad)
  Solid = false
  Source = -> Face148
  Symmetric = false
FEATURE [Part::MultiFuse] Fusion116
  Placement = pos=(-18,19,36) rot=(0,0,1;0rad)
  Shapes = -> [Revolve156,Revolve155]
FEATURE [Part::Box] Box029  label="Cube016"
  AttacherType = Attacher::AttachEngine3D
  Height = 28
  Length = 3
  Placement = pos=(110.7,19,22) rot=(0,0,1;0rad)
  Width = 15.7
FEATURE [Part::Cylinder] Cylinder046
  Angle = 360
  AttacherType = Attacher::AttachEngine3D
  Height = 10
  Placement = pos=(0,0,36.15) rot=(0,0,1;0rad)
  Radius = 4
FEATURE [Part::Cylinder] Cylinder047
  Angle = 360
  AttacherType = Attacher::AttachEngine3D
  Height = 20
  Placement = pos=(0,0,36.15) rot=(0,0,1;0rad)
  Radius = 10.3
FEATURE [Part::MultiFuse] Fusion117  label="removeToCreteHoleForPlugHousing041"
  Placement = pos=(70,19,36) rot=(0,1,0;1.5708rad)
  Shapes = -> [Cylinder047,Cylinder046]
FEATURE [Part::Cut] Cut049  label="plugHousingTab004"
  Base = -> Box029
  Placement = pos=(-107.4,-14,0) rot=(0,0,1;0rad)
  Tool = -> Fusion117
FEATURE [Part::Box] Box030  label="Cube017"
  AttacherType = Attacher::AttachEngine3D
  Height = 28
  Length = 3
  Placement = pos=(110.7,19,22) rot=(0,0,1;0rad)
  Width = 15.7
FEATURE [Part::Cylinder] Cylinder048
  Angle = 360
  AttacherType = Attacher::AttachEngine3D
  Height = 10
  Placement = pos=(0,0,36.15) rot=(0,0,1;0rad)
  Radius = 4
FEATURE [Part::Cylinder] Cylinder049
  Angle = 360
  AttacherType = Attacher::AttachEngine3D
  Height = 20
  Placement = pos=(0,0,36.15) rot=(0,0,1;0rad)
  Radius = 10.3
FEATURE [Part::MultiFuse] Fusion118  label="removeToCreteHoleForPlugHousing042"
  Placement = pos=(70,19,36) rot=(0,1,0;1.5708rad)
  Shapes = -> [Cylinder049,Cylinder048]
FEATURE [Part::Cut] Cut050  label="plugHousingTab005"
  Base = -> Box030
  Placement = pos=(-107.4,-14,0) rot=(0,0,1;0rad)
  Tool = -> Fusion118
FEATURE [Part::MultiFuse] Fusion119
  Placement = pos=(9.6,23,0) rot=(0,0,1;3.14159rad)
  Shapes = -> [Cut049,Cut050]
FEATURE [Part::Box] Box031  label="Cube018"
  AttacherType = Attacher::AttachEngine3D
  Height = 10
  Length = 3
  Placement = pos=(3.3,4,12) rot=(0,0,1;0rad)
  Width = 10
FEATURE [Part::Fillet] Fillet044
  Base = -> Box031
  Edges = 1 edges r=2: [Edge11]
FEATURE [Part::Box] Box032  label="Cube019"
  AttacherType = Attacher::AttachEngine3D
  Height = 10
  Length = 3
  Placement = pos=(3.3,4,50) rot=(0,0,1;0rad)
  Width = 10
FEATURE [Part::Fillet] Fillet045
  Base = -> Box032
  Edges = 1 edges r=2: [Edge12]
FEATURE [Part::Box] Box033  label="Cube020"
  AttacherType = Attacher::AttachEngine3D
  Height = 28
  Length = 4
  Placement = pos=(5,0,22) rot=(0,0,1;0rad)
  Width = 10
FEATURE [Part::Fillet] Fillet046
  Base = -> Box033
  Edges = 1 edges r=1: [Edge7]
FEATURE [Part::Fillet] Fillet047
  Base = -> Fillet046
  Edges = 1 edges r=2: [Edge5]
FEATURE [Part::Fillet] Fillet048
  Base = -> Fillet047
  Edges = 1 edges r=2: [Edge2]
FEATURE [Part::Cylinder] Cylinder050
  Angle = 360
  AttacherType = Attacher::AttachEngine3D
  Height = 20
  Placement = pos=(0,0,36.15) rot=(0,0,1;0rad)
  Radius = 8.2
FEATURE [Part::Cylinder] Cylinder051
  Angle = 360
  AttacherType = Attacher::AttachEngine3D
  Height = 10
  Placement = pos=(0,0,36.15) rot=(0,0,1;0rad)
  Radius = 4
FEATURE [Part::MultiFuse] Fusion120  label="removeToCreteHoleForPlugHousing043"
  Placement = pos=(-42,19,36) rot=(0,1,0;1.5708rad)
  Shapes = -> [Cylinder050,Cylinder051]
FEATURE [Sketcher::SketchObject] Sketch067  label="topSketch018"
  FullyConstrained = true
  sketch-geometry (4):
    g0: LineSegment StartX=16.8446 StartY=31.512 StartZ=0 EndX=16.3251 EndY=34.4666 EndZ=0
    g1: ArcOfCircle CenterX=19 CenterY=19.2524 CenterZ=0 NormalX=0 NormalY=0 NormalZ=1 AngleXU=0 Radius=15.4476 StartAngle=1.74483 EndAngle=2.72717
    g2: ArcOfCircle CenterX=19 CenterY=19.2524 CenterZ=0 NormalX=0 NormalY=0 NormalZ=1 AngleXU=0 Radius=12.4476 StartAngle=1.74483 EndAngle=2.73189
    g3: LineSegment StartX=4.86004 StartY=25.4725 StartZ=0 EndX=7.58253 EndY=24.2107 EndZ=0
  constraints (7):
    c: Block(g0)
    c: Coincident(g1,g0)
    c: Coincident(g2,g0)
    c: Coincident(g3,g1)
    c: Coincident(g3,g2)
    c: Block(g1)
    c: Block(g2)
FEATURE [Part::Extrusion] Extrude058
  Base = -> Sketch067
  Dir = (0,0,1)
  DirMode = 2
  FaceMakerClass = Part::FaceMakerBullseye
  LengthFwd = 10
  LengthRev = 0
  Placement = pos=(0,0,31) rot=(0,0,1;0rad)
  Solid = true
  Symmetric = false
FEATURE [Part::Cut] Cut051
  Base = -> Extrude058
  Tool = -> Fusion120
FEATURE [Part::Fillet] Fillet049
  Base = -> Cut051
  Edges = 1 edges r=2: [Edge1]
FEATURE [Part::Fillet] Fillet050
  Base = -> Fillet049
  Edges = 1 edges r=2.5: [Edge1]
FEATURE [Part::Fillet] Fillet051
  Base = -> Fillet050
  Edges = 1 edges r=2.5: [Edge2]
FEATURE [Part::MultiFuse] Fusion121  label="wireHolder003"
  Shapes = -> [Fusion116,Fillet051]
FEATURE [Part::MultiFuse] Fusion122
  Shapes = -> [Fillet045,Fusion121]
FEATURE [Part::MultiFuse] Fusion123  label="wireHolder004"
  Shapes = -> [Fusion122,Fillet048]
FEATURE [Part::MultiFuse] Fusion124  label="wireHolder005"
  Shapes = -> [Fillet044,Fusion119,Fusion123]
FEATURE [Sketcher::SketchObject] Sketch068  label="topSketch019"
  FullyConstrained = true
  sketch-geometry (6):
    g0: LineSegment StartX=19 StartY=38 StartZ=0 EndX=117 EndY=38 EndZ=0
    g1: ArcOfCircle CenterX=19 CenterY=19 CenterZ=0 NormalX=0 NormalY=0 NormalZ=1 AngleXU=0 Radius=19 StartAngle=1.5708 EndAngle=3.14159
    g2: LineSegment StartX=117 StartY=38 StartZ=0 EndX=117 EndY=19 EndZ=0
    g3: LineSegment StartX=98 StartY=1.0161e-12 StartZ=0 EndX=5.22862e-06 EndY=1.0161e-12 EndZ=0
    g4: LineSegment StartX=5.22862e-06 StartY=19 StartZ=0 EndX=5.22862e-06 EndY=1.0161e-12 EndZ=0
    g5: ArcOfCircle CenterX=98 CenterY=19 CenterZ=0 NormalX=0 NormalY=0 NormalZ=1 AngleXU=0 Radius=19 StartAngle=4.71239 EndAngle=6.28319
  constraints (16):
    c: Horizontal(g0)
    c: Distance(g0) = 98
    c: Coincident(g1,g0)
    c: Block(g1)
    c: Coincident(g2,g0)
    c: Vertical(g2)
    c: Distance(g2) = 19
    c: Horizontal(g3)
    c: Coincident(g4,g1)
    c: Vertical(g4)
    c: Coincident(g3,g4)
    c: Block(g3)
    c: Coincident(g5,g2)
    c: Coincident(g5,g3)
    c: Block(g0)
    c: Block(g5)
FEATURE [Part::Extrusion] Extrude059  label="sideA002"
  Base = -> Sketch068
  Dir = (0,0,1)
  DirMode = 2
  FaceMakerClass = Part::FaceMakerBullseye
  LengthFwd = 3
  LengthRev = 0
  Placement = pos=(0,0,-2.7) rot=(0,0,1;0rad)
  Solid = true
  Symmetric = false
FEATURE [Sketcher::SketchObject] Sketch069  label="topSketch020"
  FullyConstrained = true
  sketch-geometry (6):
    g0: LineSegment StartX=19 StartY=38 StartZ=0 EndX=117 EndY=38 EndZ=0
    g1: ArcOfCircle CenterX=19 CenterY=19 CenterZ=0 NormalX=0 NormalY=0 NormalZ=1 AngleXU=0 Radius=19 StartAngle=1.5708 EndAngle=3.14159
    g2: LineSegment StartX=117 StartY=38 StartZ=0 EndX=117 EndY=19 EndZ=0
    g3: LineSegment StartX=98 StartY=1.0161e-12 StartZ=0 EndX=5.22862e-06 EndY=1.0161e-12 EndZ=0
    g4: LineSegment StartX=5.22862e-06 StartY=19 StartZ=0 EndX=5.22862e-06 EndY=1.0161e-12 EndZ=0
    g5: ArcOfCircle CenterX=98 CenterY=19 CenterZ=0 NormalX=0 NormalY=0 NormalZ=1 AngleXU=0 Radius=19 StartAngle=4.71239 EndAngle=6.28319
  constraints (16):
    c: Horizontal(g0)
    c: Distance(g0) = 98
    c: Coincident(g1,g0)
    c: Block(g1)
    c: Coincident(g2,g0)
    c: Vertical(g2)
    c: Distance(g2) = 19
    c: Horizontal(g3)
    c: Coincident(g4,g1)
    c: Vertical(g4)
    c: Coincident(g3,g4)
    c: Block(g3)
    c: Coincident(g5,g2)
    c: Coincident(g5,g3)
    c: Block(g0)
    c: Block(g5)
FEATURE [Part::Extrusion] Extrude060  label="sideB002"
  Base = -> Sketch069
  Dir = (0,0,1)
  DirMode = 2
  FaceMakerClass = Part::FaceMakerBullseye
  LengthFwd = 3
  LengthRev = 0
  Placement = pos=(0,0,71.7) rot=(0,0,1;0rad)
  Solid = true
  Symmetric = false
FEATURE [Part::MultiFuse] Fusion127  label="removeFromBottom001"
  Placement = pos=(2,0,0) rot=(0,0,1;0rad)
  Shapes = -> [Extrude059,Extrude060]
FEATURE [Part::Cylinder] Cylinder052
  Angle = 360
  AttacherType = Attacher::AttachEngine3D
  Height = 20
  Placement = pos=(0,0,36.15) rot=(0,0,1;0rad)
  Radius = 14
FEATURE [Part::Cylinder] Cylinder053
  Angle = 360
  AttacherType = Attacher::AttachEngine3D
  Height = 10
  Placement = pos=(0,0,36.15) rot=(0,0,1;0rad)
  Radius = 4
FEATURE [Part::MultiFuse] Fusion128  label="removeToCreteHoleForPlugHousing044"
  Placement = pos=(70,19,36) rot=(0,1,0;1.5708rad)
  Shapes = -> [Cylinder052,Cylinder053]
FEATURE [Part::Cut] Cut052  label="bottom011"
  Base = -> Extrude043
  Tool = -> Fusion128
FEATURE [Part::Cut] Cut054  label="bottom012"
  Base = -> Cut052
  Tool = -> Fusion115
FEATURE [Sketcher::SketchObject] Sketch070
  FullyConstrained = true
  Placement = pos=(117,19,0) rot=(0.57735,0.57735,0.57735;2.0944rad)
  sketch-geometry (48):
    g0: LineSegment StartX=-49.19 StartY=69.25 StartZ=0 EndX=-49.19 EndY=66.25 EndZ=0
    g1: LineSegment StartX=-49.19 StartY=63.5 StartZ=0 EndX=-49.19 EndY=60.5 EndZ=0
    g2: LineSegment StartX=-49.19 StartY=57.75 StartZ=0 EndX=-49.19 EndY=54.75 EndZ=0
    g3: LineSegment StartX=-49.19 StartY=52 StartZ=0 EndX=-49.19 EndY=49 EndZ=0
    g4: LineSegment StartX=-49.19 StartY=46.25 StartZ=0 EndX=-49.19 EndY=43.25 EndZ=0
    g5: LineSegment StartX=-49.19 StartY=40.5 StartZ=0 EndX=-49.19 EndY=37.5 EndZ=0
    g6: LineSegment StartX=-49.19 StartY=34.5 StartZ=0 EndX=-49.19 EndY=31.5 EndZ=0
    g7: LineSegment StartX=-49.19 StartY=28.75 StartZ=0 EndX=-49.19 EndY=25.75 EndZ=0
    g8: LineSegment StartX=-49.19 StartY=23 StartZ=0 EndX=-49.19 EndY=20 EndZ=0
    g9: LineSegment StartX=-49.19 StartY=17.25 StartZ=0 EndX=-49.19 EndY=14.25 EndZ=0
    g10: LineSegment StartX=-49.19 StartY=11.5 StartZ=0 EndX=-49.19 EndY=8.5 EndZ=0
    g11: LineSegment StartX=-49.19 StartY=5.75 StartZ=0 EndX=-49.19 EndY=2.75 EndZ=0
    g12: ArcOfCircle CenterX=-1.5 CenterY=67.75 CenterZ=0 NormalX=0 NormalY=0 NormalZ=1 AngleXU=0 Radius=1.5 StartAngle=4.71239 EndAngle=7.85398
    g13: ArcOfCircle CenterX=-1.5 CenterY=62 CenterZ=0 NormalX=0 NormalY=0 NormalZ=1 AngleXU=0 Radius=1.5 StartAngle=4.71239 EndAngle=7.85398
    g14: ArcOfCircle CenterX=-1.5 CenterY=56.25 CenterZ=0 NormalX=0 NormalY=0 NormalZ=1 AngleXU=0 Radius=1.5 StartAngle=4.71239 EndAngle=7.85398
    g15: ArcOfCircle CenterX=-11.49 CenterY=50.5 CenterZ=0 NormalX=0 NormalY=0 NormalZ=1 AngleXU=0 Radius=1.5 StartAngle=4.71239 EndAngle=7.85398
    g16: ArcOfCircle CenterX=-16.28 CenterY=44.75 CenterZ=0 NormalX=0 NormalY=0 NormalZ=1 AngleXU=0 Radius=1.5 StartAngle=4.71239 EndAngle=7.85398
    g17: ArcOfCircle CenterX=-18.2337 CenterY=39 CenterZ=0 NormalX=0 NormalY=0 NormalZ=1 AngleXU=0 Radius=1.5 StartAngle=4.71485 EndAngle=7.85398
    g18: ArcOfCircle CenterX=-16.2837 CenterY=27.25 CenterZ=0 NormalX=0 NormalY=0 NormalZ=1 AngleXU=0 Radius=1.5 StartAngle=4.71485 EndAngle=7.85398
    g19: ArcOfCircle CenterX=-18.2337 CenterY=33 CenterZ=0 NormalX=0 NormalY=0 NormalZ=1 AngleXU=0 Radius=1.5 StartAngle=4.71485 EndAngle=7.85398
    g20: ArcOfCircle CenterX=-11.49 CenterY=21.5 CenterZ=0 NormalX=0 NormalY=0 NormalZ=1 AngleXU=0 Radius=1.5 StartAngle=4.71239 EndAngle=7.85398
    g21: ArcOfCircle CenterX=-1.5 CenterY=4.25 CenterZ=0 NormalX=0 NormalY=0 NormalZ=1 AngleXU=0 Radius=1.5 StartAngle=4.71239 EndAngle=7.85398
    g22: ArcOfCircle CenterX=-1.5 CenterY=10 CenterZ=0 NormalX=0 NormalY=0 NormalZ=1 AngleXU=0 Radius=1.5 StartAngle=4.71239 EndAngle=7.85398
    g23: ArcOfCircle CenterX=-1.5 CenterY=15.75 CenterZ=0 NormalX=0 NormalY=0 NormalZ=1 AngleXU=0 Radius=1.5 StartAngle=4.71239 EndAngle=7.85398
    g24: LineSegment StartX=-49.19 StartY=69.25 StartZ=0 EndX=-1.5 EndY=69.25 EndZ=0
    g25: LineSegment StartX=-49.19 StartY=66.25 StartZ=0 EndX=-1.5 EndY=66.25 EndZ=0
    g26: LineSegment StartX=-49.19 StartY=63.5 StartZ=0 EndX=-1.5 EndY=63.5 EndZ=0
    g27: LineSegment StartX=-49.19 StartY=60.5 StartZ=0 EndX=-1.5 EndY=60.5 EndZ=0
    g28: LineSegment StartX=-49.19 StartY=57.75 StartZ=0 EndX=-1.5 EndY=57.75 EndZ=0
    g29: LineSegment StartX=-49.19 StartY=54.75 StartZ=0 EndX=-1.5 EndY=54.75 EndZ=0
    g30: LineSegment StartX=-49.19 StartY=52 StartZ=0 EndX=-11.49 EndY=52 EndZ=0
    g31: LineSegment StartX=-49.19 StartY=49 StartZ=0 EndX=-11.49 EndY=49 EndZ=0
    g32: LineSegment StartX=-49.19 StartY=46.25 StartZ=0 EndX=-16.28 EndY=46.25 EndZ=0
    g33: LineSegment StartX=-49.19 StartY=43.25 StartZ=0 EndX=-16.28 EndY=43.25 EndZ=0
    g34: LineSegment StartX=-49.19 StartY=40.5 StartZ=0 EndX=-18.2337 EndY=40.5 EndZ=0
    g35: LineSegment StartX=-49.19 StartY=37.5 StartZ=0 EndX=-18.23 EndY=37.5 EndZ=0
    g36: LineSegment StartX=-49.19 StartY=34.5 StartZ=0 EndX=-18.2337 EndY=34.5 EndZ=0
    g37: LineSegment StartX=-49.19 StartY=31.5 StartZ=0 EndX=-18.23 EndY=31.5 EndZ=0
    g38: LineSegment StartX=-49.19 StartY=28.75 StartZ=0 EndX=-16.2837 EndY=28.75 EndZ=0
    g39: LineSegment StartX=-49.19 StartY=25.75 StartZ=0 EndX=-16.28 EndY=25.75 EndZ=0
    g40: LineSegment StartX=-49.19 StartY=23 StartZ=0 EndX=-11.49 EndY=23 EndZ=0
    g41: LineSegment StartX=-49.19 StartY=20 StartZ=0 EndX=-11.49 EndY=20 EndZ=0
    g42: LineSegment StartX=-49.19 StartY=17.25 StartZ=0 EndX=-1.5 EndY=17.25 EndZ=0
    g43: LineSegment StartX=-49.19 StartY=14.25 StartZ=0 EndX=-1.5 EndY=14.25 EndZ=0
    g44: LineSegment StartX=-49.19 StartY=11.5 StartZ=0 EndX=-1.5 EndY=11.5 EndZ=0
    g45: LineSegment StartX=-49.19 StartY=8.5 StartZ=0 EndX=-1.5 EndY=8.5 EndZ=0
    g46: LineSegment StartX=-49.19 StartY=5.75 StartZ=0 EndX=-1.5 EndY=5.75 EndZ=0
    g47: LineSegment StartX=-49.19 StartY=2.75 StartZ=0 EndX=-1.5 EndY=2.75 EndZ=0
  constraints (120):
    c: Vertical(g0)
    c: Distance(g0) = 3
    c: Block(g0)
    c: Vertical(g1)
    c: Distance(g1) = 3
    c: Vertical(g2)
    c: Equal(g0,g2) = 3
    c: Block(g2)
    c: Vertical(g3)
    c: Equal(g1,g3) = 3
    c: Vertical(g4)
    c: Equal(g0,g4) = 3
    c: Block(g4)
    c: Vertical(g5)
    c: Equal(g1,g5) = 3
    c: Vertical(g6)
    c: Equal(g0,g6) = 3
    c: Block(g6)
    c: Vertical(g7)
    c: Equal(g1,g7) = 3
    c: Vertical(g8)
    c: Equal(g0,g8) = 3
    c: Block(g8)
    c: Vertical(g9)
    c: Equal(g1,g9) = 3
    c: Vertical(g10)
    c: Equal(g0,g10) = 3
    c: Block(g10)
    c: Vertical(g11)
    c: Equal(g1,g11) = 3
    c: Block(g12)
    c: Block(g13)
    c: Block(g14)
    c: Block(g15)
    c: Block(g16)
    c: Block(g17)
    c: Block(g18)
    c: Block(g19)
    c: Block(g20)
    c: Block(g21)
    c: Block(g22)
    c: Block(g23)
    c: Block(g11)
    c: Block(g9)
    c: Block(g7)
    c: Block(g5)
    c: Block(g3)
    c: Block(g1)
    c: Coincident(g24,g0)
    c: Coincident(g24,g12)
    c: Horizontal(g24)
    c: Coincident(g25,g0)
    c: Coincident(g25,g12)
    c: Horizontal(g25)
    c: Coincident(g26,g1)
    c: Coincident(g26,g13)
    c: Horizontal(g26)
    c: Coincident(g27,g1)
    c: Coincident(g27,g13)
    c: Horizontal(g27)
    c: Coincident(g28,g2)
    c: Coincident(g28,g14)
    c: Horizontal(g28)
    c: Coincident(g29,g2)
    c: Coincident(g29,g14)
    c: Horizontal(g29)
    c: Coincident(g30,g3)
    c: Coincident(g30,g15)
    c: Horizontal(g30)
    c: Coincident(g31,g3)
    c: Coincident(g31,g15)
    c: Horizontal(g31)
    c: Coincident(g32,g4)
    c: Coincident(g32,g16)
    c: Horizontal(g32)
    c: Coincident(g33,g4)
    c: Coincident(g33,g16)
    c: Horizontal(g33)
    c: Coincident(g34,g5)
    c: Coincident(g34,g17)
    c: Horizontal(g34)
    c: Coincident(g35,g5)
    c: Coincident(g35,g17)
    c: Horizontal(g35)
    c: Coincident(g36,g6)
    c: Coincident(g36,g19)
    c: Horizontal(g36)
    c: Coincident(g37,g6)
    c: Coincident(g37,g19)
    c: Horizontal(g37)
    c: Coincident(g38,g7)
    c: Coincident(g38,g18)
    c: Horizontal(g38)
    c: Coincident(g39,g7)
    c: Coincident(g39,g18)
    c: Horizontal(g39)
    c: Coincident(g40,g8)
    c: Coincident(g40,g20)
    c: Horizontal(g40)
    c: Coincident(g41,g8)
    c: Coincident(g41,g20)
    c: Horizontal(g41)
    c: Coincident(g42,g9)
    c: Coincident(g42,g23)
    c: Horizontal(g42)
    c: Coincident(g43,g9)
    c: Coincident(g43,g23)
    c: Horizontal(g43)
    c: Coincident(g44,g10)
    c: Coincident(g44,g22)
    c: Horizontal(g44)
    c: Coincident(g45,g10)
    c: Coincident(g45,g22)
    c: Horizontal(g45)
    c: Coincident(g46,g11)
    c: Coincident(g46,g21)
    c: Horizontal(g46)
    c: Coincident(g47,g11)
    c: Coincident(g47,g21)
    c: Horizontal(g47)
FEATURE [Part::Extrusion] Extrude061
  Base = -> Sketch070
  Dir = (1,0,0)
  DirMode = 2
  FaceMakerClass = Part::FaceMakerBullseye
  LengthFwd = 23
  LengthRev = 0
  Placement = pos=(-19,0,0) rot=(0,0,1;0rad)
  Solid = true
  Symmetric = false
FEATURE [Part::Fillet] Fillet052  label="removeToCreateVentalationHoles002"
  Base = -> Extrude061
  Edges = <same value as first occurrence — deduplicated (x6 in doc)>
  Placement = pos=(7,0.02,0) rot=(0,0,1;0rad)
FEATURE [Part::MultiFuse] Fusion130  label="bottom013"
  Shapes = -> [Cut054,Cut034]
FEATURE [Part::Cut] Cut055
  Base = -> Fusion130
  Tool = -> Fillet052
FEATURE [Part::Cylinder] Cylinder054
  Angle = 360
  AttacherType = Attacher::AttachEngine3D
  Height = 20
  Placement = pos=(0,0,36.15) rot=(0,0,1;0rad)
  Radius = 4
FEATURE [Sketcher::SketchObject] Sketch071  label="bottomSketch002"
  FullyConstrained = true
  sketch-geometry (32):
    g0: LineSegment StartX=3.3 StartY=-6.03275e-07 StartZ=0 EndX=98 EndY=-6.03275e-07 EndZ=0
    g1: ArcOfCircle CenterX=98 CenterY=19 CenterZ=0 NormalX=0 NormalY=0 NormalZ=1 AngleXU=0 Radius=19 StartAngle=4.71239 EndAngle=5.71103
    g2: LineSegment StartX=6.3 StartY=8 StartZ=0 EndX=3.3 EndY=8 EndZ=0
    g3: LineSegment StartX=3.3 StartY=8 StartZ=0 EndX=3.3 EndY=-6.03275e-07 EndZ=0
    g4: ArcOfCircle CenterX=8.3 CenterY=5 CenterZ=0 NormalX=0 NormalY=0 NormalZ=1 AngleXU=0 Radius=2 StartAngle=3.14159 EndAngle=4.71239
    g5: LineSegment StartX=6.3 StartY=8 StartZ=0 EndX=6.3 EndY=5 EndZ=0
    g6: ArcOfCircle CenterX=98 CenterY=19 CenterZ=0 NormalX=0 NormalY=0 NormalZ=1 AngleXU=0 Radius=12.7 StartAngle=4.71239 EndAngle=6.28319
    g7: LineSegment StartX=94.7 StartY=3 StartZ=0 EndX=8.3 EndY=3 EndZ=0
    g8-g12: Circle x5 (B-spline internal-alignment scaffolding for g13; pole/knot coordinates omitted)
    g13: BSplineCurve PolesCount=5 KnotsCount=3 Degree=3 IsPeriodic=0
    g14: GeomPoint X=98 Y=6.3 Z=0
    g15: GeomPoint X=96.3938 Y=4.71946 Z=0
    g16: GeomPoint X=94.7 Y=3 Z=0
    g17-g23: Circle x7 (B-spline internal-alignment scaffolding for g24; pole/knot coordinates omitted)
    g24: BSplineCurve PolesCount=7 KnotsCount=5 Degree=3 IsPeriodic=0
    g25-g29: GeomPoint x5 (B-spline internal-alignment scaffolding for g24; pole/knot coordinates omitted)
    g30: ArcOfCircle CenterX=98 CenterY=19 CenterZ=0 NormalX=0 NormalY=0 NormalZ=1 AngleXU=0 Radius=15.7 StartAngle=5.81226 EndAngle=6.28319
    g31: LineSegment StartX=110.7 StartY=19 StartZ=0 EndX=113.7 EndY=19 EndZ=0
  constraints (41):
    c: Horizontal(g0)
    c: Coincident(g1,g0)
    c: Block(g1)
    c: Horizontal(g2)
    c: Distance(g2) = 3
    c: Coincident(g3,g2)
    c: Vertical(g3)
    c: Coincident(g3,g0)
    c: Block(g4)
    c: Block(g2)
    c: Coincident(g5,g2)
    c: Coincident(g5,g4)
    c: Vertical(g5)
    c: Coincident(g6,g1)
    c: Block(g6)
    c: Coincident(g7,g4)
    c: Horizontal(g7)
    c: Block(g0)
    c: Block(g7)
    c: Block(g3)
    c: Coincident(g13,g6)
    c: Weight(g8) = 1
    c: Equal(g8, g9-g12) x4
    c: Coincident(g13,g7)
    c: InternalAlignment(g8-g12 -> g13) x5
    c: InternalAlignment(g14,g13)
    c: InternalAlignment(g15,g13)
    c: InternalAlignment(g16,g13)
    c: Block(g13)
    c: Weight(g17) = 1
    c: Equal(g17, g18-g23) x6
    c: Coincident(g24,g1)
    c: InternalAlignment(g17-g23 -> g24) x7
    c: InternalAlignment(g25-g29 -> g24) x5
    c: Block(g24)
    c: Coincident(g30,g24)
    c: Coincident(g31,g6)
    c: Coincident(g31,g30)
    c: Horizontal(g31)
    c: Block(g31)
    c: Block(g30)
FEATURE [Part::Extrusion] Extrude062  label="bottom014"
  Base = -> Sketch071
  Dir = (0,0,1)
  DirMode = 2
  FaceMakerClass = Part::FaceMakerBullseye
  LengthFwd = 71.4
  LengthRev = 0
  Placement = pos=(0,0,0.3) rot=(0,0,1;0rad)
  Solid = true
  Symmetric = false
FEATURE [Part::Fillet] Fillet054
  Base = -> Extrude062
  Edges = 1 edges r=2.4: [Edge17]
FEATURE [Part::Fillet] Fillet055  label="bottom015"
  Base = -> Fillet054
  Edges = 1 edges r=2.4: [Edge36]
FEATURE [Part::Cylinder] Cylinder055
  Angle = 360
  AttacherType = Attacher::AttachEngine3D
  Height = 10
  Placement = pos=(0,0,36.15) rot=(0,0,1;0rad)
  Radius = 4
FEATURE [Part::MultiFuse] Fusion131  label="removeToCreateHoleForPlugHousing002"
  Placement = pos=(70,19,36.15) rot=(0,1,0;1.5708rad)
  Shapes = -> [Cylinder054,Cylinder055]
FEATURE [Part::Cut] Cut056  label="Bottom001"
  Base = -> Fillet055
  Placement = pos=(9,0,0) rot=(0,0,1;0rad)
  Tool = -> Fusion131
FEATURE [Part::Cut] Cut057
  Base = -> Cut055
  Tool = -> Cut056
FEATURE [Sketcher::SketchObject] Sketch072  label="topSketch021"
  FullyConstrained = true
  sketch-geometry (4):
    g0: ArcOfCircle CenterX=105 CenterY=19 CenterZ=0 NormalX=0 NormalY=0 NormalZ=1 AngleXU=0 Radius=20.6155 StartAngle=5.54125 EndAngle=6.28319
    g1: ArcOfCircle CenterX=105 CenterY=19 CenterZ=0 NormalX=0 NormalY=0 NormalZ=1 AngleXU=0 Radius=13 StartAngle=5.54125 EndAngle=6.28319
    g2: LineSegment StartX=118 StartY=19 StartZ=0 EndX=125.616 EndY=19 EndZ=0
    g3: LineSegment StartX=114.583 StartY=10.2157 StartZ=0 EndX=120.197 EndY=5.06982 EndZ=0
  constraints (7):
    c: Block(g0)
    c: Block(g1)
    c: Coincident(g2,g1)
    c: Coincident(g2,g0)
    c: Horizontal(g2)
    c: Coincident(g3,g1)
    c: Coincident(g3,g0)
FEATURE [Part::Extrusion] Extrude063  label="bottomPlugHousingBit003"
  Base = -> Sketch072
  Dir = (0,0,1)
  DirMode = 2
  FaceMakerClass = Part::FaceMakerBullseye
  LengthFwd = 72
  LengthRev = 0
  Solid = true
  Symmetric = false
FEATURE [Part::Cylinder] Cylinder056
  Angle = 360
  AttacherType = Attacher::AttachEngine3D
  Height = 20
  Placement = pos=(0,0,36.15) rot=(0,0,1;0rad)
  Radius = 14.3
FEATURE [Part::Cylinder] Cylinder057
  Angle = 360
  AttacherType = Attacher::AttachEngine3D
  Height = 10
  Placement = pos=(0,0,36.15) rot=(0,0,1;0rad)
  Radius = 4
FEATURE [Part::Box] Box034  label="removeToCreteHoleForPlugHousing047"
  AttacherType = Attacher::AttachEngine3D
  Height = 28.6
  Length = 20
  Placement = pos=(106.15,0,21.7) rot=(0,0,1;0rad)
  Width = 19
FEATURE [Part::Cylinder] Cylinder058
  Angle = 360
  AttacherType = Attacher::AttachEngine3D
  Height = 20
  Placement = pos=(0,0,36.15) rot=(0,0,1;0rad)
  Radius = 14.3
FEATURE [Part::Cylinder] Cylinder059
  Angle = 360
  AttacherType = Attacher::AttachEngine3D
  Height = 10
  Placement = pos=(0,0,36.15) rot=(0,0,1;0rad)
  Radius = 4
FEATURE [Part::MultiFuse] Fusion134  label="removeToCreteHoleForPlugHousing046"
  Placement = pos=(70,19,36) rot=(0,1,0;1.5708rad)
  Shapes = -> [Cylinder058,Cylinder059]
FEATURE [Part::Cylinder] Cylinder060
  Angle = 360
  AttacherType = Attacher::AttachEngine3D
  Height = 20
  Placement = pos=(0,0,36.15) rot=(0,0,1;0rad)
  Radius = 14
FEATURE [Part::Cylinder] Cylinder061
  Angle = 360
  AttacherType = Attacher::AttachEngine3D
  Height = 10
  Placement = pos=(0,0,36.15) rot=(0,0,1;0rad)
  Radius = 4
FEATURE [Part::MultiFuse] Fusion135  label="removeToCreteHoleForPlugHousing048"
  Placement = pos=(70,19,36) rot=(0,1,0;1.5708rad)
  Shapes = -> [Cylinder060,Cylinder061]
FEATURE [Part::Box] Box035  label="removeToCreteHoleForPlugHousing049"
  AttacherType = Attacher::AttachEngine3D
  Height = 28.6
  Length = 20
  Placement = pos=(106.15,0,21.7) rot=(0,0,1;0rad)
  Width = 19
FEATURE [Part::MultiFuse] Fusion133  label="removeToCreteHoleForPlugHousing045"
  Placement = pos=(0,0,-28.3) rot=(0,0,1;0rad)
  Shapes = -> [Box035,Fusion134]
FEATURE [Part::MultiFuse] Fusion138  label="removeToCreteHoleForPlugHousing051"
  Placement = pos=(70,19,36) rot=(0,1,0;1.5708rad)
  Shapes = -> [Cylinder056,Cylinder057]
FEATURE [Part::MultiFuse] Fusion137  label="removeToCreteHoleForPlugHousing050"
  Placement = pos=(0,0,28.3) rot=(0,0,1;0rad)
  Shapes = -> [Box034,Fusion138]
FEATURE [Part::MultiFuse] Fusion132  label="removeToCreatePlugHousingBottomBit002"
  Shapes = -> [Fusion133,Fusion137]
FEATURE [Part::MultiFuse] Fusion136  label="removeToCreatePlugHousingBottomBit003"
  Shapes = -> [Fusion135,Fusion132]
FEATURE [Part::Cut] Cut058  label="bottomPlugHousingBit002"
  Base = -> Extrude063
  Placement = pos=(-0.09,0,0) rot=(0,0,1;0rad)
  Tool = -> Fusion136
FEATURE [Sketcher::SketchObject] Sketch073  label="bottomSketch003"
  FullyConstrained = true
  sketch-geometry (45):
    g0: LineSegment StartX=6.29999 StartY=8 StartZ=0 EndX=3.29999 EndY=8 EndZ=0
    g1: LineSegment StartX=3.29999 StartY=8 StartZ=0 EndX=3.29999 EndY=-6.03275e-07 EndZ=0
    g2: ArcOfCircle CenterX=8.29999 CenterY=5 CenterZ=0 NormalX=0 NormalY=0 NormalZ=1 AngleXU=0 Radius=2 StartAngle=3.14159 EndAngle=4.71239
    g3: LineSegment StartX=6.29999 StartY=8 StartZ=0 EndX=6.29999 EndY=5 EndZ=0
    g4: ArcOfCircle CenterX=105 CenterY=19 CenterZ=0 NormalX=0 NormalY=0 NormalZ=1 AngleXU=0 Radius=12.7 StartAngle=4.71239 EndAngle=5.94289
    g5-g11: Circle x7 (B-spline internal-alignment scaffolding for g12; pole/knot coordinates omitted)
    g12: BSplineCurve PolesCount=7 KnotsCount=5 Degree=3 IsPeriodic=0
    g13-g17: GeomPoint x5 (B-spline internal-alignment scaffolding for g12; pole/knot coordinates omitted)
    g18: ArcOfCircle CenterX=105 CenterY=19 CenterZ=0 NormalX=0 NormalY=0 NormalZ=1 AngleXU=0 Radius=15.7 StartAngle=5.81226 EndAngle=6.28319
    g19: BSplineCurve PolesCount=5 KnotsCount=3 Degree=3 IsPeriodic=0
    g20: LineSegment StartX=8.29999 StartY=3 StartZ=0 EndX=101.7 EndY=3 EndZ=0
    g21: LineSegment StartX=3.29999 StartY=-6.03275e-07 StartZ=0 EndX=105 EndY=-6.03275e-07 EndZ=0
    g22: LineSegment StartX=120.974 StartY=8.71251 StartZ=0 EndX=122.332 EndY=7.83778 EndZ=0
    g23: LineSegment StartX=105 StartY=-6.03274e-07 StartZ=0 EndX=113 EndY=-6.03274e-07 EndZ=0
    g24: ArcOfCircle CenterX=105 CenterY=19 CenterZ=0 NormalX=0 NormalY=0 NormalZ=1 AngleXU=0 Radius=20.6155 StartAngle=5.11091 EndAngle=5.71103
    g25: ArcOfCircle CenterX=117.7 CenterY=19 CenterZ=0 NormalX=0 NormalY=0 NormalZ=1 AngleXU=0 Radius=3 StartAngle=1.2e-15 EndAngle=2.10468
    g26: Circle CenterX=116.345 CenterY=16.3232 CenterZ=0 NormalX=0 NormalY=0 NormalZ=1 AngleXU=0 Radius=1
    g27: Circle CenterX=117.24 CenterY=15.7584 CenterZ=0 NormalX=0 NormalY=0 NormalZ=1 AngleXU=0 Radius=1
    g28: Circle CenterX=116.972 CenterY=14.7612 CenterZ=0 NormalX=0 NormalY=0 NormalZ=1 AngleXU=0 Radius=1
    g29: BSplineCurve PolesCount=3 KnotsCount=2 Degree=2 IsPeriodic=0
    g30: GeomPoint X=116.345 Y=16.3232 Z=0
    g31: GeomPoint X=116.972 Y=14.7612 Z=0
    g32: Circle CenterX=115.828 CenterY=17.157 CenterZ=0 NormalX=0 NormalY=0 NormalZ=1 AngleXU=0 Radius=1
    g33: Circle CenterX=115.841 CenterY=16.639 CenterZ=0 NormalX=0 NormalY=0 NormalZ=1 AngleXU=0 Radius=1
    g34: Circle CenterX=116.345 CenterY=16.3232 CenterZ=0 NormalX=0 NormalY=0 NormalZ=1 AngleXU=0 Radius=1
    g35: BSplineCurve PolesCount=3 KnotsCount=2 Degree=2 IsPeriodic=0
    g36: GeomPoint X=115.828 Y=17.157 Z=0
    g37: GeomPoint X=116.345 Y=16.3232 Z=0
    g38: LineSegment StartX=115.828 StartY=17.157 StartZ=0 EndX=115.828 EndY=20.8307 EndZ=0
    g39: Circle CenterX=115.828 CenterY=20.8307 CenterZ=0 NormalX=0 NormalY=0 NormalZ=1 AngleXU=0 Radius=1
    g40: Circle CenterX=115.831 CenterY=21.3396 CenterZ=0 NormalX=0 NormalY=0 NormalZ=1 AngleXU=0 Radius=1
    g41: Circle CenterX=116.173 CenterY=21.5825 CenterZ=0 NormalX=0 NormalY=0 NormalZ=1 AngleXU=0 Radius=1
    g42: BSplineCurve PolesCount=3 KnotsCount=2 Degree=2 IsPeriodic=0
    g43: GeomPoint X=115.828 Y=20.8307 Z=0
    g44: GeomPoint X=116.173 Y=21.5825 Z=0
  constraints (70):
    c: Horizontal(g0)
    c: Distance(g0) = 3
    c: Coincident(g1,g0)
    c: Vertical(g1)
    c: Block(g2)
    c: Block(g0)
    c: Coincident(g3,g0)
    c: Coincident(g3,g2)
    c: Vertical(g3)
    c: Block(g1)
    c: Block(g4)
    c: Coincident(g19,g4)
    c: Block(g19)
    c: Equal(g5, g6-g11) x6
    c: InternalAlignment(g5-g11 -> g12) x7
    c: InternalAlignment(g13-g17 -> g12) x5
    c: Block(g12)
    c: Coincident(g18,g12)
    c: Block(g18)
    c: Coincident(g20,g2)
    c: Coincident(g20,g19)
    c: Horizontal(g20)
    c: Distance(g20) = 93.4
    c: Coincident(g21,g1)
    c: Horizontal(g21)
    c: Distance(g21) = 101.7
    c: Horizontal(g23)
    c: Distance(g23) = 8
    c: Coincident(g24,g23)
    c: Block(g23)
    c: Coincident(g22,g24)
    c: Block(g24)
    c: Block(g22)
    c: Distance(g22) = 1.61553
    c: Coincident(g25,g18)
    c: Block(g25)
    c: Weight(g26) = 1
    c: Equal(g26,g27)
    c: Equal(g26,g28)
    c: Coincident(g29,g4)
    c: InternalAlignment(g26,g29)
    c: InternalAlignment(g27,g29)
    c: InternalAlignment(g28,g29)
    c: InternalAlignment(g30,g29)
    c: InternalAlignment(g31,g29)
    c: Block(g29)
    c: Weight(g32) = 1
    c: Equal(g32,g33)
    c: Equal(g32,g34)
    c: Coincident(g35,g29)
    c: InternalAlignment(g32,g35)
    c: InternalAlignment(g33,g35)
    c: InternalAlignment(g34,g35)
    c: InternalAlignment(g36,g35)
    c: InternalAlignment(g37,g35)
    c: Block(g35)
    c: Coincident(g38,g35)
    c: Vertical(g38)
    c: Block(g38)
    c: Coincident(g42,g38)
    c: Weight(g39) = 1
    c: Equal(g39,g40)
    c: Equal(g39,g41)
    c: Coincident(g42,g25)
    c: InternalAlignment(g39,g42)
    c: InternalAlignment(g40,g42)
    c: InternalAlignment(g41,g42)
    c: InternalAlignment(g43,g42)
    c: InternalAlignment(g44,g42)
    c: Block(g42)
FEATURE [Part::Extrusion] Extrude064  label="bottom016"
  Base = -> Sketch073
  Dir = (0,0,1)
  DirMode = 2
  FaceMakerClass = Part::FaceMakerBullseye
  LengthFwd = 71.4
  LengthRev = 0
  Placement = pos=(0,0,0.3) rot=(0,0,1;0rad)
  Solid = true
  Symmetric = false
FEATURE [Part::Revolution] Revolve157  label="removeToCreateScrewAndThreadedInsertHole063"
  Angle = 360
  Axis = (0,1,0)
  Base = (0,0,0)
  FaceMakerClass = Part::FaceMakerBullseye
  Placement = pos=(12.5,0,10) rot=(0,0,1;0rad)
  Solid = false
  Source = -> Face141
  Symmetric = false
FEATURE [Sketcher::SketchObject] Sketch074
  FullyConstrained = true
  Placement = pos=(117,19,0) rot=(0.57735,0.57735,0.57735;2.0944rad)
  sketch-geometry (48):
    g0: LineSegment StartX=-49.19 StartY=69.25 StartZ=0 EndX=-49.19 EndY=66.25 EndZ=0
    g1: LineSegment StartX=-49.19 StartY=63.5 StartZ=0 EndX=-49.19 EndY=60.5 EndZ=0
    g2: LineSegment StartX=-49.19 StartY=57.75 StartZ=0 EndX=-49.19 EndY=54.75 EndZ=0
    g3: LineSegment StartX=-49.19 StartY=52 StartZ=0 EndX=-49.19 EndY=49 EndZ=0
    g4: LineSegment StartX=-49.19 StartY=46.25 StartZ=0 EndX=-49.19 EndY=43.25 EndZ=0
    g5: LineSegment StartX=-49.19 StartY=40.5 StartZ=0 EndX=-49.19 EndY=37.5 EndZ=0
    g6: LineSegment StartX=-49.19 StartY=34.5 StartZ=0 EndX=-49.19 EndY=31.5 EndZ=0
    g7: LineSegment StartX=-49.19 StartY=28.75 StartZ=0 EndX=-49.19 EndY=25.75 EndZ=0
    g8: LineSegment StartX=-49.19 StartY=23 StartZ=0 EndX=-49.19 EndY=20 EndZ=0
    g9: LineSegment StartX=-49.19 StartY=17.25 StartZ=0 EndX=-49.19 EndY=14.25 EndZ=0
    g10: LineSegment StartX=-49.19 StartY=11.5 StartZ=0 EndX=-49.19 EndY=8.5 EndZ=0
    g11: LineSegment StartX=-49.19 StartY=5.75 StartZ=0 EndX=-49.19 EndY=2.75 EndZ=0
    g12: ArcOfCircle CenterX=-1.5 CenterY=67.75 CenterZ=0 NormalX=0 NormalY=0 NormalZ=1 AngleXU=0 Radius=1.5 StartAngle=4.71239 EndAngle=7.85398
    g13: ArcOfCircle CenterX=-1.5 CenterY=62 CenterZ=0 NormalX=0 NormalY=0 NormalZ=1 AngleXU=0 Radius=1.5 StartAngle=4.71239 EndAngle=7.85398
    g14: ArcOfCircle CenterX=-1.5 CenterY=56.25 CenterZ=0 NormalX=0 NormalY=0 NormalZ=1 AngleXU=0 Radius=1.5 StartAngle=4.71239 EndAngle=7.85398
    g15: ArcOfCircle CenterX=-11.49 CenterY=50.5 CenterZ=0 NormalX=0 NormalY=0 NormalZ=1 AngleXU=0 Radius=1.5 StartAngle=4.71239 EndAngle=7.85398
    g16: ArcOfCircle CenterX=-16.28 CenterY=44.75 CenterZ=0 NormalX=0 NormalY=0 NormalZ=1 AngleXU=0 Radius=1.5 StartAngle=4.71239 EndAngle=7.85398
    g17: ArcOfCircle CenterX=-18.2337 CenterY=39 CenterZ=0 NormalX=0 NormalY=0 NormalZ=1 AngleXU=0 Radius=1.5 StartAngle=4.71485 EndAngle=7.85398
    g18: ArcOfCircle CenterX=-16.2837 CenterY=27.25 CenterZ=0 NormalX=0 NormalY=0 NormalZ=1 AngleXU=0 Radius=1.5 StartAngle=4.71485 EndAngle=7.85398
    g19: ArcOfCircle CenterX=-18.2337 CenterY=33 CenterZ=0 NormalX=0 NormalY=0 NormalZ=1 AngleXU=0 Radius=1.5 StartAngle=4.71485 EndAngle=7.85398
    g20: ArcOfCircle CenterX=-11.49 CenterY=21.5 CenterZ=0 NormalX=0 NormalY=0 NormalZ=1 AngleXU=0 Radius=1.5 StartAngle=4.71239 EndAngle=7.85398
    g21: ArcOfCircle CenterX=-1.5 CenterY=4.25 CenterZ=0 NormalX=0 NormalY=0 NormalZ=1 AngleXU=0 Radius=1.5 StartAngle=4.71239 EndAngle=7.85398
    g22: ArcOfCircle CenterX=-1.5 CenterY=10 CenterZ=0 NormalX=0 NormalY=0 NormalZ=1 AngleXU=0 Radius=1.5 StartAngle=4.71239 EndAngle=7.85398
    g23: ArcOfCircle CenterX=-1.5 CenterY=15.75 CenterZ=0 NormalX=0 NormalY=0 NormalZ=1 AngleXU=0 Radius=1.5 StartAngle=4.71239 EndAngle=7.85398
    g24: LineSegment StartX=-49.19 StartY=69.25 StartZ=0 EndX=-1.5 EndY=69.25 EndZ=0
    g25: LineSegment StartX=-49.19 StartY=66.25 StartZ=0 EndX=-1.5 EndY=66.25 EndZ=0
    g26: LineSegment StartX=-49.19 StartY=63.5 StartZ=0 EndX=-1.5 EndY=63.5 EndZ=0
    g27: LineSegment StartX=-49.19 StartY=60.5 StartZ=0 EndX=-1.5 EndY=60.5 EndZ=0
    g28: LineSegment StartX=-49.19 StartY=57.75 StartZ=0 EndX=-1.5 EndY=57.75 EndZ=0
    g29: LineSegment StartX=-49.19 StartY=54.75 StartZ=0 EndX=-1.5 EndY=54.75 EndZ=0
    g30: LineSegment StartX=-49.19 StartY=52 StartZ=0 EndX=-11.49 EndY=52 EndZ=0
    g31: LineSegment StartX=-49.19 StartY=49 StartZ=0 EndX=-11.49 EndY=49 EndZ=0
    g32: LineSegment StartX=-49.19 StartY=46.25 StartZ=0 EndX=-16.28 EndY=46.25 EndZ=0
    g33: LineSegment StartX=-49.19 StartY=43.25 StartZ=0 EndX=-16.28 EndY=43.25 EndZ=0
    g34: LineSegment StartX=-49.19 StartY=40.5 StartZ=0 EndX=-18.2337 EndY=40.5 EndZ=0
    g35: LineSegment StartX=-49.19 StartY=37.5 StartZ=0 EndX=-18.23 EndY=37.5 EndZ=0
    g36: LineSegment StartX=-49.19 StartY=34.5 StartZ=0 EndX=-18.2337 EndY=34.5 EndZ=0
    g37: LineSegment StartX=-49.19 StartY=31.5 StartZ=0 EndX=-18.23 EndY=31.5 EndZ=0
    g38: LineSegment StartX=-49.19 StartY=28.75 StartZ=0 EndX=-16.2837 EndY=28.75 EndZ=0
    g39: LineSegment StartX=-49.19 StartY=25.75 StartZ=0 EndX=-16.28 EndY=25.75 EndZ=0
    g40: LineSegment StartX=-49.19 StartY=23 StartZ=0 EndX=-11.49 EndY=23 EndZ=0
    g41: LineSegment StartX=-49.19 StartY=20 StartZ=0 EndX=-11.49 EndY=20 EndZ=0
    g42: LineSegment StartX=-49.19 StartY=17.25 StartZ=0 EndX=-1.5 EndY=17.25 EndZ=0
    g43: LineSegment StartX=-49.19 StartY=14.25 StartZ=0 EndX=-1.5 EndY=14.25 EndZ=0
    g44: LineSegment StartX=-49.19 StartY=11.5 StartZ=0 EndX=-1.5 EndY=11.5 EndZ=0
    g45: LineSegment StartX=-49.19 StartY=8.5 StartZ=0 EndX=-1.5 EndY=8.5 EndZ=0
    g46: LineSegment StartX=-49.19 StartY=5.75 StartZ=0 EndX=-1.5 EndY=5.75 EndZ=0
    g47: LineSegment StartX=-49.19 StartY=2.75 StartZ=0 EndX=-1.5 EndY=2.75 EndZ=0
  constraints (120):
    c: Vertical(g0)
    c: Distance(g0) = 3
    c: Block(g0)
    c: Vertical(g1)
    c: Distance(g1) = 3
    c: Vertical(g2)
    c: Equal(g0,g2) = 3
    c: Block(g2)
    c: Vertical(g3)
    c: Equal(g1,g3) = 3
    c: Vertical(g4)
    c: Equal(g0,g4) = 3
    c: Block(g4)
    c: Vertical(g5)
    c: Equal(g1,g5) = 3
    c: Vertical(g6)
    c: Equal(g0,g6) = 3
    c: Block(g6)
    c: Vertical(g7)
    c: Equal(g1,g7) = 3
    c: Vertical(g8)
    c: Equal(g0,g8) = 3
    c: Block(g8)
    c: Vertical(g9)
    c: Equal(g1,g9) = 3
    c: Vertical(g10)
    c: Equal(g0,g10) = 3
    c: Block(g10)
    c: Vertical(g11)
    c: Equal(g1,g11) = 3
    c: Block(g12)
    c: Block(g13)
    c: Block(g14)
    c: Block(g15)
    c: Block(g16)
    c: Block(g17)
    c: Block(g18)
    c: Block(g19)
    c: Block(g20)
    c: Block(g21)
    c: Block(g22)
    c: Block(g23)
    c: Block(g11)
    c: Block(g9)
    c: Block(g7)
    c: Block(g5)
    c: Block(g3)
    c: Block(g1)
    c: Coincident(g24,g0)
    c: Coincident(g24,g12)
    c: Horizontal(g24)
    c: Coincident(g25,g0)
    c: Coincident(g25,g12)
    c: Horizontal(g25)
    c: Coincident(g26,g1)
    c: Coincident(g26,g13)
    c: Horizontal(g26)
    c: Coincident(g27,g1)
    c: Coincident(g27,g13)
    c: Horizontal(g27)
    c: Coincident(g28,g2)
    c: Coincident(g28,g14)
    c: Horizontal(g28)
    c: Coincident(g29,g2)
    c: Coincident(g29,g14)
    c: Horizontal(g29)
    c: Coincident(g30,g3)
    c: Coincident(g30,g15)
    c: Horizontal(g30)
    c: Coincident(g31,g3)
    c: Coincident(g31,g15)
    c: Horizontal(g31)
    c: Coincident(g32,g4)
    c: Coincident(g32,g16)
    c: Horizontal(g32)
    c: Coincident(g33,g4)
    c: Coincident(g33,g16)
    c: Horizontal(g33)
    c: Coincident(g34,g5)
    c: Coincident(g34,g17)
    c: Horizontal(g34)
    c: Coincident(g35,g5)
    c: Coincident(g35,g17)
    c: Horizontal(g35)
    c: Coincident(g36,g6)
    c: Coincident(g36,g19)
    c: Horizontal(g36)
    c: Coincident(g37,g6)
    c: Coincident(g37,g19)
    c: Horizontal(g37)
    c: Coincident(g38,g7)
    c: Coincident(g38,g18)
    c: Horizontal(g38)
    c: Coincident(g39,g7)
    c: Coincident(g39,g18)
    c: Horizontal(g39)
    c: Coincident(g40,g8)
    c: Coincident(g40,g20)
    c: Horizontal(g40)
    c: Coincident(g41,g8)
    c: Coincident(g41,g20)
    c: Horizontal(g41)
    c: Coincident(g42,g9)
    c: Coincident(g42,g23)
    c: Horizontal(g42)
    c: Coincident(g43,g9)
    c: Coincident(g43,g23)
    c: Horizontal(g43)
    c: Coincident(g44,g10)
    c: Coincident(g44,g22)
    c: Horizontal(g44)
    c: Coincident(g45,g10)
    c: Coincident(g45,g22)
    c: Horizontal(g45)
    c: Coincident(g46,g11)
    c: Coincident(g46,g21)
    c: Horizontal(g46)
    c: Coincident(g47,g11)
    c: Coincident(g47,g21)
    c: Horizontal(g47)
FEATURE [Part::Extrusion] Extrude065
  Base = -> Sketch074
  Dir = (1,0,0)
  DirMode = 2
  FaceMakerClass = Part::FaceMakerBullseye
  LengthFwd = 23
  LengthRev = 0
  Placement = pos=(-19,0,0) rot=(0,0,1;0rad)
  Solid = true
  Symmetric = false
FEATURE [Part::Fillet] Fillet056  label="removeToCreateVentalationHoles003"
  Base = -> Extrude065
  Edges = <same value as first occurrence — deduplicated (x6 in doc)>
  Placement = pos=(7,0.02,0) rot=(0,0,1;0rad)
FEATURE [Part::Revolution] Revolve158  label="removeToCreateScrewAndThreadedInsertHole065"
  Angle = 360
  Axis = (0,1,0)
  Base = (0,0,0)
  FaceMakerClass = Part::FaceMakerBullseye
  Placement = pos=(12.5,0,62) rot=(0,0,1;0rad)
  Solid = false
  Source = -> Face146
  Symmetric = false
FEATURE [Part::Revolution] Revolve159  label="removeToCreateScrewAndThreadedInsertHole066"
  Angle = 360
  Axis = (0,1,0)
  Base = (0,0,0)
  FaceMakerClass = Part::FaceMakerBullseye
  Placement = pos=(89.5,0,68.5) rot=(0,0,1;0rad)
  Solid = false
  Source = -> Face143
  Symmetric = false
FEATURE [Part::Revolution] Revolve160  label="removeToCreateScrewAndThreadedInsertHole067"
  Angle = 360
  Axis = (0,1,0)
  Base = (0,0,0)
  FaceMakerClass = Part::FaceMakerBullseye
  Placement = pos=(89.5,0,3.5) rot=(0,0,1;0rad)
  Solid = false
  Source = -> Face142
  Symmetric = false
FEATURE [Part::Revolution] Revolve161  label="removeToCreateScrewAndThreadedInsertHole068"
  Angle = 360
  Axis = (0,1,0)
  Base = (0,0,0)
  FaceMakerClass = Part::FaceMakerBullseye
  Placement = pos=(109.5,4.7,3.5) rot=(0,0,1;0rad)
  Solid = false
  Source = -> Face145
  Symmetric = false
FEATURE [Part::Revolution] Revolve162  label="removeToCreateScrewAndThreadedInsertHole069"
  Angle = 360
  Axis = (0,1,0)
  Base = (0,0,0)
  FaceMakerClass = Part::FaceMakerBullseye
  Placement = pos=(109.5,4.7,68.5) rot=(0,0,1;0rad)
  Solid = false
  Source = -> Face144
  Symmetric = false
FEATURE [Part::MultiFuse] Fusion141  label="removeToCreateScrewAndThreadedInsertHole064"
  Shapes = -> [Revolve162,Revolve161,Revolve160,Revolve159,Revolve158,Revolve157]
FEATURE [Part::Cylinder] Cylinder062
  Angle = 360
  AttacherType = Attacher::AttachEngine3D
  Height = 20
  Placement = pos=(0,0,36.15) rot=(0,0,1;0rad)
  Radius = 14
FEATURE [Part::Cylinder] Cylinder063
  Angle = 360
  AttacherType = Attacher::AttachEngine3D
  Height = 10
  Placement = pos=(0,0,36.15) rot=(0,0,1;0rad)
  Radius = 4
FEATURE [Part::MultiFuse] Fusion139  label="removeToCreteHoleForPlugHousing052"
  Placement = pos=(70,19,36) rot=(0,1,0;1.5708rad)
  Shapes = -> [Cylinder062,Cylinder063]
FEATURE [Part::Cut] Cut060  label="bottom017"
  Base = -> Extrude064
  Tool = -> Fusion139
FEATURE [Part::Cut] Cut061  label="bottom019"
  Base = -> Cut060
  Tool = -> Fusion141
FEATURE [Part::MultiFuse] Fusion140  label="bottom018"
  Shapes = -> [Cut061,Cut058]
FEATURE [Part::Cut] Cut059  label="bottom020"
  Base = -> Fusion140
  Tool = -> Fillet056
FEATURE [Part::Box] Box036  label="Cube021"
  AttacherType = Attacher::AttachEngine3D
  Height = 80
  Length = 26
  Placement = pos=(0,-1,-5) rot=(0,0,1;0rad)
  Width = 11
FEATURE [Part::Cut] Cut062  label="removeFromBottom002"
  Base = -> Cut057
  Tool = -> Box036
FEATURE [Part::Cut] Cut063
  Base = -> Cut059
  Tool = -> Cut062
FEATURE [Part::Cut] Cut064  label="pcbStands"
  Base = -> Fusion095
  Tool = -> Fusion127
FEATURE [Sketcher::SketchObject] Sketch075  label="topSketch022"
  FullyConstrained = true
  sketch-geometry (6):
    g0: LineSegment StartX=19 StartY=38 StartZ=0 EndX=117 EndY=38 EndZ=0
    g1: ArcOfCircle CenterX=19 CenterY=19 CenterZ=0 NormalX=0 NormalY=0 NormalZ=1 AngleXU=0 Radius=19 StartAngle=1.5708 EndAngle=3.14159
    g2: LineSegment StartX=117 StartY=38 StartZ=0 EndX=117 EndY=19 EndZ=0
    g3: LineSegment StartX=98 StartY=1.0161e-12 StartZ=0 EndX=5.22862e-06 EndY=1.0161e-12 EndZ=0
    g4: LineSegment StartX=5.22862e-06 StartY=19 StartZ=0 EndX=5.22862e-06 EndY=1.0161e-12 EndZ=0
    g5: ArcOfCircle CenterX=98 CenterY=19 CenterZ=0 NormalX=0 NormalY=0 NormalZ=1 AngleXU=0 Radius=19 StartAngle=4.71239 EndAngle=6.28319
  constraints (16):
    c: Horizontal(g0)
    c: Distance(g0) = 98
    c: Coincident(g1,g0)
    c: Block(g1)
    c: Coincident(g2,g0)
    c: Vertical(g2)
    c: Distance(g2) = 19
    c: Horizontal(g3)
    c: Coincident(g4,g1)
    c: Vertical(g4)
    c: Coincident(g3,g4)
    c: Block(g3)
    c: Coincident(g5,g2)
    c: Coincident(g5,g3)
    c: Block(g0)
    c: Block(g5)
FEATURE [Part::Extrusion] Extrude067  label="sideB003"
  Base = -> Sketch075
  Dir = (0,0,1)
  DirMode = 2
  FaceMakerClass = Part::FaceMakerBullseye
  LengthFwd = 3
  LengthRev = 0
  Placement = pos=(0,0,71.7) rot=(0,0,1;0rad)
  Solid = true
  Symmetric = false
FEATURE [Sketcher::SketchObject] Sketch076  label="topSketch023"
  FullyConstrained = true
  sketch-geometry (6):
    g0: LineSegment StartX=19 StartY=38 StartZ=0 EndX=117 EndY=38 EndZ=0
    g1: ArcOfCircle CenterX=19 CenterY=19 CenterZ=0 NormalX=0 NormalY=0 NormalZ=1 AngleXU=0 Radius=19 StartAngle=1.5708 EndAngle=3.14159
    g2: LineSegment StartX=117 StartY=38 StartZ=0 EndX=117 EndY=19 EndZ=0
    g3: LineSegment StartX=98 StartY=1.0161e-12 StartZ=0 EndX=5.22862e-06 EndY=1.0161e-12 EndZ=0
    g4: LineSegment StartX=5.22862e-06 StartY=19 StartZ=0 EndX=5.22862e-06 EndY=1.0161e-12 EndZ=0
    g5: ArcOfCircle CenterX=98 CenterY=19 CenterZ=0 NormalX=0 NormalY=0 NormalZ=1 AngleXU=0 Radius=19 StartAngle=4.71239 EndAngle=6.28319
  constraints (16):
    c: Horizontal(g0)
    c: Distance(g0) = 98
    c: Coincident(g1,g0)
    c: Block(g1)
    c: Coincident(g2,g0)
    c: Vertical(g2)
    c: Distance(g2) = 19
    c: Horizontal(g3)
    c: Coincident(g4,g1)
    c: Vertical(g4)
    c: Coincident(g3,g4)
    c: Block(g3)
    c: Coincident(g5,g2)
    c: Coincident(g5,g3)
    c: Block(g0)
    c: Block(g5)
FEATURE [Part::Extrusion] Extrude066  label="sideA003"
  Base = -> Sketch076
  Dir = (0,0,1)
  DirMode = 2
  FaceMakerClass = Part::FaceMakerBullseye
  LengthFwd = 3
  LengthRev = 0
  Placement = pos=(0,0,-2.7) rot=(0,0,1;0rad)
  Solid = true
  Symmetric = false
FEATURE [Part::MultiFuse] Fusion142  label="removeFromBottom003"
  Placement = pos=(2,0,0) rot=(0,0,1;0rad)
  Shapes = -> [Extrude066,Extrude067]
FEATURE [Part::Cut] Cut065  label="screwRetainers002"
  Base = -> Fusion096
  Tool = -> Fusion142
FEATURE [Sketcher::SketchObject] Sketch077
  FullyConstrained = true
  Placement = pos=(117,19,0) rot=(0.57735,0.57735,0.57735;2.0944rad)
  sketch-geometry (8):
    g0: LineSegment StartX=-49.19 StartY=63.5 StartZ=0 EndX=-49.19 EndY=60.5 EndZ=0
    g1: LineSegment StartX=-49.19 StartY=11.5 StartZ=0 EndX=-49.19 EndY=8.5 EndZ=0
    g2: ArcOfCircle CenterX=-1.5 CenterY=62 CenterZ=0 NormalX=0 NormalY=0 NormalZ=1 AngleXU=0 Radius=1.5 StartAngle=4.71239 EndAngle=7.85398
    g3: ArcOfCircle CenterX=-1.5 CenterY=10 CenterZ=0 NormalX=0 NormalY=0 NormalZ=1 AngleXU=0 Radius=1.5 StartAngle=4.71239 EndAngle=7.85398
    g4: LineSegment StartX=-49.19 StartY=63.5 StartZ=0 EndX=-1.5 EndY=63.5 EndZ=0
    g5: LineSegment StartX=-49.19 StartY=60.5 StartZ=0 EndX=-1.5 EndY=60.5 EndZ=0
    g6: LineSegment StartX=-49.19 StartY=11.5 StartZ=0 EndX=-1.5 EndY=11.5 EndZ=0
    g7: LineSegment StartX=-49.19 StartY=8.5 StartZ=0 EndX=-1.5 EndY=8.5 EndZ=0
  constraints (19):
    c: Vertical(g0)
    c: Distance(g0) = 3
    c: Vertical(g1)
    c: Block(g1)
    c: Block(g2)
    c: Block(g3)
    c: Block(g0)
    c: Coincident(g4,g0)
    c: Coincident(g4,g2)
    c: Horizontal(g4)
    c: Coincident(g5,g0)
    c: Coincident(g5,g2)
    c: Horizontal(g5)
    c: Coincident(g6,g1)
    c: Coincident(g6,g3)
    c: Horizontal(g6)
    c: Coincident(g7,g1)
    c: Coincident(g7,g3)
    c: Horizontal(g7)
FEATURE [Part::Extrusion] Extrude068
  Base = -> Sketch077
  Dir = (1,0,0)
  DirMode = 2
  FaceMakerClass = Part::FaceMakerBullseye
  LengthFwd = 10
  LengthRev = 0
  Solid = true
  Symmetric = false
FEATURE [Part::Fillet] Fillet057  label="removeFromtMoreFrontCaseScrewRetainers002"
  Base = -> Extrude068
  Edges = 4 edges r=1.49: [Edge6,Edge11,Edge18,Edge23]
  Placement = pos=(-12,0,0) rot=(0,0,1;0rad)
FEATURE [Sketcher::SketchObject] Sketch078
  FullyConstrained = true
  Placement = pos=(117,19,0) rot=(0.57735,0.57735,0.57735;2.0944rad)
  sketch-geometry (8):
    g0: LineSegment StartX=-49.19 StartY=69.25 StartZ=0 EndX=-49.19 EndY=66.25 EndZ=0
    g1: LineSegment StartX=-49.19 StartY=5.75 StartZ=0 EndX=-49.19 EndY=2.75 EndZ=0
    g2: ArcOfCircle CenterX=-1.5 CenterY=67.75 CenterZ=0 NormalX=0 NormalY=0 NormalZ=1 AngleXU=0 Radius=1.5 StartAngle=4.71239 EndAngle=7.85398
    g3: ArcOfCircle CenterX=-1.5 CenterY=4.25 CenterZ=0 NormalX=0 NormalY=0 NormalZ=1 AngleXU=0 Radius=1.5 StartAngle=4.71239 EndAngle=7.85398
    g4: LineSegment StartX=-49.19 StartY=69.25 StartZ=0 EndX=-1.5 EndY=69.25 EndZ=0
    g5: LineSegment StartX=-49.19 StartY=66.25 StartZ=0 EndX=-1.5 EndY=66.25 EndZ=0
    g6: LineSegment StartX=-49.19 StartY=5.75 StartZ=0 EndX=-1.5 EndY=5.75 EndZ=0
    g7: LineSegment StartX=-49.19 StartY=2.75 StartZ=0 EndX=-1.5 EndY=2.75 EndZ=0
  constraints (19):
    c: Vertical(g0)
    c: Distance(g0) = 3
    c: Block(g0)
    c: Vertical(g1)
    c: Block(g2)
    c: Block(g3)
    c: Block(g1)
    c: Coincident(g4,g0)
    c: Coincident(g4,g2)
    c: Horizontal(g4)
    c: Coincident(g5,g0)
    c: Coincident(g5,g2)
    c: Horizontal(g5)
    c: Coincident(g6,g1)
    c: Coincident(g6,g3)
    c: Horizontal(g6)
    c: Coincident(g7,g1)
    c: Coincident(g7,g3)
    c: Horizontal(g7)
FEATURE [Part::Extrusion] Extrude069
  Base = -> Sketch078
  Dir = (1,0,0)
  DirMode = 2
  FaceMakerClass = Part::FaceMakerBullseye
  LengthFwd = 10
  LengthRev = 0
  Solid = true
  Symmetric = false
FEATURE [Part::Fillet] Fillet058  label="removeFromtMoreFrontCaseScrewRetainers003"
  Base = -> Extrude069
  Edges = 4 edges r=1.49: [Edge6,Edge11,Edge18,Edge23]
  Placement = pos=(-4,0,0) rot=(0,0,1;0rad)
FEATURE [Part::Cut] Cut066
  Base = -> Cut065
  Tool = -> Fillet058
FEATURE [Part::Cut] Cut067  label="screwPillars"
  Base = -> Cut066
  Tool = -> Fillet057
FEATURE [Part::MultiFuse] Fusion143  label="bottom021"
  Shapes = -> [Cut031,Cut063]
FEATURE [Part::Cylinder] Cylinder
  Angle = 360
  AttacherType = Attacher::AttachEngine3D
  Height = 10
  Placement = pos=(20.65,12,4.68) rot=(1,0,0;1.5708rad)
  Radius = 2
FEATURE [Part::Cylinder] Cylinder064
  Angle = 360
  AttacherType = Attacher::AttachEngine3D
  Height = 10
  Placement = pos=(20.65,12,67.38) rot=(1,0,0;1.5708rad)
  Radius = 2
FEATURE [Part::Cylinder] Cylinder065
  Angle = 360
  AttacherType = Attacher::AttachEngine3D
  Height = 10
  Placement = pos=(77.15,12,67.38) rot=(1,0,0;1.5708rad)
  Radius = 2
FEATURE [Part::Cylinder] Cylinder066
  Angle = 360
  AttacherType = Attacher::AttachEngine3D
  Height = 10
  Placement = pos=(77.15,12,4.68) rot=(1,0,0;1.5708rad)
  Radius = 2
FEATURE [Part::MultiFuse] Fusion144  label="removeFromThreadedInsertHousing"
  Shapes = -> [Cylinder065,Cylinder064,Cylinder,Cylinder066]
FEATURE [Part::Cut] Cut068  label="pcbStands001"
  Base = -> Cut064
  Tool = -> Fusion144
FEATURE [Part::MultiFuse] Fusion145
  Shapes = -> [Cut068,Fusion143]
FEATURE [Part::MultiFuse] Fusion146
  Shapes = -> [Fusion145]
FEATURE [Part::MultiFuse] Fusion147  label="bottom022"
  Shapes = -> [Cut067,Fusion146]
FEATURE [Part::MultiFuse] Fusion148  label="casePillars005"
  Shapes = -> [Cut047,Fusion092]
FEATURE [Part::MultiFuse] Fusion149  label="bottom023"
  Shapes = -> [Fusion124,Fusion113,Fusion147]
FEATURE [Part::MultiFuse] Fusion150  label="topBits"
  Shapes = -> [Cut025,Fusion148,Cut030,Fillet034]
FEATURE [Part::Feature] Face149 .. Face152  x4 (patterned run collapsed; names and placements below)
  shape: bbox 3.2 x 1.5 x 2e-07 mm, 1 faces, 0 solids (baked)
FEATURE [Part::Feature] Face153
  shape: bbox 3.6 x 3.2 x 2e-07 mm, 1 faces, 0 solids (baked)
FEATURE [Part::Feature] Face154
  shape: bbox 3.6 x 3.2 x 2e-07 mm, 1 faces, 0 solids (baked)
FEATURE [Sketcher::SketchObject] Sketch079  label="topSketch024"
  FullyConstrained = true
  sketch-geometry (6):
    g0: LineSegment StartX=19 StartY=38 StartZ=0 EndX=117 EndY=38 EndZ=0
    g1: ArcOfCircle CenterX=19 CenterY=19 CenterZ=0 NormalX=0 NormalY=0 NormalZ=1 AngleXU=0 Radius=19 StartAngle=1.5708 EndAngle=3.14159
    g2: LineSegment StartX=117 StartY=38 StartZ=0 EndX=117 EndY=19 EndZ=0
    g3: LineSegment StartX=98 StartY=1.0161e-12 StartZ=0 EndX=5.22862e-06 EndY=1.0161e-12 EndZ=0
    g4: LineSegment StartX=5.22862e-06 StartY=19 StartZ=0 EndX=5.22862e-06 EndY=1.0161e-12 EndZ=0
    g5: ArcOfCircle CenterX=98 CenterY=19 CenterZ=0 NormalX=0 NormalY=0 NormalZ=1 AngleXU=0 Radius=19 StartAngle=4.71239 EndAngle=6.28319
  constraints (16):
    c: Horizontal(g0)
    c: Distance(g0) = 98
    c: Coincident(g1,g0)
    c: Block(g1)
    c: Coincident(g2,g0)
    c: Vertical(g2)
    c: Distance(g2) = 19
    c: Horizontal(g3)
    c: Coincident(g4,g1)
    c: Vertical(g4)
    c: Coincident(g3,g4)
    c: Block(g3)
    c: Coincident(g5,g2)
    c: Coincident(g5,g3)
    c: Block(g0)
    c: Block(g5)
FEATURE [Sketcher::SketchObject] Sketch080  label="topSketch025"
  FullyConstrained = true
  sketch-geometry (6):
    g0: LineSegment StartX=19 StartY=38 StartZ=0 EndX=117 EndY=38 EndZ=0
    g1: ArcOfCircle CenterX=19 CenterY=19 CenterZ=0 NormalX=0 NormalY=0 NormalZ=1 AngleXU=0 Radius=19 StartAngle=1.5708 EndAngle=3.14159
    g2: LineSegment StartX=117 StartY=38 StartZ=0 EndX=117 EndY=19 EndZ=0
    g3: LineSegment StartX=98 StartY=1.0161e-12 StartZ=0 EndX=5.22862e-06 EndY=1.0161e-12 EndZ=0
    g4: LineSegment StartX=5.22862e-06 StartY=19 StartZ=0 EndX=5.22862e-06 EndY=1.0161e-12 EndZ=0
    g5: ArcOfCircle CenterX=98 CenterY=19 CenterZ=0 NormalX=0 NormalY=0 NormalZ=1 AngleXU=0 Radius=19 StartAngle=4.71239 EndAngle=6.28319
  constraints (16):
    c: Horizontal(g0)
    c: Distance(g0) = 98
    c: Coincident(g1,g0)
    c: Block(g1)
    c: Coincident(g2,g0)
    c: Vertical(g2)
    c: Distance(g2) = 19
    c: Horizontal(g3)
    c: Coincident(g4,g1)
    c: Vertical(g4)
    c: Coincident(g3,g4)
    c: Block(g3)
    c: Coincident(g5,g2)
    c: Coincident(g5,g3)
    c: Block(g0)
    c: Block(g5)
FEATURE [Part::Extrusion] Extrude070  label="sideA004"
  Base = -> Sketch080
  Dir = (0,0,1)
  DirMode = 2
  FaceMakerClass = Part::FaceMakerBullseye
  LengthFwd = 3
  LengthRev = 0
  Placement = pos=(0,0,-2.7) rot=(0,0,1;0rad)
  Solid = true
  Symmetric = false
FEATURE [Sketcher::SketchObject] Sketch081
  FullyConstrained = true
  Placement = pos=(117,19,0) rot=(0.57735,0.57735,0.57735;2.0944rad)
  sketch-geometry (8):
    g0: LineSegment StartX=-49.19 StartY=63.5 StartZ=0 EndX=-49.19 EndY=60.5 EndZ=0
    g1: LineSegment StartX=-49.19 StartY=11.5 StartZ=0 EndX=-49.19 EndY=8.5 EndZ=0
    g2: ArcOfCircle CenterX=-1.5 CenterY=62 CenterZ=0 NormalX=0 NormalY=0 NormalZ=1 AngleXU=0 Radius=1.5 StartAngle=4.71239 EndAngle=7.85398
    g3: ArcOfCircle CenterX=-1.5 CenterY=10 CenterZ=0 NormalX=0 NormalY=0 NormalZ=1 AngleXU=0 Radius=1.5 StartAngle=4.71239 EndAngle=7.85398
    g4: LineSegment StartX=-49.19 StartY=63.5 StartZ=0 EndX=-1.5 EndY=63.5 EndZ=0
    g5: LineSegment StartX=-49.19 StartY=60.5 StartZ=0 EndX=-1.5 EndY=60.5 EndZ=0
    g6: LineSegment StartX=-49.19 StartY=11.5 StartZ=0 EndX=-1.5 EndY=11.5 EndZ=0
    g7: LineSegment StartX=-49.19 StartY=8.5 StartZ=0 EndX=-1.5 EndY=8.5 EndZ=0
  constraints (19):
    c: Vertical(g0)
    c: Distance(g0) = 3
    c: Vertical(g1)
    c: Block(g1)
    c: Block(g2)
    c: Block(g3)
    c: Block(g0)
    c: Coincident(g4,g0)
    c: Coincident(g4,g2)
    c: Horizontal(g4)
    c: Coincident(g5,g0)
    c: Coincident(g5,g2)
    c: Horizontal(g5)
    c: Coincident(g6,g1)
    c: Coincident(g6,g3)
    c: Horizontal(g6)
    c: Coincident(g7,g1)
    c: Coincident(g7,g3)
    c: Horizontal(g7)
FEATURE [Part::Extrusion] Extrude071  label="sideB004"
  Base = -> Sketch079
  Dir = (0,0,1)
  DirMode = 2
  FaceMakerClass = Part::FaceMakerBullseye
  LengthFwd = 3
  LengthRev = 0
  Placement = pos=(0,0,71.7) rot=(0,0,1;0rad)
  Solid = true
  Symmetric = false
FEATURE [Part::MultiFuse] Fusion152  label="removeFromBottom004"
  Placement = pos=(2,0,0) rot=(0,0,1;0rad)
  Shapes = -> [Extrude070,Extrude071]
FEATURE [Part::Extrusion] Extrude072
  Base = -> Sketch081
  Dir = (1,0,0)
  DirMode = 2
  FaceMakerClass = Part::FaceMakerBullseye
  LengthFwd = 10
  LengthRev = 0
  Solid = true
  Symmetric = false
FEATURE [Part::Fillet] Fillet059  label="removeFromtMoreFrontCaseScrewRetainers004"
  Base = -> Extrude072
  Edges = 4 edges r=1.49: [Edge6,Edge11,Edge18,Edge23]
  Placement = pos=(-12,0,0) rot=(0,0,1;0rad)
FEATURE [Sketcher::SketchObject] Sketch082
  FullyConstrained = true
  Placement = pos=(117,19,0) rot=(0.57735,0.57735,0.57735;2.0944rad)
  sketch-geometry (8):
    g0: LineSegment StartX=-49.19 StartY=69.25 StartZ=0 EndX=-49.19 EndY=66.25 EndZ=0
    g1: LineSegment StartX=-49.19 StartY=5.75 StartZ=0 EndX=-49.19 EndY=2.75 EndZ=0
    g2: ArcOfCircle CenterX=-1.5 CenterY=67.75 CenterZ=0 NormalX=0 NormalY=0 NormalZ=1 AngleXU=0 Radius=1.5 StartAngle=4.71239 EndAngle=7.85398
    g3: ArcOfCircle CenterX=-1.5 CenterY=4.25 CenterZ=0 NormalX=0 NormalY=0 NormalZ=1 AngleXU=0 Radius=1.5 StartAngle=4.71239 EndAngle=7.85398
    g4: LineSegment StartX=-49.19 StartY=69.25 StartZ=0 EndX=-1.5 EndY=69.25 EndZ=0
    g5: LineSegment StartX=-49.19 StartY=66.25 StartZ=0 EndX=-1.5 EndY=66.25 EndZ=0
    g6: LineSegment StartX=-49.19 StartY=5.75 StartZ=0 EndX=-1.5 EndY=5.75 EndZ=0
    g7: LineSegment StartX=-49.19 StartY=2.75 StartZ=0 EndX=-1.5 EndY=2.75 EndZ=0
  constraints (19):
    c: Vertical(g0)
    c: Distance(g0) = 3
    c: Block(g0)
    c: Vertical(g1)
    c: Block(g2)
    c: Block(g3)
    c: Block(g1)
    c: Coincident(g4,g0)
    c: Coincident(g4,g2)
    c: Horizontal(g4)
    c: Coincident(g5,g0)
    c: Coincident(g5,g2)
    c: Horizontal(g5)
    c: Coincident(g6,g1)
    c: Coincident(g6,g3)
    c: Horizontal(g6)
    c: Coincident(g7,g1)
    c: Coincident(g7,g3)
    c: Horizontal(g7)
FEATURE [Part::Extrusion] Extrude073
  Base = -> Sketch082
  Dir = (1,0,0)
  DirMode = 2
  FaceMakerClass = Part::FaceMakerBullseye
  LengthFwd = 10
  LengthRev = 0
  Solid = true
  Symmetric = false
FEATURE [Part::Fillet] Fillet060  label="removeFromtMoreFrontCaseScrewRetainers005"
  Base = -> Extrude073
  Edges = 4 edges r=1.49: [Edge6,Edge11,Edge18,Edge23]
  Placement = pos=(-4,0,0) rot=(0,0,1;0rad)
FEATURE [Part::Revolution] Revolve163  label="backCaseScrewRetainer004"
  Angle = 360
  Axis = (0,1,0)
  Base = (0,0,0)
  FaceMakerClass = Part::FaceMakerBullseye
  Placement = pos=(12.5,3,62) rot=(0,0,1;0rad)
  Solid = false
  Source = -> Face149
  Symmetric = false
FEATURE [Part::Revolution] Revolve164  label="frontCaseScrewRetainer006"
  Angle = 360
  Axis = (0,1,0)
  Base = (0,0,0)
  FaceMakerClass = Part::FaceMakerBullseye
  Placement = pos=(89.5,3,68.5) rot=(0,0,1;0rad)
  Solid = false
  Source = -> Face151
  Symmetric = false
FEATURE [Part::Revolution] Revolve165  label="frontCaseScrewRetainer007"
  Angle = 360
  Axis = (0,1,0)
  Base = (0,0,0)
  FaceMakerClass = Part::FaceMakerBullseye
  Placement = pos=(89.5,3,3.5) rot=(0,0,1;0rad)
  Solid = false
  Source = -> Face152
  Symmetric = false
FEATURE [Part::Revolution] Revolve166  label="backCaseScrewRetainer005"
  Angle = 360
  Axis = (0,1,0)
  Base = (0,0,0)
  FaceMakerClass = Part::FaceMakerBullseye
  Placement = pos=(12.5,3,10) rot=(0,0,1;0rad)
  Solid = false
  Source = -> Face150
  Symmetric = false
FEATURE [Part::Revolution] Revolve167  label="moreFrontCaseScrewRetainer006"
  Angle = 360
  Axis = (0,1,0)
  Base = (0,0,0)
  FaceMakerClass = Part::FaceMakerBullseye
  Placement = pos=(109.5,4.5,68.5) rot=(0,0,1;0rad)
  Solid = false
  Source = -> Face153
  Symmetric = false
FEATURE [Part::Revolution] Revolve168  label="moreFrontCaseScrewRetainer007"
  Angle = 360
  Axis = (0,1,0)
  Base = (0,0,0)
  FaceMakerClass = Part::FaceMakerBullseye
  Placement = pos=(109.5,4.5,3.5) rot=(0,0,1;0rad)
  Solid = false
  Source = -> Face154
  Symmetric = false
FEATURE [Part::MultiFuse] Fusion151  label="screwRetainers003"
  Shapes = -> [Revolve168,Revolve167,Revolve166,Revolve165,Revolve164,Revolve163]
FEATURE [Part::Cut] Cut069  label="screwRetainers004"
  Base = -> Fusion151
  Tool = -> Fusion152
FEATURE [Part::Cut] Cut070
  Base = -> Cut069
  Tool = -> Fillet060
FEATURE [Part::Cut] Cut071  label="screwPillars001"
  Base = -> Cut070
  Tool = -> Fillet059
FEATURE [Part::MultiFuse] Fusion153  label="bottom024"
  Shapes = -> [Fusion149,Cut071]
FEATURE [Part::Cylinder] Cylinder067
  Angle = 360
  AttacherType = Attacher::AttachEngine3D
  Height = 10
  Placement = pos=(20.65,12,4.68) rot=(1,0,0;1.5708rad)
  Radius = 2
FEATURE [Part::Cylinder] Cylinder068
  Angle = 360
  AttacherType = Attacher::AttachEngine3D
  Height = 10
  Placement = pos=(20.65,12,67.38) rot=(1,0,0;1.5708rad)
  Radius = 2
FEATURE [Part::Cylinder] Cylinder069
  Angle = 360
  AttacherType = Attacher::AttachEngine3D
  Height = 10
  Placement = pos=(77.15,12,67.38) rot=(1,0,0;1.5708rad)
  Radius = 2
FEATURE [Part::Cylinder] Cylinder070
  Angle = 360
  AttacherType = Attacher::AttachEngine3D
  Height = 10
  Placement = pos=(77.15,12,4.68) rot=(1,0,0;1.5708rad)
  Radius = 2
FEATURE [Part::MultiFuse] Fusion154  label="removeFromThreadedInsertHousing001"
  Shapes = -> [Cylinder069,Cylinder068,Cylinder067,Cylinder070]
FEATURE [Part::Cut] Cut072  label="bottom025"
  Base = -> Fusion153
  Tool = -> Fusion154
FEATURE [Image::ImagePlane] ImagePlane
  XSize = 339
  YSize = 72
FEATURE [Sketcher::SketchObject] Sketch083
  FullyConstrained = false
  MapMode = 5
  Support = -> [XY_Plane]
  sketch-geometry (16):
    g0: LineSegment StartX=-151.619 StartY=28.8932 StartZ=0 EndX=-140.819 EndY=28.8932 EndZ=0
    g1: LineSegment StartX=-145.128 StartY=24.0313 StartZ=0 EndX=-151.619 EndY=24.0313 EndZ=0
    g2: LineSegment StartX=-151.619 StartY=24.0313 StartZ=0 EndX=-151.619 EndY=28.8932 EndZ=0
    g3: LineSegment StartX=-140.819 StartY=17.7713 StartZ=0 EndX=-151.619 EndY=17.7713 EndZ=0
    g4: LineSegment StartX=-151.619 StartY=17.7713 StartZ=0 EndX=-151.619 EndY=22.6313 EndZ=0
    g5: LineSegment StartX=-151.619 StartY=22.6313 StartZ=0 EndX=-145.128 EndY=22.6313 EndZ=0
    g6: LineSegment StartX=-145.128 StartY=24.0313 StartZ=0 EndX=-140.819 EndY=28.8932 EndZ=0
    g7: LineSegment StartX=-145.128 StartY=22.6313 StartZ=0 EndX=-140.819 EndY=17.7713 EndZ=0
    g8: LineSegment StartX=-151.619 StartY=28.8932 StartZ=0 EndX=-151.619 EndY=29.2832 EndZ=0
    g9: LineSegment StartX=-151.619 StartY=29.2832 StartZ=0 EndX=-151.619 EndY=35.4532 EndZ=0
    g10: LineSegment StartX=-151.619 StartY=17.7713 StartZ=0 EndX=-151.619 EndY=17.3813 EndZ=0
    g11: LineSegment StartX=-151.619 StartY=17.3813 StartZ=0 EndX=-151.619 EndY=11.2113 EndZ=0
    g12: LineSegment StartX=-151.619 StartY=24.0313 StartZ=0 EndX=-151.619 EndY=23.3313 EndZ=0
    g13: LineSegment StartX=-151.619 StartY=23.3313 StartZ=0 EndX=-155.157 EndY=23.3313 EndZ=0
    g14: ArcOfCircle CenterX=-155.157 CenterY=23.3313 CenterZ=0 NormalX=0 NormalY=0 NormalZ=1 AngleXU=0 Radius=6.92272 StartAngle=1.03441 EndAngle=5.24892
    g15: ArcOfCircle CenterX=-155.157 CenterY=23.3313 CenterZ=0 NormalX=0 NormalY=0 NormalZ=1 AngleXU=0 Radius=12.6278 StartAngle=1.28677 EndAngle=4.99646
  constraints (43):
    c: Coincident(g1,g2)
    c: Coincident(g2,g0)
    c: Horizontal(g0)
    c: Horizontal(g1)
    c: Vertical(g2)
    c: Coincident(g3,g4)
    c: Coincident(g4,g5)
    c: Horizontal(g5)
    c: Horizontal(g3)
    c: Vertical(g4)
    c: Block(g2)
    c: Block(g1)
    c: Distance(g4) = 4.86
    c: Block(g5)
    c: Distance(g0) = 10.8
    c: Distance(g3) = 10.8
    c: Coincident(g6,g1)
    c: Coincident(g6,g0)
    c: Coincident(g7,g5)
    c: Coincident(g7,g3)
    c: Coincident(g8,g0)
    c: Vertical(g8)
    c: Coincident(g9,g8)
    c: Vertical(g9)
    c: Distance(g8) = 0.39
    c: Coincident(g10,g3)
    c: Vertical(g10)
    c: Distance(g10) = 0.39
    c: Distance(g9) = 6.17
    c: Coincident(g11,g10)
    c: Vertical(g11)
    c: Distance(g11) = 6.17
    c: Coincident(g12,g1)
    c: Vertical(g12)
    c: Distance(g12) = 0.7
    c: Coincident(g13,g12)
    c: Horizontal(g13)
    c: Coincident(g14,g13)
    c: Coincident(g14,g10)
    c: Coincident(g14,g8)
    c: Coincident(g15,g13)
    c: Coincident(g15,g9)
    c: Coincident(g15,g11)
FEATURE [PartDesign::Body] Body
  Group = -> [Sketch083]
  Origin = -> Origin
FEATURE [Sketcher::SketchObject] Sketch084
  FullyConstrained = true
  MapMode = 5
  Support = -> [XY_Plane001]
FEATURE [PartDesign::Body] Body001
  Group = -> [Sketch084]
  Origin = -> Origin001
